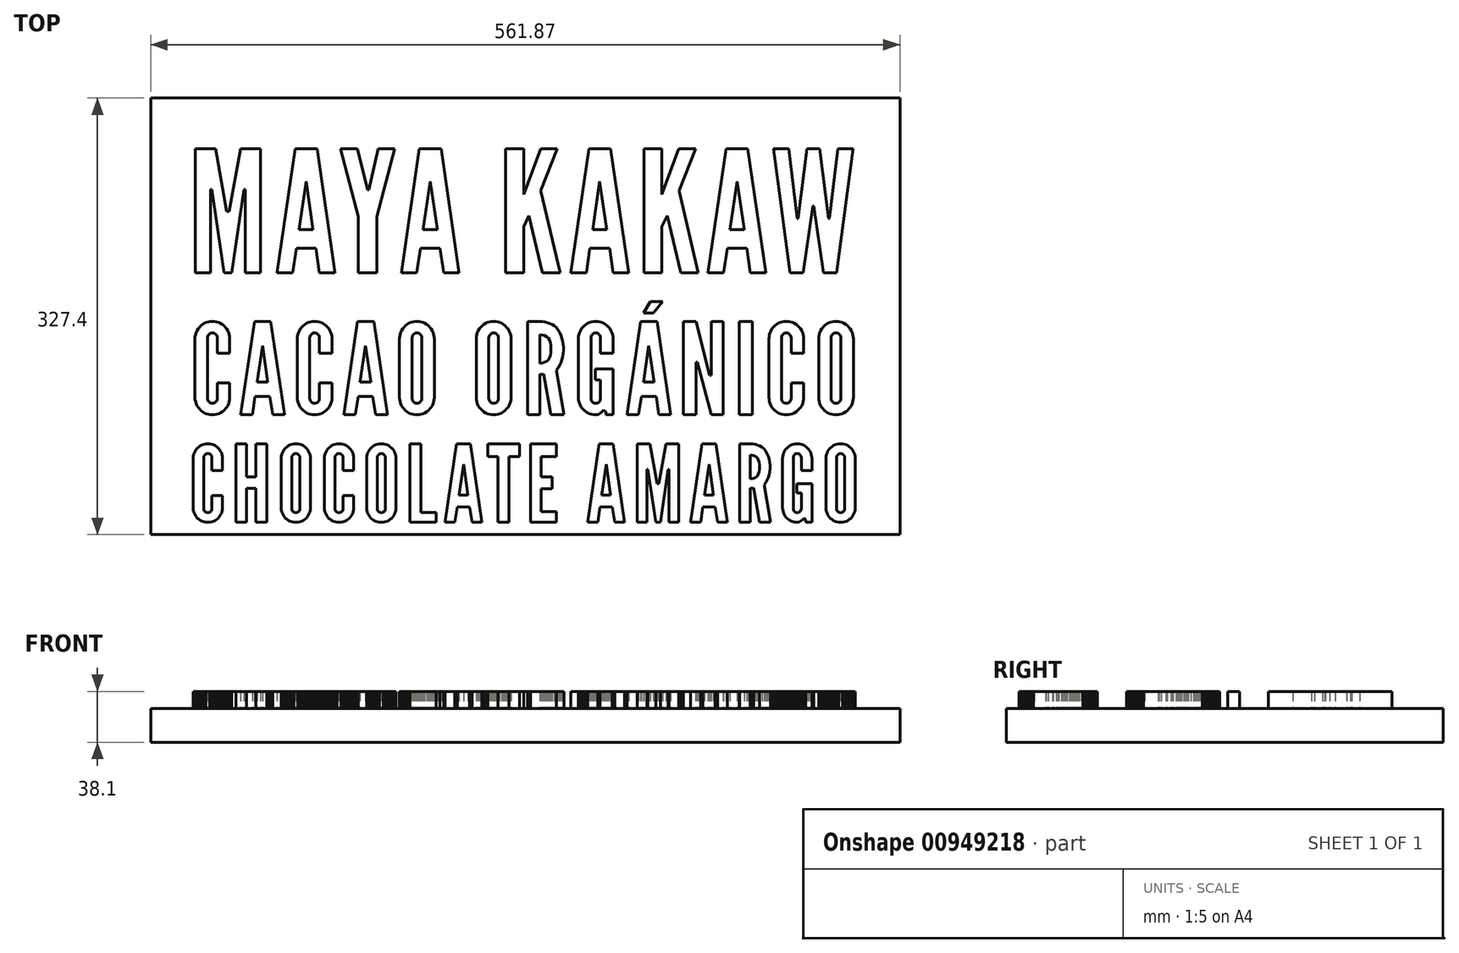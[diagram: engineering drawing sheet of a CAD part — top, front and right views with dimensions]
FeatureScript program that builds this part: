
annotation { "Feature Type Name" : "Feature", "Feature Type Description" : "" }
export const myFeature = defineFeature(function(context is Context, id is Id, definition is map)
    precondition{}
    {
        {
            var Q0;
            Q0=qCreatedBy(makeId("Top.planeOp"),FACE);
            var sketch = newSketch(context, id + "F0", { "sketchPlane" : qUnion([Q0])});
            skLineSegment(sketch, "E0", {"start": v(-116.2, -328.45) * mm, "end": v(-116.2, -376.5) * mm});
            skLineSegment(sketch, "E1", {"start": v(-116.2, -376.5) * mm, "end": v(-116.2, -377.7) * mm});
            skLineSegment(sketch, "E2", {"start": v(-116.2, -377.7) * mm, "end": v(-115.97, -378.89) * mm});
            skLineSegment(sketch, "E3", {"start": v(-115.97, -378.89) * mm, "end": v(-115.65, -379.97) * mm});
            skLineSegment(sketch, "E4", {"start": v(-115.65, -379.97) * mm, "end": v(-115.22, -381.05) * mm});
            skLineSegment(sketch, "E5", {"start": v(-115.22, -381.05) * mm, "end": v(-114.78, -382.02) * mm});
            skLineSegment(sketch, "E6", {"start": v(-114.78, -382.02) * mm, "end": v(-114.14, -383) * mm});
            skLineSegment(sketch, "E7", {"start": v(-114.14, -383) * mm, "end": v(-113.38, -383.86) * mm});
            skLineSegment(sketch, "E8", {"start": v(-113.38, -383.86) * mm, "end": v(-112.62, -384.73) * mm});
            skLineSegment(sketch, "E9", {"start": v(-112.62, -384.73) * mm, "end": v(-111.65, -385.49) * mm});
            skLineSegment(sketch, "E10", {"start": v(-111.65, -385.49) * mm, "end": v(-110.78, -386.03) * mm});
            skLineSegment(sketch, "E11", {"start": v(-110.78, -386.03) * mm, "end": v(-109.7, -386.57) * mm});
            skLineSegment(sketch, "E12", {"start": v(-109.7, -386.57) * mm, "end": v(-108.61, -387) * mm});
            skLineSegment(sketch, "E13", {"start": v(-108.61, -387) * mm, "end": v(-107.53, -387.33) * mm});
            skLineSegment(sketch, "E14", {"start": v(-107.53, -387.33) * mm, "end": v(-106.34, -387.44) * mm});
            skLineSegment(sketch, "E15", {"start": v(-106.34, -387.44) * mm, "end": v(-105.26, -387.54) * mm});
            skLineSegment(sketch, "E16", {"start": v(-105.26, -387.54) * mm, "end": v(-104.07, -387.44) * mm});
            skLineSegment(sketch, "E17", {"start": v(-104.07, -387.44) * mm, "end": v(-102.99, -387.33) * mm});
            skLineSegment(sketch, "E18", {"start": v(-102.99, -387.33) * mm, "end": v(-101.8, -387) * mm});
            skLineSegment(sketch, "E19", {"start": v(-101.8, -387) * mm, "end": v(-100.82, -386.57) * mm});
            skLineSegment(sketch, "E20", {"start": v(-100.82, -386.57) * mm, "end": v(-99.74, -386.03) * mm});
            skLineSegment(sketch, "E21", {"start": v(-99.74, -386.03) * mm, "end": v(-98.76, -385.49) * mm});
            skLineSegment(sketch, "E22", {"start": v(-98.76, -385.49) * mm, "end": v(-97.9, -384.73) * mm});
            skLineSegment(sketch, "E23", {"start": v(-97.9, -384.73) * mm, "end": v(-97.03, -383.86) * mm});
            skLineSegment(sketch, "E24", {"start": v(-97.03, -383.86) * mm, "end": v(-96.38, -383) * mm});
            skLineSegment(sketch, "E25", {"start": v(-96.38, -383) * mm, "end": v(-95.73, -382.02) * mm});
            skLineSegment(sketch, "E26", {"start": v(-95.73, -382.02) * mm, "end": v(-95.2, -381.05) * mm});
            skLineSegment(sketch, "E27", {"start": v(-95.2, -381.05) * mm, "end": v(-94.76, -379.97) * mm});
            skLineSegment(sketch, "E28", {"start": v(-94.76, -379.97) * mm, "end": v(-94.54, -378.89) * mm});
            skLineSegment(sketch, "E29", {"start": v(-94.54, -378.89) * mm, "end": v(-94.33, -377.7) * mm});
            skLineSegment(sketch, "E30", {"start": v(-94.33, -377.7) * mm, "end": v(-94.22, -376.5) * mm});
            skLineSegment(sketch, "E31", {"start": v(-94.22, -376.5) * mm, "end": v(-94.22, -328.45) * mm});
            skLineSegment(sketch, "E32", {"start": v(-94.22, -328.45) * mm, "end": v(-102.23, -328.45) * mm});
            skLineSegment(sketch, "E33", {"start": v(-102.23, -328.45) * mm, "end": v(-102.23, -377.15) * mm});
            skLineSegment(sketch, "E34", {"start": v(-108.3, -377.15) * mm, "end": v(-108.18, -377.8) * mm});
            skLineSegment(sketch, "E35", {"start": v(-108.18, -377.8) * mm, "end": v(-108.08, -378.34) * mm});
            skLineSegment(sketch, "E36", {"start": v(-108.08, -378.34) * mm, "end": v(-107.75, -378.89) * mm});
            skLineSegment(sketch, "E37", {"start": v(-107.75, -378.89) * mm, "end": v(-107.43, -379.32) * mm});
            skLineSegment(sketch, "E38", {"start": v(-107.43, -379.32) * mm, "end": v(-106.88, -379.75) * mm});
            skLineSegment(sketch, "E39", {"start": v(-106.88, -379.75) * mm, "end": v(-106.45, -379.97) * mm});
            skLineSegment(sketch, "E40", {"start": v(-106.45, -379.97) * mm, "end": v(-105.8, -380.18) * mm});
            skLineSegment(sketch, "E41", {"start": v(-105.8, -380.18) * mm, "end": v(-104.61, -380.18) * mm});
            skLineSegment(sketch, "E42", {"start": v(-104.61, -380.18) * mm, "end": v(-104.07, -379.97) * mm});
            skLineSegment(sketch, "E43", {"start": v(-104.07, -379.97) * mm, "end": v(-103.53, -379.75) * mm});
            skLineSegment(sketch, "E44", {"start": v(-103.53, -379.75) * mm, "end": v(-103.1, -379.32) * mm});
            skLineSegment(sketch, "E45", {"start": v(-103.1, -379.32) * mm, "end": v(-102.66, -378.89) * mm});
            skLineSegment(sketch, "E46", {"start": v(-102.66, -378.89) * mm, "end": v(-102.23, -377.8) * mm});
            skLineSegment(sketch, "E47", {"start": v(-102.23, -377.8) * mm, "end": v(-102.23, -377.15) * mm});
            skLineSegment(sketch, "E48", {"start": v(-108.3, -377.15) * mm, "end": v(-108.3, -328.45) * mm});
            skLineSegment(sketch, "E49", {"start": v(-108.3, -328.45) * mm, "end": v(-116.2, -328.45) * mm});
            skLineSegment(sketch, "E50", {"start": v(9.9, -341.44) * mm, "end": v(9.9, -375.1) * mm});
            skLineSegment(sketch, "E51", {"start": v(3.95, -380.3) * mm, "end": v(4.82, -380.18) * mm});
            skLineSegment(sketch, "E52", {"start": v(4.82, -380.18) * mm, "end": v(5.8, -379.97) * mm});
            skLineSegment(sketch, "E53", {"start": v(5.8, -379.97) * mm, "end": v(6.66, -379.54) * mm});
            skLineSegment(sketch, "E54", {"start": v(6.66, -379.54) * mm, "end": v(7.42, -379) * mm});
            skLineSegment(sketch, "E55", {"start": v(7.42, -379) * mm, "end": v(8.17, -378.45) * mm});
            skLineSegment(sketch, "E56", {"start": v(8.17, -378.45) * mm, "end": v(8.82, -377.7) * mm});
            skLineSegment(sketch, "E57", {"start": v(8.82, -377.7) * mm, "end": v(9.25, -376.94) * mm});
            skLineSegment(sketch, "E58", {"start": v(9.25, -376.94) * mm, "end": v(9.69, -376.07) * mm});
            skLineSegment(sketch, "E59", {"start": v(9.69, -376.07) * mm, "end": v(9.9, -375.1) * mm});
            skLineSegment(sketch, "E60", {"start": v(3.95, -380.3) * mm, "end": v(3.2, -380.3) * mm});
            skLineSegment(sketch, "E61", {"start": v(3.2, -380.3) * mm, "end": v(3.2, -336.24) * mm});
            skLineSegment(sketch, "E62", {"start": v(3.2, -336.24) * mm, "end": v(3.95, -336.24) * mm});
            skLineSegment(sketch, "E63", {"start": v(9.9, -341.44) * mm, "end": v(9.69, -340.46) * mm});
            skLineSegment(sketch, "E64", {"start": v(9.69, -340.46) * mm, "end": v(9.25, -339.6) * mm});
            skLineSegment(sketch, "E65", {"start": v(9.25, -339.6) * mm, "end": v(8.82, -338.84) * mm});
            skLineSegment(sketch, "E66", {"start": v(8.82, -338.84) * mm, "end": v(8.17, -338.08) * mm});
            skLineSegment(sketch, "E67", {"start": v(8.17, -338.08) * mm, "end": v(7.42, -337.43) * mm});
            skLineSegment(sketch, "E68", {"start": v(7.42, -337.43) * mm, "end": v(6.66, -337) * mm});
            skLineSegment(sketch, "E69", {"start": v(6.66, -337) * mm, "end": v(5.8, -336.56) * mm});
            skLineSegment(sketch, "E70", {"start": v(5.8, -336.56) * mm, "end": v(4.82, -336.35) * mm});
            skLineSegment(sketch, "E71", {"start": v(4.82, -336.35) * mm, "end": v(3.95, -336.24) * mm});
            skLineSegment(sketch, "E72", {"start": v(-5.36, -328.45) * mm, "end": v(-5.36, -387.98) * mm});
            skLineSegment(sketch, "E73", {"start": v(-5.36, -387.98) * mm, "end": v(8.6, -387.98) * mm});
            skLineSegment(sketch, "E74", {"start": v(8.6, -387.98) * mm, "end": v(9.9, -387.44) * mm});
            skLineSegment(sketch, "E75", {"start": v(9.9, -387.44) * mm, "end": v(11.2, -386.79) * mm});
            skLineSegment(sketch, "E76", {"start": v(11.2, -386.79) * mm, "end": v(12.4, -386.03) * mm});
            skLineSegment(sketch, "E77", {"start": v(12.4, -386.03) * mm, "end": v(13.48, -385.16) * mm});
            skLineSegment(sketch, "E78", {"start": v(13.48, -385.16) * mm, "end": v(14.45, -384.19) * mm});
            skLineSegment(sketch, "E79", {"start": v(14.45, -384.19) * mm, "end": v(15.42, -383.1) * mm});
            skLineSegment(sketch, "E80", {"start": v(15.42, -383.1) * mm, "end": v(16.3, -382.02) * mm});
            skLineSegment(sketch, "E81", {"start": v(16.3, -382.02) * mm, "end": v(16.94, -380.73) * mm});
            skLineSegment(sketch, "E82", {"start": v(16.94, -380.73) * mm, "end": v(17.59, -379.54) * mm});
            skLineSegment(sketch, "E83", {"start": v(17.59, -379.54) * mm, "end": v(18.13, -378.13) * mm});
            skLineSegment(sketch, "E84", {"start": v(18.13, -378.13) * mm, "end": v(18.46, -376.83) * mm});
            skLineSegment(sketch, "E85", {"start": v(18.46, -376.83) * mm, "end": v(18.46, -339.7) * mm});
            skLineSegment(sketch, "E86", {"start": v(18.46, -339.7) * mm, "end": v(18.13, -338.3) * mm});
            skLineSegment(sketch, "E87", {"start": v(18.13, -338.3) * mm, "end": v(17.59, -337) * mm});
            skLineSegment(sketch, "E88", {"start": v(17.59, -337) * mm, "end": v(16.94, -335.7) * mm});
            skLineSegment(sketch, "E89", {"start": v(16.94, -335.7) * mm, "end": v(16.3, -334.5) * mm});
            skLineSegment(sketch, "E90", {"start": v(16.3, -334.5) * mm, "end": v(15.42, -333.43) * mm});
            skLineSegment(sketch, "E91", {"start": v(15.42, -333.43) * mm, "end": v(14.45, -332.34) * mm});
            skLineSegment(sketch, "E92", {"start": v(14.45, -332.34) * mm, "end": v(13.48, -331.37) * mm});
            skLineSegment(sketch, "E93", {"start": v(13.48, -331.37) * mm, "end": v(12.4, -330.5) * mm});
            skLineSegment(sketch, "E94", {"start": v(12.4, -330.5) * mm, "end": v(11.2, -329.75) * mm});
            skLineSegment(sketch, "E95", {"start": v(11.2, -329.75) * mm, "end": v(9.9, -329.1) * mm});
            skLineSegment(sketch, "E96", {"start": v(9.9, -329.1) * mm, "end": v(8.6, -328.45) * mm});
            skLineSegment(sketch, "E97", {"start": v(8.6, -328.45) * mm, "end": v(-5.36, -328.45) * mm});
            skLineSegment(sketch, "E98", {"start": v(-135.57, -338.84) * mm, "end": v(-135.57, -377.15) * mm});
            skLineSegment(sketch, "E99", {"start": v(-141.63, -377.15) * mm, "end": v(-141.63, -377.8) * mm});
            skLineSegment(sketch, "E100", {"start": v(-141.63, -377.8) * mm, "end": v(-141.41, -378.34) * mm});
            skLineSegment(sketch, "E101", {"start": v(-141.41, -378.34) * mm, "end": v(-141.09, -378.89) * mm});
            skLineSegment(sketch, "E102", {"start": v(-141.09, -378.89) * mm, "end": v(-140.76, -379.32) * mm});
            skLineSegment(sketch, "E103", {"start": v(-140.76, -379.32) * mm, "end": v(-140.33, -379.75) * mm});
            skLineSegment(sketch, "E104", {"start": v(-140.33, -379.75) * mm, "end": v(-139.79, -379.97) * mm});
            skLineSegment(sketch, "E105", {"start": v(-139.79, -379.97) * mm, "end": v(-139.14, -380.18) * mm});
            skLineSegment(sketch, "E106", {"start": v(-139.14, -380.18) * mm, "end": v(-137.95, -380.18) * mm});
            skLineSegment(sketch, "E107", {"start": v(-137.95, -380.18) * mm, "end": v(-136.86, -379.75) * mm});
            skLineSegment(sketch, "E108", {"start": v(-136.86, -379.75) * mm, "end": v(-136, -378.89) * mm});
            skLineSegment(sketch, "E109", {"start": v(-136, -378.89) * mm, "end": v(-135.57, -377.8) * mm});
            skLineSegment(sketch, "E110", {"start": v(-135.57, -377.8) * mm, "end": v(-135.57, -377.15) * mm});
            skLineSegment(sketch, "E111", {"start": v(-141.63, -377.15) * mm, "end": v(-141.63, -338.84) * mm});
            skLineSegment(sketch, "E112", {"start": v(-135.57, -338.84) * mm, "end": v(-135.57, -338.3) * mm});
            skLineSegment(sketch, "E113", {"start": v(-135.57, -338.3) * mm, "end": v(-135.78, -337.65) * mm});
            skLineSegment(sketch, "E114", {"start": v(-135.78, -337.65) * mm, "end": v(-136, -337.21) * mm});
            skLineSegment(sketch, "E115", {"start": v(-136, -337.21) * mm, "end": v(-136.43, -336.67) * mm});
            skLineSegment(sketch, "E116", {"start": v(-136.43, -336.67) * mm, "end": v(-136.86, -336.35) * mm});
            skLineSegment(sketch, "E117", {"start": v(-136.86, -336.35) * mm, "end": v(-137.4, -336.02) * mm});
            skLineSegment(sketch, "E118", {"start": v(-137.4, -336.02) * mm, "end": v(-137.95, -335.91) * mm});
            skLineSegment(sketch, "E119", {"start": v(-137.95, -335.91) * mm, "end": v(-138.6, -335.8) * mm});
            skLineSegment(sketch, "E120", {"start": v(-138.6, -335.8) * mm, "end": v(-139.14, -335.91) * mm});
            skLineSegment(sketch, "E121", {"start": v(-139.14, -335.91) * mm, "end": v(-139.79, -336.02) * mm});
            skLineSegment(sketch, "E122", {"start": v(-139.79, -336.02) * mm, "end": v(-140.33, -336.35) * mm});
            skLineSegment(sketch, "E123", {"start": v(-140.33, -336.35) * mm, "end": v(-140.76, -336.67) * mm});
            skLineSegment(sketch, "E124", {"start": v(-140.76, -336.67) * mm, "end": v(-141.09, -337.21) * mm});
            skLineSegment(sketch, "E125", {"start": v(-141.09, -337.21) * mm, "end": v(-141.41, -337.65) * mm});
            skLineSegment(sketch, "E126", {"start": v(-141.41, -337.65) * mm, "end": v(-141.63, -338.3) * mm});
            skLineSegment(sketch, "E127", {"start": v(-141.63, -338.3) * mm, "end": v(-141.63, -338.84) * mm});
            skLineSegment(sketch, "E128", {"start": v(-149.53, -376.5) * mm, "end": v(-149.53, -339.49) * mm});
            skLineSegment(sketch, "E129", {"start": v(-127.55, -339.49) * mm, "end": v(-127.66, -338.3) * mm});
            skLineSegment(sketch, "E130", {"start": v(-127.66, -338.3) * mm, "end": v(-128.1, -336.13) * mm});
            skLineSegment(sketch, "E131", {"start": v(-128.1, -336.13) * mm, "end": v(-128.53, -335.05) * mm});
            skLineSegment(sketch, "E132", {"start": v(-128.53, -335.05) * mm, "end": v(-129.07, -333.97) * mm});
            skLineSegment(sketch, "E133", {"start": v(-129.07, -333.97) * mm, "end": v(-129.72, -333) * mm});
            skLineSegment(sketch, "E134", {"start": v(-129.72, -333) * mm, "end": v(-130.48, -332.13) * mm});
            skLineSegment(sketch, "E135", {"start": v(-130.48, -332.13) * mm, "end": v(-131.24, -331.37) * mm});
            skLineSegment(sketch, "E136", {"start": v(-131.24, -331.37) * mm, "end": v(-132.1, -330.61) * mm});
            skLineSegment(sketch, "E137", {"start": v(-132.1, -330.61) * mm, "end": v(-133.08, -329.96) * mm});
            skLineSegment(sketch, "E138", {"start": v(-133.08, -329.96) * mm, "end": v(-134.16, -329.42) * mm});
            skLineSegment(sketch, "E139", {"start": v(-134.16, -329.42) * mm, "end": v(-135.24, -328.99) * mm});
            skLineSegment(sketch, "E140", {"start": v(-135.24, -328.99) * mm, "end": v(-136.33, -328.77) * mm});
            skLineSegment(sketch, "E141", {"start": v(-136.33, -328.77) * mm, "end": v(-137.4, -328.56) * mm});
            skLineSegment(sketch, "E142", {"start": v(-137.4, -328.56) * mm, "end": v(-138.6, -328.45) * mm});
            skLineSegment(sketch, "E143", {"start": v(-138.6, -328.45) * mm, "end": v(-139.79, -328.56) * mm});
            skLineSegment(sketch, "E144", {"start": v(-139.79, -328.56) * mm, "end": v(-140.87, -328.77) * mm});
            skLineSegment(sketch, "E145", {"start": v(-140.87, -328.77) * mm, "end": v(-141.95, -328.99) * mm});
            skLineSegment(sketch, "E146", {"start": v(-141.95, -328.99) * mm, "end": v(-143.03, -329.42) * mm});
            skLineSegment(sketch, "E147", {"start": v(-143.03, -329.42) * mm, "end": v(-144.12, -329.96) * mm});
            skLineSegment(sketch, "E148", {"start": v(-144.12, -329.96) * mm, "end": v(-145.1, -330.61) * mm});
            skLineSegment(sketch, "E149", {"start": v(-145.1, -330.61) * mm, "end": v(-145.96, -331.37) * mm});
            skLineSegment(sketch, "E150", {"start": v(-145.96, -331.37) * mm, "end": v(-146.71, -332.13) * mm});
            skLineSegment(sketch, "E151", {"start": v(-146.71, -332.13) * mm, "end": v(-147.47, -333) * mm});
            skLineSegment(sketch, "E152", {"start": v(-147.47, -333) * mm, "end": v(-148.12, -333.97) * mm});
            skLineSegment(sketch, "E153", {"start": v(-148.12, -333.97) * mm, "end": v(-148.66, -335.05) * mm});
            skLineSegment(sketch, "E154", {"start": v(-148.66, -335.05) * mm, "end": v(-148.99, -336.13) * mm});
            skLineSegment(sketch, "E155", {"start": v(-148.99, -336.13) * mm, "end": v(-149.31, -337.21) * mm});
            skLineSegment(sketch, "E156", {"start": v(-149.31, -337.21) * mm, "end": v(-149.53, -338.3) * mm});
            skLineSegment(sketch, "E157", {"start": v(-149.53, -338.3) * mm, "end": v(-149.53, -339.49) * mm});
            skLineSegment(sketch, "E158", {"start": v(-127.55, -339.49) * mm, "end": v(-127.55, -376.5) * mm});
            skLineSegment(sketch, "E159", {"start": v(-129.29, -382.35) * mm, "end": v(-128.64, -381.27) * mm});
            skLineSegment(sketch, "E160", {"start": v(-128.64, -381.27) * mm, "end": v(-128.2, -380.08) * mm});
            skLineSegment(sketch, "E161", {"start": v(-128.2, -380.08) * mm, "end": v(-127.88, -379) * mm});
            skLineSegment(sketch, "E162", {"start": v(-127.88, -379) * mm, "end": v(-127.66, -377.8) * mm});
            skLineSegment(sketch, "E163", {"start": v(-127.66, -377.8) * mm, "end": v(-127.55, -376.5) * mm});
            skLineSegment(sketch, "E164", {"start": v(-129.29, -382.35) * mm, "end": v(-128.2, -383.43) * mm});
            skLineSegment(sketch, "E165", {"start": v(-128.2, -383.43) * mm, "end": v(-127.55, -383.97) * mm});
            skLineSegment(sketch, "E166", {"start": v(-127.55, -383.97) * mm, "end": v(-126.8, -384.3) * mm});
            skLineSegment(sketch, "E167", {"start": v(-126.8, -384.3) * mm, "end": v(-126.04, -384.51) * mm});
            skLineSegment(sketch, "E168", {"start": v(-126.04, -384.51) * mm, "end": v(-126.04, -391.55) * mm});
            skLineSegment(sketch, "E169", {"start": v(-134.05, -386.57) * mm, "end": v(-133.4, -387.44) * mm});
            skLineSegment(sketch, "E170", {"start": v(-133.4, -387.44) * mm, "end": v(-132.75, -388.3) * mm});
            skLineSegment(sketch, "E171", {"start": v(-132.75, -388.3) * mm, "end": v(-131.89, -389.06) * mm});
            skLineSegment(sketch, "E172", {"start": v(-131.89, -389.06) * mm, "end": v(-131.13, -389.7) * mm});
            skLineSegment(sketch, "E173", {"start": v(-131.13, -389.7) * mm, "end": v(-130.16, -390.25) * mm});
            skLineSegment(sketch, "E174", {"start": v(-130.16, -390.25) * mm, "end": v(-129.18, -390.8) * mm});
            skLineSegment(sketch, "E175", {"start": v(-129.18, -390.8) * mm, "end": v(-128.2, -391.12) * mm});
            skLineSegment(sketch, "E176", {"start": v(-128.2, -391.12) * mm, "end": v(-127.12, -391.33) * mm});
            skLineSegment(sketch, "E177", {"start": v(-127.12, -391.33) * mm, "end": v(-126.04, -391.55) * mm});
            skLineSegment(sketch, "E178", {"start": v(-149.53, -376.5) * mm, "end": v(-149.53, -377.7) * mm});
            skLineSegment(sketch, "E179", {"start": v(-149.53, -377.7) * mm, "end": v(-149.31, -378.89) * mm});
            skLineSegment(sketch, "E180", {"start": v(-149.31, -378.89) * mm, "end": v(-148.99, -379.97) * mm});
            skLineSegment(sketch, "E181", {"start": v(-148.99, -379.97) * mm, "end": v(-148.66, -381.05) * mm});
            skLineSegment(sketch, "E182", {"start": v(-148.66, -381.05) * mm, "end": v(-148.12, -382.02) * mm});
            skLineSegment(sketch, "E183", {"start": v(-148.12, -382.02) * mm, "end": v(-147.47, -383) * mm});
            skLineSegment(sketch, "E184", {"start": v(-147.47, -383) * mm, "end": v(-146.71, -383.97) * mm});
            skLineSegment(sketch, "E185", {"start": v(-146.71, -383.97) * mm, "end": v(-145.85, -384.73) * mm});
            skLineSegment(sketch, "E186", {"start": v(-145.85, -384.73) * mm, "end": v(-144.98, -385.49) * mm});
            skLineSegment(sketch, "E187", {"start": v(-144.98, -385.49) * mm, "end": v(-144, -386.14) * mm});
            skLineSegment(sketch, "E188", {"start": v(-144, -386.14) * mm, "end": v(-143.03, -386.57) * mm});
            skLineSegment(sketch, "E189", {"start": v(-143.03, -386.57) * mm, "end": v(-141.95, -387) * mm});
            skLineSegment(sketch, "E190", {"start": v(-141.95, -387) * mm, "end": v(-140.76, -387.33) * mm});
            skLineSegment(sketch, "E191", {"start": v(-140.76, -387.33) * mm, "end": v(-139.68, -387.44) * mm});
            skLineSegment(sketch, "E192", {"start": v(-139.68, -387.44) * mm, "end": v(-138.49, -387.54) * mm});
            skLineSegment(sketch, "E193", {"start": v(-138.49, -387.54) * mm, "end": v(-137.3, -387.44) * mm});
            skLineSegment(sketch, "E194", {"start": v(-137.3, -387.44) * mm, "end": v(-136.22, -387.33) * mm});
            skLineSegment(sketch, "E195", {"start": v(-136.22, -387.33) * mm, "end": v(-135.13, -387) * mm});
            skLineSegment(sketch, "E196", {"start": v(-135.13, -387) * mm, "end": v(-134.05, -386.57) * mm});
            skLineSegment(sketch, "E197", {"start": v(-167.06, -338.84) * mm, "end": v(-167.06, -343.7) * mm});
            skLineSegment(sketch, "E198", {"start": v(-167.06, -343.7) * mm, "end": v(-159.16, -343.7) * mm});
            skLineSegment(sketch, "E199", {"start": v(-159.16, -343.7) * mm, "end": v(-159.16, -339.49) * mm});
            skLineSegment(sketch, "E200", {"start": v(-159.16, -339.49) * mm, "end": v(-159.16, -338.3) * mm});
            skLineSegment(sketch, "E201", {"start": v(-159.16, -338.3) * mm, "end": v(-159.38, -337.21) * mm});
            skLineSegment(sketch, "E202", {"start": v(-159.38, -337.21) * mm, "end": v(-159.7, -336.13) * mm});
            skLineSegment(sketch, "E203", {"start": v(-159.7, -336.13) * mm, "end": v(-160.03, -335.05) * mm});
            skLineSegment(sketch, "E204", {"start": v(-160.03, -335.05) * mm, "end": v(-160.57, -333.97) * mm});
            skLineSegment(sketch, "E205", {"start": v(-160.57, -333.97) * mm, "end": v(-161.22, -333) * mm});
            skLineSegment(sketch, "E206", {"start": v(-161.22, -333) * mm, "end": v(-161.97, -332.13) * mm});
            skLineSegment(sketch, "E207", {"start": v(-161.97, -332.13) * mm, "end": v(-162.73, -331.37) * mm});
            skLineSegment(sketch, "E208", {"start": v(-162.73, -331.37) * mm, "end": v(-163.7, -330.61) * mm});
            skLineSegment(sketch, "E209", {"start": v(-163.7, -330.61) * mm, "end": v(-164.58, -329.96) * mm});
            skLineSegment(sketch, "E210", {"start": v(-164.58, -329.96) * mm, "end": v(-165.65, -329.42) * mm});
            skLineSegment(sketch, "E211", {"start": v(-165.65, -329.42) * mm, "end": v(-166.74, -328.99) * mm});
            skLineSegment(sketch, "E212", {"start": v(-166.74, -328.99) * mm, "end": v(-167.82, -328.77) * mm});
            skLineSegment(sketch, "E213", {"start": v(-167.82, -328.77) * mm, "end": v(-169.01, -328.56) * mm});
            skLineSegment(sketch, "E214", {"start": v(-169.01, -328.56) * mm, "end": v(-170.1, -328.45) * mm});
            skLineSegment(sketch, "E215", {"start": v(-170.1, -328.45) * mm, "end": v(-171.28, -328.56) * mm});
            skLineSegment(sketch, "E216", {"start": v(-171.28, -328.56) * mm, "end": v(-172.37, -328.77) * mm});
            skLineSegment(sketch, "E217", {"start": v(-172.37, -328.77) * mm, "end": v(-173.45, -328.99) * mm});
            skLineSegment(sketch, "E218", {"start": v(-173.45, -328.99) * mm, "end": v(-174.53, -329.42) * mm});
            skLineSegment(sketch, "E219", {"start": v(-174.53, -329.42) * mm, "end": v(-175.61, -329.96) * mm});
            skLineSegment(sketch, "E220", {"start": v(-175.61, -329.96) * mm, "end": v(-176.59, -330.61) * mm});
            skLineSegment(sketch, "E221", {"start": v(-176.59, -330.61) * mm, "end": v(-177.46, -331.37) * mm});
            skLineSegment(sketch, "E222", {"start": v(-177.46, -331.37) * mm, "end": v(-178.32, -332.13) * mm});
            skLineSegment(sketch, "E223", {"start": v(-178.32, -332.13) * mm, "end": v(-178.97, -333) * mm});
            skLineSegment(sketch, "E224", {"start": v(-178.97, -333) * mm, "end": v(-179.62, -333.97) * mm});
            skLineSegment(sketch, "E225", {"start": v(-179.62, -333.97) * mm, "end": v(-180.16, -335.05) * mm});
            skLineSegment(sketch, "E226", {"start": v(-180.16, -335.05) * mm, "end": v(-180.6, -336.13) * mm});
            skLineSegment(sketch, "E227", {"start": v(-180.6, -336.13) * mm, "end": v(-180.8, -337.21) * mm});
            skLineSegment(sketch, "E228", {"start": v(-180.8, -337.21) * mm, "end": v(-181.03, -338.3) * mm});
            skLineSegment(sketch, "E229", {"start": v(-181.03, -338.3) * mm, "end": v(-181.13, -339.49) * mm});
            skLineSegment(sketch, "E230", {"start": v(-181.13, -339.49) * mm, "end": v(-181.13, -343.7) * mm});
            skLineSegment(sketch, "E231", {"start": v(-181.13, -343.7) * mm, "end": v(-180.38, -346.09) * mm});
            skLineSegment(sketch, "E232", {"start": v(-180.38, -346.09) * mm, "end": v(-179.51, -348.36) * mm});
            skLineSegment(sketch, "E233", {"start": v(-179.51, -348.36) * mm, "end": v(-178.54, -350.63) * mm});
            skLineSegment(sketch, "E234", {"start": v(-178.54, -350.63) * mm, "end": v(-177.46, -352.8) * mm});
            skLineSegment(sketch, "E235", {"start": v(-177.46, -352.8) * mm, "end": v(-176.26, -354.96) * mm});
            skLineSegment(sketch, "E236", {"start": v(-176.26, -354.96) * mm, "end": v(-174.86, -357.02) * mm});
            skLineSegment(sketch, "E237", {"start": v(-174.86, -357.02) * mm, "end": v(-173.34, -358.97) * mm});
            skLineSegment(sketch, "E238", {"start": v(-166.52, -370.66) * mm, "end": v(-168.69, -366.65) * mm});
            skLineSegment(sketch, "E239", {"start": v(-168.69, -366.65) * mm, "end": v(-170.96, -362.87) * mm});
            skLineSegment(sketch, "E240", {"start": v(-170.96, -362.87) * mm, "end": v(-173.34, -358.97) * mm});
            skLineSegment(sketch, "E241", {"start": v(-166.52, -370.66) * mm, "end": v(-166.52, -376.18) * mm});
            skLineSegment(sketch, "E242", {"start": v(-174.53, -377.15) * mm, "end": v(-174.31, -377.8) * mm});
            skLineSegment(sketch, "E243", {"start": v(-174.31, -377.8) * mm, "end": v(-174, -378.45) * mm});
            skLineSegment(sketch, "E244", {"start": v(-174, -378.45) * mm, "end": v(-173.56, -379) * mm});
            skLineSegment(sketch, "E245", {"start": v(-173.56, -379) * mm, "end": v(-173.02, -379.43) * mm});
            skLineSegment(sketch, "E246", {"start": v(-173.02, -379.43) * mm, "end": v(-172.47, -379.86) * mm});
            skLineSegment(sketch, "E247", {"start": v(-172.47, -379.86) * mm, "end": v(-171.82, -380.08) * mm});
            skLineSegment(sketch, "E248", {"start": v(-171.82, -380.08) * mm, "end": v(-171.07, -380.3) * mm});
            skLineSegment(sketch, "E249", {"start": v(-171.07, -380.3) * mm, "end": v(-170.42, -380.3) * mm});
            skLineSegment(sketch, "E250", {"start": v(-170.42, -380.3) * mm, "end": v(-169.77, -380.18) * mm});
            skLineSegment(sketch, "E251", {"start": v(-169.77, -380.18) * mm, "end": v(-169.01, -379.97) * mm});
            skLineSegment(sketch, "E252", {"start": v(-169.01, -379.97) * mm, "end": v(-168.47, -379.75) * mm});
            skLineSegment(sketch, "E253", {"start": v(-168.47, -379.75) * mm, "end": v(-167.82, -379.32) * mm});
            skLineSegment(sketch, "E254", {"start": v(-167.82, -379.32) * mm, "end": v(-167.39, -378.78) * mm});
            skLineSegment(sketch, "E255", {"start": v(-167.39, -378.78) * mm, "end": v(-166.96, -378.23) * mm});
            skLineSegment(sketch, "E256", {"start": v(-166.96, -378.23) * mm, "end": v(-166.74, -377.59) * mm});
            skLineSegment(sketch, "E257", {"start": v(-166.74, -377.59) * mm, "end": v(-166.52, -376.94) * mm});
            skLineSegment(sketch, "E258", {"start": v(-166.52, -376.94) * mm, "end": v(-166.52, -376.18) * mm});
            skLineSegment(sketch, "E259", {"start": v(-174.53, -377.15) * mm, "end": v(-174.53, -370.66) * mm});
            skLineSegment(sketch, "E260", {"start": v(-174.53, -370.66) * mm, "end": v(-182.32, -370.66) * mm});
            skLineSegment(sketch, "E261", {"start": v(-182.32, -370.66) * mm, "end": v(-182.32, -376.5) * mm});
            skLineSegment(sketch, "E262", {"start": v(-182.32, -376.5) * mm, "end": v(-182.22, -377.8) * mm});
            skLineSegment(sketch, "E263", {"start": v(-182.22, -377.8) * mm, "end": v(-182, -379) * mm});
            skLineSegment(sketch, "E264", {"start": v(-182, -379) * mm, "end": v(-181.57, -380.08) * mm});
            skLineSegment(sketch, "E265", {"start": v(-181.57, -380.08) * mm, "end": v(-181.13, -381.27) * mm});
            skLineSegment(sketch, "E266", {"start": v(-181.13, -381.27) * mm, "end": v(-180.49, -382.24) * mm});
            skLineSegment(sketch, "E267", {"start": v(-180.49, -382.24) * mm, "end": v(-179.73, -383.21) * mm});
            skLineSegment(sketch, "E268", {"start": v(-179.73, -383.21) * mm, "end": v(-178.97, -384.19) * mm});
            skLineSegment(sketch, "E269", {"start": v(-178.97, -384.19) * mm, "end": v(-178.1, -384.95) * mm});
            skLineSegment(sketch, "E270", {"start": v(-178.1, -384.95) * mm, "end": v(-177.02, -385.7) * mm});
            skLineSegment(sketch, "E271", {"start": v(-177.02, -385.7) * mm, "end": v(-176.05, -386.25) * mm});
            skLineSegment(sketch, "E272", {"start": v(-176.05, -386.25) * mm, "end": v(-174.86, -386.79) * mm});
            skLineSegment(sketch, "E273", {"start": v(-174.86, -386.79) * mm, "end": v(-173.78, -387.11) * mm});
            skLineSegment(sketch, "E274", {"start": v(-173.78, -387.11) * mm, "end": v(-172.58, -387.44) * mm});
            skLineSegment(sketch, "E275", {"start": v(-172.58, -387.44) * mm, "end": v(-171.4, -387.54) * mm});
            skLineSegment(sketch, "E276", {"start": v(-171.4, -387.54) * mm, "end": v(-170.1, -387.54) * mm});
            skLineSegment(sketch, "E277", {"start": v(-170.1, -387.54) * mm, "end": v(-168.9, -387.44) * mm});
            skLineSegment(sketch, "E278", {"start": v(-168.9, -387.44) * mm, "end": v(-167.71, -387.11) * mm});
            skLineSegment(sketch, "E279", {"start": v(-167.71, -387.11) * mm, "end": v(-166.63, -386.79) * mm});
            skLineSegment(sketch, "E280", {"start": v(-166.63, -386.79) * mm, "end": v(-165.44, -386.25) * mm});
            skLineSegment(sketch, "E281", {"start": v(-165.44, -386.25) * mm, "end": v(-164.47, -385.7) * mm});
            skLineSegment(sketch, "E282", {"start": v(-164.47, -385.7) * mm, "end": v(-163.38, -384.95) * mm});
            skLineSegment(sketch, "E283", {"start": v(-163.38, -384.95) * mm, "end": v(-162.52, -384.19) * mm});
            skLineSegment(sketch, "E284", {"start": v(-162.52, -384.19) * mm, "end": v(-161.76, -383.21) * mm});
            skLineSegment(sketch, "E285", {"start": v(-161.76, -383.21) * mm, "end": v(-161, -382.24) * mm});
            skLineSegment(sketch, "E286", {"start": v(-161, -382.24) * mm, "end": v(-160.35, -381.27) * mm});
            skLineSegment(sketch, "E287", {"start": v(-160.35, -381.27) * mm, "end": v(-159.92, -380.08) * mm});
            skLineSegment(sketch, "E288", {"start": v(-159.92, -380.08) * mm, "end": v(-159.49, -379) * mm});
            skLineSegment(sketch, "E289", {"start": v(-159.49, -379) * mm, "end": v(-159.27, -377.8) * mm});
            skLineSegment(sketch, "E290", {"start": v(-159.27, -377.8) * mm, "end": v(-159.16, -376.5) * mm});
            skLineSegment(sketch, "E291", {"start": v(-159.16, -376.5) * mm, "end": v(-159.16, -370.66) * mm});
            skLineSegment(sketch, "E292", {"start": v(-159.16, -370.66) * mm, "end": v(-159.81, -368.06) * mm});
            skLineSegment(sketch, "E293", {"start": v(-159.81, -368.06) * mm, "end": v(-160.79, -365.57) * mm});
            skLineSegment(sketch, "E294", {"start": v(-160.79, -365.57) * mm, "end": v(-161.76, -363.2) * mm});
            skLineSegment(sketch, "E295", {"start": v(-161.76, -363.2) * mm, "end": v(-162.84, -360.8) * mm});
            skLineSegment(sketch, "E296", {"start": v(-162.84, -360.8) * mm, "end": v(-164.14, -358.54) * mm});
            skLineSegment(sketch, "E297", {"start": v(-164.14, -358.54) * mm, "end": v(-165.55, -356.37) * mm});
            skLineSegment(sketch, "E298", {"start": v(-165.55, -356.37) * mm, "end": v(-167.06, -354.2) * mm});
            skLineSegment(sketch, "E299", {"start": v(-173.12, -343.7) * mm, "end": v(-172.15, -345.87) * mm});
            skLineSegment(sketch, "E300", {"start": v(-172.15, -345.87) * mm, "end": v(-171.07, -348.04) * mm});
            skLineSegment(sketch, "E301", {"start": v(-171.07, -348.04) * mm, "end": v(-169.77, -350.2) * mm});
            skLineSegment(sketch, "E302", {"start": v(-169.77, -350.2) * mm, "end": v(-168.47, -352.26) * mm});
            skLineSegment(sketch, "E303", {"start": v(-168.47, -352.26) * mm, "end": v(-167.06, -354.2) * mm});
            skLineSegment(sketch, "E304", {"start": v(-173.12, -343.7) * mm, "end": v(-173.12, -338.84) * mm});
            skLineSegment(sketch, "E305", {"start": v(-167.06, -338.84) * mm, "end": v(-167.06, -338.3) * mm});
            skLineSegment(sketch, "E306", {"start": v(-167.06, -338.3) * mm, "end": v(-167.28, -337.65) * mm});
            skLineSegment(sketch, "E307", {"start": v(-167.28, -337.65) * mm, "end": v(-167.6, -337.21) * mm});
            skLineSegment(sketch, "E308", {"start": v(-167.6, -337.21) * mm, "end": v(-167.93, -336.67) * mm});
            skLineSegment(sketch, "E309", {"start": v(-167.93, -336.67) * mm, "end": v(-168.36, -336.35) * mm});
            skLineSegment(sketch, "E310", {"start": v(-168.36, -336.35) * mm, "end": v(-168.9, -336.02) * mm});
            skLineSegment(sketch, "E311", {"start": v(-168.9, -336.02) * mm, "end": v(-169.55, -335.91) * mm});
            skLineSegment(sketch, "E312", {"start": v(-169.55, -335.91) * mm, "end": v(-170.1, -335.8) * mm});
            skLineSegment(sketch, "E313", {"start": v(-170.1, -335.8) * mm, "end": v(-170.74, -335.91) * mm});
            skLineSegment(sketch, "E314", {"start": v(-170.74, -335.91) * mm, "end": v(-171.28, -336.02) * mm});
            skLineSegment(sketch, "E315", {"start": v(-171.28, -336.02) * mm, "end": v(-171.82, -336.35) * mm});
            skLineSegment(sketch, "E316", {"start": v(-171.82, -336.35) * mm, "end": v(-172.26, -336.67) * mm});
            skLineSegment(sketch, "E317", {"start": v(-172.26, -336.67) * mm, "end": v(-172.7, -337.21) * mm});
            skLineSegment(sketch, "E318", {"start": v(-172.7, -337.21) * mm, "end": v(-172.9, -337.65) * mm});
            skLineSegment(sketch, "E319", {"start": v(-172.9, -337.65) * mm, "end": v(-173.12, -338.3) * mm});
            skLineSegment(sketch, "E320", {"start": v(-173.12, -338.3) * mm, "end": v(-173.12, -338.84) * mm});
            skLineSegment(sketch, "E321", {"start": v(-39.34, -338.84) * mm, "end": v(-39.34, -343.7) * mm});
            skLineSegment(sketch, "E322", {"start": v(-39.34, -343.7) * mm, "end": v(-31.44, -343.7) * mm});
            skLineSegment(sketch, "E323", {"start": v(-31.44, -343.7) * mm, "end": v(-31.44, -339.49) * mm});
            skLineSegment(sketch, "E324", {"start": v(-31.44, -339.49) * mm, "end": v(-31.55, -338.3) * mm});
            skLineSegment(sketch, "E325", {"start": v(-31.55, -338.3) * mm, "end": v(-31.66, -337.21) * mm});
            skLineSegment(sketch, "E326", {"start": v(-31.66, -337.21) * mm, "end": v(-31.98, -336.13) * mm});
            skLineSegment(sketch, "E327", {"start": v(-31.98, -336.13) * mm, "end": v(-32.42, -335.05) * mm});
            skLineSegment(sketch, "E328", {"start": v(-32.42, -335.05) * mm, "end": v(-32.96, -333.97) * mm});
            skLineSegment(sketch, "E329", {"start": v(-32.96, -333.97) * mm, "end": v(-33.6, -333) * mm});
            skLineSegment(sketch, "E330", {"start": v(-33.6, -333) * mm, "end": v(-34.26, -332.13) * mm});
            skLineSegment(sketch, "E331", {"start": v(-34.26, -332.13) * mm, "end": v(-35.12, -331.37) * mm});
            skLineSegment(sketch, "E332", {"start": v(-35.12, -331.37) * mm, "end": v(-35.99, -330.61) * mm});
            skLineSegment(sketch, "E333", {"start": v(-35.99, -330.61) * mm, "end": v(-36.96, -329.96) * mm});
            skLineSegment(sketch, "E334", {"start": v(-36.96, -329.96) * mm, "end": v(-37.94, -329.42) * mm});
            skLineSegment(sketch, "E335", {"start": v(-37.94, -329.42) * mm, "end": v(-39.02, -328.99) * mm});
            skLineSegment(sketch, "E336", {"start": v(-39.02, -328.99) * mm, "end": v(-40.2, -328.77) * mm});
            skLineSegment(sketch, "E337", {"start": v(-40.2, -328.77) * mm, "end": v(-41.3, -328.56) * mm});
            skLineSegment(sketch, "E338", {"start": v(-41.3, -328.56) * mm, "end": v(-42.48, -328.45) * mm});
            skLineSegment(sketch, "E339", {"start": v(-42.48, -328.45) * mm, "end": v(-43.56, -328.56) * mm});
            skLineSegment(sketch, "E340", {"start": v(-43.56, -328.56) * mm, "end": v(-44.75, -328.77) * mm});
            skLineSegment(sketch, "E341", {"start": v(-44.75, -328.77) * mm, "end": v(-45.84, -328.99) * mm});
            skLineSegment(sketch, "E342", {"start": v(-45.84, -328.99) * mm, "end": v(-46.92, -329.42) * mm});
            skLineSegment(sketch, "E343", {"start": v(-46.92, -329.42) * mm, "end": v(-47.9, -329.96) * mm});
            skLineSegment(sketch, "E344", {"start": v(-47.9, -329.96) * mm, "end": v(-48.87, -330.61) * mm});
            skLineSegment(sketch, "E345", {"start": v(-48.87, -330.61) * mm, "end": v(-49.84, -331.37) * mm});
            skLineSegment(sketch, "E346", {"start": v(-49.84, -331.37) * mm, "end": v(-50.6, -332.13) * mm});
            skLineSegment(sketch, "E347", {"start": v(-50.6, -332.13) * mm, "end": v(-51.36, -333) * mm});
            skLineSegment(sketch, "E348", {"start": v(-51.36, -333) * mm, "end": v(-52, -333.97) * mm});
            skLineSegment(sketch, "E349", {"start": v(-52, -333.97) * mm, "end": v(-52.44, -335.05) * mm});
            skLineSegment(sketch, "E350", {"start": v(-52.44, -335.05) * mm, "end": v(-52.87, -336.13) * mm});
            skLineSegment(sketch, "E351", {"start": v(-52.87, -336.13) * mm, "end": v(-53.2, -337.21) * mm});
            skLineSegment(sketch, "E352", {"start": v(-53.2, -337.21) * mm, "end": v(-53.41, -338.3) * mm});
            skLineSegment(sketch, "E353", {"start": v(-53.41, -338.3) * mm, "end": v(-53.41, -339.49) * mm});
            skLineSegment(sketch, "E354", {"start": v(-53.41, -339.49) * mm, "end": v(-53.41, -343.7) * mm});
            skLineSegment(sketch, "E355", {"start": v(-53.41, -343.7) * mm, "end": v(-52.77, -346.09) * mm});
            skLineSegment(sketch, "E356", {"start": v(-52.77, -346.09) * mm, "end": v(-51.9, -348.36) * mm});
            skLineSegment(sketch, "E357", {"start": v(-51.9, -348.36) * mm, "end": v(-50.92, -350.63) * mm});
            skLineSegment(sketch, "E358", {"start": v(-50.92, -350.63) * mm, "end": v(-49.84, -352.8) * mm});
            skLineSegment(sketch, "E359", {"start": v(-49.84, -352.8) * mm, "end": v(-48.54, -354.96) * mm});
            skLineSegment(sketch, "E360", {"start": v(-48.54, -354.96) * mm, "end": v(-47.25, -357.02) * mm});
            skLineSegment(sketch, "E361", {"start": v(-47.25, -357.02) * mm, "end": v(-45.73, -358.97) * mm});
            skLineSegment(sketch, "E362", {"start": v(-38.8, -370.66) * mm, "end": v(-40.97, -366.65) * mm});
            skLineSegment(sketch, "E363", {"start": v(-40.97, -366.65) * mm, "end": v(-43.35, -362.87) * mm});
            skLineSegment(sketch, "E364", {"start": v(-43.35, -362.87) * mm, "end": v(-45.73, -358.97) * mm});
            skLineSegment(sketch, "E365", {"start": v(-38.8, -370.66) * mm, "end": v(-38.8, -376.18) * mm});
            skLineSegment(sketch, "E366", {"start": v(-46.81, -377.15) * mm, "end": v(-46.6, -377.8) * mm});
            skLineSegment(sketch, "E367", {"start": v(-46.6, -377.8) * mm, "end": v(-46.27, -378.45) * mm});
            skLineSegment(sketch, "E368", {"start": v(-46.27, -378.45) * mm, "end": v(-45.84, -379) * mm});
            skLineSegment(sketch, "E369", {"start": v(-45.84, -379) * mm, "end": v(-45.4, -379.43) * mm});
            skLineSegment(sketch, "E370", {"start": v(-45.4, -379.43) * mm, "end": v(-44.75, -379.86) * mm});
            skLineSegment(sketch, "E371", {"start": v(-44.75, -379.86) * mm, "end": v(-44.1, -380.08) * mm});
            skLineSegment(sketch, "E372", {"start": v(-44.1, -380.08) * mm, "end": v(-43.46, -380.3) * mm});
            skLineSegment(sketch, "E373", {"start": v(-43.46, -380.3) * mm, "end": v(-42.7, -380.3) * mm});
            skLineSegment(sketch, "E374", {"start": v(-42.7, -380.3) * mm, "end": v(-42.05, -380.18) * mm});
            skLineSegment(sketch, "E375", {"start": v(-42.05, -380.18) * mm, "end": v(-40.75, -379.75) * mm});
            skLineSegment(sketch, "E376", {"start": v(-40.75, -379.75) * mm, "end": v(-40.2, -379.32) * mm});
            skLineSegment(sketch, "E377", {"start": v(-40.2, -379.32) * mm, "end": v(-39.67, -378.78) * mm});
            skLineSegment(sketch, "E378", {"start": v(-39.67, -378.78) * mm, "end": v(-39.34, -378.23) * mm});
            skLineSegment(sketch, "E379", {"start": v(-39.34, -378.23) * mm, "end": v(-39.02, -377.59) * mm});
            skLineSegment(sketch, "E380", {"start": v(-39.02, -377.59) * mm, "end": v(-38.91, -376.94) * mm});
            skLineSegment(sketch, "E381", {"start": v(-38.91, -376.94) * mm, "end": v(-38.8, -376.18) * mm});
            skLineSegment(sketch, "E382", {"start": v(-46.81, -377.15) * mm, "end": v(-46.81, -370.66) * mm});
            skLineSegment(sketch, "E383", {"start": v(-46.81, -370.66) * mm, "end": v(-54.71, -370.66) * mm});
            skLineSegment(sketch, "E384", {"start": v(-54.71, -370.66) * mm, "end": v(-54.71, -376.5) * mm});
            skLineSegment(sketch, "E385", {"start": v(-54.71, -376.5) * mm, "end": v(-54.6, -377.8) * mm});
            skLineSegment(sketch, "E386", {"start": v(-54.6, -377.8) * mm, "end": v(-54.28, -379) * mm});
            skLineSegment(sketch, "E387", {"start": v(-54.28, -379) * mm, "end": v(-53.96, -380.08) * mm});
            skLineSegment(sketch, "E388", {"start": v(-53.96, -380.08) * mm, "end": v(-53.41, -381.27) * mm});
            skLineSegment(sketch, "E389", {"start": v(-53.41, -381.27) * mm, "end": v(-52.87, -382.24) * mm});
            skLineSegment(sketch, "E390", {"start": v(-52.87, -382.24) * mm, "end": v(-52.12, -383.21) * mm});
            skLineSegment(sketch, "E391", {"start": v(-52.12, -383.21) * mm, "end": v(-51.25, -384.19) * mm});
            skLineSegment(sketch, "E392", {"start": v(-51.25, -384.19) * mm, "end": v(-50.38, -384.95) * mm});
            skLineSegment(sketch, "E393", {"start": v(-50.38, -384.95) * mm, "end": v(-49.4, -385.7) * mm});
            skLineSegment(sketch, "E394", {"start": v(-49.4, -385.7) * mm, "end": v(-48.33, -386.25) * mm});
            skLineSegment(sketch, "E395", {"start": v(-48.33, -386.25) * mm, "end": v(-47.25, -386.79) * mm});
            skLineSegment(sketch, "E396", {"start": v(-47.25, -386.79) * mm, "end": v(-44.86, -387.44) * mm});
            skLineSegment(sketch, "E397", {"start": v(-44.86, -387.44) * mm, "end": v(-43.67, -387.54) * mm});
            skLineSegment(sketch, "E398", {"start": v(-43.67, -387.54) * mm, "end": v(-42.48, -387.54) * mm});
            skLineSegment(sketch, "E399", {"start": v(-42.48, -387.54) * mm, "end": v(-41.3, -387.44) * mm});
            skLineSegment(sketch, "E400", {"start": v(-41.3, -387.44) * mm, "end": v(-38.91, -386.79) * mm});
            skLineSegment(sketch, "E401", {"start": v(-38.91, -386.79) * mm, "end": v(-37.83, -386.25) * mm});
            skLineSegment(sketch, "E402", {"start": v(-37.83, -386.25) * mm, "end": v(-36.75, -385.7) * mm});
            skLineSegment(sketch, "E403", {"start": v(-36.75, -385.7) * mm, "end": v(-35.77, -384.95) * mm});
            skLineSegment(sketch, "E404", {"start": v(-35.77, -384.95) * mm, "end": v(-34.9, -384.19) * mm});
            skLineSegment(sketch, "E405", {"start": v(-34.9, -384.19) * mm, "end": v(-34.04, -383.21) * mm});
            skLineSegment(sketch, "E406", {"start": v(-34.04, -383.21) * mm, "end": v(-33.28, -382.24) * mm});
            skLineSegment(sketch, "E407", {"start": v(-33.28, -382.24) * mm, "end": v(-32.74, -381.27) * mm});
            skLineSegment(sketch, "E408", {"start": v(-32.74, -381.27) * mm, "end": v(-32.2, -380.08) * mm});
            skLineSegment(sketch, "E409", {"start": v(-32.2, -380.08) * mm, "end": v(-31.88, -379) * mm});
            skLineSegment(sketch, "E410", {"start": v(-31.88, -379) * mm, "end": v(-31.55, -377.8) * mm});
            skLineSegment(sketch, "E411", {"start": v(-31.55, -377.8) * mm, "end": v(-31.44, -376.5) * mm});
            skLineSegment(sketch, "E412", {"start": v(-31.44, -376.5) * mm, "end": v(-31.44, -370.66) * mm});
            skLineSegment(sketch, "E413", {"start": v(-31.44, -370.66) * mm, "end": v(-32.2, -368.06) * mm});
            skLineSegment(sketch, "E414", {"start": v(-32.2, -368.06) * mm, "end": v(-33.07, -365.57) * mm});
            skLineSegment(sketch, "E415", {"start": v(-33.07, -365.57) * mm, "end": v(-34.04, -363.2) * mm});
            skLineSegment(sketch, "E416", {"start": v(-34.04, -363.2) * mm, "end": v(-35.23, -360.8) * mm});
            skLineSegment(sketch, "E417", {"start": v(-35.23, -360.8) * mm, "end": v(-36.53, -358.54) * mm});
            skLineSegment(sketch, "E418", {"start": v(-36.53, -358.54) * mm, "end": v(-37.83, -356.37) * mm});
            skLineSegment(sketch, "E419", {"start": v(-37.83, -356.37) * mm, "end": v(-39.34, -354.2) * mm});
            skLineSegment(sketch, "E420", {"start": v(-45.51, -343.7) * mm, "end": v(-44.54, -345.87) * mm});
            skLineSegment(sketch, "E421", {"start": v(-44.54, -345.87) * mm, "end": v(-43.35, -348.04) * mm});
            skLineSegment(sketch, "E422", {"start": v(-43.35, -348.04) * mm, "end": v(-42.16, -350.2) * mm});
            skLineSegment(sketch, "E423", {"start": v(-42.16, -350.2) * mm, "end": v(-40.86, -352.26) * mm});
            skLineSegment(sketch, "E424", {"start": v(-40.86, -352.26) * mm, "end": v(-39.34, -354.2) * mm});
            skLineSegment(sketch, "E425", {"start": v(-45.51, -343.7) * mm, "end": v(-45.51, -338.84) * mm});
            skLineSegment(sketch, "E426", {"start": v(-39.34, -338.84) * mm, "end": v(-39.45, -338.3) * mm});
            skLineSegment(sketch, "E427", {"start": v(-39.45, -338.3) * mm, "end": v(-39.67, -337.65) * mm});
            skLineSegment(sketch, "E428", {"start": v(-39.67, -337.65) * mm, "end": v(-39.89, -337.21) * mm});
            skLineSegment(sketch, "E429", {"start": v(-39.89, -337.21) * mm, "end": v(-40.32, -336.67) * mm});
            skLineSegment(sketch, "E430", {"start": v(-40.32, -336.67) * mm, "end": v(-40.75, -336.35) * mm});
            skLineSegment(sketch, "E431", {"start": v(-40.75, -336.35) * mm, "end": v(-41.3, -336.02) * mm});
            skLineSegment(sketch, "E432", {"start": v(-41.3, -336.02) * mm, "end": v(-41.83, -335.91) * mm});
            skLineSegment(sketch, "E433", {"start": v(-41.83, -335.91) * mm, "end": v(-42.48, -335.8) * mm});
            skLineSegment(sketch, "E434", {"start": v(-42.48, -335.8) * mm, "end": v(-43.03, -335.91) * mm});
            skLineSegment(sketch, "E435", {"start": v(-43.03, -335.91) * mm, "end": v(-43.56, -336.02) * mm});
            skLineSegment(sketch, "E436", {"start": v(-43.56, -336.02) * mm, "end": v(-44.1, -336.35) * mm});
            skLineSegment(sketch, "E437", {"start": v(-44.1, -336.35) * mm, "end": v(-44.65, -336.67) * mm});
            skLineSegment(sketch, "E438", {"start": v(-44.65, -336.67) * mm, "end": v(-44.97, -337.21) * mm});
            skLineSegment(sketch, "E439", {"start": v(-44.97, -337.21) * mm, "end": v(-45.3, -337.65) * mm});
            skLineSegment(sketch, "E440", {"start": v(-45.3, -337.65) * mm, "end": v(-45.4, -338.3) * mm});
            skLineSegment(sketch, "E441", {"start": v(-45.4, -338.3) * mm, "end": v(-45.51, -338.84) * mm});
            skLineSegment(sketch, "E442", {"start": v(-234.06, -376.18) * mm, "end": v(-233.52, -374.88) * mm});
            skLineSegment(sketch, "E443", {"start": v(-233.52, -374.88) * mm, "end": v(-233.09, -373.47) * mm});
            skLineSegment(sketch, "E444", {"start": v(-233.09, -373.47) * mm, "end": v(-232.65, -372.07) * mm});
            skLineSegment(sketch, "E445", {"start": v(-232.65, -372.07) * mm, "end": v(-232.55, -370.66) * mm});
            skLineSegment(sketch, "E446", {"start": v(-232.55, -370.66) * mm, "end": v(-232.44, -369.25) * mm});
            skLineSegment(sketch, "E447", {"start": v(-232.44, -369.25) * mm, "end": v(-232.55, -367.84) * mm});
            skLineSegment(sketch, "E448", {"start": v(-232.55, -367.84) * mm, "end": v(-232.65, -366.44) * mm});
            skLineSegment(sketch, "E449", {"start": v(-232.65, -366.44) * mm, "end": v(-233.09, -365.03) * mm});
            skLineSegment(sketch, "E450", {"start": v(-233.09, -365.03) * mm, "end": v(-233.52, -363.73) * mm});
            skLineSegment(sketch, "E451", {"start": v(-233.52, -363.73) * mm, "end": v(-234.06, -362.43) * mm});
            skLineSegment(sketch, "E452", {"start": v(-239.37, -378.34) * mm, "end": v(-238.28, -378.13) * mm});
            skLineSegment(sketch, "E453", {"start": v(-238.28, -378.13) * mm, "end": v(-237.1, -377.91) * mm});
            skLineSegment(sketch, "E454", {"start": v(-237.1, -377.91) * mm, "end": v(-236.01, -377.48) * mm});
            skLineSegment(sketch, "E455", {"start": v(-236.01, -377.48) * mm, "end": v(-235.04, -376.83) * mm});
            skLineSegment(sketch, "E456", {"start": v(-235.04, -376.83) * mm, "end": v(-234.06, -376.18) * mm});
            skLineSegment(sketch, "E457", {"start": v(-239.37, -378.34) * mm, "end": v(-239.37, -360.27) * mm});
            skLineSegment(sketch, "E458", {"start": v(-234.06, -362.43) * mm, "end": v(-235.04, -361.68) * mm});
            skLineSegment(sketch, "E459", {"start": v(-235.04, -361.68) * mm, "end": v(-236.01, -361.13) * mm});
            skLineSegment(sketch, "E460", {"start": v(-236.01, -361.13) * mm, "end": v(-237.1, -360.7) * mm});
            skLineSegment(sketch, "E461", {"start": v(-237.1, -360.7) * mm, "end": v(-238.28, -360.38) * mm});
            skLineSegment(sketch, "E462", {"start": v(-238.28, -360.38) * mm, "end": v(-239.37, -360.27) * mm});
            skLineSegment(sketch, "E463", {"start": v(-234.06, -350.2) * mm, "end": v(-233.52, -349.12) * mm});
            skLineSegment(sketch, "E464", {"start": v(-233.52, -349.12) * mm, "end": v(-232.98, -348.04) * mm});
            skLineSegment(sketch, "E465", {"start": v(-232.98, -348.04) * mm, "end": v(-232.65, -346.85) * mm});
            skLineSegment(sketch, "E466", {"start": v(-232.65, -346.85) * mm, "end": v(-232.44, -345.66) * mm});
            skLineSegment(sketch, "E467", {"start": v(-232.44, -345.66) * mm, "end": v(-232.44, -343.17) * mm});
            skLineSegment(sketch, "E468", {"start": v(-232.44, -343.17) * mm, "end": v(-232.65, -341.98) * mm});
            skLineSegment(sketch, "E469", {"start": v(-232.65, -341.98) * mm, "end": v(-232.98, -340.79) * mm});
            skLineSegment(sketch, "E470", {"start": v(-232.98, -340.79) * mm, "end": v(-233.52, -339.6) * mm});
            skLineSegment(sketch, "E471", {"start": v(-233.52, -339.6) * mm, "end": v(-234.06, -338.62) * mm});
            skLineSegment(sketch, "E472", {"start": v(-239.37, -352.48) * mm, "end": v(-238.6, -352.58) * mm});
            skLineSegment(sketch, "E473", {"start": v(-238.6, -352.58) * mm, "end": v(-237.1, -352.37) * mm});
            skLineSegment(sketch, "E474", {"start": v(-237.1, -352.37) * mm, "end": v(-236.44, -352.15) * mm});
            skLineSegment(sketch, "E475", {"start": v(-236.44, -352.15) * mm, "end": v(-235.69, -351.82) * mm});
            skLineSegment(sketch, "E476", {"start": v(-235.69, -351.82) * mm, "end": v(-235.14, -351.4) * mm});
            skLineSegment(sketch, "E477", {"start": v(-235.14, -351.4) * mm, "end": v(-234.6, -350.85) * mm});
            skLineSegment(sketch, "E478", {"start": v(-234.6, -350.85) * mm, "end": v(-234.06, -350.2) * mm});
            skLineSegment(sketch, "E479", {"start": v(-239.37, -352.48) * mm, "end": v(-239.37, -336.35) * mm});
            skLineSegment(sketch, "E480", {"start": v(-234.06, -338.62) * mm, "end": v(-235.04, -337.86) * mm});
            skLineSegment(sketch, "E481", {"start": v(-235.04, -337.86) * mm, "end": v(-236.01, -337.32) * mm});
            skLineSegment(sketch, "E482", {"start": v(-236.01, -337.32) * mm, "end": v(-237.1, -336.78) * mm});
            skLineSegment(sketch, "E483", {"start": v(-237.1, -336.78) * mm, "end": v(-238.28, -336.56) * mm});
            skLineSegment(sketch, "E484", {"start": v(-238.28, -336.56) * mm, "end": v(-239.37, -336.35) * mm});
            skLineSegment(sketch, "E485", {"start": v(-247.7, -328.45) * mm, "end": v(-247.7, -387.98) * mm});
            skLineSegment(sketch, "E486", {"start": v(-247.7, -387.98) * mm, "end": v(-238.82, -387.98) * mm});
            skLineSegment(sketch, "E487", {"start": v(-238.82, -387.98) * mm, "end": v(-237.53, -387.87) * mm});
            skLineSegment(sketch, "E488", {"start": v(-237.53, -387.87) * mm, "end": v(-236.12, -387.54) * mm});
            skLineSegment(sketch, "E489", {"start": v(-236.12, -387.54) * mm, "end": v(-234.82, -387.11) * mm});
            skLineSegment(sketch, "E490", {"start": v(-234.82, -387.11) * mm, "end": v(-233.52, -386.57) * mm});
            skLineSegment(sketch, "E491", {"start": v(-233.52, -386.57) * mm, "end": v(-232.33, -385.92) * mm});
            skLineSegment(sketch, "E492", {"start": v(-232.33, -385.92) * mm, "end": v(-231.14, -385.16) * mm});
            skLineSegment(sketch, "E493", {"start": v(-231.14, -385.16) * mm, "end": v(-230.06, -384.3) * mm});
            skLineSegment(sketch, "E494", {"start": v(-230.06, -384.3) * mm, "end": v(-229.08, -383.32) * mm});
            skLineSegment(sketch, "E495", {"start": v(-229.08, -383.32) * mm, "end": v(-228.22, -382.24) * mm});
            skLineSegment(sketch, "E496", {"start": v(-228.22, -382.24) * mm, "end": v(-227.46, -381.16) * mm});
            skLineSegment(sketch, "E497", {"start": v(-227.46, -381.16) * mm, "end": v(-226.81, -379.97) * mm});
            skLineSegment(sketch, "E498", {"start": v(-226.81, -379.97) * mm, "end": v(-226.05, -378.34) * mm});
            skLineSegment(sketch, "E499", {"start": v(-226.05, -378.34) * mm, "end": v(-225.4, -376.83) * mm});
            skLineSegment(sketch, "E500", {"start": v(-225.4, -376.83) * mm, "end": v(-224.97, -375.2) * mm});
            skLineSegment(sketch, "E501", {"start": v(-224.97, -375.2) * mm, "end": v(-224.54, -373.47) * mm});
            skLineSegment(sketch, "E502", {"start": v(-224.54, -373.47) * mm, "end": v(-224.32, -371.85) * mm});
            skLineSegment(sketch, "E503", {"start": v(-224.32, -371.85) * mm, "end": v(-224.21, -370.12) * mm});
            skLineSegment(sketch, "E504", {"start": v(-224.21, -370.12) * mm, "end": v(-224.21, -368.39) * mm});
            skLineSegment(sketch, "E505", {"start": v(-224.21, -368.39) * mm, "end": v(-224.32, -366.76) * mm});
            skLineSegment(sketch, "E506", {"start": v(-224.32, -366.76) * mm, "end": v(-224.54, -365.03) * mm});
            skLineSegment(sketch, "E507", {"start": v(-224.54, -365.03) * mm, "end": v(-224.97, -363.4) * mm});
            skLineSegment(sketch, "E508", {"start": v(-224.97, -363.4) * mm, "end": v(-225.4, -361.78) * mm});
            skLineSegment(sketch, "E509", {"start": v(-225.4, -361.78) * mm, "end": v(-226.05, -360.16) * mm});
            skLineSegment(sketch, "E510", {"start": v(-226.05, -360.16) * mm, "end": v(-226.81, -358.64) * mm});
            skLineSegment(sketch, "E511", {"start": v(-226.81, -358.64) * mm, "end": v(-227.68, -357.45) * mm});
            skLineSegment(sketch, "E512", {"start": v(-227.68, -357.45) * mm, "end": v(-228.65, -356.48) * mm});
            skLineSegment(sketch, "E513", {"start": v(-228.65, -356.48) * mm, "end": v(-229.73, -355.5) * mm});
            skLineSegment(sketch, "E514", {"start": v(-229.73, -355.5) * mm, "end": v(-228.65, -354.53) * mm});
            skLineSegment(sketch, "E515", {"start": v(-228.65, -354.53) * mm, "end": v(-227.68, -353.56) * mm});
            skLineSegment(sketch, "E516", {"start": v(-227.68, -353.56) * mm, "end": v(-226.81, -352.37) * mm});
            skLineSegment(sketch, "E517", {"start": v(-226.81, -352.37) * mm, "end": v(-226.05, -351.18) * mm});
            skLineSegment(sketch, "E518", {"start": v(-226.05, -351.18) * mm, "end": v(-225.4, -349.88) * mm});
            skLineSegment(sketch, "E519", {"start": v(-225.4, -349.88) * mm, "end": v(-224.86, -348.47) * mm});
            skLineSegment(sketch, "E520", {"start": v(-224.86, -348.47) * mm, "end": v(-224.54, -347.06) * mm});
            skLineSegment(sketch, "E521", {"start": v(-224.54, -347.06) * mm, "end": v(-224.21, -345.66) * mm});
            skLineSegment(sketch, "E522", {"start": v(-224.21, -345.66) * mm, "end": v(-224.1, -344.25) * mm});
            skLineSegment(sketch, "E523", {"start": v(-224.1, -344.25) * mm, "end": v(-224.1, -342.84) * mm});
            skLineSegment(sketch, "E524", {"start": v(-224.1, -342.84) * mm, "end": v(-224.21, -341.33) * mm});
            skLineSegment(sketch, "E525", {"start": v(-224.21, -341.33) * mm, "end": v(-224.54, -339.92) * mm});
            skLineSegment(sketch, "E526", {"start": v(-224.54, -339.92) * mm, "end": v(-224.86, -338.51) * mm});
            skLineSegment(sketch, "E527", {"start": v(-224.86, -338.51) * mm, "end": v(-225.4, -337.21) * mm});
            skLineSegment(sketch, "E528", {"start": v(-225.4, -337.21) * mm, "end": v(-226.05, -335.91) * mm});
            skLineSegment(sketch, "E529", {"start": v(-226.05, -335.91) * mm, "end": v(-226.81, -334.62) * mm});
            skLineSegment(sketch, "E530", {"start": v(-226.81, -334.62) * mm, "end": v(-227.57, -333.53) * mm});
            skLineSegment(sketch, "E531", {"start": v(-227.57, -333.53) * mm, "end": v(-228.54, -332.45) * mm});
            skLineSegment(sketch, "E532", {"start": v(-228.54, -332.45) * mm, "end": v(-229.62, -331.37) * mm});
            skLineSegment(sketch, "E533", {"start": v(-229.62, -331.37) * mm, "end": v(-230.82, -330.5) * mm});
            skLineSegment(sketch, "E534", {"start": v(-230.82, -330.5) * mm, "end": v(-232, -329.75) * mm});
            skLineSegment(sketch, "E535", {"start": v(-232, -329.75) * mm, "end": v(-233.3, -329.1) * mm});
            skLineSegment(sketch, "E536", {"start": v(-233.3, -329.1) * mm, "end": v(-234.6, -328.45) * mm});
            skLineSegment(sketch, "E537", {"start": v(-234.6, -328.45) * mm, "end": v(-247.7, -328.45) * mm});
            skLineSegment(sketch, "E538", {"start": v(239.48, -378.67) * mm, "end": v(247.7, -378.67) * mm});
            skLineSegment(sketch, "E539", {"start": v(247.7, -378.67) * mm, "end": v(247.7, -387.98) * mm});
            skLineSegment(sketch, "E540", {"start": v(247.7, -387.98) * mm, "end": v(239.48, -387.98) * mm});
            skLineSegment(sketch, "E541", {"start": v(239.48, -387.98) * mm, "end": v(239.48, -378.67) * mm});
            skLineSegment(sketch, "E542", {"start": v(-237.74, -272.7) * mm, "end": v(-237.74, -296.4) * mm});
            skLineSegment(sketch, "E543", {"start": v(-241.96, -300.09) * mm, "end": v(-241.31, -299.98) * mm});
            skLineSegment(sketch, "E544", {"start": v(-241.31, -299.98) * mm, "end": v(-240.56, -299.76) * mm});
            skLineSegment(sketch, "E545", {"start": v(-240.56, -299.76) * mm, "end": v(-239.9, -299.44) * mm});
            skLineSegment(sketch, "E546", {"start": v(-239.9, -299.44) * mm, "end": v(-239.26, -299) * mm});
            skLineSegment(sketch, "E547", {"start": v(-239.26, -299) * mm, "end": v(-238.72, -298.46) * mm});
            skLineSegment(sketch, "E548", {"start": v(-238.72, -298.46) * mm, "end": v(-238.28, -297.81) * mm});
            skLineSegment(sketch, "E549", {"start": v(-238.28, -297.81) * mm, "end": v(-237.96, -297.17) * mm});
            skLineSegment(sketch, "E550", {"start": v(-237.96, -297.17) * mm, "end": v(-237.74, -296.4) * mm});
            skLineSegment(sketch, "E551", {"start": v(-241.96, -300.09) * mm, "end": v(-242.5, -300.09) * mm});
            skLineSegment(sketch, "E552", {"start": v(-242.5, -300.09) * mm, "end": v(-242.5, -269.02) * mm});
            skLineSegment(sketch, "E553", {"start": v(-242.5, -269.02) * mm, "end": v(-241.96, -269.02) * mm});
            skLineSegment(sketch, "E554", {"start": v(-237.74, -272.7) * mm, "end": v(-237.96, -271.95) * mm});
            skLineSegment(sketch, "E555", {"start": v(-237.96, -271.95) * mm, "end": v(-238.28, -271.3) * mm});
            skLineSegment(sketch, "E556", {"start": v(-238.28, -271.3) * mm, "end": v(-238.72, -270.65) * mm});
            skLineSegment(sketch, "E557", {"start": v(-238.72, -270.65) * mm, "end": v(-239.26, -270.1) * mm});
            skLineSegment(sketch, "E558", {"start": v(-239.26, -270.1) * mm, "end": v(-239.9, -269.67) * mm});
            skLineSegment(sketch, "E559", {"start": v(-239.9, -269.67) * mm, "end": v(-240.56, -269.35) * mm});
            skLineSegment(sketch, "E560", {"start": v(-240.56, -269.35) * mm, "end": v(-241.31, -269.13) * mm});
            skLineSegment(sketch, "E561", {"start": v(-241.31, -269.13) * mm, "end": v(-241.96, -269.02) * mm});
            skLineSegment(sketch, "E562", {"start": v(-248.57, -263.61) * mm, "end": v(-248.57, -305.5) * mm});
            skLineSegment(sketch, "E563", {"start": v(-248.57, -305.5) * mm, "end": v(-238.72, -305.5) * mm});
            skLineSegment(sketch, "E564", {"start": v(-238.72, -305.5) * mm, "end": v(-237.53, -305.07) * mm});
            skLineSegment(sketch, "E565", {"start": v(-237.53, -305.07) * mm, "end": v(-236.55, -304.42) * mm});
            skLineSegment(sketch, "E566", {"start": v(-236.55, -304.42) * mm, "end": v(-235.47, -303.77) * mm});
            skLineSegment(sketch, "E567", {"start": v(-235.47, -303.77) * mm, "end": v(-234.6, -302.9) * mm});
            skLineSegment(sketch, "E568", {"start": v(-234.6, -302.9) * mm, "end": v(-233.85, -302.04) * mm});
            skLineSegment(sketch, "E569", {"start": v(-233.85, -302.04) * mm, "end": v(-233.09, -301.06) * mm});
            skLineSegment(sketch, "E570", {"start": v(-233.09, -301.06) * mm, "end": v(-232.55, -299.98) * mm});
            skLineSegment(sketch, "E571", {"start": v(-232.55, -299.98) * mm, "end": v(-232, -298.79) * mm});
            skLineSegment(sketch, "E572", {"start": v(-232, -298.79) * mm, "end": v(-231.68, -297.7) * mm});
            skLineSegment(sketch, "E573", {"start": v(-231.68, -297.7) * mm, "end": v(-231.68, -271.4) * mm});
            skLineSegment(sketch, "E574", {"start": v(-231.68, -271.4) * mm, "end": v(-232, -270.32) * mm});
            skLineSegment(sketch, "E575", {"start": v(-232, -270.32) * mm, "end": v(-232.55, -269.13) * mm});
            skLineSegment(sketch, "E576", {"start": v(-232.55, -269.13) * mm, "end": v(-233.09, -268.05) * mm});
            skLineSegment(sketch, "E577", {"start": v(-233.09, -268.05) * mm, "end": v(-233.85, -267.08) * mm});
            skLineSegment(sketch, "E578", {"start": v(-233.85, -267.08) * mm, "end": v(-234.6, -266.2) * mm});
            skLineSegment(sketch, "E579", {"start": v(-234.6, -266.2) * mm, "end": v(-235.47, -265.34) * mm});
            skLineSegment(sketch, "E580", {"start": v(-235.47, -265.34) * mm, "end": v(-236.55, -264.7) * mm});
            skLineSegment(sketch, "E581", {"start": v(-236.55, -264.7) * mm, "end": v(-237.53, -264.04) * mm});
            skLineSegment(sketch, "E582", {"start": v(-237.53, -264.04) * mm, "end": v(-238.72, -263.61) * mm});
            skLineSegment(sketch, "E583", {"start": v(-238.72, -263.61) * mm, "end": v(-248.57, -263.61) * mm});
            skLineSegment(sketch, "E584", {"start": v(63.16, -272.7) * mm, "end": v(63.16, -296.4) * mm});
            skLineSegment(sketch, "E585", {"start": v(58.93, -300.09) * mm, "end": v(59.7, -299.98) * mm});
            skLineSegment(sketch, "E586", {"start": v(59.7, -299.98) * mm, "end": v(60.45, -299.76) * mm});
            skLineSegment(sketch, "E587", {"start": v(60.45, -299.76) * mm, "end": v(61.1, -299.44) * mm});
            skLineSegment(sketch, "E588", {"start": v(61.1, -299.44) * mm, "end": v(61.64, -299) * mm});
            skLineSegment(sketch, "E589", {"start": v(61.64, -299) * mm, "end": v(62.18, -298.46) * mm});
            skLineSegment(sketch, "E590", {"start": v(62.18, -298.46) * mm, "end": v(62.62, -297.81) * mm});
            skLineSegment(sketch, "E591", {"start": v(62.62, -297.81) * mm, "end": v(62.94, -297.17) * mm});
            skLineSegment(sketch, "E592", {"start": v(62.94, -297.17) * mm, "end": v(63.16, -296.4) * mm});
            skLineSegment(sketch, "E593", {"start": v(58.93, -300.09) * mm, "end": v(58.5, -300.09) * mm});
            skLineSegment(sketch, "E594", {"start": v(58.5, -300.09) * mm, "end": v(58.5, -269.02) * mm});
            skLineSegment(sketch, "E595", {"start": v(58.5, -269.02) * mm, "end": v(58.93, -269.02) * mm});
            skLineSegment(sketch, "E596", {"start": v(63.16, -272.7) * mm, "end": v(62.94, -271.95) * mm});
            skLineSegment(sketch, "E597", {"start": v(62.94, -271.95) * mm, "end": v(62.62, -271.3) * mm});
            skLineSegment(sketch, "E598", {"start": v(62.62, -271.3) * mm, "end": v(62.18, -270.65) * mm});
            skLineSegment(sketch, "E599", {"start": v(62.18, -270.65) * mm, "end": v(61.64, -270.1) * mm});
            skLineSegment(sketch, "E600", {"start": v(61.64, -270.1) * mm, "end": v(61.1, -269.67) * mm});
            skLineSegment(sketch, "E601", {"start": v(61.1, -269.67) * mm, "end": v(60.45, -269.35) * mm});
            skLineSegment(sketch, "E602", {"start": v(60.45, -269.35) * mm, "end": v(59.7, -269.13) * mm});
            skLineSegment(sketch, "E603", {"start": v(59.7, -269.13) * mm, "end": v(58.93, -269.02) * mm});
            skLineSegment(sketch, "E604", {"start": v(52.44, -263.61) * mm, "end": v(52.44, -305.5) * mm});
            skLineSegment(sketch, "E605", {"start": v(52.44, -305.5) * mm, "end": v(62.29, -305.5) * mm});
            skLineSegment(sketch, "E606", {"start": v(62.29, -305.5) * mm, "end": v(63.37, -305.07) * mm});
            skLineSegment(sketch, "E607", {"start": v(63.37, -305.07) * mm, "end": v(64.46, -304.42) * mm});
            skLineSegment(sketch, "E608", {"start": v(64.46, -304.42) * mm, "end": v(65.43, -303.77) * mm});
            skLineSegment(sketch, "E609", {"start": v(65.43, -303.77) * mm, "end": v(66.3, -302.9) * mm});
            skLineSegment(sketch, "E610", {"start": v(66.3, -302.9) * mm, "end": v(67.16, -302.04) * mm});
            skLineSegment(sketch, "E611", {"start": v(67.16, -302.04) * mm, "end": v(67.8, -301.06) * mm});
            skLineSegment(sketch, "E612", {"start": v(67.8, -301.06) * mm, "end": v(68.46, -299.98) * mm});
            skLineSegment(sketch, "E613", {"start": v(68.46, -299.98) * mm, "end": v(68.9, -298.79) * mm});
            skLineSegment(sketch, "E614", {"start": v(68.9, -298.79) * mm, "end": v(69.22, -297.7) * mm});
            skLineSegment(sketch, "E615", {"start": v(69.22, -297.7) * mm, "end": v(69.22, -271.4) * mm});
            skLineSegment(sketch, "E616", {"start": v(69.22, -271.4) * mm, "end": v(68.9, -270.32) * mm});
            skLineSegment(sketch, "E617", {"start": v(68.9, -270.32) * mm, "end": v(68.46, -269.13) * mm});
            skLineSegment(sketch, "E618", {"start": v(68.46, -269.13) * mm, "end": v(67.8, -268.05) * mm});
            skLineSegment(sketch, "E619", {"start": v(67.8, -268.05) * mm, "end": v(67.16, -267.08) * mm});
            skLineSegment(sketch, "E620", {"start": v(67.16, -267.08) * mm, "end": v(65.43, -265.34) * mm});
            skLineSegment(sketch, "E621", {"start": v(65.43, -265.34) * mm, "end": v(64.46, -264.7) * mm});
            skLineSegment(sketch, "E622", {"start": v(64.46, -264.7) * mm, "end": v(63.37, -264.04) * mm});
            skLineSegment(sketch, "E623", {"start": v(63.37, -264.04) * mm, "end": v(62.29, -263.61) * mm});
            skLineSegment(sketch, "E624", {"start": v(62.29, -263.61) * mm, "end": v(52.44, -263.61) * mm});
            skLineSegment(sketch, "E625", {"start": v(135.13, -272.7) * mm, "end": v(135.13, -296.4) * mm});
            skLineSegment(sketch, "E626", {"start": v(130.91, -300.09) * mm, "end": v(131.67, -299.98) * mm});
            skLineSegment(sketch, "E627", {"start": v(131.67, -299.98) * mm, "end": v(132.43, -299.76) * mm});
            skLineSegment(sketch, "E628", {"start": v(132.43, -299.76) * mm, "end": v(133.08, -299.44) * mm});
            skLineSegment(sketch, "E629", {"start": v(133.08, -299.44) * mm, "end": v(133.62, -299) * mm});
            skLineSegment(sketch, "E630", {"start": v(133.62, -299) * mm, "end": v(134.16, -298.46) * mm});
            skLineSegment(sketch, "E631", {"start": v(134.16, -298.46) * mm, "end": v(134.6, -297.81) * mm});
            skLineSegment(sketch, "E632", {"start": v(134.6, -297.81) * mm, "end": v(134.92, -297.17) * mm});
            skLineSegment(sketch, "E633", {"start": v(134.92, -297.17) * mm, "end": v(135.13, -296.4) * mm});
            skLineSegment(sketch, "E634", {"start": v(130.91, -300.09) * mm, "end": v(130.37, -300.09) * mm});
            skLineSegment(sketch, "E635", {"start": v(130.37, -300.09) * mm, "end": v(130.37, -269.02) * mm});
            skLineSegment(sketch, "E636", {"start": v(130.37, -269.02) * mm, "end": v(130.91, -269.02) * mm});
            skLineSegment(sketch, "E637", {"start": v(135.13, -272.7) * mm, "end": v(134.92, -271.95) * mm});
            skLineSegment(sketch, "E638", {"start": v(134.92, -271.95) * mm, "end": v(134.6, -271.3) * mm});
            skLineSegment(sketch, "E639", {"start": v(134.6, -271.3) * mm, "end": v(134.16, -270.65) * mm});
            skLineSegment(sketch, "E640", {"start": v(134.16, -270.65) * mm, "end": v(133.62, -270.1) * mm});
            skLineSegment(sketch, "E641", {"start": v(133.62, -270.1) * mm, "end": v(133.08, -269.67) * mm});
            skLineSegment(sketch, "E642", {"start": v(133.08, -269.67) * mm, "end": v(132.43, -269.35) * mm});
            skLineSegment(sketch, "E643", {"start": v(132.43, -269.35) * mm, "end": v(131.67, -269.13) * mm});
            skLineSegment(sketch, "E644", {"start": v(131.67, -269.13) * mm, "end": v(130.91, -269.02) * mm});
            skLineSegment(sketch, "E645", {"start": v(124.42, -263.61) * mm, "end": v(124.42, -305.5) * mm});
            skLineSegment(sketch, "E646", {"start": v(124.42, -305.5) * mm, "end": v(134.27, -305.5) * mm});
            skLineSegment(sketch, "E647", {"start": v(134.27, -305.5) * mm, "end": v(135.35, -305.07) * mm});
            skLineSegment(sketch, "E648", {"start": v(135.35, -305.07) * mm, "end": v(136.43, -304.42) * mm});
            skLineSegment(sketch, "E649", {"start": v(136.43, -304.42) * mm, "end": v(137.4, -303.77) * mm});
            skLineSegment(sketch, "E650", {"start": v(137.4, -303.77) * mm, "end": v(138.27, -302.9) * mm});
            skLineSegment(sketch, "E651", {"start": v(138.27, -302.9) * mm, "end": v(139.14, -302.04) * mm});
            skLineSegment(sketch, "E652", {"start": v(139.14, -302.04) * mm, "end": v(139.79, -301.06) * mm});
            skLineSegment(sketch, "E653", {"start": v(139.79, -301.06) * mm, "end": v(140.44, -299.98) * mm});
            skLineSegment(sketch, "E654", {"start": v(140.44, -299.98) * mm, "end": v(140.87, -298.79) * mm});
            skLineSegment(sketch, "E655", {"start": v(140.87, -298.79) * mm, "end": v(141.2, -297.7) * mm});
            skLineSegment(sketch, "E656", {"start": v(141.2, -297.7) * mm, "end": v(141.2, -271.4) * mm});
            skLineSegment(sketch, "E657", {"start": v(141.2, -271.4) * mm, "end": v(140.87, -270.32) * mm});
            skLineSegment(sketch, "E658", {"start": v(140.87, -270.32) * mm, "end": v(140.44, -269.13) * mm});
            skLineSegment(sketch, "E659", {"start": v(140.44, -269.13) * mm, "end": v(139.79, -268.05) * mm});
            skLineSegment(sketch, "E660", {"start": v(139.79, -268.05) * mm, "end": v(139.14, -267.08) * mm});
            skLineSegment(sketch, "E661", {"start": v(139.14, -267.08) * mm, "end": v(137.4, -265.34) * mm});
            skLineSegment(sketch, "E662", {"start": v(137.4, -265.34) * mm, "end": v(136.43, -264.7) * mm});
            skLineSegment(sketch, "E663", {"start": v(136.43, -264.7) * mm, "end": v(135.35, -264.04) * mm});
            skLineSegment(sketch, "E664", {"start": v(135.35, -264.04) * mm, "end": v(134.27, -263.61) * mm});
            skLineSegment(sketch, "E665", {"start": v(134.27, -263.61) * mm, "end": v(124.42, -263.61) * mm});
            skLineSegment(sketch, "E666", {"start": v(-223.02, -263.61) * mm, "end": v(-217.07, -263.61) * mm});
            skLineSegment(sketch, "E667", {"start": v(-217.07, -263.61) * mm, "end": v(-217.07, -305.5) * mm});
            skLineSegment(sketch, "E668", {"start": v(-217.07, -305.5) * mm, "end": v(-223.02, -305.5) * mm});
            skLineSegment(sketch, "E669", {"start": v(-223.02, -305.5) * mm, "end": v(-223.02, -263.61) * mm});
            skLineSegment(sketch, "E670", {"start": v(-197.15, -280.82) * mm, "end": v(-196.61, -279.85) * mm});
            skLineSegment(sketch, "E671", {"start": v(-196.61, -279.85) * mm, "end": v(-196.29, -278.76) * mm});
            skLineSegment(sketch, "E672", {"start": v(-196.29, -278.76) * mm, "end": v(-195.96, -277.68) * mm});
            skLineSegment(sketch, "E673", {"start": v(-195.96, -277.68) * mm, "end": v(-195.86, -276.5) * mm});
            skLineSegment(sketch, "E674", {"start": v(-195.86, -276.5) * mm, "end": v(-195.86, -275.4) * mm});
            skLineSegment(sketch, "E675", {"start": v(-195.86, -275.4) * mm, "end": v(-195.96, -274.22) * mm});
            skLineSegment(sketch, "E676", {"start": v(-195.96, -274.22) * mm, "end": v(-196.29, -273.14) * mm});
            skLineSegment(sketch, "E677", {"start": v(-196.29, -273.14) * mm, "end": v(-196.61, -272.05) * mm});
            skLineSegment(sketch, "E678", {"start": v(-196.61, -272.05) * mm, "end": v(-197.15, -271.08) * mm});
            skLineSegment(sketch, "E679", {"start": v(-200.83, -282.34) * mm, "end": v(-199.86, -282.23) * mm});
            skLineSegment(sketch, "E680", {"start": v(-199.86, -282.23) * mm, "end": v(-198.88, -281.9) * mm});
            skLineSegment(sketch, "E681", {"start": v(-198.88, -281.9) * mm, "end": v(-197.91, -281.47) * mm});
            skLineSegment(sketch, "E682", {"start": v(-197.91, -281.47) * mm, "end": v(-197.15, -280.82) * mm});
            skLineSegment(sketch, "E683", {"start": v(-200.83, -282.34) * mm, "end": v(-200.83, -269.57) * mm});
            skLineSegment(sketch, "E684", {"start": v(-197.15, -271.08) * mm, "end": v(-197.91, -270.43) * mm});
            skLineSegment(sketch, "E685", {"start": v(-197.91, -270.43) * mm, "end": v(-198.88, -270) * mm});
            skLineSegment(sketch, "E686", {"start": v(-198.88, -270) * mm, "end": v(-199.86, -269.67) * mm});
            skLineSegment(sketch, "E687", {"start": v(-199.86, -269.67) * mm, "end": v(-200.83, -269.57) * mm});
            skLineSegment(sketch, "E688", {"start": v(-200.83, -263.61) * mm, "end": v(-206.46, -263.61) * mm});
            skLineSegment(sketch, "E689", {"start": v(-206.46, -263.61) * mm, "end": v(-206.46, -305.5) * mm});
            skLineSegment(sketch, "E690", {"start": v(-206.46, -305.5) * mm, "end": v(-200.83, -305.5) * mm});
            skLineSegment(sketch, "E691", {"start": v(-200.83, -305.5) * mm, "end": v(-200.83, -287.2) * mm});
            skLineSegment(sketch, "E692", {"start": v(-200.83, -287.2) * mm, "end": v(-200.4, -287.42) * mm});
            skLineSegment(sketch, "E693", {"start": v(-200.4, -287.42) * mm, "end": v(-199.54, -287.42) * mm});
            skLineSegment(sketch, "E694", {"start": v(-199.54, -287.42) * mm, "end": v(-199.1, -287.2) * mm});
            skLineSegment(sketch, "E695", {"start": v(-199.1, -287.2) * mm, "end": v(-195.86, -305.5) * mm});
            skLineSegment(sketch, "E696", {"start": v(-195.86, -305.5) * mm, "end": v(-190, -305.5) * mm});
            skLineSegment(sketch, "E697", {"start": v(-190, -305.5) * mm, "end": v(-193.47, -285.58) * mm});
            skLineSegment(sketch, "E698", {"start": v(-193.47, -285.58) * mm, "end": v(-192.6, -284.4) * mm});
            skLineSegment(sketch, "E699", {"start": v(-192.6, -284.4) * mm, "end": v(-191.96, -283.1) * mm});
            skLineSegment(sketch, "E700", {"start": v(-191.96, -283.1) * mm, "end": v(-191.3, -281.8) * mm});
            skLineSegment(sketch, "E701", {"start": v(-191.3, -281.8) * mm, "end": v(-190.87, -280.39) * mm});
            skLineSegment(sketch, "E702", {"start": v(-190.87, -280.39) * mm, "end": v(-190.44, -278.87) * mm});
            skLineSegment(sketch, "E703", {"start": v(-190.44, -278.87) * mm, "end": v(-190.23, -277.47) * mm});
            skLineSegment(sketch, "E704", {"start": v(-190.23, -277.47) * mm, "end": v(-190.23, -274.44) * mm});
            skLineSegment(sketch, "E705", {"start": v(-190.23, -274.44) * mm, "end": v(-190.44, -273.03) * mm});
            skLineSegment(sketch, "E706", {"start": v(-190.44, -273.03) * mm, "end": v(-190.87, -271.51) * mm});
            skLineSegment(sketch, "E707", {"start": v(-190.87, -271.51) * mm, "end": v(-191.3, -270.1) * mm});
            skLineSegment(sketch, "E708", {"start": v(-191.3, -270.1) * mm, "end": v(-191.96, -268.8) * mm});
            skLineSegment(sketch, "E709", {"start": v(-191.96, -268.8) * mm, "end": v(-192.6, -267.5) * mm});
            skLineSegment(sketch, "E710", {"start": v(-192.6, -267.5) * mm, "end": v(-193.47, -266.32) * mm});
            skLineSegment(sketch, "E711", {"start": v(-193.47, -266.32) * mm, "end": v(-194.56, -265.56) * mm});
            skLineSegment(sketch, "E712", {"start": v(-194.56, -265.56) * mm, "end": v(-195.75, -264.91) * mm});
            skLineSegment(sketch, "E713", {"start": v(-195.75, -264.91) * mm, "end": v(-196.93, -264.37) * mm});
            skLineSegment(sketch, "E714", {"start": v(-196.93, -264.37) * mm, "end": v(-198.24, -263.94) * mm});
            skLineSegment(sketch, "E715", {"start": v(-198.24, -263.94) * mm, "end": v(-199.54, -263.72) * mm});
            skLineSegment(sketch, "E716", {"start": v(-199.54, -263.72) * mm, "end": v(-200.83, -263.61) * mm});
            skLineSegment(sketch, "E717", {"start": v(-167.82, -263.61) * mm, "end": v(-181.57, -263.61) * mm});
            skLineSegment(sketch, "E718", {"start": v(-181.57, -263.61) * mm, "end": v(-181.57, -305.5) * mm});
            skLineSegment(sketch, "E719", {"start": v(-181.57, -305.5) * mm, "end": v(-167.82, -305.5) * mm});
            skLineSegment(sketch, "E720", {"start": v(-167.82, -305.5) * mm, "end": v(-167.82, -299.65) * mm});
            skLineSegment(sketch, "E721", {"start": v(-167.82, -299.65) * mm, "end": v(-175.83, -299.65) * mm});
            skLineSegment(sketch, "E722", {"start": v(-175.83, -299.65) * mm, "end": v(-175.83, -287.64) * mm});
            skLineSegment(sketch, "E723", {"start": v(-175.83, -287.64) * mm, "end": v(-170.1, -287.64) * mm});
            skLineSegment(sketch, "E724", {"start": v(-170.1, -287.64) * mm, "end": v(-170.1, -281.36) * mm});
            skLineSegment(sketch, "E725", {"start": v(-170.1, -281.36) * mm, "end": v(-175.83, -281.36) * mm});
            skLineSegment(sketch, "E726", {"start": v(-175.83, -281.36) * mm, "end": v(-175.83, -270.32) * mm});
            skLineSegment(sketch, "E727", {"start": v(-175.83, -270.32) * mm, "end": v(-167.82, -270.32) * mm});
            skLineSegment(sketch, "E728", {"start": v(-167.82, -270.32) * mm, "end": v(-167.82, -263.61) * mm});
            skLineSegment(sketch, "E729", {"start": v(-41.72, -263.61) * mm, "end": v(-55.47, -263.61) * mm});
            skLineSegment(sketch, "E730", {"start": v(-55.47, -263.61) * mm, "end": v(-55.47, -305.5) * mm});
            skLineSegment(sketch, "E731", {"start": v(-55.47, -305.5) * mm, "end": v(-41.72, -305.5) * mm});
            skLineSegment(sketch, "E732", {"start": v(-41.72, -305.5) * mm, "end": v(-41.72, -299.65) * mm});
            skLineSegment(sketch, "E733", {"start": v(-41.72, -299.65) * mm, "end": v(-49.73, -299.65) * mm});
            skLineSegment(sketch, "E734", {"start": v(-49.73, -299.65) * mm, "end": v(-49.73, -287.64) * mm});
            skLineSegment(sketch, "E735", {"start": v(-49.73, -287.64) * mm, "end": v(-44, -287.64) * mm});
            skLineSegment(sketch, "E736", {"start": v(-44, -287.64) * mm, "end": v(-44, -281.36) * mm});
            skLineSegment(sketch, "E737", {"start": v(-44, -281.36) * mm, "end": v(-49.73, -281.36) * mm});
            skLineSegment(sketch, "E738", {"start": v(-49.73, -281.36) * mm, "end": v(-49.73, -270.32) * mm});
            skLineSegment(sketch, "E739", {"start": v(-49.73, -270.32) * mm, "end": v(-41.72, -270.32) * mm});
            skLineSegment(sketch, "E740", {"start": v(-41.72, -270.32) * mm, "end": v(-41.72, -263.61) * mm});
            skLineSegment(sketch, "E741", {"start": v(31.01, -263.61) * mm, "end": v(17.26, -263.61) * mm});
            skLineSegment(sketch, "E742", {"start": v(17.26, -263.61) * mm, "end": v(17.26, -305.5) * mm});
            skLineSegment(sketch, "E743", {"start": v(17.26, -305.5) * mm, "end": v(31.01, -305.5) * mm});
            skLineSegment(sketch, "E744", {"start": v(31.01, -305.5) * mm, "end": v(31.01, -299.65) * mm});
            skLineSegment(sketch, "E745", {"start": v(31.01, -299.65) * mm, "end": v(23, -299.65) * mm});
            skLineSegment(sketch, "E746", {"start": v(23, -299.65) * mm, "end": v(23, -287.64) * mm});
            skLineSegment(sketch, "E747", {"start": v(23, -287.64) * mm, "end": v(28.74, -287.64) * mm});
            skLineSegment(sketch, "E748", {"start": v(28.74, -287.64) * mm, "end": v(28.74, -281.36) * mm});
            skLineSegment(sketch, "E749", {"start": v(28.74, -281.36) * mm, "end": v(23, -281.36) * mm});
            skLineSegment(sketch, "E750", {"start": v(23, -281.36) * mm, "end": v(23, -270.32) * mm});
            skLineSegment(sketch, "E751", {"start": v(23, -270.32) * mm, "end": v(31.01, -270.32) * mm});
            skLineSegment(sketch, "E752", {"start": v(31.01, -270.32) * mm, "end": v(31.01, -263.61) * mm});
            skLineSegment(sketch, "E753", {"start": v(92.38, -263.61) * mm, "end": v(78.63, -263.61) * mm});
            skLineSegment(sketch, "E754", {"start": v(78.63, -263.61) * mm, "end": v(78.63, -305.5) * mm});
            skLineSegment(sketch, "E755", {"start": v(78.63, -305.5) * mm, "end": v(92.38, -305.5) * mm});
            skLineSegment(sketch, "E756", {"start": v(92.38, -305.5) * mm, "end": v(92.38, -299.65) * mm});
            skLineSegment(sketch, "E757", {"start": v(92.38, -299.65) * mm, "end": v(84.37, -299.65) * mm});
            skLineSegment(sketch, "E758", {"start": v(84.37, -299.65) * mm, "end": v(84.37, -287.64) * mm});
            skLineSegment(sketch, "E759", {"start": v(84.37, -287.64) * mm, "end": v(90.1, -287.64) * mm});
            skLineSegment(sketch, "E760", {"start": v(90.1, -287.64) * mm, "end": v(90.1, -281.36) * mm});
            skLineSegment(sketch, "E761", {"start": v(90.1, -281.36) * mm, "end": v(84.37, -281.36) * mm});
            skLineSegment(sketch, "E762", {"start": v(84.37, -281.36) * mm, "end": v(84.37, -270.32) * mm});
            skLineSegment(sketch, "E763", {"start": v(84.37, -270.32) * mm, "end": v(92.38, -270.32) * mm});
            skLineSegment(sketch, "E764", {"start": v(92.38, -270.32) * mm, "end": v(92.38, -263.61) * mm});
            skLineSegment(sketch, "E765", {"start": v(164.47, -263.61) * mm, "end": v(150.72, -263.61) * mm});
            skLineSegment(sketch, "E766", {"start": v(150.72, -263.61) * mm, "end": v(150.72, -305.5) * mm});
            skLineSegment(sketch, "E767", {"start": v(150.72, -305.5) * mm, "end": v(164.47, -305.5) * mm});
            skLineSegment(sketch, "E768", {"start": v(164.47, -305.5) * mm, "end": v(164.47, -299.65) * mm});
            skLineSegment(sketch, "E769", {"start": v(164.47, -299.65) * mm, "end": v(156.46, -299.65) * mm});
            skLineSegment(sketch, "E770", {"start": v(156.46, -299.65) * mm, "end": v(156.46, -287.64) * mm});
            skLineSegment(sketch, "E771", {"start": v(156.46, -287.64) * mm, "end": v(162.2, -287.64) * mm});
            skLineSegment(sketch, "E772", {"start": v(162.2, -287.64) * mm, "end": v(162.2, -281.36) * mm});
            skLineSegment(sketch, "E773", {"start": v(162.2, -281.36) * mm, "end": v(156.46, -281.36) * mm});
            skLineSegment(sketch, "E774", {"start": v(156.46, -281.36) * mm, "end": v(156.46, -270.32) * mm});
            skLineSegment(sketch, "E775", {"start": v(156.46, -270.32) * mm, "end": v(164.47, -270.32) * mm});
            skLineSegment(sketch, "E776", {"start": v(164.47, -270.32) * mm, "end": v(164.47, -263.61) * mm});
            skLineSegment(sketch, "E777", {"start": v(-159.7, -297.7) * mm, "end": v(-159.7, -298.79) * mm});
            skLineSegment(sketch, "E778", {"start": v(-159.7, -298.79) * mm, "end": v(-159.49, -299.76) * mm});
            skLineSegment(sketch, "E779", {"start": v(-159.49, -299.76) * mm, "end": v(-159.16, -300.74) * mm});
            skLineSegment(sketch, "E780", {"start": v(-159.16, -300.74) * mm, "end": v(-158.73, -301.6) * mm});
            skLineSegment(sketch, "E781", {"start": v(-158.73, -301.6) * mm, "end": v(-158.08, -302.47) * mm});
            skLineSegment(sketch, "E782", {"start": v(-158.08, -302.47) * mm, "end": v(-157.43, -303.23) * mm});
            skLineSegment(sketch, "E783", {"start": v(-157.43, -303.23) * mm, "end": v(-156.67, -303.98) * mm});
            skLineSegment(sketch, "E784", {"start": v(-156.67, -303.98) * mm, "end": v(-155.8, -304.53) * mm});
            skLineSegment(sketch, "E785", {"start": v(-155.8, -304.53) * mm, "end": v(-154.94, -304.96) * mm});
            skLineSegment(sketch, "E786", {"start": v(-154.94, -304.96) * mm, "end": v(-153.97, -305.28) * mm});
            skLineSegment(sketch, "E787", {"start": v(-153.97, -305.28) * mm, "end": v(-152.88, -305.5) * mm});
            skLineSegment(sketch, "E788", {"start": v(-152.88, -305.5) * mm, "end": v(-150.94, -305.5) * mm});
            skLineSegment(sketch, "E789", {"start": v(-150.94, -305.5) * mm, "end": v(-149.85, -305.28) * mm});
            skLineSegment(sketch, "E790", {"start": v(-149.85, -305.28) * mm, "end": v(-148.88, -304.96) * mm});
            skLineSegment(sketch, "E791", {"start": v(-148.88, -304.96) * mm, "end": v(-148.01, -304.53) * mm});
            skLineSegment(sketch, "E792", {"start": v(-148.01, -304.53) * mm, "end": v(-147.15, -303.98) * mm});
            skLineSegment(sketch, "E793", {"start": v(-147.15, -303.98) * mm, "end": v(-146.39, -303.23) * mm});
            skLineSegment(sketch, "E794", {"start": v(-146.39, -303.23) * mm, "end": v(-145.74, -302.47) * mm});
            skLineSegment(sketch, "E795", {"start": v(-145.74, -302.47) * mm, "end": v(-144.66, -300.74) * mm});
            skLineSegment(sketch, "E796", {"start": v(-144.66, -300.74) * mm, "end": v(-144.33, -299.76) * mm});
            skLineSegment(sketch, "E797", {"start": v(-144.33, -299.76) * mm, "end": v(-144.22, -298.79) * mm});
            skLineSegment(sketch, "E798", {"start": v(-144.22, -298.79) * mm, "end": v(-144.12, -297.7) * mm});
            skLineSegment(sketch, "E799", {"start": v(-144.12, -297.7) * mm, "end": v(-144.12, -291.21) * mm});
            skLineSegment(sketch, "E800", {"start": v(-144.12, -291.21) * mm, "end": v(-149.74, -291.21) * mm});
            skLineSegment(sketch, "E801", {"start": v(-149.74, -291.21) * mm, "end": v(-149.74, -298.14) * mm});
            skLineSegment(sketch, "E802", {"start": v(-154.07, -298.14) * mm, "end": v(-154.07, -298.68) * mm});
            skLineSegment(sketch, "E803", {"start": v(-154.07, -298.68) * mm, "end": v(-153.86, -299.11) * mm});
            skLineSegment(sketch, "E804", {"start": v(-153.86, -299.11) * mm, "end": v(-153.64, -299.55) * mm});
            skLineSegment(sketch, "E805", {"start": v(-153.64, -299.55) * mm, "end": v(-153.32, -299.87) * mm});
            skLineSegment(sketch, "E806", {"start": v(-153.32, -299.87) * mm, "end": v(-152.88, -300.09) * mm});
            skLineSegment(sketch, "E807", {"start": v(-152.88, -300.09) * mm, "end": v(-152.45, -300.3) * mm});
            skLineSegment(sketch, "E808", {"start": v(-152.45, -300.3) * mm, "end": v(-151.48, -300.3) * mm});
            skLineSegment(sketch, "E809", {"start": v(-151.48, -300.3) * mm, "end": v(-150.94, -300.09) * mm});
            skLineSegment(sketch, "E810", {"start": v(-150.94, -300.09) * mm, "end": v(-150.61, -299.87) * mm});
            skLineSegment(sketch, "E811", {"start": v(-150.61, -299.87) * mm, "end": v(-150.18, -299.55) * mm});
            skLineSegment(sketch, "E812", {"start": v(-150.18, -299.55) * mm, "end": v(-149.96, -299.11) * mm});
            skLineSegment(sketch, "E813", {"start": v(-149.96, -299.11) * mm, "end": v(-149.74, -298.68) * mm});
            skLineSegment(sketch, "E814", {"start": v(-149.74, -298.68) * mm, "end": v(-149.74, -298.14) * mm});
            skLineSegment(sketch, "E815", {"start": v(-154.07, -298.14) * mm, "end": v(-154.07, -270.97) * mm});
            skLineSegment(sketch, "E816", {"start": v(-149.74, -270.97) * mm, "end": v(-149.74, -270.43) * mm});
            skLineSegment(sketch, "E817", {"start": v(-149.74, -270.43) * mm, "end": v(-149.96, -270) * mm});
            skLineSegment(sketch, "E818", {"start": v(-149.96, -270) * mm, "end": v(-150.18, -269.57) * mm});
            skLineSegment(sketch, "E819", {"start": v(-150.18, -269.57) * mm, "end": v(-150.61, -269.24) * mm});
            skLineSegment(sketch, "E820", {"start": v(-150.61, -269.24) * mm, "end": v(-150.94, -269.02) * mm});
            skLineSegment(sketch, "E821", {"start": v(-150.94, -269.02) * mm, "end": v(-151.48, -268.8) * mm});
            skLineSegment(sketch, "E822", {"start": v(-151.48, -268.8) * mm, "end": v(-152.45, -268.8) * mm});
            skLineSegment(sketch, "E823", {"start": v(-152.45, -268.8) * mm, "end": v(-153.32, -269.24) * mm});
            skLineSegment(sketch, "E824", {"start": v(-153.32, -269.24) * mm, "end": v(-153.64, -269.57) * mm});
            skLineSegment(sketch, "E825", {"start": v(-153.64, -269.57) * mm, "end": v(-153.86, -270) * mm});
            skLineSegment(sketch, "E826", {"start": v(-153.86, -270) * mm, "end": v(-154.07, -270.43) * mm});
            skLineSegment(sketch, "E827", {"start": v(-154.07, -270.43) * mm, "end": v(-154.07, -270.97) * mm});
            skLineSegment(sketch, "E828", {"start": v(-149.74, -270.97) * mm, "end": v(-149.74, -277.9) * mm});
            skLineSegment(sketch, "E829", {"start": v(-149.74, -277.9) * mm, "end": v(-144.12, -277.9) * mm});
            skLineSegment(sketch, "E830", {"start": v(-144.12, -277.9) * mm, "end": v(-144.12, -271.4) * mm});
            skLineSegment(sketch, "E831", {"start": v(-144.12, -271.4) * mm, "end": v(-144.22, -270.32) * mm});
            skLineSegment(sketch, "E832", {"start": v(-144.22, -270.32) * mm, "end": v(-144.33, -269.35) * mm});
            skLineSegment(sketch, "E833", {"start": v(-144.33, -269.35) * mm, "end": v(-144.66, -268.37) * mm});
            skLineSegment(sketch, "E834", {"start": v(-144.66, -268.37) * mm, "end": v(-145.2, -267.5) * mm});
            skLineSegment(sketch, "E835", {"start": v(-145.2, -267.5) * mm, "end": v(-145.74, -266.64) * mm});
            skLineSegment(sketch, "E836", {"start": v(-145.74, -266.64) * mm, "end": v(-146.39, -265.88) * mm});
            skLineSegment(sketch, "E837", {"start": v(-146.39, -265.88) * mm, "end": v(-147.15, -265.13) * mm});
            skLineSegment(sketch, "E838", {"start": v(-147.15, -265.13) * mm, "end": v(-148.01, -264.59) * mm});
            skLineSegment(sketch, "E839", {"start": v(-148.01, -264.59) * mm, "end": v(-148.88, -264.15) * mm});
            skLineSegment(sketch, "E840", {"start": v(-148.88, -264.15) * mm, "end": v(-149.85, -263.83) * mm});
            skLineSegment(sketch, "E841", {"start": v(-149.85, -263.83) * mm, "end": v(-150.94, -263.61) * mm});
            skLineSegment(sketch, "E842", {"start": v(-150.94, -263.61) * mm, "end": v(-152.88, -263.61) * mm});
            skLineSegment(sketch, "E843", {"start": v(-152.88, -263.61) * mm, "end": v(-153.97, -263.83) * mm});
            skLineSegment(sketch, "E844", {"start": v(-153.97, -263.83) * mm, "end": v(-154.94, -264.15) * mm});
            skLineSegment(sketch, "E845", {"start": v(-154.94, -264.15) * mm, "end": v(-155.8, -264.59) * mm});
            skLineSegment(sketch, "E846", {"start": v(-155.8, -264.59) * mm, "end": v(-156.67, -265.13) * mm});
            skLineSegment(sketch, "E847", {"start": v(-156.67, -265.13) * mm, "end": v(-157.43, -265.88) * mm});
            skLineSegment(sketch, "E848", {"start": v(-157.43, -265.88) * mm, "end": v(-158.08, -266.64) * mm});
            skLineSegment(sketch, "E849", {"start": v(-158.08, -266.64) * mm, "end": v(-158.73, -267.5) * mm});
            skLineSegment(sketch, "E850", {"start": v(-158.73, -267.5) * mm, "end": v(-159.16, -268.37) * mm});
            skLineSegment(sketch, "E851", {"start": v(-159.16, -268.37) * mm, "end": v(-159.49, -269.35) * mm});
            skLineSegment(sketch, "E852", {"start": v(-159.49, -269.35) * mm, "end": v(-159.7, -270.32) * mm});
            skLineSegment(sketch, "E853", {"start": v(-159.7, -270.32) * mm, "end": v(-159.7, -271.4) * mm});
            skLineSegment(sketch, "E854", {"start": v(-159.7, -271.4) * mm, "end": v(-159.7, -297.7) * mm});
            skLineSegment(sketch, "E855", {"start": v(-119.87, -263.61) * mm, "end": v(-136.97, -263.61) * mm});
            skLineSegment(sketch, "E856", {"start": v(-136.97, -263.61) * mm, "end": v(-136.97, -270.32) * mm});
            skLineSegment(sketch, "E857", {"start": v(-136.97, -270.32) * mm, "end": v(-131.56, -270.32) * mm});
            skLineSegment(sketch, "E858", {"start": v(-131.56, -270.32) * mm, "end": v(-131.56, -305.5) * mm});
            skLineSegment(sketch, "E859", {"start": v(-131.56, -305.5) * mm, "end": v(-125.6, -305.5) * mm});
            skLineSegment(sketch, "E860", {"start": v(-125.6, -305.5) * mm, "end": v(-125.6, -270.32) * mm});
            skLineSegment(sketch, "E861", {"start": v(-125.6, -270.32) * mm, "end": v(-119.87, -270.32) * mm});
            skLineSegment(sketch, "E862", {"start": v(-119.87, -270.32) * mm, "end": v(-119.87, -263.61) * mm});
            skLineSegment(sketch, "E863", {"start": v(9.58, -263.61) * mm, "end": v(-7.52, -263.61) * mm});
            skLineSegment(sketch, "E864", {"start": v(-7.52, -263.61) * mm, "end": v(-7.52, -270.32) * mm});
            skLineSegment(sketch, "E865", {"start": v(-7.52, -270.32) * mm, "end": v(-2.1, -270.32) * mm});
            skLineSegment(sketch, "E866", {"start": v(-2.1, -270.32) * mm, "end": v(-2.1, -305.5) * mm});
            skLineSegment(sketch, "E867", {"start": v(-2.1, -305.5) * mm, "end": v(3.74, -305.5) * mm});
            skLineSegment(sketch, "E868", {"start": v(3.74, -305.5) * mm, "end": v(3.74, -270.32) * mm});
            skLineSegment(sketch, "E869", {"start": v(3.74, -270.32) * mm, "end": v(9.58, -270.32) * mm});
            skLineSegment(sketch, "E870", {"start": v(9.58, -270.32) * mm, "end": v(9.58, -263.61) * mm});
            skLineSegment(sketch, "E871", {"start": v(110.35, -270.97) * mm, "end": v(110.35, -274.33) * mm});
            skLineSegment(sketch, "E872", {"start": v(110.35, -274.33) * mm, "end": v(116.08, -274.33) * mm});
            skLineSegment(sketch, "E873", {"start": v(116.08, -274.33) * mm, "end": v(116.08, -271.4) * mm});
            skLineSegment(sketch, "E874", {"start": v(116.08, -271.4) * mm, "end": v(115.98, -270.32) * mm});
            skLineSegment(sketch, "E875", {"start": v(115.98, -270.32) * mm, "end": v(115.76, -269.35) * mm});
            skLineSegment(sketch, "E876", {"start": v(115.76, -269.35) * mm, "end": v(115.43, -268.37) * mm});
            skLineSegment(sketch, "E877", {"start": v(115.43, -268.37) * mm, "end": v(115, -267.5) * mm});
            skLineSegment(sketch, "E878", {"start": v(115, -267.5) * mm, "end": v(114.46, -266.64) * mm});
            skLineSegment(sketch, "E879", {"start": v(114.46, -266.64) * mm, "end": v(113.7, -265.88) * mm});
            skLineSegment(sketch, "E880", {"start": v(113.7, -265.88) * mm, "end": v(112.95, -265.24) * mm});
            skLineSegment(sketch, "E881", {"start": v(112.95, -265.24) * mm, "end": v(112.08, -264.59) * mm});
            skLineSegment(sketch, "E882", {"start": v(112.08, -264.59) * mm, "end": v(111.21, -264.15) * mm});
            skLineSegment(sketch, "E883", {"start": v(111.21, -264.15) * mm, "end": v(110.24, -263.83) * mm});
            skLineSegment(sketch, "E884", {"start": v(110.24, -263.83) * mm, "end": v(109.26, -263.61) * mm});
            skLineSegment(sketch, "E885", {"start": v(109.26, -263.61) * mm, "end": v(107.2, -263.61) * mm});
            skLineSegment(sketch, "E886", {"start": v(107.2, -263.61) * mm, "end": v(106.23, -263.83) * mm});
            skLineSegment(sketch, "E887", {"start": v(106.23, -263.83) * mm, "end": v(105.26, -264.15) * mm});
            skLineSegment(sketch, "E888", {"start": v(105.26, -264.15) * mm, "end": v(104.29, -264.59) * mm});
            skLineSegment(sketch, "E889", {"start": v(104.29, -264.59) * mm, "end": v(103.53, -265.24) * mm});
            skLineSegment(sketch, "E890", {"start": v(103.53, -265.24) * mm, "end": v(102.67, -265.88) * mm});
            skLineSegment(sketch, "E891", {"start": v(102.67, -265.88) * mm, "end": v(102.02, -266.64) * mm});
            skLineSegment(sketch, "E892", {"start": v(102.02, -266.64) * mm, "end": v(101.47, -267.5) * mm});
            skLineSegment(sketch, "E893", {"start": v(101.47, -267.5) * mm, "end": v(101.04, -268.37) * mm});
            skLineSegment(sketch, "E894", {"start": v(101.04, -268.37) * mm, "end": v(100.72, -269.35) * mm});
            skLineSegment(sketch, "E895", {"start": v(100.72, -269.35) * mm, "end": v(100.5, -270.32) * mm});
            skLineSegment(sketch, "E896", {"start": v(100.5, -270.32) * mm, "end": v(100.39, -271.4) * mm});
            skLineSegment(sketch, "E897", {"start": v(100.39, -271.4) * mm, "end": v(100.39, -274.33) * mm});
            skLineSegment(sketch, "E898", {"start": v(100.39, -274.33) * mm, "end": v(101.04, -276.28) * mm});
            skLineSegment(sketch, "E899", {"start": v(101.04, -276.28) * mm, "end": v(101.69, -278.22) * mm});
            skLineSegment(sketch, "E900", {"start": v(101.69, -278.22) * mm, "end": v(102.56, -280.06) * mm});
            skLineSegment(sketch, "E901", {"start": v(102.56, -280.06) * mm, "end": v(103.53, -281.9) * mm});
            skLineSegment(sketch, "E902", {"start": v(103.53, -281.9) * mm, "end": v(104.72, -283.64) * mm});
            skLineSegment(sketch, "E903", {"start": v(104.72, -283.64) * mm, "end": v(105.9, -285.26) * mm});
            skLineSegment(sketch, "E904", {"start": v(110.78, -293.49) * mm, "end": v(108.4, -289.37) * mm});
            skLineSegment(sketch, "E905", {"start": v(108.4, -289.37) * mm, "end": v(105.9, -285.26) * mm});
            skLineSegment(sketch, "E906", {"start": v(110.78, -293.49) * mm, "end": v(110.78, -297.49) * mm});
            skLineSegment(sketch, "E907", {"start": v(105.05, -298.14) * mm, "end": v(105.26, -298.68) * mm});
            skLineSegment(sketch, "E908", {"start": v(105.26, -298.68) * mm, "end": v(105.59, -299.22) * mm});
            skLineSegment(sketch, "E909", {"start": v(105.59, -299.22) * mm, "end": v(105.9, -299.65) * mm});
            skLineSegment(sketch, "E910", {"start": v(105.9, -299.65) * mm, "end": v(106.34, -299.98) * mm});
            skLineSegment(sketch, "E911", {"start": v(106.34, -299.98) * mm, "end": v(106.88, -300.2) * mm});
            skLineSegment(sketch, "E912", {"start": v(106.88, -300.2) * mm, "end": v(107.43, -300.3) * mm});
            skLineSegment(sketch, "E913", {"start": v(107.43, -300.3) * mm, "end": v(107.97, -300.41) * mm});
            skLineSegment(sketch, "E914", {"start": v(107.97, -300.41) * mm, "end": v(108.51, -300.3) * mm});
            skLineSegment(sketch, "E915", {"start": v(108.51, -300.3) * mm, "end": v(109.05, -300.2) * mm});
            skLineSegment(sketch, "E916", {"start": v(109.05, -300.2) * mm, "end": v(109.59, -299.87) * mm});
            skLineSegment(sketch, "E917", {"start": v(109.59, -299.87) * mm, "end": v(110.02, -299.55) * mm});
            skLineSegment(sketch, "E918", {"start": v(110.02, -299.55) * mm, "end": v(110.35, -299.11) * mm});
            skLineSegment(sketch, "E919", {"start": v(110.35, -299.11) * mm, "end": v(110.78, -298.03) * mm});
            skLineSegment(sketch, "E920", {"start": v(110.78, -298.03) * mm, "end": v(110.78, -297.49) * mm});
            skLineSegment(sketch, "E921", {"start": v(105.05, -298.14) * mm, "end": v(105.05, -293.49) * mm});
            skLineSegment(sketch, "E922", {"start": v(105.05, -293.49) * mm, "end": v(99.52, -293.49) * mm});
            skLineSegment(sketch, "E923", {"start": v(99.52, -293.49) * mm, "end": v(99.52, -297.7) * mm});
            skLineSegment(sketch, "E924", {"start": v(99.52, -297.7) * mm, "end": v(99.63, -298.68) * mm});
            skLineSegment(sketch, "E925", {"start": v(99.63, -298.68) * mm, "end": v(99.85, -299.65) * mm});
            skLineSegment(sketch, "E926", {"start": v(99.85, -299.65) * mm, "end": v(100.17, -300.63) * mm});
            skLineSegment(sketch, "E927", {"start": v(100.17, -300.63) * mm, "end": v(100.72, -301.5) * mm});
            skLineSegment(sketch, "E928", {"start": v(100.72, -301.5) * mm, "end": v(101.26, -302.36) * mm});
            skLineSegment(sketch, "E929", {"start": v(101.26, -302.36) * mm, "end": v(101.9, -303.12) * mm});
            skLineSegment(sketch, "E930", {"start": v(101.9, -303.12) * mm, "end": v(102.67, -303.77) * mm});
            skLineSegment(sketch, "E931", {"start": v(102.67, -303.77) * mm, "end": v(103.53, -304.3) * mm});
            skLineSegment(sketch, "E932", {"start": v(103.53, -304.3) * mm, "end": v(104.4, -304.85) * mm});
            skLineSegment(sketch, "E933", {"start": v(104.4, -304.85) * mm, "end": v(105.26, -305.18) * mm});
            skLineSegment(sketch, "E934", {"start": v(105.26, -305.18) * mm, "end": v(106.23, -305.4) * mm});
            skLineSegment(sketch, "E935", {"start": v(106.23, -305.4) * mm, "end": v(107.32, -305.5) * mm});
            skLineSegment(sketch, "E936", {"start": v(107.32, -305.5) * mm, "end": v(108.3, -305.5) * mm});
            skLineSegment(sketch, "E937", {"start": v(108.3, -305.5) * mm, "end": v(109.26, -305.4) * mm});
            skLineSegment(sketch, "E938", {"start": v(109.26, -305.4) * mm, "end": v(110.24, -305.18) * mm});
            skLineSegment(sketch, "E939", {"start": v(110.24, -305.18) * mm, "end": v(111.21, -304.85) * mm});
            skLineSegment(sketch, "E940", {"start": v(111.21, -304.85) * mm, "end": v(112.08, -304.3) * mm});
            skLineSegment(sketch, "E941", {"start": v(112.08, -304.3) * mm, "end": v(112.95, -303.77) * mm});
            skLineSegment(sketch, "E942", {"start": v(112.95, -303.77) * mm, "end": v(114.35, -302.36) * mm});
            skLineSegment(sketch, "E943", {"start": v(114.35, -302.36) * mm, "end": v(114.9, -301.5) * mm});
            skLineSegment(sketch, "E944", {"start": v(114.9, -301.5) * mm, "end": v(115.33, -300.63) * mm});
            skLineSegment(sketch, "E945", {"start": v(115.33, -300.63) * mm, "end": v(115.65, -299.65) * mm});
            skLineSegment(sketch, "E946", {"start": v(115.65, -299.65) * mm, "end": v(115.87, -298.68) * mm});
            skLineSegment(sketch, "E947", {"start": v(115.87, -298.68) * mm, "end": v(116.08, -297.7) * mm});
            skLineSegment(sketch, "E948", {"start": v(116.08, -297.7) * mm, "end": v(116.08, -293.49) * mm});
            skLineSegment(sketch, "E949", {"start": v(116.08, -293.49) * mm, "end": v(115.43, -291.43) * mm});
            skLineSegment(sketch, "E950", {"start": v(115.43, -291.43) * mm, "end": v(114.68, -289.37) * mm});
            skLineSegment(sketch, "E951", {"start": v(114.68, -289.37) * mm, "end": v(113.81, -287.42) * mm});
            skLineSegment(sketch, "E952", {"start": v(113.81, -287.42) * mm, "end": v(112.73, -285.48) * mm});
            skLineSegment(sketch, "E953", {"start": v(112.73, -285.48) * mm, "end": v(111.65, -283.64) * mm});
            skLineSegment(sketch, "E954", {"start": v(111.65, -283.64) * mm, "end": v(110.35, -281.9) * mm});
            skLineSegment(sketch, "E955", {"start": v(106.02, -274.33) * mm, "end": v(107, -276.38) * mm});
            skLineSegment(sketch, "E956", {"start": v(107, -276.38) * mm, "end": v(107.97, -278.22) * mm});
            skLineSegment(sketch, "E957", {"start": v(107.97, -278.22) * mm, "end": v(109.16, -280.06) * mm});
            skLineSegment(sketch, "E958", {"start": v(109.16, -280.06) * mm, "end": v(110.35, -281.9) * mm});
            skLineSegment(sketch, "E959", {"start": v(106.02, -274.33) * mm, "end": v(106.02, -270.97) * mm});
            skLineSegment(sketch, "E960", {"start": v(110.35, -270.97) * mm, "end": v(110.35, -270.43) * mm});
            skLineSegment(sketch, "E961", {"start": v(110.35, -270.43) * mm, "end": v(110.13, -270) * mm});
            skLineSegment(sketch, "E962", {"start": v(110.13, -270) * mm, "end": v(109.91, -269.57) * mm});
            skLineSegment(sketch, "E963", {"start": v(109.91, -269.57) * mm, "end": v(109.59, -269.24) * mm});
            skLineSegment(sketch, "E964", {"start": v(109.59, -269.24) * mm, "end": v(109.16, -269.02) * mm});
            skLineSegment(sketch, "E965", {"start": v(109.16, -269.02) * mm, "end": v(108.73, -268.8) * mm});
            skLineSegment(sketch, "E966", {"start": v(108.73, -268.8) * mm, "end": v(107.75, -268.8) * mm});
            skLineSegment(sketch, "E967", {"start": v(107.75, -268.8) * mm, "end": v(107.32, -269.02) * mm});
            skLineSegment(sketch, "E968", {"start": v(107.32, -269.02) * mm, "end": v(106.88, -269.24) * mm});
            skLineSegment(sketch, "E969", {"start": v(106.88, -269.24) * mm, "end": v(106.56, -269.57) * mm});
            skLineSegment(sketch, "E970", {"start": v(106.56, -269.57) * mm, "end": v(106.23, -270) * mm});
            skLineSegment(sketch, "E971", {"start": v(106.23, -270) * mm, "end": v(106.13, -270.43) * mm});
            skLineSegment(sketch, "E972", {"start": v(106.13, -270.43) * mm, "end": v(106.02, -270.97) * mm});
            skLineSegment(sketch, "E973", {"start": v(242.94, -270.97) * mm, "end": v(242.94, -274.33) * mm});
            skLineSegment(sketch, "E974", {"start": v(242.94, -274.33) * mm, "end": v(248.57, -274.33) * mm});
            skLineSegment(sketch, "E975", {"start": v(248.57, -274.33) * mm, "end": v(248.57, -271.4) * mm});
            skLineSegment(sketch, "E976", {"start": v(248.57, -271.4) * mm, "end": v(248.57, -270.32) * mm});
            skLineSegment(sketch, "E977", {"start": v(248.57, -270.32) * mm, "end": v(248.35, -269.35) * mm});
            skLineSegment(sketch, "E978", {"start": v(248.35, -269.35) * mm, "end": v(248.03, -268.37) * mm});
            skLineSegment(sketch, "E979", {"start": v(248.03, -268.37) * mm, "end": v(247.48, -267.5) * mm});
            skLineSegment(sketch, "E980", {"start": v(247.48, -267.5) * mm, "end": v(246.94, -266.64) * mm});
            skLineSegment(sketch, "E981", {"start": v(246.94, -266.64) * mm, "end": v(246.3, -265.88) * mm});
            skLineSegment(sketch, "E982", {"start": v(246.3, -265.88) * mm, "end": v(245.54, -265.24) * mm});
            skLineSegment(sketch, "E983", {"start": v(245.54, -265.24) * mm, "end": v(244.67, -264.59) * mm});
            skLineSegment(sketch, "E984", {"start": v(244.67, -264.59) * mm, "end": v(243.8, -264.15) * mm});
            skLineSegment(sketch, "E985", {"start": v(243.8, -264.15) * mm, "end": v(242.83, -263.83) * mm});
            skLineSegment(sketch, "E986", {"start": v(242.83, -263.83) * mm, "end": v(241.75, -263.61) * mm});
            skLineSegment(sketch, "E987", {"start": v(241.75, -263.61) * mm, "end": v(239.8, -263.61) * mm});
            skLineSegment(sketch, "E988", {"start": v(239.8, -263.61) * mm, "end": v(238.72, -263.83) * mm});
            skLineSegment(sketch, "E989", {"start": v(238.72, -263.83) * mm, "end": v(237.74, -264.15) * mm});
            skLineSegment(sketch, "E990", {"start": v(237.74, -264.15) * mm, "end": v(236.88, -264.59) * mm});
            skLineSegment(sketch, "E991", {"start": v(236.88, -264.59) * mm, "end": v(236.01, -265.24) * mm});
            skLineSegment(sketch, "E992", {"start": v(236.01, -265.24) * mm, "end": v(235.25, -265.88) * mm});
            skLineSegment(sketch, "E993", {"start": v(235.25, -265.88) * mm, "end": v(234.6, -266.64) * mm});
            skLineSegment(sketch, "E994", {"start": v(234.6, -266.64) * mm, "end": v(234.07, -267.5) * mm});
            skLineSegment(sketch, "E995", {"start": v(234.07, -267.5) * mm, "end": v(233.52, -268.37) * mm});
            skLineSegment(sketch, "E996", {"start": v(233.52, -268.37) * mm, "end": v(233.2, -269.35) * mm});
            skLineSegment(sketch, "E997", {"start": v(233.2, -269.35) * mm, "end": v(233.09, -270.32) * mm});
            skLineSegment(sketch, "E998", {"start": v(233.09, -270.32) * mm, "end": v(232.98, -271.4) * mm});
            skLineSegment(sketch, "E999", {"start": v(232.98, -271.4) * mm, "end": v(232.98, -274.33) * mm});
            skLineSegment(sketch, "E1000", {"start": v(232.98, -274.33) * mm, "end": v(233.52, -276.28) * mm});
            skLineSegment(sketch, "E1001", {"start": v(233.52, -276.28) * mm, "end": v(234.28, -278.22) * mm});
            skLineSegment(sketch, "E1002", {"start": v(234.28, -278.22) * mm, "end": v(235.14, -280.06) * mm});
            skLineSegment(sketch, "E1003", {"start": v(235.14, -280.06) * mm, "end": v(236.12, -281.9) * mm});
            skLineSegment(sketch, "E1004", {"start": v(236.12, -281.9) * mm, "end": v(237.2, -283.64) * mm});
            skLineSegment(sketch, "E1005", {"start": v(237.2, -283.64) * mm, "end": v(238.5, -285.26) * mm});
            skLineSegment(sketch, "E1006", {"start": v(243.37, -293.49) * mm, "end": v(241, -289.37) * mm});
            skLineSegment(sketch, "E1007", {"start": v(241, -289.37) * mm, "end": v(238.5, -285.26) * mm});
            skLineSegment(sketch, "E1008", {"start": v(243.37, -293.49) * mm, "end": v(243.37, -297.49) * mm});
            skLineSegment(sketch, "E1009", {"start": v(237.63, -298.14) * mm, "end": v(237.85, -298.68) * mm});
            skLineSegment(sketch, "E1010", {"start": v(237.85, -298.68) * mm, "end": v(238.07, -299.22) * mm});
            skLineSegment(sketch, "E1011", {"start": v(238.07, -299.22) * mm, "end": v(238.5, -299.65) * mm});
            skLineSegment(sketch, "E1012", {"start": v(238.5, -299.65) * mm, "end": v(238.93, -299.98) * mm});
            skLineSegment(sketch, "E1013", {"start": v(238.93, -299.98) * mm, "end": v(239.48, -300.2) * mm});
            skLineSegment(sketch, "E1014", {"start": v(239.48, -300.2) * mm, "end": v(240.02, -300.3) * mm});
            skLineSegment(sketch, "E1015", {"start": v(240.02, -300.3) * mm, "end": v(240.55, -300.41) * mm});
            skLineSegment(sketch, "E1016", {"start": v(240.55, -300.41) * mm, "end": v(241.1, -300.3) * mm});
            skLineSegment(sketch, "E1017", {"start": v(241.1, -300.3) * mm, "end": v(241.64, -300.2) * mm});
            skLineSegment(sketch, "E1018", {"start": v(241.64, -300.2) * mm, "end": v(242.07, -299.87) * mm});
            skLineSegment(sketch, "E1019", {"start": v(242.07, -299.87) * mm, "end": v(242.5, -299.55) * mm});
            skLineSegment(sketch, "E1020", {"start": v(242.5, -299.55) * mm, "end": v(242.94, -299.11) * mm});
            skLineSegment(sketch, "E1021", {"start": v(242.94, -299.11) * mm, "end": v(243.16, -298.57) * mm});
            skLineSegment(sketch, "E1022", {"start": v(243.16, -298.57) * mm, "end": v(243.37, -297.49) * mm});
            skLineSegment(sketch, "E1023", {"start": v(237.63, -298.14) * mm, "end": v(237.63, -293.49) * mm});
            skLineSegment(sketch, "E1024", {"start": v(237.63, -293.49) * mm, "end": v(232.12, -293.49) * mm});
            skLineSegment(sketch, "E1025", {"start": v(232.12, -293.49) * mm, "end": v(232.12, -297.7) * mm});
            skLineSegment(sketch, "E1026", {"start": v(232.12, -297.7) * mm, "end": v(232.22, -298.68) * mm});
            skLineSegment(sketch, "E1027", {"start": v(232.22, -298.68) * mm, "end": v(232.44, -299.65) * mm});
            skLineSegment(sketch, "E1028", {"start": v(232.44, -299.65) * mm, "end": v(232.76, -300.63) * mm});
            skLineSegment(sketch, "E1029", {"start": v(232.76, -300.63) * mm, "end": v(233.2, -301.5) * mm});
            skLineSegment(sketch, "E1030", {"start": v(233.2, -301.5) * mm, "end": v(233.85, -302.36) * mm});
            skLineSegment(sketch, "E1031", {"start": v(233.85, -302.36) * mm, "end": v(234.5, -303.12) * mm});
            skLineSegment(sketch, "E1032", {"start": v(234.5, -303.12) * mm, "end": v(235.25, -303.77) * mm});
            skLineSegment(sketch, "E1033", {"start": v(235.25, -303.77) * mm, "end": v(236.01, -304.3) * mm});
            skLineSegment(sketch, "E1034", {"start": v(236.01, -304.3) * mm, "end": v(236.88, -304.85) * mm});
            skLineSegment(sketch, "E1035", {"start": v(236.88, -304.85) * mm, "end": v(237.85, -305.18) * mm});
            skLineSegment(sketch, "E1036", {"start": v(237.85, -305.18) * mm, "end": v(238.83, -305.4) * mm});
            skLineSegment(sketch, "E1037", {"start": v(238.83, -305.4) * mm, "end": v(239.8, -305.5) * mm});
            skLineSegment(sketch, "E1038", {"start": v(239.8, -305.5) * mm, "end": v(240.77, -305.5) * mm});
            skLineSegment(sketch, "E1039", {"start": v(240.77, -305.5) * mm, "end": v(241.86, -305.4) * mm});
            skLineSegment(sketch, "E1040", {"start": v(241.86, -305.4) * mm, "end": v(242.83, -305.18) * mm});
            skLineSegment(sketch, "E1041", {"start": v(242.83, -305.18) * mm, "end": v(243.7, -304.85) * mm});
            skLineSegment(sketch, "E1042", {"start": v(243.7, -304.85) * mm, "end": v(244.67, -304.3) * mm});
            skLineSegment(sketch, "E1043", {"start": v(244.67, -304.3) * mm, "end": v(245.43, -303.77) * mm});
            skLineSegment(sketch, "E1044", {"start": v(245.43, -303.77) * mm, "end": v(246.19, -303.12) * mm});
            skLineSegment(sketch, "E1045", {"start": v(246.19, -303.12) * mm, "end": v(246.83, -302.36) * mm});
            skLineSegment(sketch, "E1046", {"start": v(246.83, -302.36) * mm, "end": v(247.38, -301.5) * mm});
            skLineSegment(sketch, "E1047", {"start": v(247.38, -301.5) * mm, "end": v(247.92, -300.63) * mm});
            skLineSegment(sketch, "E1048", {"start": v(247.92, -300.63) * mm, "end": v(248.24, -299.65) * mm});
            skLineSegment(sketch, "E1049", {"start": v(248.24, -299.65) * mm, "end": v(248.46, -298.68) * mm});
            skLineSegment(sketch, "E1050", {"start": v(248.46, -298.68) * mm, "end": v(248.57, -297.7) * mm});
            skLineSegment(sketch, "E1051", {"start": v(248.57, -297.7) * mm, "end": v(248.57, -293.49) * mm});
            skLineSegment(sketch, "E1052", {"start": v(248.57, -293.49) * mm, "end": v(247.92, -291.43) * mm});
            skLineSegment(sketch, "E1053", {"start": v(247.92, -291.43) * mm, "end": v(247.16, -289.37) * mm});
            skLineSegment(sketch, "E1054", {"start": v(247.16, -289.37) * mm, "end": v(246.3, -287.42) * mm});
            skLineSegment(sketch, "E1055", {"start": v(246.3, -287.42) * mm, "end": v(245.32, -285.48) * mm});
            skLineSegment(sketch, "E1056", {"start": v(245.32, -285.48) * mm, "end": v(244.24, -283.64) * mm});
            skLineSegment(sketch, "E1057", {"start": v(244.24, -283.64) * mm, "end": v(242.94, -281.9) * mm});
            skLineSegment(sketch, "E1058", {"start": v(238.6, -274.33) * mm, "end": v(239.48, -276.38) * mm});
            skLineSegment(sketch, "E1059", {"start": v(239.48, -276.38) * mm, "end": v(240.55, -278.22) * mm});
            skLineSegment(sketch, "E1060", {"start": v(240.55, -278.22) * mm, "end": v(241.64, -280.06) * mm});
            skLineSegment(sketch, "E1061", {"start": v(241.64, -280.06) * mm, "end": v(242.94, -281.9) * mm});
            skLineSegment(sketch, "E1062", {"start": v(238.6, -274.33) * mm, "end": v(238.6, -270.97) * mm});
            skLineSegment(sketch, "E1063", {"start": v(242.94, -270.97) * mm, "end": v(242.94, -270.43) * mm});
            skLineSegment(sketch, "E1064", {"start": v(242.94, -270.43) * mm, "end": v(242.72, -270) * mm});
            skLineSegment(sketch, "E1065", {"start": v(242.72, -270) * mm, "end": v(242.5, -269.57) * mm});
            skLineSegment(sketch, "E1066", {"start": v(242.5, -269.57) * mm, "end": v(242.18, -269.24) * mm});
            skLineSegment(sketch, "E1067", {"start": v(242.18, -269.24) * mm, "end": v(241.75, -269.02) * mm});
            skLineSegment(sketch, "E1068", {"start": v(241.75, -269.02) * mm, "end": v(241.2, -268.8) * mm});
            skLineSegment(sketch, "E1069", {"start": v(241.2, -268.8) * mm, "end": v(240.34, -268.8) * mm});
            skLineSegment(sketch, "E1070", {"start": v(240.34, -268.8) * mm, "end": v(239.8, -269.02) * mm});
            skLineSegment(sketch, "E1071", {"start": v(239.8, -269.02) * mm, "end": v(239.48, -269.24) * mm});
            skLineSegment(sketch, "E1072", {"start": v(239.48, -269.24) * mm, "end": v(239.04, -269.57) * mm});
            skLineSegment(sketch, "E1073", {"start": v(239.04, -269.57) * mm, "end": v(238.83, -270) * mm});
            skLineSegment(sketch, "E1074", {"start": v(238.83, -270) * mm, "end": v(238.6, -270.43) * mm});
            skLineSegment(sketch, "E1075", {"start": v(238.6, -270.43) * mm, "end": v(238.6, -270.97) * mm});
            skLineSegment(sketch, "E1076", {"start": v(-105.48, -274.44) * mm, "end": v(-103.1, -290.89) * mm});
            skLineSegment(sketch, "E1077", {"start": v(-103.1, -290.89) * mm, "end": v(-107.86, -290.89) * mm});
            skLineSegment(sketch, "E1078", {"start": v(-107.86, -290.89) * mm, "end": v(-105.48, -274.44) * mm});
            skLineSegment(sketch, "E1079", {"start": v(-101.8, -263.61) * mm, "end": v(-109.16, -263.61) * mm});
            skLineSegment(sketch, "E1080", {"start": v(-109.16, -263.61) * mm, "end": v(-115.22, -305.5) * mm});
            skLineSegment(sketch, "E1081", {"start": v(-115.22, -305.5) * mm, "end": v(-110.02, -305.5) * mm});
            skLineSegment(sketch, "E1082", {"start": v(-110.02, -305.5) * mm, "end": v(-108.72, -297.27) * mm});
            skLineSegment(sketch, "E1083", {"start": v(-108.72, -297.27) * mm, "end": v(-102.12, -297.27) * mm});
            skLineSegment(sketch, "E1084", {"start": v(-102.12, -297.27) * mm, "end": v(-100.93, -305.5) * mm});
            skLineSegment(sketch, "E1085", {"start": v(-100.93, -305.5) * mm, "end": v(-95.63, -305.5) * mm});
            skLineSegment(sketch, "E1086", {"start": v(-95.63, -305.5) * mm, "end": v(-101.8, -263.61) * mm});
            skLineSegment(sketch, "E1087", {"start": v(191.74, -263.61) * mm, "end": v(185.9, -263.61) * mm});
            skLineSegment(sketch, "E1088", {"start": v(185.9, -263.61) * mm, "end": v(185.9, -305.5) * mm});
            skLineSegment(sketch, "E1089", {"start": v(185.9, -305.5) * mm, "end": v(199.75, -305.5) * mm});
            skLineSegment(sketch, "E1090", {"start": v(199.75, -305.5) * mm, "end": v(199.75, -300.3) * mm});
            skLineSegment(sketch, "E1091", {"start": v(199.75, -300.3) * mm, "end": v(191.74, -300.3) * mm});
            skLineSegment(sketch, "E1092", {"start": v(191.74, -300.3) * mm, "end": v(191.74, -263.61) * mm});
            skLineSegment(sketch, "E1093", {"start": v(217.07, -270.97) * mm, "end": v(217.07, -298.14) * mm});
            skLineSegment(sketch, "E1094", {"start": v(212.74, -298.14) * mm, "end": v(212.74, -298.68) * mm});
            skLineSegment(sketch, "E1095", {"start": v(212.74, -298.68) * mm, "end": v(212.96, -299.11) * mm});
            skLineSegment(sketch, "E1096", {"start": v(212.96, -299.11) * mm, "end": v(213.17, -299.55) * mm});
            skLineSegment(sketch, "E1097", {"start": v(213.17, -299.55) * mm, "end": v(213.6, -299.87) * mm});
            skLineSegment(sketch, "E1098", {"start": v(213.6, -299.87) * mm, "end": v(213.93, -300.09) * mm});
            skLineSegment(sketch, "E1099", {"start": v(213.93, -300.09) * mm, "end": v(214.47, -300.3) * mm});
            skLineSegment(sketch, "E1100", {"start": v(214.47, -300.3) * mm, "end": v(215.45, -300.3) * mm});
            skLineSegment(sketch, "E1101", {"start": v(215.45, -300.3) * mm, "end": v(215.88, -300.09) * mm});
            skLineSegment(sketch, "E1102", {"start": v(215.88, -300.09) * mm, "end": v(216.31, -299.87) * mm});
            skLineSegment(sketch, "E1103", {"start": v(216.31, -299.87) * mm, "end": v(216.64, -299.55) * mm});
            skLineSegment(sketch, "E1104", {"start": v(216.64, -299.55) * mm, "end": v(216.85, -299.11) * mm});
            skLineSegment(sketch, "E1105", {"start": v(216.85, -299.11) * mm, "end": v(217.07, -298.68) * mm});
            skLineSegment(sketch, "E1106", {"start": v(217.07, -298.68) * mm, "end": v(217.07, -298.14) * mm});
            skLineSegment(sketch, "E1107", {"start": v(212.74, -298.14) * mm, "end": v(212.74, -270.97) * mm});
            skLineSegment(sketch, "E1108", {"start": v(217.07, -270.97) * mm, "end": v(217.07, -270.43) * mm});
            skLineSegment(sketch, "E1109", {"start": v(217.07, -270.43) * mm, "end": v(216.64, -269.57) * mm});
            skLineSegment(sketch, "E1110", {"start": v(216.64, -269.57) * mm, "end": v(216.31, -269.24) * mm});
            skLineSegment(sketch, "E1111", {"start": v(216.31, -269.24) * mm, "end": v(215.88, -269.02) * mm});
            skLineSegment(sketch, "E1112", {"start": v(215.88, -269.02) * mm, "end": v(215.45, -268.8) * mm});
            skLineSegment(sketch, "E1113", {"start": v(215.45, -268.8) * mm, "end": v(214.47, -268.8) * mm});
            skLineSegment(sketch, "E1114", {"start": v(214.47, -268.8) * mm, "end": v(213.93, -269.02) * mm});
            skLineSegment(sketch, "E1115", {"start": v(213.93, -269.02) * mm, "end": v(213.6, -269.24) * mm});
            skLineSegment(sketch, "E1116", {"start": v(213.6, -269.24) * mm, "end": v(213.17, -269.57) * mm});
            skLineSegment(sketch, "E1117", {"start": v(213.17, -269.57) * mm, "end": v(212.96, -270) * mm});
            skLineSegment(sketch, "E1118", {"start": v(212.96, -270) * mm, "end": v(212.74, -270.43) * mm});
            skLineSegment(sketch, "E1119", {"start": v(212.74, -270.43) * mm, "end": v(212.74, -270.97) * mm});
            skLineSegment(sketch, "E1120", {"start": v(207.11, -271.4) * mm, "end": v(207.11, -297.7) * mm});
            skLineSegment(sketch, "E1121", {"start": v(207.11, -297.7) * mm, "end": v(207.22, -298.79) * mm});
            skLineSegment(sketch, "E1122", {"start": v(207.22, -298.79) * mm, "end": v(207.33, -299.76) * mm});
            skLineSegment(sketch, "E1123", {"start": v(207.33, -299.76) * mm, "end": v(207.65, -300.74) * mm});
            skLineSegment(sketch, "E1124", {"start": v(207.65, -300.74) * mm, "end": v(208.74, -302.47) * mm});
            skLineSegment(sketch, "E1125", {"start": v(208.74, -302.47) * mm, "end": v(209.39, -303.23) * mm});
            skLineSegment(sketch, "E1126", {"start": v(209.39, -303.23) * mm, "end": v(210.14, -303.98) * mm});
            skLineSegment(sketch, "E1127", {"start": v(210.14, -303.98) * mm, "end": v(211, -304.53) * mm});
            skLineSegment(sketch, "E1128", {"start": v(211, -304.53) * mm, "end": v(211.87, -304.96) * mm});
            skLineSegment(sketch, "E1129", {"start": v(211.87, -304.96) * mm, "end": v(212.85, -305.28) * mm});
            skLineSegment(sketch, "E1130", {"start": v(212.85, -305.28) * mm, "end": v(213.93, -305.5) * mm});
            skLineSegment(sketch, "E1131", {"start": v(213.93, -305.5) * mm, "end": v(215.88, -305.5) * mm});
            skLineSegment(sketch, "E1132", {"start": v(215.88, -305.5) * mm, "end": v(216.96, -305.28) * mm});
            skLineSegment(sketch, "E1133", {"start": v(216.96, -305.28) * mm, "end": v(217.94, -304.96) * mm});
            skLineSegment(sketch, "E1134", {"start": v(217.94, -304.96) * mm, "end": v(218.8, -304.53) * mm});
            skLineSegment(sketch, "E1135", {"start": v(218.8, -304.53) * mm, "end": v(219.67, -303.98) * mm});
            skLineSegment(sketch, "E1136", {"start": v(219.67, -303.98) * mm, "end": v(220.43, -303.23) * mm});
            skLineSegment(sketch, "E1137", {"start": v(220.43, -303.23) * mm, "end": v(221.08, -302.47) * mm});
            skLineSegment(sketch, "E1138", {"start": v(221.08, -302.47) * mm, "end": v(221.72, -301.6) * mm});
            skLineSegment(sketch, "E1139", {"start": v(221.72, -301.6) * mm, "end": v(222.16, -300.74) * mm});
            skLineSegment(sketch, "E1140", {"start": v(222.16, -300.74) * mm, "end": v(222.48, -299.76) * mm});
            skLineSegment(sketch, "E1141", {"start": v(222.48, -299.76) * mm, "end": v(222.7, -298.79) * mm});
            skLineSegment(sketch, "E1142", {"start": v(222.7, -298.79) * mm, "end": v(222.7, -297.7) * mm});
            skLineSegment(sketch, "E1143", {"start": v(222.7, -297.7) * mm, "end": v(222.7, -271.4) * mm});
            skLineSegment(sketch, "E1144", {"start": v(222.7, -271.4) * mm, "end": v(222.7, -270.32) * mm});
            skLineSegment(sketch, "E1145", {"start": v(222.7, -270.32) * mm, "end": v(222.48, -269.35) * mm});
            skLineSegment(sketch, "E1146", {"start": v(222.48, -269.35) * mm, "end": v(222.16, -268.37) * mm});
            skLineSegment(sketch, "E1147", {"start": v(222.16, -268.37) * mm, "end": v(221.72, -267.5) * mm});
            skLineSegment(sketch, "E1148", {"start": v(221.72, -267.5) * mm, "end": v(221.08, -266.64) * mm});
            skLineSegment(sketch, "E1149", {"start": v(221.08, -266.64) * mm, "end": v(220.43, -265.88) * mm});
            skLineSegment(sketch, "E1150", {"start": v(220.43, -265.88) * mm, "end": v(219.67, -265.13) * mm});
            skLineSegment(sketch, "E1151", {"start": v(219.67, -265.13) * mm, "end": v(218.8, -264.59) * mm});
            skLineSegment(sketch, "E1152", {"start": v(218.8, -264.59) * mm, "end": v(217.94, -264.15) * mm});
            skLineSegment(sketch, "E1153", {"start": v(217.94, -264.15) * mm, "end": v(216.96, -263.83) * mm});
            skLineSegment(sketch, "E1154", {"start": v(216.96, -263.83) * mm, "end": v(215.88, -263.61) * mm});
            skLineSegment(sketch, "E1155", {"start": v(215.88, -263.61) * mm, "end": v(213.93, -263.61) * mm});
            skLineSegment(sketch, "E1156", {"start": v(213.93, -263.61) * mm, "end": v(212.85, -263.83) * mm});
            skLineSegment(sketch, "E1157", {"start": v(212.85, -263.83) * mm, "end": v(211.87, -264.15) * mm});
            skLineSegment(sketch, "E1158", {"start": v(211.87, -264.15) * mm, "end": v(211, -264.59) * mm});
            skLineSegment(sketch, "E1159", {"start": v(211, -264.59) * mm, "end": v(210.14, -265.13) * mm});
            skLineSegment(sketch, "E1160", {"start": v(210.14, -265.13) * mm, "end": v(209.39, -265.88) * mm});
            skLineSegment(sketch, "E1161", {"start": v(209.39, -265.88) * mm, "end": v(208.74, -266.64) * mm});
            skLineSegment(sketch, "E1162", {"start": v(208.74, -266.64) * mm, "end": v(208.2, -267.5) * mm});
            skLineSegment(sketch, "E1163", {"start": v(208.2, -267.5) * mm, "end": v(207.65, -268.37) * mm});
            skLineSegment(sketch, "E1164", {"start": v(207.65, -268.37) * mm, "end": v(207.33, -269.35) * mm});
            skLineSegment(sketch, "E1165", {"start": v(207.33, -269.35) * mm, "end": v(207.22, -270.32) * mm});
            skLineSegment(sketch, "E1166", {"start": v(207.22, -270.32) * mm, "end": v(207.11, -271.4) * mm});
            skLineSegment(sketch, "E1167", {"start": v(-80.58, -263.61) * mm, "end": v(-87.4, -263.61) * mm});
            skLineSegment(sketch, "E1168", {"start": v(-87.4, -263.61) * mm, "end": v(-87.4, -305.5) * mm});
            skLineSegment(sketch, "E1169", {"start": v(-87.4, -305.5) * mm, "end": v(-82.31, -305.5) * mm});
            skLineSegment(sketch, "E1170", {"start": v(-82.31, -305.5) * mm, "end": v(-82.31, -277.25) * mm});
            skLineSegment(sketch, "E1171", {"start": v(-82.31, -277.25) * mm, "end": v(-81.77, -277.25) * mm});
            skLineSegment(sketch, "E1172", {"start": v(-81.77, -277.25) * mm, "end": v(-77.55, -305.5) * mm});
            skLineSegment(sketch, "E1173", {"start": v(-77.55, -305.5) * mm, "end": v(-75.17, -305.5) * mm});
            skLineSegment(sketch, "E1174", {"start": v(-75.17, -305.5) * mm, "end": v(-70.95, -277.25) * mm});
            skLineSegment(sketch, "E1175", {"start": v(-70.95, -277.25) * mm, "end": v(-70.52, -277.25) * mm});
            skLineSegment(sketch, "E1176", {"start": v(-70.52, -277.25) * mm, "end": v(-70.52, -305.5) * mm});
            skLineSegment(sketch, "E1177", {"start": v(-70.52, -305.5) * mm, "end": v(-65.32, -305.5) * mm});
            skLineSegment(sketch, "E1178", {"start": v(-65.32, -305.5) * mm, "end": v(-65.32, -263.61) * mm});
            skLineSegment(sketch, "E1179", {"start": v(-65.32, -263.61) * mm, "end": v(-72.14, -263.61) * mm});
            skLineSegment(sketch, "E1180", {"start": v(-72.14, -263.61) * mm, "end": v(-75.93, -284.83) * mm});
            skLineSegment(sketch, "E1181", {"start": v(-75.93, -284.83) * mm, "end": v(-76.8, -284.83) * mm});
            skLineSegment(sketch, "E1182", {"start": v(-76.8, -284.83) * mm, "end": v(-80.58, -263.61) * mm});
            skLineSegment(sketch, "E1183", {"start": v(-27.65, -263.61) * mm, "end": v(-33.17, -263.61) * mm});
            skLineSegment(sketch, "E1184", {"start": v(-33.17, -263.61) * mm, "end": v(-33.17, -305.5) * mm});
            skLineSegment(sketch, "E1185", {"start": v(-33.17, -305.5) * mm, "end": v(-27.65, -305.5) * mm});
            skLineSegment(sketch, "E1186", {"start": v(-27.65, -305.5) * mm, "end": v(-27.65, -281.9) * mm});
            skLineSegment(sketch, "E1187", {"start": v(-27.65, -281.9) * mm, "end": v(-27, -281.9) * mm});
            skLineSegment(sketch, "E1188", {"start": v(-27, -281.9) * mm, "end": v(-20.73, -305.5) * mm});
            skLineSegment(sketch, "E1189", {"start": v(-20.73, -305.5) * mm, "end": v(-15.53, -305.5) * mm});
            skLineSegment(sketch, "E1190", {"start": v(-15.53, -305.5) * mm, "end": v(-15.53, -263.61) * mm});
            skLineSegment(sketch, "E1191", {"start": v(-15.53, -263.61) * mm, "end": v(-20.73, -263.61) * mm});
            skLineSegment(sketch, "E1192", {"start": v(-20.73, -263.61) * mm, "end": v(-20.73, -287.75) * mm});
            skLineSegment(sketch, "E1193", {"start": v(-20.73, -287.75) * mm, "end": v(-21.38, -287.75) * mm});
            skLineSegment(sketch, "E1194", {"start": v(-21.38, -287.75) * mm, "end": v(-27.65, -263.61) * mm});
            skLineSegment(sketch, "E1195", {"start": v(-0.05, 391.55) * mm, "end": v(-13.58, 391.55) * mm});
            skLineSegment(sketch, "E1196", {"start": v(-13.58, 391.55) * mm, "end": v(-13.58, 298.68) * mm});
            skLineSegment(sketch, "E1197", {"start": v(-13.58, 298.68) * mm, "end": v(-0.05, 298.68) * mm});
            skLineSegment(sketch, "E1198", {"start": v(-0.05, 298.68) * mm, "end": v(-0.05, 333.2) * mm});
            skLineSegment(sketch, "E1199", {"start": v(-0.05, 333.2) * mm, "end": v(3.84, 341.54) * mm});
            skLineSegment(sketch, "E1200", {"start": v(3.84, 341.54) * mm, "end": v(14.01, 298.68) * mm});
            skLineSegment(sketch, "E1201", {"start": v(14.01, 298.68) * mm, "end": v(27.22, 298.68) * mm});
            skLineSegment(sketch, "E1202", {"start": v(27.22, 298.68) * mm, "end": v(12.61, 360.16) * mm});
            skLineSegment(sketch, "E1203", {"start": v(12.61, 360.16) * mm, "end": v(25.17, 391.55) * mm});
            skLineSegment(sketch, "E1204", {"start": v(25.17, 391.55) * mm, "end": v(12.5, 391.55) * mm});
            skLineSegment(sketch, "E1205", {"start": v(12.5, 391.55) * mm, "end": v(-0.05, 357.34) * mm});
            skLineSegment(sketch, "E1206", {"start": v(-0.05, 357.34) * mm, "end": v(-0.05, 391.55) * mm});
            skLineSegment(sketch, "E1207", {"start": v(103.53, 391.55) * mm, "end": v(90.1, 391.55) * mm});
            skLineSegment(sketch, "E1208", {"start": v(90.1, 391.55) * mm, "end": v(90.1, 298.68) * mm});
            skLineSegment(sketch, "E1209", {"start": v(90.1, 298.68) * mm, "end": v(103.53, 298.68) * mm});
            skLineSegment(sketch, "E1210", {"start": v(103.53, 298.68) * mm, "end": v(103.53, 333.2) * mm});
            skLineSegment(sketch, "E1211", {"start": v(103.53, 333.2) * mm, "end": v(107.53, 341.54) * mm});
            skLineSegment(sketch, "E1212", {"start": v(107.53, 341.54) * mm, "end": v(117.6, 298.68) * mm});
            skLineSegment(sketch, "E1213", {"start": v(117.6, 298.68) * mm, "end": v(130.8, 298.68) * mm});
            skLineSegment(sketch, "E1214", {"start": v(130.8, 298.68) * mm, "end": v(116.3, 360.16) * mm});
            skLineSegment(sketch, "E1215", {"start": v(116.3, 360.16) * mm, "end": v(128.75, 391.55) * mm});
            skLineSegment(sketch, "E1216", {"start": v(128.75, 391.55) * mm, "end": v(116.08, 391.55) * mm});
            skLineSegment(sketch, "E1217", {"start": v(116.08, 391.55) * mm, "end": v(103.53, 357.34) * mm});
            skLineSegment(sketch, "E1218", {"start": v(103.53, 357.34) * mm, "end": v(103.53, 391.55) * mm});
            skLineSegment(sketch, "E1219", {"start": v(56.88, 367.4) * mm, "end": v(62.18, 331.15) * mm});
            skLineSegment(sketch, "E1220", {"start": v(62.18, 331.15) * mm, "end": v(51.69, 331.15) * mm});
            skLineSegment(sketch, "E1221", {"start": v(51.69, 331.15) * mm, "end": v(56.88, 367.4) * mm});
            skLineSegment(sketch, "E1222", {"start": v(65.1, 391.55) * mm, "end": v(48.76, 391.55) * mm});
            skLineSegment(sketch, "E1223", {"start": v(48.76, 391.55) * mm, "end": v(35.23, 298.68) * mm});
            skLineSegment(sketch, "E1224", {"start": v(35.23, 298.68) * mm, "end": v(46.92, 298.68) * mm});
            skLineSegment(sketch, "E1225", {"start": v(46.92, 298.68) * mm, "end": v(49.63, 317.08) * mm});
            skLineSegment(sketch, "E1226", {"start": v(49.63, 317.08) * mm, "end": v(64.24, 317.08) * mm});
            skLineSegment(sketch, "E1227", {"start": v(64.24, 317.08) * mm, "end": v(66.95, 298.68) * mm});
            skLineSegment(sketch, "E1228", {"start": v(66.95, 298.68) * mm, "end": v(78.63, 298.68) * mm});
            skLineSegment(sketch, "E1229", {"start": v(78.63, 298.68) * mm, "end": v(65.1, 391.55) * mm});
            skLineSegment(sketch, "E1230", {"start": v(159.92, 367.4) * mm, "end": v(165.23, 331.15) * mm});
            skLineSegment(sketch, "E1231", {"start": v(165.23, 331.15) * mm, "end": v(154.62, 331.15) * mm});
            skLineSegment(sketch, "E1232", {"start": v(154.62, 331.15) * mm, "end": v(159.92, 367.4) * mm});
            skLineSegment(sketch, "E1233", {"start": v(168.04, 391.55) * mm, "end": v(151.8, 391.55) * mm});
            skLineSegment(sketch, "E1234", {"start": v(151.8, 391.55) * mm, "end": v(138.16, 298.68) * mm});
            skLineSegment(sketch, "E1235", {"start": v(138.16, 298.68) * mm, "end": v(149.86, 298.68) * mm});
            skLineSegment(sketch, "E1236", {"start": v(149.86, 298.68) * mm, "end": v(152.56, 317.08) * mm});
            skLineSegment(sketch, "E1237", {"start": v(152.56, 317.08) * mm, "end": v(167.28, 317.08) * mm});
            skLineSegment(sketch, "E1238", {"start": v(167.28, 317.08) * mm, "end": v(169.88, 298.68) * mm});
            skLineSegment(sketch, "E1239", {"start": v(169.88, 298.68) * mm, "end": v(181.57, 298.68) * mm});
            skLineSegment(sketch, "E1240", {"start": v(181.57, 298.68) * mm, "end": v(168.04, 391.55) * mm});
            skLineSegment(sketch, "E1241", {"start": v(-78.42, 391.55) * mm, "end": v(-62.07, 391.55) * mm});
            skLineSegment(sketch, "E1242", {"start": v(-70.19, 367.4) * mm, "end": v(-64.89, 331.15) * mm});
            skLineSegment(sketch, "E1243", {"start": v(-64.89, 331.15) * mm, "end": v(-75.5, 331.15) * mm});
            skLineSegment(sketch, "E1244", {"start": v(-75.5, 331.15) * mm, "end": v(-70.19, 367.4) * mm});
            skLineSegment(sketch, "E1245", {"start": v(-62.07, 391.55) * mm, "end": v(-78.42, 391.55) * mm});
            skLineSegment(sketch, "E1246", {"start": v(-78.42, 391.55) * mm, "end": v(-91.95, 298.68) * mm});
            skLineSegment(sketch, "E1247", {"start": v(-91.95, 298.68) * mm, "end": v(-80.26, 298.68) * mm});
            skLineSegment(sketch, "E1248", {"start": v(-80.26, 298.68) * mm, "end": v(-77.55, 317.08) * mm});
            skLineSegment(sketch, "E1249", {"start": v(-77.55, 317.08) * mm, "end": v(-62.83, 317.08) * mm});
            skLineSegment(sketch, "E1250", {"start": v(-62.83, 317.08) * mm, "end": v(-60.23, 298.68) * mm});
            skLineSegment(sketch, "E1251", {"start": v(-60.23, 298.68) * mm, "end": v(-48.54, 298.68) * mm});
            skLineSegment(sketch, "E1252", {"start": v(-48.54, 298.68) * mm, "end": v(-62.07, 391.55) * mm});
            skLineSegment(sketch, "E1253", {"start": v(-171.5, 391.55) * mm, "end": v(-155.16, 391.55) * mm});
            skLineSegment(sketch, "E1254", {"start": v(-163.27, 367.4) * mm, "end": v(-158.08, 331.15) * mm});
            skLineSegment(sketch, "E1255", {"start": v(-158.08, 331.15) * mm, "end": v(-168.58, 331.15) * mm});
            skLineSegment(sketch, "E1256", {"start": v(-168.58, 331.15) * mm, "end": v(-163.27, 367.4) * mm});
            skLineSegment(sketch, "E1257", {"start": v(-155.16, 391.55) * mm, "end": v(-171.5, 391.55) * mm});
            skLineSegment(sketch, "E1258", {"start": v(-171.5, 391.55) * mm, "end": v(-185.03, 298.68) * mm});
            skLineSegment(sketch, "E1259", {"start": v(-185.03, 298.68) * mm, "end": v(-173.34, 298.68) * mm});
            skLineSegment(sketch, "E1260", {"start": v(-173.34, 298.68) * mm, "end": v(-170.64, 317.08) * mm});
            skLineSegment(sketch, "E1261", {"start": v(-170.64, 317.08) * mm, "end": v(-156.02, 317.08) * mm});
            skLineSegment(sketch, "E1262", {"start": v(-156.02, 317.08) * mm, "end": v(-153.32, 298.68) * mm});
            skLineSegment(sketch, "E1263", {"start": v(-153.32, 298.68) * mm, "end": v(-141.63, 298.68) * mm});
            skLineSegment(sketch, "E1264", {"start": v(-141.63, 298.68) * mm, "end": v(-155.16, 391.55) * mm});
            skLineSegment(sketch, "E1265", {"start": v(198.78, 391.55) * mm, "end": v(187.2, 391.55) * mm});
            skLineSegment(sketch, "E1266", {"start": v(187.2, 391.55) * mm, "end": v(199.53, 298.68) * mm});
            skLineSegment(sketch, "E1267", {"start": v(199.53, 298.68) * mm, "end": v(209.39, 298.68) * mm});
            skLineSegment(sketch, "E1268", {"start": v(209.39, 298.68) * mm, "end": v(216.85, 348.8) * mm});
            skLineSegment(sketch, "E1269", {"start": v(216.85, 348.8) * mm, "end": v(217.4, 348.8) * mm});
            skLineSegment(sketch, "E1270", {"start": v(217.4, 348.8) * mm, "end": v(224.86, 298.68) * mm});
            skLineSegment(sketch, "E1271", {"start": v(224.86, 298.68) * mm, "end": v(234.71, 298.68) * mm});
            skLineSegment(sketch, "E1272", {"start": v(234.71, 298.68) * mm, "end": v(246.94, 391.55) * mm});
            skLineSegment(sketch, "E1273", {"start": v(246.94, 391.55) * mm, "end": v(235.47, 391.55) * mm});
            skLineSegment(sketch, "E1274", {"start": v(235.47, 391.55) * mm, "end": v(229.3, 339.27) * mm});
            skLineSegment(sketch, "E1275", {"start": v(229.3, 339.27) * mm, "end": v(228.44, 339.27) * mm});
            skLineSegment(sketch, "E1276", {"start": v(228.44, 339.27) * mm, "end": v(221.94, 391.55) * mm});
            skLineSegment(sketch, "E1277", {"start": v(221.94, 391.55) * mm, "end": v(212.3, 391.55) * mm});
            skLineSegment(sketch, "E1278", {"start": v(212.3, 391.55) * mm, "end": v(205.81, 339.27) * mm});
            skLineSegment(sketch, "E1279", {"start": v(205.81, 339.27) * mm, "end": v(204.95, 339.27) * mm});
            skLineSegment(sketch, "E1280", {"start": v(204.95, 339.27) * mm, "end": v(198.78, 391.55) * mm});
            skLineSegment(sketch, "E1281", {"start": v(-96.82, 391.55) * mm, "end": v(-109.26, 391.55) * mm});
            skLineSegment(sketch, "E1282", {"start": v(-109.26, 391.55) * mm, "end": v(-116.4, 361.02) * mm});
            skLineSegment(sketch, "E1283", {"start": v(-116.4, 361.02) * mm, "end": v(-117.38, 361.02) * mm});
            skLineSegment(sketch, "E1284", {"start": v(-117.38, 361.02) * mm, "end": v(-124.85, 391.55) * mm});
            skLineSegment(sketch, "E1285", {"start": v(-124.85, 391.55) * mm, "end": v(-137.62, 391.55) * mm});
            skLineSegment(sketch, "E1286", {"start": v(-137.62, 391.55) * mm, "end": v(-124.1, 341) * mm});
            skLineSegment(sketch, "E1287", {"start": v(-124.1, 341) * mm, "end": v(-124.1, 298.68) * mm});
            skLineSegment(sketch, "E1288", {"start": v(-124.1, 298.68) * mm, "end": v(-110.24, 298.68) * mm});
            skLineSegment(sketch, "E1289", {"start": v(-110.24, 298.68) * mm, "end": v(-110.24, 341) * mm});
            skLineSegment(sketch, "E1290", {"start": v(-110.24, 341) * mm, "end": v(-96.82, 391.55) * mm});
            skLineSegment(sketch, "E1291", {"start": v(-231.36, 391.55) * mm, "end": v(-246.4, 391.55) * mm});
            skLineSegment(sketch, "E1292", {"start": v(-246.4, 391.55) * mm, "end": v(-246.4, 298.68) * mm});
            skLineSegment(sketch, "E1293", {"start": v(-246.4, 298.68) * mm, "end": v(-235.04, 298.68) * mm});
            skLineSegment(sketch, "E1294", {"start": v(-235.04, 298.68) * mm, "end": v(-235.04, 361.35) * mm});
            skLineSegment(sketch, "E1295", {"start": v(-235.04, 361.35) * mm, "end": v(-234.06, 361.35) * mm});
            skLineSegment(sketch, "E1296", {"start": v(-234.06, 361.35) * mm, "end": v(-224.75, 298.68) * mm});
            skLineSegment(sketch, "E1297", {"start": v(-224.75, 298.68) * mm, "end": v(-219.23, 298.68) * mm});
            skLineSegment(sketch, "E1298", {"start": v(-219.23, 298.68) * mm, "end": v(-209.93, 361.35) * mm});
            skLineSegment(sketch, "E1299", {"start": v(-209.93, 361.35) * mm, "end": v(-208.95, 361.35) * mm});
            skLineSegment(sketch, "E1300", {"start": v(-208.95, 361.35) * mm, "end": v(-208.95, 298.68) * mm});
            skLineSegment(sketch, "E1301", {"start": v(-208.95, 298.68) * mm, "end": v(-197.59, 298.68) * mm});
            skLineSegment(sketch, "E1302", {"start": v(-197.59, 298.68) * mm, "end": v(-197.59, 391.55) * mm});
            skLineSegment(sketch, "E1303", {"start": v(-197.59, 391.55) * mm, "end": v(-212.63, 391.55) * mm});
            skLineSegment(sketch, "E1304", {"start": v(-212.63, 391.55) * mm, "end": v(-221.07, 344.68) * mm});
            skLineSegment(sketch, "E1305", {"start": v(-221.07, 344.68) * mm, "end": v(-222.91, 344.68) * mm});
            skLineSegment(sketch, "E1306", {"start": v(-222.91, 344.68) * mm, "end": v(-231.36, 391.55) * mm});
            skLineSegment(sketch, "E1307", {"start": v(-202.13, 262.3) * mm, "end": v(-189.8, 262.3) * mm});
            skLineSegment(sketch, "E1308", {"start": v(-195.96, 244.02) * mm, "end": v(-192.07, 216.74) * mm});
            skLineSegment(sketch, "E1309", {"start": v(-192.07, 216.74) * mm, "end": v(-199.97, 216.74) * mm});
            skLineSegment(sketch, "E1310", {"start": v(-199.97, 216.74) * mm, "end": v(-195.96, 244.02) * mm});
            skLineSegment(sketch, "E1311", {"start": v(-189.8, 262.3) * mm, "end": v(-202.13, 262.3) * mm});
            skLineSegment(sketch, "E1312", {"start": v(-202.13, 262.3) * mm, "end": v(-212.41, 192.18) * mm});
            skLineSegment(sketch, "E1313", {"start": v(-212.41, 192.18) * mm, "end": v(-203.54, 192.18) * mm});
            skLineSegment(sketch, "E1314", {"start": v(-203.54, 192.18) * mm, "end": v(-201.6, 206.03) * mm});
            skLineSegment(sketch, "E1315", {"start": v(-201.6, 206.03) * mm, "end": v(-190.44, 206.03) * mm});
            skLineSegment(sketch, "E1316", {"start": v(-190.44, 206.03) * mm, "end": v(-188.39, 192.18) * mm});
            skLineSegment(sketch, "E1317", {"start": v(-188.39, 192.18) * mm, "end": v(-179.62, 192.18) * mm});
            skLineSegment(sketch, "E1318", {"start": v(-179.62, 192.18) * mm, "end": v(-189.8, 262.3) * mm});
            skLineSegment(sketch, "E1319", {"start": v(-124.96, 262.3) * mm, "end": v(-112.62, 262.3) * mm});
            skLineSegment(sketch, "E1320", {"start": v(-118.79, 244.02) * mm, "end": v(-114.78, 216.74) * mm});
            skLineSegment(sketch, "E1321", {"start": v(-114.78, 216.74) * mm, "end": v(-122.8, 216.74) * mm});
            skLineSegment(sketch, "E1322", {"start": v(-122.8, 216.74) * mm, "end": v(-118.79, 244.02) * mm});
            skLineSegment(sketch, "E1323", {"start": v(-112.62, 262.3) * mm, "end": v(-124.96, 262.3) * mm});
            skLineSegment(sketch, "E1324", {"start": v(-124.96, 262.3) * mm, "end": v(-135.13, 192.18) * mm});
            skLineSegment(sketch, "E1325", {"start": v(-135.13, 192.18) * mm, "end": v(-126.37, 192.18) * mm});
            skLineSegment(sketch, "E1326", {"start": v(-126.37, 192.18) * mm, "end": v(-124.3, 206.03) * mm});
            skLineSegment(sketch, "E1327", {"start": v(-124.3, 206.03) * mm, "end": v(-113.27, 206.03) * mm});
            skLineSegment(sketch, "E1328", {"start": v(-113.27, 206.03) * mm, "end": v(-111.21, 192.18) * mm});
            skLineSegment(sketch, "E1329", {"start": v(-111.21, 192.18) * mm, "end": v(-102.34, 192.18) * mm});
            skLineSegment(sketch, "E1330", {"start": v(-102.34, 192.18) * mm, "end": v(-112.62, 262.3) * mm});
            skLineSegment(sketch, "E1331", {"start": v(87.5, 262.3) * mm, "end": v(99.85, 262.3) * mm});
            skLineSegment(sketch, "E1332", {"start": v(93.68, 244.02) * mm, "end": v(97.68, 216.74) * mm});
            skLineSegment(sketch, "E1333", {"start": v(97.68, 216.74) * mm, "end": v(89.68, 216.74) * mm});
            skLineSegment(sketch, "E1334", {"start": v(89.68, 216.74) * mm, "end": v(93.68, 244.02) * mm});
            skLineSegment(sketch, "E1335", {"start": v(99.85, 262.3) * mm, "end": v(87.5, 262.3) * mm});
            skLineSegment(sketch, "E1336", {"start": v(87.5, 262.3) * mm, "end": v(77.33, 192.18) * mm});
            skLineSegment(sketch, "E1337", {"start": v(77.33, 192.18) * mm, "end": v(86.1, 192.18) * mm});
            skLineSegment(sketch, "E1338", {"start": v(86.1, 192.18) * mm, "end": v(88.16, 206.03) * mm});
            skLineSegment(sketch, "E1339", {"start": v(88.16, 206.03) * mm, "end": v(99.2, 206.03) * mm});
            skLineSegment(sketch, "E1340", {"start": v(99.2, 206.03) * mm, "end": v(101.26, 192.18) * mm});
            skLineSegment(sketch, "E1341", {"start": v(101.26, 192.18) * mm, "end": v(110.02, 192.18) * mm});
            skLineSegment(sketch, "E1342", {"start": v(110.02, 192.18) * mm, "end": v(99.85, 262.3) * mm});
            skLineSegment(sketch, "E1343", {"start": v(161.54, 262.3) * mm, "end": v(171.4, 262.3) * mm});
            skLineSegment(sketch, "E1344", {"start": v(171.4, 262.3) * mm, "end": v(171.4, 192.18) * mm});
            skLineSegment(sketch, "E1345", {"start": v(171.4, 192.18) * mm, "end": v(161.54, 192.18) * mm});
            skLineSegment(sketch, "E1346", {"start": v(161.54, 192.18) * mm, "end": v(161.54, 262.3) * mm});
            skLineSegment(sketch, "E1347", {"start": v(237.74, 249.97) * mm, "end": v(237.74, 204.51) * mm});
            skLineSegment(sketch, "E1348", {"start": v(230.5, 204.51) * mm, "end": v(230.5, 203.65) * mm});
            skLineSegment(sketch, "E1349", {"start": v(230.5, 203.65) * mm, "end": v(230.81, 202.89) * mm});
            skLineSegment(sketch, "E1350", {"start": v(230.81, 202.89) * mm, "end": v(231.25, 202.24) * mm});
            skLineSegment(sketch, "E1351", {"start": v(231.25, 202.24) * mm, "end": v(231.8, 201.6) * mm});
            skLineSegment(sketch, "E1352", {"start": v(231.8, 201.6) * mm, "end": v(232.44, 201.16) * mm});
            skLineSegment(sketch, "E1353", {"start": v(232.44, 201.16) * mm, "end": v(233.3, 200.94) * mm});
            skLineSegment(sketch, "E1354", {"start": v(233.3, 200.94) * mm, "end": v(234.07, 200.83) * mm});
            skLineSegment(sketch, "E1355", {"start": v(234.07, 200.83) * mm, "end": v(234.82, 200.94) * mm});
            skLineSegment(sketch, "E1356", {"start": v(234.82, 200.94) * mm, "end": v(235.69, 201.16) * mm});
            skLineSegment(sketch, "E1357", {"start": v(235.69, 201.16) * mm, "end": v(236.34, 201.6) * mm});
            skLineSegment(sketch, "E1358", {"start": v(236.34, 201.6) * mm, "end": v(236.88, 202.24) * mm});
            skLineSegment(sketch, "E1359", {"start": v(236.88, 202.24) * mm, "end": v(237.3, 202.89) * mm});
            skLineSegment(sketch, "E1360", {"start": v(237.3, 202.89) * mm, "end": v(237.63, 203.65) * mm});
            skLineSegment(sketch, "E1361", {"start": v(237.63, 203.65) * mm, "end": v(237.74, 204.51) * mm});
            skLineSegment(sketch, "E1362", {"start": v(230.5, 204.51) * mm, "end": v(230.5, 249.97) * mm});
            skLineSegment(sketch, "E1363", {"start": v(237.74, 249.97) * mm, "end": v(237.63, 250.84) * mm});
            skLineSegment(sketch, "E1364", {"start": v(237.63, 250.84) * mm, "end": v(237.3, 251.6) * mm});
            skLineSegment(sketch, "E1365", {"start": v(237.3, 251.6) * mm, "end": v(236.88, 252.25) * mm});
            skLineSegment(sketch, "E1366", {"start": v(236.88, 252.25) * mm, "end": v(236.34, 252.78) * mm});
            skLineSegment(sketch, "E1367", {"start": v(236.34, 252.78) * mm, "end": v(235.69, 253.22) * mm});
            skLineSegment(sketch, "E1368", {"start": v(235.69, 253.22) * mm, "end": v(234.82, 253.54) * mm});
            skLineSegment(sketch, "E1369", {"start": v(234.82, 253.54) * mm, "end": v(234.07, 253.65) * mm});
            skLineSegment(sketch, "E1370", {"start": v(234.07, 253.65) * mm, "end": v(233.3, 253.54) * mm});
            skLineSegment(sketch, "E1371", {"start": v(233.3, 253.54) * mm, "end": v(232.44, 253.22) * mm});
            skLineSegment(sketch, "E1372", {"start": v(232.44, 253.22) * mm, "end": v(231.8, 252.78) * mm});
            skLineSegment(sketch, "E1373", {"start": v(231.8, 252.78) * mm, "end": v(231.25, 252.25) * mm});
            skLineSegment(sketch, "E1374", {"start": v(231.25, 252.25) * mm, "end": v(230.81, 251.6) * mm});
            skLineSegment(sketch, "E1375", {"start": v(230.81, 251.6) * mm, "end": v(230.5, 250.84) * mm});
            skLineSegment(sketch, "E1376", {"start": v(230.5, 250.84) * mm, "end": v(230.5, 249.97) * mm});
            skLineSegment(sketch, "E1377", {"start": v(221.08, 249.22) * mm, "end": v(221.08, 205.16) * mm});
            skLineSegment(sketch, "E1378", {"start": v(221.08, 205.16) * mm, "end": v(221.08, 203.65) * mm});
            skLineSegment(sketch, "E1379", {"start": v(221.08, 203.65) * mm, "end": v(221.4, 202.13) * mm});
            skLineSegment(sketch, "E1380", {"start": v(221.4, 202.13) * mm, "end": v(221.83, 200.62) * mm});
            skLineSegment(sketch, "E1381", {"start": v(221.83, 200.62) * mm, "end": v(222.48, 199.1) * mm});
            skLineSegment(sketch, "E1382", {"start": v(222.48, 199.1) * mm, "end": v(223.35, 197.8) * mm});
            skLineSegment(sketch, "E1383", {"start": v(223.35, 197.8) * mm, "end": v(224.32, 196.61) * mm});
            skLineSegment(sketch, "E1384", {"start": v(224.32, 196.61) * mm, "end": v(225.4, 195.42) * mm});
            skLineSegment(sketch, "E1385", {"start": v(225.4, 195.42) * mm, "end": v(226.7, 194.45) * mm});
            skLineSegment(sketch, "E1386", {"start": v(226.7, 194.45) * mm, "end": v(228, 193.69) * mm});
            skLineSegment(sketch, "E1387", {"start": v(228, 193.69) * mm, "end": v(229.4, 193.04) * mm});
            skLineSegment(sketch, "E1388", {"start": v(229.4, 193.04) * mm, "end": v(230.92, 192.5) * mm});
            skLineSegment(sketch, "E1389", {"start": v(230.92, 192.5) * mm, "end": v(232.55, 192.28) * mm});
            skLineSegment(sketch, "E1390", {"start": v(232.55, 192.28) * mm, "end": v(234.07, 192.18) * mm});
            skLineSegment(sketch, "E1391", {"start": v(234.07, 192.18) * mm, "end": v(235.69, 192.28) * mm});
            skLineSegment(sketch, "E1392", {"start": v(235.69, 192.28) * mm, "end": v(237.2, 192.5) * mm});
            skLineSegment(sketch, "E1393", {"start": v(237.2, 192.5) * mm, "end": v(238.72, 193.04) * mm});
            skLineSegment(sketch, "E1394", {"start": v(238.72, 193.04) * mm, "end": v(240.13, 193.69) * mm});
            skLineSegment(sketch, "E1395", {"start": v(240.13, 193.69) * mm, "end": v(241.42, 194.45) * mm});
            skLineSegment(sketch, "E1396", {"start": v(241.42, 194.45) * mm, "end": v(242.72, 195.42) * mm});
            skLineSegment(sketch, "E1397", {"start": v(242.72, 195.42) * mm, "end": v(243.8, 196.61) * mm});
            skLineSegment(sketch, "E1398", {"start": v(243.8, 196.61) * mm, "end": v(244.78, 197.8) * mm});
            skLineSegment(sketch, "E1399", {"start": v(244.78, 197.8) * mm, "end": v(245.64, 199.1) * mm});
            skLineSegment(sketch, "E1400", {"start": v(245.64, 199.1) * mm, "end": v(246.3, 200.62) * mm});
            skLineSegment(sketch, "E1401", {"start": v(246.3, 200.62) * mm, "end": v(246.72, 202.13) * mm});
            skLineSegment(sketch, "E1402", {"start": v(246.72, 202.13) * mm, "end": v(247.05, 203.65) * mm});
            skLineSegment(sketch, "E1403", {"start": v(247.05, 203.65) * mm, "end": v(247.16, 205.16) * mm});
            skLineSegment(sketch, "E1404", {"start": v(247.16, 205.16) * mm, "end": v(247.16, 249.22) * mm});
            skLineSegment(sketch, "E1405", {"start": v(247.16, 249.22) * mm, "end": v(247.05, 250.84) * mm});
            skLineSegment(sketch, "E1406", {"start": v(247.05, 250.84) * mm, "end": v(246.72, 252.36) * mm});
            skLineSegment(sketch, "E1407", {"start": v(246.72, 252.36) * mm, "end": v(246.3, 253.87) * mm});
            skLineSegment(sketch, "E1408", {"start": v(246.3, 253.87) * mm, "end": v(245.64, 255.28) * mm});
            skLineSegment(sketch, "E1409", {"start": v(245.64, 255.28) * mm, "end": v(244.78, 256.68) * mm});
            skLineSegment(sketch, "E1410", {"start": v(244.78, 256.68) * mm, "end": v(243.8, 257.87) * mm});
            skLineSegment(sketch, "E1411", {"start": v(243.8, 257.87) * mm, "end": v(242.72, 258.96) * mm});
            skLineSegment(sketch, "E1412", {"start": v(242.72, 258.96) * mm, "end": v(241.42, 259.93) * mm});
            skLineSegment(sketch, "E1413", {"start": v(241.42, 259.93) * mm, "end": v(240.13, 260.8) * mm});
            skLineSegment(sketch, "E1414", {"start": v(240.13, 260.8) * mm, "end": v(238.72, 261.45) * mm});
            skLineSegment(sketch, "E1415", {"start": v(238.72, 261.45) * mm, "end": v(237.2, 261.88) * mm});
            skLineSegment(sketch, "E1416", {"start": v(237.2, 261.88) * mm, "end": v(235.69, 262.2) * mm});
            skLineSegment(sketch, "E1417", {"start": v(235.69, 262.2) * mm, "end": v(234.07, 262.3) * mm});
            skLineSegment(sketch, "E1418", {"start": v(234.07, 262.3) * mm, "end": v(232.55, 262.2) * mm});
            skLineSegment(sketch, "E1419", {"start": v(232.55, 262.2) * mm, "end": v(230.92, 261.88) * mm});
            skLineSegment(sketch, "E1420", {"start": v(230.92, 261.88) * mm, "end": v(229.4, 261.45) * mm});
            skLineSegment(sketch, "E1421", {"start": v(229.4, 261.45) * mm, "end": v(228, 260.8) * mm});
            skLineSegment(sketch, "E1422", {"start": v(228, 260.8) * mm, "end": v(226.7, 259.93) * mm});
            skLineSegment(sketch, "E1423", {"start": v(226.7, 259.93) * mm, "end": v(225.4, 258.96) * mm});
            skLineSegment(sketch, "E1424", {"start": v(225.4, 258.96) * mm, "end": v(224.32, 257.87) * mm});
            skLineSegment(sketch, "E1425", {"start": v(224.32, 257.87) * mm, "end": v(223.35, 256.68) * mm});
            skLineSegment(sketch, "E1426", {"start": v(223.35, 256.68) * mm, "end": v(222.48, 255.28) * mm});
            skLineSegment(sketch, "E1427", {"start": v(222.48, 255.28) * mm, "end": v(221.83, 253.87) * mm});
            skLineSegment(sketch, "E1428", {"start": v(221.83, 253.87) * mm, "end": v(221.4, 252.36) * mm});
            skLineSegment(sketch, "E1429", {"start": v(221.4, 252.36) * mm, "end": v(221.08, 250.84) * mm});
            skLineSegment(sketch, "E1430", {"start": v(221.08, 250.84) * mm, "end": v(221.08, 249.22) * mm});
            skLineSegment(sketch, "E1431", {"start": v(183.84, 205.16) * mm, "end": v(183.95, 203.65) * mm});
            skLineSegment(sketch, "E1432", {"start": v(183.95, 203.65) * mm, "end": v(184.17, 202.13) * mm});
            skLineSegment(sketch, "E1433", {"start": v(184.17, 202.13) * mm, "end": v(184.7, 200.62) * mm});
            skLineSegment(sketch, "E1434", {"start": v(184.7, 200.62) * mm, "end": v(185.36, 199.1) * mm});
            skLineSegment(sketch, "E1435", {"start": v(185.36, 199.1) * mm, "end": v(186.11, 197.8) * mm});
            skLineSegment(sketch, "E1436", {"start": v(186.11, 197.8) * mm, "end": v(187.09, 196.61) * mm});
            skLineSegment(sketch, "E1437", {"start": v(187.09, 196.61) * mm, "end": v(188.17, 195.42) * mm});
            skLineSegment(sketch, "E1438", {"start": v(188.17, 195.42) * mm, "end": v(189.47, 194.45) * mm});
            skLineSegment(sketch, "E1439", {"start": v(189.47, 194.45) * mm, "end": v(190.77, 193.69) * mm});
            skLineSegment(sketch, "E1440", {"start": v(190.77, 193.69) * mm, "end": v(192.18, 193.04) * mm});
            skLineSegment(sketch, "E1441", {"start": v(192.18, 193.04) * mm, "end": v(193.7, 192.5) * mm});
            skLineSegment(sketch, "E1442", {"start": v(193.7, 192.5) * mm, "end": v(195.31, 192.28) * mm});
            skLineSegment(sketch, "E1443", {"start": v(195.31, 192.28) * mm, "end": v(196.83, 192.18) * mm});
            skLineSegment(sketch, "E1444", {"start": v(196.83, 192.18) * mm, "end": v(198.45, 192.28) * mm});
            skLineSegment(sketch, "E1445", {"start": v(198.45, 192.28) * mm, "end": v(199.97, 192.5) * mm});
            skLineSegment(sketch, "E1446", {"start": v(199.97, 192.5) * mm, "end": v(201.48, 193.04) * mm});
            skLineSegment(sketch, "E1447", {"start": v(201.48, 193.04) * mm, "end": v(202.9, 193.69) * mm});
            skLineSegment(sketch, "E1448", {"start": v(202.9, 193.69) * mm, "end": v(204.3, 194.45) * mm});
            skLineSegment(sketch, "E1449", {"start": v(204.3, 194.45) * mm, "end": v(205.5, 195.42) * mm});
            skLineSegment(sketch, "E1450", {"start": v(205.5, 195.42) * mm, "end": v(206.57, 196.61) * mm});
            skLineSegment(sketch, "E1451", {"start": v(206.57, 196.61) * mm, "end": v(207.54, 197.8) * mm});
            skLineSegment(sketch, "E1452", {"start": v(207.54, 197.8) * mm, "end": v(208.41, 199.1) * mm});
            skLineSegment(sketch, "E1453", {"start": v(208.41, 199.1) * mm, "end": v(209.06, 200.62) * mm});
            skLineSegment(sketch, "E1454", {"start": v(209.06, 200.62) * mm, "end": v(209.5, 202.13) * mm});
            skLineSegment(sketch, "E1455", {"start": v(209.5, 202.13) * mm, "end": v(209.82, 203.65) * mm});
            skLineSegment(sketch, "E1456", {"start": v(209.82, 203.65) * mm, "end": v(209.93, 205.16) * mm});
            skLineSegment(sketch, "E1457", {"start": v(209.93, 205.16) * mm, "end": v(209.93, 216.2) * mm});
            skLineSegment(sketch, "E1458", {"start": v(209.93, 216.2) * mm, "end": v(200.51, 216.2) * mm});
            skLineSegment(sketch, "E1459", {"start": v(200.51, 216.2) * mm, "end": v(200.51, 204.51) * mm});
            skLineSegment(sketch, "E1460", {"start": v(193.26, 204.51) * mm, "end": v(193.37, 203.65) * mm});
            skLineSegment(sketch, "E1461", {"start": v(193.37, 203.65) * mm, "end": v(193.58, 202.89) * mm});
            skLineSegment(sketch, "E1462", {"start": v(193.58, 202.89) * mm, "end": v(194.02, 202.24) * mm});
            skLineSegment(sketch, "E1463", {"start": v(194.02, 202.24) * mm, "end": v(194.56, 201.6) * mm});
            skLineSegment(sketch, "E1464", {"start": v(194.56, 201.6) * mm, "end": v(195.31, 201.16) * mm});
            skLineSegment(sketch, "E1465", {"start": v(195.31, 201.16) * mm, "end": v(196.07, 200.94) * mm});
            skLineSegment(sketch, "E1466", {"start": v(196.07, 200.94) * mm, "end": v(196.83, 200.83) * mm});
            skLineSegment(sketch, "E1467", {"start": v(196.83, 200.83) * mm, "end": v(197.7, 200.94) * mm});
            skLineSegment(sketch, "E1468", {"start": v(197.7, 200.94) * mm, "end": v(198.45, 201.16) * mm});
            skLineSegment(sketch, "E1469", {"start": v(198.45, 201.16) * mm, "end": v(199.1, 201.6) * mm});
            skLineSegment(sketch, "E1470", {"start": v(199.1, 201.6) * mm, "end": v(199.64, 202.24) * mm});
            skLineSegment(sketch, "E1471", {"start": v(199.64, 202.24) * mm, "end": v(200.08, 202.89) * mm});
            skLineSegment(sketch, "E1472", {"start": v(200.08, 202.89) * mm, "end": v(200.4, 203.65) * mm});
            skLineSegment(sketch, "E1473", {"start": v(200.4, 203.65) * mm, "end": v(200.51, 204.51) * mm});
            skLineSegment(sketch, "E1474", {"start": v(193.26, 204.51) * mm, "end": v(193.26, 249.97) * mm});
            skLineSegment(sketch, "E1475", {"start": v(200.51, 249.97) * mm, "end": v(200.4, 250.84) * mm});
            skLineSegment(sketch, "E1476", {"start": v(200.4, 250.84) * mm, "end": v(200.08, 251.6) * mm});
            skLineSegment(sketch, "E1477", {"start": v(200.08, 251.6) * mm, "end": v(199.64, 252.25) * mm});
            skLineSegment(sketch, "E1478", {"start": v(199.64, 252.25) * mm, "end": v(199.1, 252.78) * mm});
            skLineSegment(sketch, "E1479", {"start": v(199.1, 252.78) * mm, "end": v(198.45, 253.22) * mm});
            skLineSegment(sketch, "E1480", {"start": v(198.45, 253.22) * mm, "end": v(197.7, 253.54) * mm});
            skLineSegment(sketch, "E1481", {"start": v(197.7, 253.54) * mm, "end": v(196.83, 253.65) * mm});
            skLineSegment(sketch, "E1482", {"start": v(196.83, 253.65) * mm, "end": v(196.07, 253.54) * mm});
            skLineSegment(sketch, "E1483", {"start": v(196.07, 253.54) * mm, "end": v(195.31, 253.22) * mm});
            skLineSegment(sketch, "E1484", {"start": v(195.31, 253.22) * mm, "end": v(194.56, 252.78) * mm});
            skLineSegment(sketch, "E1485", {"start": v(194.56, 252.78) * mm, "end": v(194.02, 252.25) * mm});
            skLineSegment(sketch, "E1486", {"start": v(194.02, 252.25) * mm, "end": v(193.58, 251.6) * mm});
            skLineSegment(sketch, "E1487", {"start": v(193.58, 251.6) * mm, "end": v(193.37, 250.84) * mm});
            skLineSegment(sketch, "E1488", {"start": v(193.37, 250.84) * mm, "end": v(193.26, 249.97) * mm});
            skLineSegment(sketch, "E1489", {"start": v(200.51, 249.97) * mm, "end": v(200.51, 238.28) * mm});
            skLineSegment(sketch, "E1490", {"start": v(200.51, 238.28) * mm, "end": v(209.93, 238.28) * mm});
            skLineSegment(sketch, "E1491", {"start": v(209.93, 238.28) * mm, "end": v(209.93, 249.22) * mm});
            skLineSegment(sketch, "E1492", {"start": v(209.93, 249.22) * mm, "end": v(209.82, 250.84) * mm});
            skLineSegment(sketch, "E1493", {"start": v(209.82, 250.84) * mm, "end": v(209.5, 252.36) * mm});
            skLineSegment(sketch, "E1494", {"start": v(209.5, 252.36) * mm, "end": v(209.06, 253.87) * mm});
            skLineSegment(sketch, "E1495", {"start": v(209.06, 253.87) * mm, "end": v(208.41, 255.28) * mm});
            skLineSegment(sketch, "E1496", {"start": v(208.41, 255.28) * mm, "end": v(207.54, 256.68) * mm});
            skLineSegment(sketch, "E1497", {"start": v(207.54, 256.68) * mm, "end": v(206.57, 257.87) * mm});
            skLineSegment(sketch, "E1498", {"start": v(206.57, 257.87) * mm, "end": v(205.5, 258.96) * mm});
            skLineSegment(sketch, "E1499", {"start": v(205.5, 258.96) * mm, "end": v(204.3, 259.93) * mm});
            skLineSegment(sketch, "E1500", {"start": v(204.3, 259.93) * mm, "end": v(202.9, 260.8) * mm});
            skLineSegment(sketch, "E1501", {"start": v(202.9, 260.8) * mm, "end": v(201.48, 261.45) * mm});
            skLineSegment(sketch, "E1502", {"start": v(201.48, 261.45) * mm, "end": v(199.97, 261.88) * mm});
            skLineSegment(sketch, "E1503", {"start": v(199.97, 261.88) * mm, "end": v(198.45, 262.2) * mm});
            skLineSegment(sketch, "E1504", {"start": v(198.45, 262.2) * mm, "end": v(196.83, 262.3) * mm});
            skLineSegment(sketch, "E1505", {"start": v(196.83, 262.3) * mm, "end": v(195.31, 262.2) * mm});
            skLineSegment(sketch, "E1506", {"start": v(195.31, 262.2) * mm, "end": v(193.7, 261.88) * mm});
            skLineSegment(sketch, "E1507", {"start": v(193.7, 261.88) * mm, "end": v(192.18, 261.45) * mm});
            skLineSegment(sketch, "E1508", {"start": v(192.18, 261.45) * mm, "end": v(190.77, 260.8) * mm});
            skLineSegment(sketch, "E1509", {"start": v(190.77, 260.8) * mm, "end": v(189.47, 259.93) * mm});
            skLineSegment(sketch, "E1510", {"start": v(189.47, 259.93) * mm, "end": v(188.17, 258.96) * mm});
            skLineSegment(sketch, "E1511", {"start": v(188.17, 258.96) * mm, "end": v(187.09, 257.87) * mm});
            skLineSegment(sketch, "E1512", {"start": v(187.09, 257.87) * mm, "end": v(186.11, 256.68) * mm});
            skLineSegment(sketch, "E1513", {"start": v(186.11, 256.68) * mm, "end": v(185.36, 255.28) * mm});
            skLineSegment(sketch, "E1514", {"start": v(185.36, 255.28) * mm, "end": v(184.7, 253.87) * mm});
            skLineSegment(sketch, "E1515", {"start": v(184.7, 253.87) * mm, "end": v(184.17, 252.36) * mm});
            skLineSegment(sketch, "E1516", {"start": v(184.17, 252.36) * mm, "end": v(183.95, 250.84) * mm});
            skLineSegment(sketch, "E1517", {"start": v(183.95, 250.84) * mm, "end": v(183.84, 249.22) * mm});
            skLineSegment(sketch, "E1518", {"start": v(183.84, 249.22) * mm, "end": v(183.84, 205.16) * mm});
            skLineSegment(sketch, "E1519", {"start": v(-19.1, 249.97) * mm, "end": v(-19.1, 204.51) * mm});
            skLineSegment(sketch, "E1520", {"start": v(-26.35, 204.51) * mm, "end": v(-26.25, 203.65) * mm});
            skLineSegment(sketch, "E1521", {"start": v(-26.25, 203.65) * mm, "end": v(-25.92, 202.89) * mm});
            skLineSegment(sketch, "E1522", {"start": v(-25.92, 202.89) * mm, "end": v(-25.49, 202.24) * mm});
            skLineSegment(sketch, "E1523", {"start": v(-25.49, 202.24) * mm, "end": v(-24.95, 201.6) * mm});
            skLineSegment(sketch, "E1524", {"start": v(-24.95, 201.6) * mm, "end": v(-24.3, 201.16) * mm});
            skLineSegment(sketch, "E1525", {"start": v(-24.3, 201.16) * mm, "end": v(-23.54, 200.94) * mm});
            skLineSegment(sketch, "E1526", {"start": v(-23.54, 200.94) * mm, "end": v(-22.67, 200.83) * mm});
            skLineSegment(sketch, "E1527", {"start": v(-22.67, 200.83) * mm, "end": v(-21.92, 200.94) * mm});
            skLineSegment(sketch, "E1528", {"start": v(-21.92, 200.94) * mm, "end": v(-21.16, 201.16) * mm});
            skLineSegment(sketch, "E1529", {"start": v(-21.16, 201.16) * mm, "end": v(-20.4, 201.6) * mm});
            skLineSegment(sketch, "E1530", {"start": v(-20.4, 201.6) * mm, "end": v(-19.86, 202.24) * mm});
            skLineSegment(sketch, "E1531", {"start": v(-19.86, 202.24) * mm, "end": v(-19.43, 202.89) * mm});
            skLineSegment(sketch, "E1532", {"start": v(-19.43, 202.89) * mm, "end": v(-19.1, 203.65) * mm});
            skLineSegment(sketch, "E1533", {"start": v(-19.1, 203.65) * mm, "end": v(-19.1, 204.51) * mm});
            skLineSegment(sketch, "E1534", {"start": v(-26.35, 204.51) * mm, "end": v(-26.35, 249.97) * mm});
            skLineSegment(sketch, "E1535", {"start": v(-19.1, 249.97) * mm, "end": v(-19.1, 250.84) * mm});
            skLineSegment(sketch, "E1536", {"start": v(-19.1, 250.84) * mm, "end": v(-19.43, 251.6) * mm});
            skLineSegment(sketch, "E1537", {"start": v(-19.43, 251.6) * mm, "end": v(-19.86, 252.25) * mm});
            skLineSegment(sketch, "E1538", {"start": v(-19.86, 252.25) * mm, "end": v(-20.4, 252.78) * mm});
            skLineSegment(sketch, "E1539", {"start": v(-20.4, 252.78) * mm, "end": v(-21.16, 253.22) * mm});
            skLineSegment(sketch, "E1540", {"start": v(-21.16, 253.22) * mm, "end": v(-21.92, 253.54) * mm});
            skLineSegment(sketch, "E1541", {"start": v(-21.92, 253.54) * mm, "end": v(-22.67, 253.65) * mm});
            skLineSegment(sketch, "E1542", {"start": v(-22.67, 253.65) * mm, "end": v(-23.54, 253.54) * mm});
            skLineSegment(sketch, "E1543", {"start": v(-23.54, 253.54) * mm, "end": v(-24.3, 253.22) * mm});
            skLineSegment(sketch, "E1544", {"start": v(-24.3, 253.22) * mm, "end": v(-24.95, 252.78) * mm});
            skLineSegment(sketch, "E1545", {"start": v(-24.95, 252.78) * mm, "end": v(-25.49, 252.25) * mm});
            skLineSegment(sketch, "E1546", {"start": v(-25.49, 252.25) * mm, "end": v(-25.92, 251.6) * mm});
            skLineSegment(sketch, "E1547", {"start": v(-25.92, 251.6) * mm, "end": v(-26.25, 250.84) * mm});
            skLineSegment(sketch, "E1548", {"start": v(-26.25, 250.84) * mm, "end": v(-26.35, 249.97) * mm});
            skLineSegment(sketch, "E1549", {"start": v(-35.77, 249.22) * mm, "end": v(-35.77, 205.16) * mm});
            skLineSegment(sketch, "E1550", {"start": v(-35.77, 205.16) * mm, "end": v(-35.66, 203.65) * mm});
            skLineSegment(sketch, "E1551", {"start": v(-35.66, 203.65) * mm, "end": v(-35.34, 202.13) * mm});
            skLineSegment(sketch, "E1552", {"start": v(-35.34, 202.13) * mm, "end": v(-34.9, 200.62) * mm});
            skLineSegment(sketch, "E1553", {"start": v(-34.9, 200.62) * mm, "end": v(-34.26, 199.1) * mm});
            skLineSegment(sketch, "E1554", {"start": v(-34.26, 199.1) * mm, "end": v(-33.4, 197.8) * mm});
            skLineSegment(sketch, "E1555", {"start": v(-33.4, 197.8) * mm, "end": v(-32.42, 196.61) * mm});
            skLineSegment(sketch, "E1556", {"start": v(-32.42, 196.61) * mm, "end": v(-31.33, 195.42) * mm});
            skLineSegment(sketch, "E1557", {"start": v(-31.33, 195.42) * mm, "end": v(-30.14, 194.45) * mm});
            skLineSegment(sketch, "E1558", {"start": v(-30.14, 194.45) * mm, "end": v(-28.74, 193.69) * mm});
            skLineSegment(sketch, "E1559", {"start": v(-28.74, 193.69) * mm, "end": v(-27.33, 193.04) * mm});
            skLineSegment(sketch, "E1560", {"start": v(-27.33, 193.04) * mm, "end": v(-25.81, 192.5) * mm});
            skLineSegment(sketch, "E1561", {"start": v(-25.81, 192.5) * mm, "end": v(-24.3, 192.28) * mm});
            skLineSegment(sketch, "E1562", {"start": v(-24.3, 192.28) * mm, "end": v(-22.67, 192.18) * mm});
            skLineSegment(sketch, "E1563", {"start": v(-22.67, 192.18) * mm, "end": v(-21.16, 192.28) * mm});
            skLineSegment(sketch, "E1564", {"start": v(-21.16, 192.28) * mm, "end": v(-19.54, 192.5) * mm});
            skLineSegment(sketch, "E1565", {"start": v(-19.54, 192.5) * mm, "end": v(-18.02, 193.04) * mm});
            skLineSegment(sketch, "E1566", {"start": v(-18.02, 193.04) * mm, "end": v(-16.61, 193.69) * mm});
            skLineSegment(sketch, "E1567", {"start": v(-16.61, 193.69) * mm, "end": v(-15.31, 194.45) * mm});
            skLineSegment(sketch, "E1568", {"start": v(-15.31, 194.45) * mm, "end": v(-14.02, 195.42) * mm});
            skLineSegment(sketch, "E1569", {"start": v(-14.02, 195.42) * mm, "end": v(-12.93, 196.61) * mm});
            skLineSegment(sketch, "E1570", {"start": v(-12.93, 196.61) * mm, "end": v(-11.96, 197.8) * mm});
            skLineSegment(sketch, "E1571", {"start": v(-11.96, 197.8) * mm, "end": v(-11.1, 199.1) * mm});
            skLineSegment(sketch, "E1572", {"start": v(-11.1, 199.1) * mm, "end": v(-10.45, 200.62) * mm});
            skLineSegment(sketch, "E1573", {"start": v(-10.45, 200.62) * mm, "end": v(-10.01, 202.13) * mm});
            skLineSegment(sketch, "E1574", {"start": v(-10.01, 202.13) * mm, "end": v(-9.69, 203.65) * mm});
            skLineSegment(sketch, "E1575", {"start": v(-9.69, 203.65) * mm, "end": v(-9.69, 205.16) * mm});
            skLineSegment(sketch, "E1576", {"start": v(-9.69, 205.16) * mm, "end": v(-9.69, 249.22) * mm});
            skLineSegment(sketch, "E1577", {"start": v(-9.69, 249.22) * mm, "end": v(-9.69, 250.84) * mm});
            skLineSegment(sketch, "E1578", {"start": v(-9.69, 250.84) * mm, "end": v(-10.01, 252.36) * mm});
            skLineSegment(sketch, "E1579", {"start": v(-10.01, 252.36) * mm, "end": v(-10.45, 253.87) * mm});
            skLineSegment(sketch, "E1580", {"start": v(-10.45, 253.87) * mm, "end": v(-11.1, 255.28) * mm});
            skLineSegment(sketch, "E1581", {"start": v(-11.1, 255.28) * mm, "end": v(-11.96, 256.68) * mm});
            skLineSegment(sketch, "E1582", {"start": v(-11.96, 256.68) * mm, "end": v(-12.93, 257.87) * mm});
            skLineSegment(sketch, "E1583", {"start": v(-12.93, 257.87) * mm, "end": v(-14.02, 258.96) * mm});
            skLineSegment(sketch, "E1584", {"start": v(-14.02, 258.96) * mm, "end": v(-15.31, 259.93) * mm});
            skLineSegment(sketch, "E1585", {"start": v(-15.31, 259.93) * mm, "end": v(-16.61, 260.8) * mm});
            skLineSegment(sketch, "E1586", {"start": v(-16.61, 260.8) * mm, "end": v(-18.02, 261.45) * mm});
            skLineSegment(sketch, "E1587", {"start": v(-18.02, 261.45) * mm, "end": v(-19.54, 261.88) * mm});
            skLineSegment(sketch, "E1588", {"start": v(-19.54, 261.88) * mm, "end": v(-21.16, 262.2) * mm});
            skLineSegment(sketch, "E1589", {"start": v(-21.16, 262.2) * mm, "end": v(-22.67, 262.3) * mm});
            skLineSegment(sketch, "E1590", {"start": v(-22.67, 262.3) * mm, "end": v(-24.3, 262.2) * mm});
            skLineSegment(sketch, "E1591", {"start": v(-24.3, 262.2) * mm, "end": v(-25.81, 261.88) * mm});
            skLineSegment(sketch, "E1592", {"start": v(-25.81, 261.88) * mm, "end": v(-27.33, 261.45) * mm});
            skLineSegment(sketch, "E1593", {"start": v(-27.33, 261.45) * mm, "end": v(-28.74, 260.8) * mm});
            skLineSegment(sketch, "E1594", {"start": v(-28.74, 260.8) * mm, "end": v(-30.14, 259.93) * mm});
            skLineSegment(sketch, "E1595", {"start": v(-30.14, 259.93) * mm, "end": v(-31.33, 258.96) * mm});
            skLineSegment(sketch, "E1596", {"start": v(-31.33, 258.96) * mm, "end": v(-32.42, 257.87) * mm});
            skLineSegment(sketch, "E1597", {"start": v(-32.42, 257.87) * mm, "end": v(-33.4, 256.68) * mm});
            skLineSegment(sketch, "E1598", {"start": v(-33.4, 256.68) * mm, "end": v(-34.26, 255.28) * mm});
            skLineSegment(sketch, "E1599", {"start": v(-34.26, 255.28) * mm, "end": v(-34.9, 253.87) * mm});
            skLineSegment(sketch, "E1600", {"start": v(-34.9, 253.87) * mm, "end": v(-35.34, 252.36) * mm});
            skLineSegment(sketch, "E1601", {"start": v(-35.34, 252.36) * mm, "end": v(-35.66, 250.84) * mm});
            skLineSegment(sketch, "E1602", {"start": v(-35.66, 250.84) * mm, "end": v(-35.77, 249.22) * mm});
            skLineSegment(sketch, "E1603", {"start": v(-76.58, 249.97) * mm, "end": v(-76.58, 204.51) * mm});
            skLineSegment(sketch, "E1604", {"start": v(-83.83, 204.51) * mm, "end": v(-83.72, 203.65) * mm});
            skLineSegment(sketch, "E1605", {"start": v(-83.72, 203.65) * mm, "end": v(-83.5, 202.89) * mm});
            skLineSegment(sketch, "E1606", {"start": v(-83.5, 202.89) * mm, "end": v(-83.07, 202.24) * mm});
            skLineSegment(sketch, "E1607", {"start": v(-83.07, 202.24) * mm, "end": v(-82.53, 201.6) * mm});
            skLineSegment(sketch, "E1608", {"start": v(-82.53, 201.6) * mm, "end": v(-81.77, 201.16) * mm});
            skLineSegment(sketch, "E1609", {"start": v(-81.77, 201.16) * mm, "end": v(-81.01, 200.94) * mm});
            skLineSegment(sketch, "E1610", {"start": v(-81.01, 200.94) * mm, "end": v(-80.26, 200.83) * mm});
            skLineSegment(sketch, "E1611", {"start": v(-80.26, 200.83) * mm, "end": v(-79.39, 200.94) * mm});
            skLineSegment(sketch, "E1612", {"start": v(-79.39, 200.94) * mm, "end": v(-78.63, 201.16) * mm});
            skLineSegment(sketch, "E1613", {"start": v(-78.63, 201.16) * mm, "end": v(-77.98, 201.6) * mm});
            skLineSegment(sketch, "E1614", {"start": v(-77.98, 201.6) * mm, "end": v(-77.44, 202.24) * mm});
            skLineSegment(sketch, "E1615", {"start": v(-77.44, 202.24) * mm, "end": v(-77.01, 202.89) * mm});
            skLineSegment(sketch, "E1616", {"start": v(-77.01, 202.89) * mm, "end": v(-76.68, 203.65) * mm});
            skLineSegment(sketch, "E1617", {"start": v(-76.68, 203.65) * mm, "end": v(-76.58, 204.51) * mm});
            skLineSegment(sketch, "E1618", {"start": v(-83.83, 204.51) * mm, "end": v(-83.83, 249.97) * mm});
            skLineSegment(sketch, "E1619", {"start": v(-76.58, 249.97) * mm, "end": v(-76.68, 250.84) * mm});
            skLineSegment(sketch, "E1620", {"start": v(-76.68, 250.84) * mm, "end": v(-77.01, 251.6) * mm});
            skLineSegment(sketch, "E1621", {"start": v(-77.01, 251.6) * mm, "end": v(-77.44, 252.25) * mm});
            skLineSegment(sketch, "E1622", {"start": v(-77.44, 252.25) * mm, "end": v(-77.98, 252.78) * mm});
            skLineSegment(sketch, "E1623", {"start": v(-77.98, 252.78) * mm, "end": v(-78.63, 253.22) * mm});
            skLineSegment(sketch, "E1624", {"start": v(-78.63, 253.22) * mm, "end": v(-79.39, 253.54) * mm});
            skLineSegment(sketch, "E1625", {"start": v(-79.39, 253.54) * mm, "end": v(-80.26, 253.65) * mm});
            skLineSegment(sketch, "E1626", {"start": v(-80.26, 253.65) * mm, "end": v(-81.01, 253.54) * mm});
            skLineSegment(sketch, "E1627", {"start": v(-81.01, 253.54) * mm, "end": v(-81.77, 253.22) * mm});
            skLineSegment(sketch, "E1628", {"start": v(-81.77, 253.22) * mm, "end": v(-82.53, 252.78) * mm});
            skLineSegment(sketch, "E1629", {"start": v(-82.53, 252.78) * mm, "end": v(-83.07, 252.25) * mm});
            skLineSegment(sketch, "E1630", {"start": v(-83.07, 252.25) * mm, "end": v(-83.5, 251.6) * mm});
            skLineSegment(sketch, "E1631", {"start": v(-83.5, 251.6) * mm, "end": v(-83.72, 250.84) * mm});
            skLineSegment(sketch, "E1632", {"start": v(-83.72, 250.84) * mm, "end": v(-83.83, 249.97) * mm});
            skLineSegment(sketch, "E1633", {"start": v(-93.25, 249.22) * mm, "end": v(-93.25, 205.16) * mm});
            skLineSegment(sketch, "E1634", {"start": v(-93.25, 205.16) * mm, "end": v(-93.14, 203.65) * mm});
            skLineSegment(sketch, "E1635", {"start": v(-93.14, 203.65) * mm, "end": v(-92.92, 202.13) * mm});
            skLineSegment(sketch, "E1636", {"start": v(-92.92, 202.13) * mm, "end": v(-92.38, 200.62) * mm});
            skLineSegment(sketch, "E1637", {"start": v(-92.38, 200.62) * mm, "end": v(-91.84, 199.1) * mm});
            skLineSegment(sketch, "E1638", {"start": v(-91.84, 199.1) * mm, "end": v(-90.97, 197.8) * mm});
            skLineSegment(sketch, "E1639", {"start": v(-90.97, 197.8) * mm, "end": v(-90, 196.61) * mm});
            skLineSegment(sketch, "E1640", {"start": v(-90, 196.61) * mm, "end": v(-88.91, 195.42) * mm});
            skLineSegment(sketch, "E1641", {"start": v(-88.91, 195.42) * mm, "end": v(-87.62, 194.45) * mm});
            skLineSegment(sketch, "E1642", {"start": v(-87.62, 194.45) * mm, "end": v(-86.32, 193.69) * mm});
            skLineSegment(sketch, "E1643", {"start": v(-86.32, 193.69) * mm, "end": v(-84.91, 193.04) * mm});
            skLineSegment(sketch, "E1644", {"start": v(-84.91, 193.04) * mm, "end": v(-83.4, 192.5) * mm});
            skLineSegment(sketch, "E1645", {"start": v(-83.4, 192.5) * mm, "end": v(-81.77, 192.28) * mm});
            skLineSegment(sketch, "E1646", {"start": v(-81.77, 192.28) * mm, "end": v(-80.26, 192.18) * mm});
            skLineSegment(sketch, "E1647", {"start": v(-80.26, 192.18) * mm, "end": v(-78.63, 192.28) * mm});
            skLineSegment(sketch, "E1648", {"start": v(-78.63, 192.28) * mm, "end": v(-77.12, 192.5) * mm});
            skLineSegment(sketch, "E1649", {"start": v(-77.12, 192.5) * mm, "end": v(-75.6, 193.04) * mm});
            skLineSegment(sketch, "E1650", {"start": v(-75.6, 193.04) * mm, "end": v(-74.2, 193.69) * mm});
            skLineSegment(sketch, "E1651", {"start": v(-74.2, 193.69) * mm, "end": v(-72.79, 194.45) * mm});
            skLineSegment(sketch, "E1652", {"start": v(-72.79, 194.45) * mm, "end": v(-71.6, 195.42) * mm});
            skLineSegment(sketch, "E1653", {"start": v(-71.6, 195.42) * mm, "end": v(-70.52, 196.61) * mm});
            skLineSegment(sketch, "E1654", {"start": v(-70.52, 196.61) * mm, "end": v(-69.54, 197.8) * mm});
            skLineSegment(sketch, "E1655", {"start": v(-69.54, 197.8) * mm, "end": v(-68.67, 199.1) * mm});
            skLineSegment(sketch, "E1656", {"start": v(-68.67, 199.1) * mm, "end": v(-68.03, 200.62) * mm});
            skLineSegment(sketch, "E1657", {"start": v(-68.03, 200.62) * mm, "end": v(-67.6, 202.13) * mm});
            skLineSegment(sketch, "E1658", {"start": v(-67.6, 202.13) * mm, "end": v(-67.27, 203.65) * mm});
            skLineSegment(sketch, "E1659", {"start": v(-67.27, 203.65) * mm, "end": v(-67.16, 205.16) * mm});
            skLineSegment(sketch, "E1660", {"start": v(-67.16, 205.16) * mm, "end": v(-67.16, 249.22) * mm});
            skLineSegment(sketch, "E1661", {"start": v(-67.16, 249.22) * mm, "end": v(-67.27, 250.84) * mm});
            skLineSegment(sketch, "E1662", {"start": v(-67.27, 250.84) * mm, "end": v(-67.6, 252.36) * mm});
            skLineSegment(sketch, "E1663", {"start": v(-67.6, 252.36) * mm, "end": v(-68.03, 253.87) * mm});
            skLineSegment(sketch, "E1664", {"start": v(-68.03, 253.87) * mm, "end": v(-68.67, 255.28) * mm});
            skLineSegment(sketch, "E1665", {"start": v(-68.67, 255.28) * mm, "end": v(-69.54, 256.68) * mm});
            skLineSegment(sketch, "E1666", {"start": v(-69.54, 256.68) * mm, "end": v(-70.52, 257.87) * mm});
            skLineSegment(sketch, "E1667", {"start": v(-70.52, 257.87) * mm, "end": v(-71.6, 258.96) * mm});
            skLineSegment(sketch, "E1668", {"start": v(-71.6, 258.96) * mm, "end": v(-72.79, 259.93) * mm});
            skLineSegment(sketch, "E1669", {"start": v(-72.79, 259.93) * mm, "end": v(-74.2, 260.8) * mm});
            skLineSegment(sketch, "E1670", {"start": v(-74.2, 260.8) * mm, "end": v(-75.6, 261.45) * mm});
            skLineSegment(sketch, "E1671", {"start": v(-75.6, 261.45) * mm, "end": v(-77.12, 261.88) * mm});
            skLineSegment(sketch, "E1672", {"start": v(-77.12, 261.88) * mm, "end": v(-78.63, 262.2) * mm});
            skLineSegment(sketch, "E1673", {"start": v(-78.63, 262.2) * mm, "end": v(-80.26, 262.3) * mm});
            skLineSegment(sketch, "E1674", {"start": v(-80.26, 262.3) * mm, "end": v(-81.77, 262.2) * mm});
            skLineSegment(sketch, "E1675", {"start": v(-81.77, 262.2) * mm, "end": v(-83.4, 261.88) * mm});
            skLineSegment(sketch, "E1676", {"start": v(-83.4, 261.88) * mm, "end": v(-84.91, 261.45) * mm});
            skLineSegment(sketch, "E1677", {"start": v(-84.91, 261.45) * mm, "end": v(-86.32, 260.8) * mm});
            skLineSegment(sketch, "E1678", {"start": v(-86.32, 260.8) * mm, "end": v(-87.62, 259.93) * mm});
            skLineSegment(sketch, "E1679", {"start": v(-87.62, 259.93) * mm, "end": v(-88.91, 258.96) * mm});
            skLineSegment(sketch, "E1680", {"start": v(-88.91, 258.96) * mm, "end": v(-90, 257.87) * mm});
            skLineSegment(sketch, "E1681", {"start": v(-90, 257.87) * mm, "end": v(-90.97, 256.68) * mm});
            skLineSegment(sketch, "E1682", {"start": v(-90.97, 256.68) * mm, "end": v(-91.84, 255.28) * mm});
            skLineSegment(sketch, "E1683", {"start": v(-91.84, 255.28) * mm, "end": v(-92.38, 253.87) * mm});
            skLineSegment(sketch, "E1684", {"start": v(-92.38, 253.87) * mm, "end": v(-92.92, 252.36) * mm});
            skLineSegment(sketch, "E1685", {"start": v(-92.92, 252.36) * mm, "end": v(-93.14, 250.84) * mm});
            skLineSegment(sketch, "E1686", {"start": v(-93.14, 250.84) * mm, "end": v(-93.25, 249.22) * mm});
            skLineSegment(sketch, "E1687", {"start": v(-246.72, 205.16) * mm, "end": v(-246.62, 203.65) * mm});
            skLineSegment(sketch, "E1688", {"start": v(-246.62, 203.65) * mm, "end": v(-246.3, 202.13) * mm});
            skLineSegment(sketch, "E1689", {"start": v(-246.3, 202.13) * mm, "end": v(-245.86, 200.62) * mm});
            skLineSegment(sketch, "E1690", {"start": v(-245.86, 200.62) * mm, "end": v(-245.21, 199.1) * mm});
            skLineSegment(sketch, "E1691", {"start": v(-245.21, 199.1) * mm, "end": v(-244.34, 197.8) * mm});
            skLineSegment(sketch, "E1692", {"start": v(-244.34, 197.8) * mm, "end": v(-243.37, 196.61) * mm});
            skLineSegment(sketch, "E1693", {"start": v(-243.37, 196.61) * mm, "end": v(-242.29, 195.42) * mm});
            skLineSegment(sketch, "E1694", {"start": v(-242.29, 195.42) * mm, "end": v(-240.99, 194.45) * mm});
            skLineSegment(sketch, "E1695", {"start": v(-240.99, 194.45) * mm, "end": v(-239.69, 193.69) * mm});
            skLineSegment(sketch, "E1696", {"start": v(-239.69, 193.69) * mm, "end": v(-238.28, 193.04) * mm});
            skLineSegment(sketch, "E1697", {"start": v(-238.28, 193.04) * mm, "end": v(-236.77, 192.5) * mm});
            skLineSegment(sketch, "E1698", {"start": v(-236.77, 192.5) * mm, "end": v(-235.25, 192.28) * mm});
            skLineSegment(sketch, "E1699", {"start": v(-235.25, 192.28) * mm, "end": v(-233.63, 192.18) * mm});
            skLineSegment(sketch, "E1700", {"start": v(-233.63, 192.18) * mm, "end": v(-232.11, 192.28) * mm});
            skLineSegment(sketch, "E1701", {"start": v(-232.11, 192.28) * mm, "end": v(-230.49, 192.5) * mm});
            skLineSegment(sketch, "E1702", {"start": v(-230.49, 192.5) * mm, "end": v(-228.97, 193.04) * mm});
            skLineSegment(sketch, "E1703", {"start": v(-228.97, 193.04) * mm, "end": v(-227.57, 193.69) * mm});
            skLineSegment(sketch, "E1704", {"start": v(-227.57, 193.69) * mm, "end": v(-226.27, 194.45) * mm});
            skLineSegment(sketch, "E1705", {"start": v(-226.27, 194.45) * mm, "end": v(-224.97, 195.42) * mm});
            skLineSegment(sketch, "E1706", {"start": v(-224.97, 195.42) * mm, "end": v(-223.89, 196.61) * mm});
            skLineSegment(sketch, "E1707", {"start": v(-223.89, 196.61) * mm, "end": v(-222.91, 197.8) * mm});
            skLineSegment(sketch, "E1708", {"start": v(-222.91, 197.8) * mm, "end": v(-222.05, 199.1) * mm});
            skLineSegment(sketch, "E1709", {"start": v(-222.05, 199.1) * mm, "end": v(-221.4, 200.62) * mm});
            skLineSegment(sketch, "E1710", {"start": v(-221.4, 200.62) * mm, "end": v(-220.96, 202.13) * mm});
            skLineSegment(sketch, "E1711", {"start": v(-220.96, 202.13) * mm, "end": v(-220.64, 203.65) * mm});
            skLineSegment(sketch, "E1712", {"start": v(-220.64, 203.65) * mm, "end": v(-220.64, 205.16) * mm});
            skLineSegment(sketch, "E1713", {"start": v(-220.64, 205.16) * mm, "end": v(-220.64, 216.2) * mm});
            skLineSegment(sketch, "E1714", {"start": v(-220.64, 216.2) * mm, "end": v(-230.06, 216.2) * mm});
            skLineSegment(sketch, "E1715", {"start": v(-230.06, 216.2) * mm, "end": v(-230.06, 204.51) * mm});
            skLineSegment(sketch, "E1716", {"start": v(-237.3, 204.51) * mm, "end": v(-237.2, 203.65) * mm});
            skLineSegment(sketch, "E1717", {"start": v(-237.2, 203.65) * mm, "end": v(-236.88, 202.89) * mm});
            skLineSegment(sketch, "E1718", {"start": v(-236.88, 202.89) * mm, "end": v(-236.44, 202.24) * mm});
            skLineSegment(sketch, "E1719", {"start": v(-236.44, 202.24) * mm, "end": v(-235.9, 201.6) * mm});
            skLineSegment(sketch, "E1720", {"start": v(-235.9, 201.6) * mm, "end": v(-235.25, 201.16) * mm});
            skLineSegment(sketch, "E1721", {"start": v(-235.25, 201.16) * mm, "end": v(-234.39, 200.94) * mm});
            skLineSegment(sketch, "E1722", {"start": v(-234.39, 200.94) * mm, "end": v(-233.63, 200.83) * mm});
            skLineSegment(sketch, "E1723", {"start": v(-233.63, 200.83) * mm, "end": v(-232.87, 200.94) * mm});
            skLineSegment(sketch, "E1724", {"start": v(-232.87, 200.94) * mm, "end": v(-232.11, 201.16) * mm});
            skLineSegment(sketch, "E1725", {"start": v(-232.11, 201.16) * mm, "end": v(-231.36, 201.6) * mm});
            skLineSegment(sketch, "E1726", {"start": v(-231.36, 201.6) * mm, "end": v(-230.82, 202.24) * mm});
            skLineSegment(sketch, "E1727", {"start": v(-230.82, 202.24) * mm, "end": v(-230.38, 202.89) * mm});
            skLineSegment(sketch, "E1728", {"start": v(-230.38, 202.89) * mm, "end": v(-230.06, 203.65) * mm});
            skLineSegment(sketch, "E1729", {"start": v(-230.06, 203.65) * mm, "end": v(-230.06, 204.51) * mm});
            skLineSegment(sketch, "E1730", {"start": v(-237.3, 204.51) * mm, "end": v(-237.3, 249.97) * mm});
            skLineSegment(sketch, "E1731", {"start": v(-230.06, 249.97) * mm, "end": v(-230.06, 250.84) * mm});
            skLineSegment(sketch, "E1732", {"start": v(-230.06, 250.84) * mm, "end": v(-230.38, 251.6) * mm});
            skLineSegment(sketch, "E1733", {"start": v(-230.38, 251.6) * mm, "end": v(-230.82, 252.25) * mm});
            skLineSegment(sketch, "E1734", {"start": v(-230.82, 252.25) * mm, "end": v(-231.36, 252.78) * mm});
            skLineSegment(sketch, "E1735", {"start": v(-231.36, 252.78) * mm, "end": v(-232.11, 253.22) * mm});
            skLineSegment(sketch, "E1736", {"start": v(-232.11, 253.22) * mm, "end": v(-232.87, 253.54) * mm});
            skLineSegment(sketch, "E1737", {"start": v(-232.87, 253.54) * mm, "end": v(-233.63, 253.65) * mm});
            skLineSegment(sketch, "E1738", {"start": v(-233.63, 253.65) * mm, "end": v(-234.39, 253.54) * mm});
            skLineSegment(sketch, "E1739", {"start": v(-234.39, 253.54) * mm, "end": v(-235.25, 253.22) * mm});
            skLineSegment(sketch, "E1740", {"start": v(-235.25, 253.22) * mm, "end": v(-235.9, 252.78) * mm});
            skLineSegment(sketch, "E1741", {"start": v(-235.9, 252.78) * mm, "end": v(-236.44, 252.25) * mm});
            skLineSegment(sketch, "E1742", {"start": v(-236.44, 252.25) * mm, "end": v(-236.88, 251.6) * mm});
            skLineSegment(sketch, "E1743", {"start": v(-236.88, 251.6) * mm, "end": v(-237.2, 250.84) * mm});
            skLineSegment(sketch, "E1744", {"start": v(-237.2, 250.84) * mm, "end": v(-237.3, 249.97) * mm});
            skLineSegment(sketch, "E1745", {"start": v(-230.06, 249.97) * mm, "end": v(-230.06, 238.28) * mm});
            skLineSegment(sketch, "E1746", {"start": v(-230.06, 238.28) * mm, "end": v(-220.64, 238.28) * mm});
            skLineSegment(sketch, "E1747", {"start": v(-220.64, 238.28) * mm, "end": v(-220.64, 249.22) * mm});
            skLineSegment(sketch, "E1748", {"start": v(-220.64, 249.22) * mm, "end": v(-220.64, 250.84) * mm});
            skLineSegment(sketch, "E1749", {"start": v(-220.64, 250.84) * mm, "end": v(-220.96, 252.36) * mm});
            skLineSegment(sketch, "E1750", {"start": v(-220.96, 252.36) * mm, "end": v(-221.4, 253.87) * mm});
            skLineSegment(sketch, "E1751", {"start": v(-221.4, 253.87) * mm, "end": v(-222.05, 255.28) * mm});
            skLineSegment(sketch, "E1752", {"start": v(-222.05, 255.28) * mm, "end": v(-222.91, 256.68) * mm});
            skLineSegment(sketch, "E1753", {"start": v(-222.91, 256.68) * mm, "end": v(-223.89, 257.87) * mm});
            skLineSegment(sketch, "E1754", {"start": v(-223.89, 257.87) * mm, "end": v(-224.97, 258.96) * mm});
            skLineSegment(sketch, "E1755", {"start": v(-224.97, 258.96) * mm, "end": v(-226.27, 259.93) * mm});
            skLineSegment(sketch, "E1756", {"start": v(-226.27, 259.93) * mm, "end": v(-227.57, 260.8) * mm});
            skLineSegment(sketch, "E1757", {"start": v(-227.57, 260.8) * mm, "end": v(-228.97, 261.45) * mm});
            skLineSegment(sketch, "E1758", {"start": v(-228.97, 261.45) * mm, "end": v(-230.49, 261.88) * mm});
            skLineSegment(sketch, "E1759", {"start": v(-230.49, 261.88) * mm, "end": v(-232.11, 262.2) * mm});
            skLineSegment(sketch, "E1760", {"start": v(-232.11, 262.2) * mm, "end": v(-233.63, 262.3) * mm});
            skLineSegment(sketch, "E1761", {"start": v(-233.63, 262.3) * mm, "end": v(-235.25, 262.2) * mm});
            skLineSegment(sketch, "E1762", {"start": v(-235.25, 262.2) * mm, "end": v(-236.77, 261.88) * mm});
            skLineSegment(sketch, "E1763", {"start": v(-236.77, 261.88) * mm, "end": v(-238.28, 261.45) * mm});
            skLineSegment(sketch, "E1764", {"start": v(-238.28, 261.45) * mm, "end": v(-239.69, 260.8) * mm});
            skLineSegment(sketch, "E1765", {"start": v(-239.69, 260.8) * mm, "end": v(-240.99, 259.93) * mm});
            skLineSegment(sketch, "E1766", {"start": v(-240.99, 259.93) * mm, "end": v(-242.29, 258.96) * mm});
            skLineSegment(sketch, "E1767", {"start": v(-242.29, 258.96) * mm, "end": v(-243.37, 257.87) * mm});
            skLineSegment(sketch, "E1768", {"start": v(-243.37, 257.87) * mm, "end": v(-244.34, 256.68) * mm});
            skLineSegment(sketch, "E1769", {"start": v(-244.34, 256.68) * mm, "end": v(-245.21, 255.28) * mm});
            skLineSegment(sketch, "E1770", {"start": v(-245.21, 255.28) * mm, "end": v(-245.86, 253.87) * mm});
            skLineSegment(sketch, "E1771", {"start": v(-245.86, 253.87) * mm, "end": v(-246.3, 252.36) * mm});
            skLineSegment(sketch, "E1772", {"start": v(-246.3, 252.36) * mm, "end": v(-246.62, 250.84) * mm});
            skLineSegment(sketch, "E1773", {"start": v(-246.62, 250.84) * mm, "end": v(-246.72, 249.22) * mm});
            skLineSegment(sketch, "E1774", {"start": v(-246.72, 249.22) * mm, "end": v(-246.72, 205.16) * mm});
            skLineSegment(sketch, "E1775", {"start": v(-169.99, 205.16) * mm, "end": v(-169.88, 203.65) * mm});
            skLineSegment(sketch, "E1776", {"start": v(-169.88, 203.65) * mm, "end": v(-169.66, 202.13) * mm});
            skLineSegment(sketch, "E1777", {"start": v(-169.66, 202.13) * mm, "end": v(-169.12, 200.62) * mm});
            skLineSegment(sketch, "E1778", {"start": v(-169.12, 200.62) * mm, "end": v(-168.47, 199.1) * mm});
            skLineSegment(sketch, "E1779", {"start": v(-168.47, 199.1) * mm, "end": v(-167.71, 197.8) * mm});
            skLineSegment(sketch, "E1780", {"start": v(-167.71, 197.8) * mm, "end": v(-166.74, 196.61) * mm});
            skLineSegment(sketch, "E1781", {"start": v(-166.74, 196.61) * mm, "end": v(-165.55, 195.42) * mm});
            skLineSegment(sketch, "E1782", {"start": v(-165.55, 195.42) * mm, "end": v(-164.36, 194.45) * mm});
            skLineSegment(sketch, "E1783", {"start": v(-164.36, 194.45) * mm, "end": v(-163.06, 193.69) * mm});
            skLineSegment(sketch, "E1784", {"start": v(-163.06, 193.69) * mm, "end": v(-161.54, 193.04) * mm});
            skLineSegment(sketch, "E1785", {"start": v(-161.54, 193.04) * mm, "end": v(-160.03, 192.5) * mm});
            skLineSegment(sketch, "E1786", {"start": v(-160.03, 192.5) * mm, "end": v(-158.51, 192.28) * mm});
            skLineSegment(sketch, "E1787", {"start": v(-158.51, 192.28) * mm, "end": v(-157, 192.18) * mm});
            skLineSegment(sketch, "E1788", {"start": v(-157, 192.18) * mm, "end": v(-155.37, 192.28) * mm});
            skLineSegment(sketch, "E1789", {"start": v(-155.37, 192.28) * mm, "end": v(-153.86, 192.5) * mm});
            skLineSegment(sketch, "E1790", {"start": v(-153.86, 192.5) * mm, "end": v(-152.34, 193.04) * mm});
            skLineSegment(sketch, "E1791", {"start": v(-152.34, 193.04) * mm, "end": v(-150.94, 193.69) * mm});
            skLineSegment(sketch, "E1792", {"start": v(-150.94, 193.69) * mm, "end": v(-149.53, 194.45) * mm});
            skLineSegment(sketch, "E1793", {"start": v(-149.53, 194.45) * mm, "end": v(-148.34, 195.42) * mm});
            skLineSegment(sketch, "E1794", {"start": v(-148.34, 195.42) * mm, "end": v(-147.15, 196.61) * mm});
            skLineSegment(sketch, "E1795", {"start": v(-147.15, 196.61) * mm, "end": v(-146.17, 197.8) * mm});
            skLineSegment(sketch, "E1796", {"start": v(-146.17, 197.8) * mm, "end": v(-145.42, 199.1) * mm});
            skLineSegment(sketch, "E1797", {"start": v(-145.42, 199.1) * mm, "end": v(-144.77, 200.62) * mm});
            skLineSegment(sketch, "E1798", {"start": v(-144.77, 200.62) * mm, "end": v(-144.33, 202.13) * mm});
            skLineSegment(sketch, "E1799", {"start": v(-144.33, 202.13) * mm, "end": v(-144, 203.65) * mm});
            skLineSegment(sketch, "E1800", {"start": v(-144, 203.65) * mm, "end": v(-143.9, 205.16) * mm});
            skLineSegment(sketch, "E1801", {"start": v(-143.9, 205.16) * mm, "end": v(-143.9, 216.2) * mm});
            skLineSegment(sketch, "E1802", {"start": v(-143.9, 216.2) * mm, "end": v(-153.32, 216.2) * mm});
            skLineSegment(sketch, "E1803", {"start": v(-153.32, 216.2) * mm, "end": v(-153.32, 204.51) * mm});
            skLineSegment(sketch, "E1804", {"start": v(-160.57, 204.51) * mm, "end": v(-160.46, 203.65) * mm});
            skLineSegment(sketch, "E1805", {"start": v(-160.46, 203.65) * mm, "end": v(-160.24, 202.89) * mm});
            skLineSegment(sketch, "E1806", {"start": v(-160.24, 202.89) * mm, "end": v(-159.81, 202.24) * mm});
            skLineSegment(sketch, "E1807", {"start": v(-159.81, 202.24) * mm, "end": v(-159.16, 201.6) * mm});
            skLineSegment(sketch, "E1808", {"start": v(-159.16, 201.6) * mm, "end": v(-158.51, 201.16) * mm});
            skLineSegment(sketch, "E1809", {"start": v(-158.51, 201.16) * mm, "end": v(-157.76, 200.94) * mm});
            skLineSegment(sketch, "E1810", {"start": v(-157.76, 200.94) * mm, "end": v(-157, 200.83) * mm});
            skLineSegment(sketch, "E1811", {"start": v(-157, 200.83) * mm, "end": v(-156.13, 200.94) * mm});
            skLineSegment(sketch, "E1812", {"start": v(-156.13, 200.94) * mm, "end": v(-155.37, 201.16) * mm});
            skLineSegment(sketch, "E1813", {"start": v(-155.37, 201.16) * mm, "end": v(-154.73, 201.6) * mm});
            skLineSegment(sketch, "E1814", {"start": v(-154.73, 201.6) * mm, "end": v(-154.07, 202.24) * mm});
            skLineSegment(sketch, "E1815", {"start": v(-154.07, 202.24) * mm, "end": v(-153.64, 202.89) * mm});
            skLineSegment(sketch, "E1816", {"start": v(-153.64, 202.89) * mm, "end": v(-153.42, 203.65) * mm});
            skLineSegment(sketch, "E1817", {"start": v(-153.42, 203.65) * mm, "end": v(-153.32, 204.51) * mm});
            skLineSegment(sketch, "E1818", {"start": v(-160.57, 204.51) * mm, "end": v(-160.57, 249.97) * mm});
            skLineSegment(sketch, "E1819", {"start": v(-153.32, 249.97) * mm, "end": v(-153.42, 250.84) * mm});
            skLineSegment(sketch, "E1820", {"start": v(-153.42, 250.84) * mm, "end": v(-153.64, 251.6) * mm});
            skLineSegment(sketch, "E1821", {"start": v(-153.64, 251.6) * mm, "end": v(-154.07, 252.25) * mm});
            skLineSegment(sketch, "E1822", {"start": v(-154.07, 252.25) * mm, "end": v(-154.73, 252.78) * mm});
            skLineSegment(sketch, "E1823", {"start": v(-154.73, 252.78) * mm, "end": v(-155.37, 253.22) * mm});
            skLineSegment(sketch, "E1824", {"start": v(-155.37, 253.22) * mm, "end": v(-156.13, 253.54) * mm});
            skLineSegment(sketch, "E1825", {"start": v(-156.13, 253.54) * mm, "end": v(-157, 253.65) * mm});
            skLineSegment(sketch, "E1826", {"start": v(-157, 253.65) * mm, "end": v(-157.76, 253.54) * mm});
            skLineSegment(sketch, "E1827", {"start": v(-157.76, 253.54) * mm, "end": v(-158.51, 253.22) * mm});
            skLineSegment(sketch, "E1828", {"start": v(-158.51, 253.22) * mm, "end": v(-159.16, 252.78) * mm});
            skLineSegment(sketch, "E1829", {"start": v(-159.16, 252.78) * mm, "end": v(-159.81, 252.25) * mm});
            skLineSegment(sketch, "E1830", {"start": v(-159.81, 252.25) * mm, "end": v(-160.24, 251.6) * mm});
            skLineSegment(sketch, "E1831", {"start": v(-160.24, 251.6) * mm, "end": v(-160.46, 250.84) * mm});
            skLineSegment(sketch, "E1832", {"start": v(-160.46, 250.84) * mm, "end": v(-160.57, 249.97) * mm});
            skLineSegment(sketch, "E1833", {"start": v(-153.32, 249.97) * mm, "end": v(-153.32, 238.28) * mm});
            skLineSegment(sketch, "E1834", {"start": v(-153.32, 238.28) * mm, "end": v(-143.9, 238.28) * mm});
            skLineSegment(sketch, "E1835", {"start": v(-143.9, 238.28) * mm, "end": v(-143.9, 249.22) * mm});
            skLineSegment(sketch, "E1836", {"start": v(-143.9, 249.22) * mm, "end": v(-144, 250.84) * mm});
            skLineSegment(sketch, "E1837", {"start": v(-144, 250.84) * mm, "end": v(-144.33, 252.36) * mm});
            skLineSegment(sketch, "E1838", {"start": v(-144.33, 252.36) * mm, "end": v(-144.77, 253.87) * mm});
            skLineSegment(sketch, "E1839", {"start": v(-144.77, 253.87) * mm, "end": v(-145.42, 255.28) * mm});
            skLineSegment(sketch, "E1840", {"start": v(-145.42, 255.28) * mm, "end": v(-146.17, 256.68) * mm});
            skLineSegment(sketch, "E1841", {"start": v(-146.17, 256.68) * mm, "end": v(-147.15, 257.87) * mm});
            skLineSegment(sketch, "E1842", {"start": v(-147.15, 257.87) * mm, "end": v(-148.34, 258.96) * mm});
            skLineSegment(sketch, "E1843", {"start": v(-148.34, 258.96) * mm, "end": v(-149.53, 259.93) * mm});
            skLineSegment(sketch, "E1844", {"start": v(-149.53, 259.93) * mm, "end": v(-150.94, 260.8) * mm});
            skLineSegment(sketch, "E1845", {"start": v(-150.94, 260.8) * mm, "end": v(-152.34, 261.45) * mm});
            skLineSegment(sketch, "E1846", {"start": v(-152.34, 261.45) * mm, "end": v(-153.86, 261.88) * mm});
            skLineSegment(sketch, "E1847", {"start": v(-153.86, 261.88) * mm, "end": v(-155.37, 262.2) * mm});
            skLineSegment(sketch, "E1848", {"start": v(-155.37, 262.2) * mm, "end": v(-157, 262.3) * mm});
            skLineSegment(sketch, "E1849", {"start": v(-157, 262.3) * mm, "end": v(-158.51, 262.2) * mm});
            skLineSegment(sketch, "E1850", {"start": v(-158.51, 262.2) * mm, "end": v(-160.03, 261.88) * mm});
            skLineSegment(sketch, "E1851", {"start": v(-160.03, 261.88) * mm, "end": v(-161.54, 261.45) * mm});
            skLineSegment(sketch, "E1852", {"start": v(-161.54, 261.45) * mm, "end": v(-163.06, 260.8) * mm});
            skLineSegment(sketch, "E1853", {"start": v(-163.06, 260.8) * mm, "end": v(-164.36, 259.93) * mm});
            skLineSegment(sketch, "E1854", {"start": v(-164.36, 259.93) * mm, "end": v(-165.55, 258.96) * mm});
            skLineSegment(sketch, "E1855", {"start": v(-165.55, 258.96) * mm, "end": v(-166.74, 257.87) * mm});
            skLineSegment(sketch, "E1856", {"start": v(-166.74, 257.87) * mm, "end": v(-167.71, 256.68) * mm});
            skLineSegment(sketch, "E1857", {"start": v(-167.71, 256.68) * mm, "end": v(-168.47, 255.28) * mm});
            skLineSegment(sketch, "E1858", {"start": v(-168.47, 255.28) * mm, "end": v(-169.12, 253.87) * mm});
            skLineSegment(sketch, "E1859", {"start": v(-169.12, 253.87) * mm, "end": v(-169.66, 252.36) * mm});
            skLineSegment(sketch, "E1860", {"start": v(-169.66, 252.36) * mm, "end": v(-169.88, 250.84) * mm});
            skLineSegment(sketch, "E1861", {"start": v(-169.88, 250.84) * mm, "end": v(-169.99, 249.22) * mm});
            skLineSegment(sketch, "E1862", {"start": v(-169.99, 249.22) * mm, "end": v(-169.99, 205.16) * mm});
            skLineSegment(sketch, "E1863", {"start": v(129.07, 262.3) * mm, "end": v(119.77, 262.3) * mm});
            skLineSegment(sketch, "E1864", {"start": v(119.77, 262.3) * mm, "end": v(119.77, 192.18) * mm});
            skLineSegment(sketch, "E1865", {"start": v(119.77, 192.18) * mm, "end": v(129.07, 192.18) * mm});
            skLineSegment(sketch, "E1866", {"start": v(129.07, 192.18) * mm, "end": v(129.07, 231.79) * mm});
            skLineSegment(sketch, "E1867", {"start": v(129.07, 231.79) * mm, "end": v(130.05, 231.79) * mm});
            skLineSegment(sketch, "E1868", {"start": v(130.05, 231.79) * mm, "end": v(140.54, 192.18) * mm});
            skLineSegment(sketch, "E1869", {"start": v(140.54, 192.18) * mm, "end": v(149.31, 192.18) * mm});
            skLineSegment(sketch, "E1870", {"start": v(149.31, 192.18) * mm, "end": v(149.31, 262.3) * mm});
            skLineSegment(sketch, "E1871", {"start": v(149.31, 262.3) * mm, "end": v(140.54, 262.3) * mm});
            skLineSegment(sketch, "E1872", {"start": v(140.54, 262.3) * mm, "end": v(140.54, 221.83) * mm});
            skLineSegment(sketch, "E1873", {"start": v(140.54, 221.83) * mm, "end": v(139.36, 221.83) * mm});
            skLineSegment(sketch, "E1874", {"start": v(139.36, 221.83) * mm, "end": v(129.07, 262.3) * mm});
            skLineSegment(sketch, "E1875", {"start": v(57.53, 249.97) * mm, "end": v(57.53, 238.28) * mm});
            skLineSegment(sketch, "E1876", {"start": v(57.53, 238.28) * mm, "end": v(66.95, 238.28) * mm});
            skLineSegment(sketch, "E1877", {"start": v(66.95, 238.28) * mm, "end": v(66.95, 249.22) * mm});
            skLineSegment(sketch, "E1878", {"start": v(66.95, 249.22) * mm, "end": v(66.84, 250.84) * mm});
            skLineSegment(sketch, "E1879", {"start": v(66.84, 250.84) * mm, "end": v(66.62, 252.36) * mm});
            skLineSegment(sketch, "E1880", {"start": v(66.62, 252.36) * mm, "end": v(66.08, 253.87) * mm});
            skLineSegment(sketch, "E1881", {"start": v(66.08, 253.87) * mm, "end": v(65.43, 255.28) * mm});
            skLineSegment(sketch, "E1882", {"start": v(65.43, 255.28) * mm, "end": v(64.67, 256.68) * mm});
            skLineSegment(sketch, "E1883", {"start": v(64.67, 256.68) * mm, "end": v(63.7, 257.87) * mm});
            skLineSegment(sketch, "E1884", {"start": v(63.7, 257.87) * mm, "end": v(62.5, 258.96) * mm});
            skLineSegment(sketch, "E1885", {"start": v(62.5, 258.96) * mm, "end": v(61.31, 259.93) * mm});
            skLineSegment(sketch, "E1886", {"start": v(61.31, 259.93) * mm, "end": v(60.02, 260.8) * mm});
            skLineSegment(sketch, "E1887", {"start": v(60.02, 260.8) * mm, "end": v(58.5, 261.45) * mm});
            skLineSegment(sketch, "E1888", {"start": v(58.5, 261.45) * mm, "end": v(56.99, 261.88) * mm});
            skLineSegment(sketch, "E1889", {"start": v(56.99, 261.88) * mm, "end": v(55.47, 262.2) * mm});
            skLineSegment(sketch, "E1890", {"start": v(55.47, 262.2) * mm, "end": v(53.96, 262.3) * mm});
            skLineSegment(sketch, "E1891", {"start": v(53.96, 262.3) * mm, "end": v(52.33, 262.2) * mm});
            skLineSegment(sketch, "E1892", {"start": v(52.33, 262.2) * mm, "end": v(50.82, 261.88) * mm});
            skLineSegment(sketch, "E1893", {"start": v(50.82, 261.88) * mm, "end": v(49.3, 261.45) * mm});
            skLineSegment(sketch, "E1894", {"start": v(49.3, 261.45) * mm, "end": v(47.9, 260.8) * mm});
            skLineSegment(sketch, "E1895", {"start": v(47.9, 260.8) * mm, "end": v(46.49, 259.93) * mm});
            skLineSegment(sketch, "E1896", {"start": v(46.49, 259.93) * mm, "end": v(45.3, 258.96) * mm});
            skLineSegment(sketch, "E1897", {"start": v(45.3, 258.96) * mm, "end": v(44.1, 257.87) * mm});
            skLineSegment(sketch, "E1898", {"start": v(44.1, 257.87) * mm, "end": v(43.13, 256.68) * mm});
            skLineSegment(sketch, "E1899", {"start": v(43.13, 256.68) * mm, "end": v(42.37, 255.28) * mm});
            skLineSegment(sketch, "E1900", {"start": v(42.37, 255.28) * mm, "end": v(41.73, 253.87) * mm});
            skLineSegment(sketch, "E1901", {"start": v(41.73, 253.87) * mm, "end": v(41.19, 252.36) * mm});
            skLineSegment(sketch, "E1902", {"start": v(41.19, 252.36) * mm, "end": v(40.97, 250.84) * mm});
            skLineSegment(sketch, "E1903", {"start": v(40.97, 250.84) * mm, "end": v(40.86, 249.22) * mm});
            skLineSegment(sketch, "E1904", {"start": v(40.86, 249.22) * mm, "end": v(40.86, 205.16) * mm});
            skLineSegment(sketch, "E1905", {"start": v(40.86, 205.16) * mm, "end": v(40.97, 203.65) * mm});
            skLineSegment(sketch, "E1906", {"start": v(40.97, 203.65) * mm, "end": v(41.19, 202.13) * mm});
            skLineSegment(sketch, "E1907", {"start": v(41.19, 202.13) * mm, "end": v(41.73, 200.62) * mm});
            skLineSegment(sketch, "E1908", {"start": v(41.73, 200.62) * mm, "end": v(42.37, 199.1) * mm});
            skLineSegment(sketch, "E1909", {"start": v(42.37, 199.1) * mm, "end": v(43.13, 197.8) * mm});
            skLineSegment(sketch, "E1910", {"start": v(43.13, 197.8) * mm, "end": v(44.1, 196.61) * mm});
            skLineSegment(sketch, "E1911", {"start": v(44.1, 196.61) * mm, "end": v(45.3, 195.42) * mm});
            skLineSegment(sketch, "E1912", {"start": v(45.3, 195.42) * mm, "end": v(46.49, 194.45) * mm});
            skLineSegment(sketch, "E1913", {"start": v(46.49, 194.45) * mm, "end": v(47.9, 193.69) * mm});
            skLineSegment(sketch, "E1914", {"start": v(47.9, 193.69) * mm, "end": v(49.3, 193.04) * mm});
            skLineSegment(sketch, "E1915", {"start": v(49.3, 193.04) * mm, "end": v(50.82, 192.5) * mm});
            skLineSegment(sketch, "E1916", {"start": v(50.82, 192.5) * mm, "end": v(52.33, 192.28) * mm});
            skLineSegment(sketch, "E1917", {"start": v(52.33, 192.28) * mm, "end": v(53.96, 192.18) * mm});
            skLineSegment(sketch, "E1918", {"start": v(53.96, 192.18) * mm, "end": v(55.04, 192.4) * mm});
            skLineSegment(sketch, "E1919", {"start": v(55.04, 192.4) * mm, "end": v(56.23, 192.71) * mm});
            skLineSegment(sketch, "E1920", {"start": v(56.23, 192.71) * mm, "end": v(57.2, 193.25) * mm});
            skLineSegment(sketch, "E1921", {"start": v(57.2, 193.25) * mm, "end": v(58.18, 194.01) * mm});
            skLineSegment(sketch, "E1922", {"start": v(58.18, 194.01) * mm, "end": v(59.04, 194.88) * mm});
            skLineSegment(sketch, "E1923", {"start": v(59.04, 194.88) * mm, "end": v(59.7, 195.85) * mm});
            skLineSegment(sketch, "E1924", {"start": v(59.7, 195.85) * mm, "end": v(61.42, 194.66) * mm});
            skLineSegment(sketch, "E1925", {"start": v(61.42, 194.66) * mm, "end": v(61.42, 192.18) * mm});
            skLineSegment(sketch, "E1926", {"start": v(61.42, 192.18) * mm, "end": v(66.95, 192.18) * mm});
            skLineSegment(sketch, "E1927", {"start": v(66.95, 192.18) * mm, "end": v(66.95, 226.7) * mm});
            skLineSegment(sketch, "E1928", {"start": v(66.95, 226.7) * mm, "end": v(53.74, 226.7) * mm});
            skLineSegment(sketch, "E1929", {"start": v(53.74, 226.7) * mm, "end": v(53.74, 218.37) * mm});
            skLineSegment(sketch, "E1930", {"start": v(53.74, 218.37) * mm, "end": v(57.53, 218.37) * mm});
            skLineSegment(sketch, "E1931", {"start": v(57.53, 218.37) * mm, "end": v(57.53, 204.51) * mm});
            skLineSegment(sketch, "E1932", {"start": v(50.28, 204.51) * mm, "end": v(50.38, 203.65) * mm});
            skLineSegment(sketch, "E1933", {"start": v(50.38, 203.65) * mm, "end": v(50.6, 202.89) * mm});
            skLineSegment(sketch, "E1934", {"start": v(50.6, 202.89) * mm, "end": v(51.04, 202.24) * mm});
            skLineSegment(sketch, "E1935", {"start": v(51.04, 202.24) * mm, "end": v(51.69, 201.6) * mm});
            skLineSegment(sketch, "E1936", {"start": v(51.69, 201.6) * mm, "end": v(52.33, 201.16) * mm});
            skLineSegment(sketch, "E1937", {"start": v(52.33, 201.16) * mm, "end": v(53.1, 200.94) * mm});
            skLineSegment(sketch, "E1938", {"start": v(53.1, 200.94) * mm, "end": v(53.96, 200.83) * mm});
            skLineSegment(sketch, "E1939", {"start": v(53.96, 200.83) * mm, "end": v(54.72, 200.94) * mm});
            skLineSegment(sketch, "E1940", {"start": v(54.72, 200.94) * mm, "end": v(55.47, 201.16) * mm});
            skLineSegment(sketch, "E1941", {"start": v(55.47, 201.16) * mm, "end": v(56.12, 201.6) * mm});
            skLineSegment(sketch, "E1942", {"start": v(56.12, 201.6) * mm, "end": v(56.77, 202.24) * mm});
            skLineSegment(sketch, "E1943", {"start": v(56.77, 202.24) * mm, "end": v(57.2, 202.89) * mm});
            skLineSegment(sketch, "E1944", {"start": v(57.2, 202.89) * mm, "end": v(57.42, 203.65) * mm});
            skLineSegment(sketch, "E1945", {"start": v(57.42, 203.65) * mm, "end": v(57.53, 204.51) * mm});
            skLineSegment(sketch, "E1946", {"start": v(50.28, 204.51) * mm, "end": v(50.28, 249.97) * mm});
            skLineSegment(sketch, "E1947", {"start": v(57.53, 249.97) * mm, "end": v(57.42, 250.84) * mm});
            skLineSegment(sketch, "E1948", {"start": v(57.42, 250.84) * mm, "end": v(57.2, 251.6) * mm});
            skLineSegment(sketch, "E1949", {"start": v(57.2, 251.6) * mm, "end": v(56.77, 252.25) * mm});
            skLineSegment(sketch, "E1950", {"start": v(56.77, 252.25) * mm, "end": v(56.12, 252.78) * mm});
            skLineSegment(sketch, "E1951", {"start": v(56.12, 252.78) * mm, "end": v(55.47, 253.22) * mm});
            skLineSegment(sketch, "E1952", {"start": v(55.47, 253.22) * mm, "end": v(54.72, 253.54) * mm});
            skLineSegment(sketch, "E1953", {"start": v(54.72, 253.54) * mm, "end": v(53.96, 253.65) * mm});
            skLineSegment(sketch, "E1954", {"start": v(53.96, 253.65) * mm, "end": v(53.1, 253.54) * mm});
            skLineSegment(sketch, "E1955", {"start": v(53.1, 253.54) * mm, "end": v(52.33, 253.22) * mm});
            skLineSegment(sketch, "E1956", {"start": v(52.33, 253.22) * mm, "end": v(51.69, 252.78) * mm});
            skLineSegment(sketch, "E1957", {"start": v(51.69, 252.78) * mm, "end": v(51.04, 252.25) * mm});
            skLineSegment(sketch, "E1958", {"start": v(51.04, 252.25) * mm, "end": v(50.6, 251.6) * mm});
            skLineSegment(sketch, "E1959", {"start": v(50.6, 251.6) * mm, "end": v(50.38, 250.84) * mm});
            skLineSegment(sketch, "E1960", {"start": v(50.38, 250.84) * mm, "end": v(50.28, 249.97) * mm});
            skLineSegment(sketch, "E1961", {"start": v(18.35, 233.41) * mm, "end": v(19.21, 235.14) * mm});
            skLineSegment(sketch, "E1962", {"start": v(19.21, 235.14) * mm, "end": v(19.86, 236.87) * mm});
            skLineSegment(sketch, "E1963", {"start": v(19.86, 236.87) * mm, "end": v(20.18, 238.72) * mm});
            skLineSegment(sketch, "E1964", {"start": v(20.18, 238.72) * mm, "end": v(20.4, 240.66) * mm});
            skLineSegment(sketch, "E1965", {"start": v(20.4, 240.66) * mm, "end": v(20.4, 242.5) * mm});
            skLineSegment(sketch, "E1966", {"start": v(20.4, 242.5) * mm, "end": v(20.18, 244.45) * mm});
            skLineSegment(sketch, "E1967", {"start": v(20.18, 244.45) * mm, "end": v(19.86, 246.3) * mm});
            skLineSegment(sketch, "E1968", {"start": v(19.86, 246.3) * mm, "end": v(19.21, 248.13) * mm});
            skLineSegment(sketch, "E1969", {"start": v(19.21, 248.13) * mm, "end": v(18.35, 249.75) * mm});
            skLineSegment(sketch, "E1970", {"start": v(12.07, 230.81) * mm, "end": v(13.8, 231.14) * mm});
            skLineSegment(sketch, "E1971", {"start": v(13.8, 231.14) * mm, "end": v(15.42, 231.57) * mm});
            skLineSegment(sketch, "E1972", {"start": v(15.42, 231.57) * mm, "end": v(16.94, 232.44) * mm});
            skLineSegment(sketch, "E1973", {"start": v(16.94, 232.44) * mm, "end": v(18.35, 233.41) * mm});
            skLineSegment(sketch, "E1974", {"start": v(12.07, 230.81) * mm, "end": v(12.07, 252.36) * mm});
            skLineSegment(sketch, "E1975", {"start": v(18.35, 249.75) * mm, "end": v(16.94, 250.84) * mm});
            skLineSegment(sketch, "E1976", {"start": v(16.94, 250.84) * mm, "end": v(15.42, 251.6) * mm});
            skLineSegment(sketch, "E1977", {"start": v(15.42, 251.6) * mm, "end": v(13.8, 252.14) * mm});
            skLineSegment(sketch, "E1978", {"start": v(13.8, 252.14) * mm, "end": v(12.07, 252.36) * mm});
            skLineSegment(sketch, "E1979", {"start": v(12.07, 262.3) * mm, "end": v(2.76, 262.3) * mm});
            skLineSegment(sketch, "E1980", {"start": v(2.76, 262.3) * mm, "end": v(2.76, 192.18) * mm});
            skLineSegment(sketch, "E1981", {"start": v(2.76, 192.18) * mm, "end": v(12.07, 192.18) * mm});
            skLineSegment(sketch, "E1982", {"start": v(12.07, 192.18) * mm, "end": v(12.07, 222.8) * mm});
            skLineSegment(sketch, "E1983", {"start": v(12.07, 222.8) * mm, "end": v(12.83, 222.48) * mm});
            skLineSegment(sketch, "E1984", {"start": v(12.83, 222.48) * mm, "end": v(13.59, 222.37) * mm});
            skLineSegment(sketch, "E1985", {"start": v(13.59, 222.37) * mm, "end": v(14.34, 222.48) * mm});
            skLineSegment(sketch, "E1986", {"start": v(14.34, 222.48) * mm, "end": v(15, 222.8) * mm});
            skLineSegment(sketch, "E1987", {"start": v(15, 222.8) * mm, "end": v(20.4, 192.18) * mm});
            skLineSegment(sketch, "E1988", {"start": v(20.4, 192.18) * mm, "end": v(30.14, 192.18) * mm});
            skLineSegment(sketch, "E1989", {"start": v(30.14, 192.18) * mm, "end": v(24.4, 225.5) * mm});
            skLineSegment(sketch, "E1990", {"start": v(24.4, 225.5) * mm, "end": v(25.7, 227.35) * mm});
            skLineSegment(sketch, "E1991", {"start": v(25.7, 227.35) * mm, "end": v(26.9, 229.4) * mm});
            skLineSegment(sketch, "E1992", {"start": v(26.9, 229.4) * mm, "end": v(27.87, 231.46) * mm});
            skLineSegment(sketch, "E1993", {"start": v(27.87, 231.46) * mm, "end": v(28.63, 233.63) * mm});
            skLineSegment(sketch, "E1994", {"start": v(28.63, 233.63) * mm, "end": v(29.28, 235.9) * mm});
            skLineSegment(sketch, "E1995", {"start": v(29.28, 235.9) * mm, "end": v(29.6, 238.17) * mm});
            skLineSegment(sketch, "E1996", {"start": v(29.6, 238.17) * mm, "end": v(29.82, 240.45) * mm});
            skLineSegment(sketch, "E1997", {"start": v(29.82, 240.45) * mm, "end": v(29.82, 242.72) * mm});
            skLineSegment(sketch, "E1998", {"start": v(29.82, 242.72) * mm, "end": v(29.6, 245.1) * mm});
            skLineSegment(sketch, "E1999", {"start": v(29.6, 245.1) * mm, "end": v(29.28, 247.37) * mm});
            skLineSegment(sketch, "E2000", {"start": v(29.28, 247.37) * mm, "end": v(28.63, 249.54) * mm});
            skLineSegment(sketch, "E2001", {"start": v(28.63, 249.54) * mm, "end": v(27.87, 251.7) * mm});
            skLineSegment(sketch, "E2002", {"start": v(27.87, 251.7) * mm, "end": v(26.9, 253.87) * mm});
            skLineSegment(sketch, "E2003", {"start": v(26.9, 253.87) * mm, "end": v(25.7, 255.82) * mm});
            skLineSegment(sketch, "E2004", {"start": v(25.7, 255.82) * mm, "end": v(24.4, 257.77) * mm});
            skLineSegment(sketch, "E2005", {"start": v(24.4, 257.77) * mm, "end": v(22.9, 258.85) * mm});
            skLineSegment(sketch, "E2006", {"start": v(22.9, 258.85) * mm, "end": v(21.16, 259.82) * mm});
            skLineSegment(sketch, "E2007", {"start": v(21.16, 259.82) * mm, "end": v(19.54, 260.69) * mm});
            skLineSegment(sketch, "E2008", {"start": v(19.54, 260.69) * mm, "end": v(17.7, 261.34) * mm});
            skLineSegment(sketch, "E2009", {"start": v(17.7, 261.34) * mm, "end": v(15.86, 261.77) * mm});
            skLineSegment(sketch, "E2010", {"start": v(15.86, 261.77) * mm, "end": v(14.01, 262.1) * mm});
            skLineSegment(sketch, "E2011", {"start": v(14.01, 262.1) * mm, "end": v(12.07, 262.3) * mm});
            skLineSegment(sketch, "E2012", {"start": v(-50.5, 170.52) * mm, "end": v(-40.1, 170.52) * mm});
            skLineSegment(sketch, "E2013", {"start": v(-45.3, 155.16) * mm, "end": v(-41.94, 132.1) * mm});
            skLineSegment(sketch, "E2014", {"start": v(-41.94, 132.1) * mm, "end": v(-48.65, 132.1) * mm});
            skLineSegment(sketch, "E2015", {"start": v(-48.65, 132.1) * mm, "end": v(-45.3, 155.16) * mm});
            skLineSegment(sketch, "E2016", {"start": v(-40.1, 170.52) * mm, "end": v(-50.5, 170.52) * mm});
            skLineSegment(sketch, "E2017", {"start": v(-50.5, 170.52) * mm, "end": v(-59.15, 111.54) * mm});
            skLineSegment(sketch, "E2018", {"start": v(-59.15, 111.54) * mm, "end": v(-51.68, 111.54) * mm});
            skLineSegment(sketch, "E2019", {"start": v(-51.68, 111.54) * mm, "end": v(-49.95, 123.23) * mm});
            skLineSegment(sketch, "E2020", {"start": v(-49.95, 123.23) * mm, "end": v(-40.64, 123.23) * mm});
            skLineSegment(sketch, "E2021", {"start": v(-40.64, 123.23) * mm, "end": v(-38.91, 111.54) * mm});
            skLineSegment(sketch, "E2022", {"start": v(-38.91, 111.54) * mm, "end": v(-31.55, 111.54) * mm});
            skLineSegment(sketch, "E2023", {"start": v(-31.55, 111.54) * mm, "end": v(-40.1, 170.52) * mm});
            skLineSegment(sketch, "E2024", {"start": v(56.55, 170.52) * mm, "end": v(66.95, 170.52) * mm});
            skLineSegment(sketch, "E2025", {"start": v(61.75, 155.16) * mm, "end": v(65.1, 132.1) * mm});
            skLineSegment(sketch, "E2026", {"start": v(65.1, 132.1) * mm, "end": v(58.4, 132.1) * mm});
            skLineSegment(sketch, "E2027", {"start": v(58.4, 132.1) * mm, "end": v(61.75, 155.16) * mm});
            skLineSegment(sketch, "E2028", {"start": v(66.95, 170.52) * mm, "end": v(56.55, 170.52) * mm});
            skLineSegment(sketch, "E2029", {"start": v(56.55, 170.52) * mm, "end": v(48, 111.54) * mm});
            skLineSegment(sketch, "E2030", {"start": v(48, 111.54) * mm, "end": v(55.36, 111.54) * mm});
            skLineSegment(sketch, "E2031", {"start": v(55.36, 111.54) * mm, "end": v(57.1, 123.23) * mm});
            skLineSegment(sketch, "E2032", {"start": v(57.1, 123.23) * mm, "end": v(66.4, 123.23) * mm});
            skLineSegment(sketch, "E2033", {"start": v(66.4, 123.23) * mm, "end": v(68.13, 111.54) * mm});
            skLineSegment(sketch, "E2034", {"start": v(68.13, 111.54) * mm, "end": v(75.6, 111.54) * mm});
            skLineSegment(sketch, "E2035", {"start": v(75.6, 111.54) * mm, "end": v(66.95, 170.52) * mm});
            skLineSegment(sketch, "E2036", {"start": v(133.73, 170.52) * mm, "end": v(144.12, 170.52) * mm});
            skLineSegment(sketch, "E2037", {"start": v(138.92, 155.16) * mm, "end": v(142.28, 132.1) * mm});
            skLineSegment(sketch, "E2038", {"start": v(142.28, 132.1) * mm, "end": v(135.57, 132.1) * mm});
            skLineSegment(sketch, "E2039", {"start": v(135.57, 132.1) * mm, "end": v(138.92, 155.16) * mm});
            skLineSegment(sketch, "E2040", {"start": v(144.12, 170.52) * mm, "end": v(133.73, 170.52) * mm});
            skLineSegment(sketch, "E2041", {"start": v(133.73, 170.52) * mm, "end": v(125.18, 111.54) * mm});
            skLineSegment(sketch, "E2042", {"start": v(125.18, 111.54) * mm, "end": v(132.54, 111.54) * mm});
            skLineSegment(sketch, "E2043", {"start": v(132.54, 111.54) * mm, "end": v(134.27, 123.23) * mm});
            skLineSegment(sketch, "E2044", {"start": v(134.27, 123.23) * mm, "end": v(143.58, 123.23) * mm});
            skLineSegment(sketch, "E2045", {"start": v(143.58, 123.23) * mm, "end": v(145.3, 111.54) * mm});
            skLineSegment(sketch, "E2046", {"start": v(145.3, 111.54) * mm, "end": v(152.78, 111.54) * mm});
            skLineSegment(sketch, "E2047", {"start": v(152.78, 111.54) * mm, "end": v(144.12, 170.52) * mm});
            skLineSegment(sketch, "E2048", {"start": v(-248.03, 122.47) * mm, "end": v(-247.92, 121.06) * mm});
            skLineSegment(sketch, "E2049", {"start": v(-247.92, 121.06) * mm, "end": v(-247.6, 119.65) * mm});
            skLineSegment(sketch, "E2050", {"start": v(-247.6, 119.65) * mm, "end": v(-247.16, 118.25) * mm});
            skLineSegment(sketch, "E2051", {"start": v(-247.16, 118.25) * mm, "end": v(-246.5, 116.95) * mm});
            skLineSegment(sketch, "E2052", {"start": v(-246.5, 116.95) * mm, "end": v(-245.75, 115.76) * mm});
            skLineSegment(sketch, "E2053", {"start": v(-245.75, 115.76) * mm, "end": v(-244.78, 114.68) * mm});
            skLineSegment(sketch, "E2054", {"start": v(-244.78, 114.68) * mm, "end": v(-243.7, 113.8) * mm});
            skLineSegment(sketch, "E2055", {"start": v(-243.7, 113.8) * mm, "end": v(-242.5, 112.95) * mm});
            skLineSegment(sketch, "E2056", {"start": v(-242.5, 112.95) * mm, "end": v(-241.2, 112.3) * mm});
            skLineSegment(sketch, "E2057", {"start": v(-241.2, 112.3) * mm, "end": v(-239.9, 111.86) * mm});
            skLineSegment(sketch, "E2058", {"start": v(-239.9, 111.86) * mm, "end": v(-238.5, 111.54) * mm});
            skLineSegment(sketch, "E2059", {"start": v(-238.5, 111.54) * mm, "end": v(-235.58, 111.54) * mm});
            skLineSegment(sketch, "E2060", {"start": v(-235.58, 111.54) * mm, "end": v(-234.17, 111.86) * mm});
            skLineSegment(sketch, "E2061", {"start": v(-234.17, 111.86) * mm, "end": v(-232.87, 112.3) * mm});
            skLineSegment(sketch, "E2062", {"start": v(-232.87, 112.3) * mm, "end": v(-231.57, 112.95) * mm});
            skLineSegment(sketch, "E2063", {"start": v(-231.57, 112.95) * mm, "end": v(-230.38, 113.8) * mm});
            skLineSegment(sketch, "E2064", {"start": v(-230.38, 113.8) * mm, "end": v(-229.3, 114.68) * mm});
            skLineSegment(sketch, "E2065", {"start": v(-229.3, 114.68) * mm, "end": v(-228.33, 115.76) * mm});
            skLineSegment(sketch, "E2066", {"start": v(-228.33, 115.76) * mm, "end": v(-227.57, 116.95) * mm});
            skLineSegment(sketch, "E2067", {"start": v(-227.57, 116.95) * mm, "end": v(-226.92, 118.25) * mm});
            skLineSegment(sketch, "E2068", {"start": v(-226.92, 118.25) * mm, "end": v(-226.38, 119.65) * mm});
            skLineSegment(sketch, "E2069", {"start": v(-226.38, 119.65) * mm, "end": v(-226.16, 121.06) * mm});
            skLineSegment(sketch, "E2070", {"start": v(-226.16, 121.06) * mm, "end": v(-226.05, 122.47) * mm});
            skLineSegment(sketch, "E2071", {"start": v(-226.05, 122.47) * mm, "end": v(-226.05, 131.67) * mm});
            skLineSegment(sketch, "E2072", {"start": v(-226.05, 131.67) * mm, "end": v(-233.95, 131.67) * mm});
            skLineSegment(sketch, "E2073", {"start": v(-233.95, 131.67) * mm, "end": v(-233.95, 121.82) * mm});
            skLineSegment(sketch, "E2074", {"start": v(-240.12, 121.82) * mm, "end": v(-240.01, 121.06) * mm});
            skLineSegment(sketch, "E2075", {"start": v(-240.01, 121.06) * mm, "end": v(-239.69, 120.3) * mm});
            skLineSegment(sketch, "E2076", {"start": v(-239.69, 120.3) * mm, "end": v(-239.15, 119.65) * mm});
            skLineSegment(sketch, "E2077", {"start": v(-239.15, 119.65) * mm, "end": v(-238.5, 119.22) * mm});
            skLineSegment(sketch, "E2078", {"start": v(-238.5, 119.22) * mm, "end": v(-237.85, 118.9) * mm});
            skLineSegment(sketch, "E2079", {"start": v(-237.85, 118.9) * mm, "end": v(-236.98, 118.79) * mm});
            skLineSegment(sketch, "E2080", {"start": v(-236.98, 118.79) * mm, "end": v(-236.23, 118.9) * mm});
            skLineSegment(sketch, "E2081", {"start": v(-236.23, 118.9) * mm, "end": v(-235.47, 119.22) * mm});
            skLineSegment(sketch, "E2082", {"start": v(-235.47, 119.22) * mm, "end": v(-234.82, 119.65) * mm});
            skLineSegment(sketch, "E2083", {"start": v(-234.82, 119.65) * mm, "end": v(-234.39, 120.3) * mm});
            skLineSegment(sketch, "E2084", {"start": v(-234.39, 120.3) * mm, "end": v(-234.06, 121.06) * mm});
            skLineSegment(sketch, "E2085", {"start": v(-234.06, 121.06) * mm, "end": v(-233.95, 121.82) * mm});
            skLineSegment(sketch, "E2086", {"start": v(-240.12, 121.82) * mm, "end": v(-240.12, 160.14) * mm});
            skLineSegment(sketch, "E2087", {"start": v(-233.95, 160.14) * mm, "end": v(-234.06, 161) * mm});
            skLineSegment(sketch, "E2088", {"start": v(-234.06, 161) * mm, "end": v(-234.39, 161.65) * mm});
            skLineSegment(sketch, "E2089", {"start": v(-234.39, 161.65) * mm, "end": v(-234.82, 162.3) * mm});
            skLineSegment(sketch, "E2090", {"start": v(-234.82, 162.3) * mm, "end": v(-235.47, 162.84) * mm});
            skLineSegment(sketch, "E2091", {"start": v(-235.47, 162.84) * mm, "end": v(-236.23, 163.17) * mm});
            skLineSegment(sketch, "E2092", {"start": v(-236.23, 163.17) * mm, "end": v(-237.85, 163.17) * mm});
            skLineSegment(sketch, "E2093", {"start": v(-237.85, 163.17) * mm, "end": v(-238.5, 162.84) * mm});
            skLineSegment(sketch, "E2094", {"start": v(-238.5, 162.84) * mm, "end": v(-239.15, 162.3) * mm});
            skLineSegment(sketch, "E2095", {"start": v(-239.15, 162.3) * mm, "end": v(-239.69, 161.65) * mm});
            skLineSegment(sketch, "E2096", {"start": v(-239.69, 161.65) * mm, "end": v(-240.01, 161) * mm});
            skLineSegment(sketch, "E2097", {"start": v(-240.01, 161) * mm, "end": v(-240.12, 160.14) * mm});
            skLineSegment(sketch, "E2098", {"start": v(-233.95, 160.14) * mm, "end": v(-233.95, 150.29) * mm});
            skLineSegment(sketch, "E2099", {"start": v(-233.95, 150.29) * mm, "end": v(-226.05, 150.29) * mm});
            skLineSegment(sketch, "E2100", {"start": v(-226.05, 150.29) * mm, "end": v(-226.05, 159.6) * mm});
            skLineSegment(sketch, "E2101", {"start": v(-226.05, 159.6) * mm, "end": v(-226.16, 161) * mm});
            skLineSegment(sketch, "E2102", {"start": v(-226.16, 161) * mm, "end": v(-226.38, 162.4) * mm});
            skLineSegment(sketch, "E2103", {"start": v(-226.38, 162.4) * mm, "end": v(-226.92, 163.7) * mm});
            skLineSegment(sketch, "E2104", {"start": v(-226.92, 163.7) * mm, "end": v(-227.57, 165) * mm});
            skLineSegment(sketch, "E2105", {"start": v(-227.57, 165) * mm, "end": v(-228.33, 166.2) * mm});
            skLineSegment(sketch, "E2106", {"start": v(-228.33, 166.2) * mm, "end": v(-229.3, 167.28) * mm});
            skLineSegment(sketch, "E2107", {"start": v(-229.3, 167.28) * mm, "end": v(-230.38, 168.25) * mm});
            skLineSegment(sketch, "E2108", {"start": v(-230.38, 168.25) * mm, "end": v(-231.57, 169.01) * mm});
            skLineSegment(sketch, "E2109", {"start": v(-231.57, 169.01) * mm, "end": v(-232.87, 169.66) * mm});
            skLineSegment(sketch, "E2110", {"start": v(-232.87, 169.66) * mm, "end": v(-234.17, 170.2) * mm});
            skLineSegment(sketch, "E2111", {"start": v(-234.17, 170.2) * mm, "end": v(-235.58, 170.42) * mm});
            skLineSegment(sketch, "E2112", {"start": v(-235.58, 170.42) * mm, "end": v(-236.98, 170.52) * mm});
            skLineSegment(sketch, "E2113", {"start": v(-236.98, 170.52) * mm, "end": v(-238.5, 170.42) * mm});
            skLineSegment(sketch, "E2114", {"start": v(-238.5, 170.42) * mm, "end": v(-239.9, 170.2) * mm});
            skLineSegment(sketch, "E2115", {"start": v(-239.9, 170.2) * mm, "end": v(-241.2, 169.66) * mm});
            skLineSegment(sketch, "E2116", {"start": v(-241.2, 169.66) * mm, "end": v(-242.5, 169.01) * mm});
            skLineSegment(sketch, "E2117", {"start": v(-242.5, 169.01) * mm, "end": v(-243.7, 168.25) * mm});
            skLineSegment(sketch, "E2118", {"start": v(-243.7, 168.25) * mm, "end": v(-244.78, 167.28) * mm});
            skLineSegment(sketch, "E2119", {"start": v(-244.78, 167.28) * mm, "end": v(-245.75, 166.2) * mm});
            skLineSegment(sketch, "E2120", {"start": v(-245.75, 166.2) * mm, "end": v(-246.5, 165) * mm});
            skLineSegment(sketch, "E2121", {"start": v(-246.5, 165) * mm, "end": v(-247.16, 163.7) * mm});
            skLineSegment(sketch, "E2122", {"start": v(-247.16, 163.7) * mm, "end": v(-247.6, 162.4) * mm});
            skLineSegment(sketch, "E2123", {"start": v(-247.6, 162.4) * mm, "end": v(-247.92, 161) * mm});
            skLineSegment(sketch, "E2124", {"start": v(-247.92, 161) * mm, "end": v(-248.03, 159.6) * mm});
            skLineSegment(sketch, "E2125", {"start": v(-248.03, 159.6) * mm, "end": v(-248.03, 122.47) * mm});
            skLineSegment(sketch, "E2126", {"start": v(-149.64, 122.47) * mm, "end": v(-149.53, 121.06) * mm});
            skLineSegment(sketch, "E2127", {"start": v(-149.53, 121.06) * mm, "end": v(-149.2, 119.65) * mm});
            skLineSegment(sketch, "E2128", {"start": v(-149.2, 119.65) * mm, "end": v(-148.77, 118.25) * mm});
            skLineSegment(sketch, "E2129", {"start": v(-148.77, 118.25) * mm, "end": v(-148.12, 116.95) * mm});
            skLineSegment(sketch, "E2130", {"start": v(-148.12, 116.95) * mm, "end": v(-147.36, 115.76) * mm});
            skLineSegment(sketch, "E2131", {"start": v(-147.36, 115.76) * mm, "end": v(-146.39, 114.68) * mm});
            skLineSegment(sketch, "E2132", {"start": v(-146.39, 114.68) * mm, "end": v(-145.3, 113.8) * mm});
            skLineSegment(sketch, "E2133", {"start": v(-145.3, 113.8) * mm, "end": v(-144.12, 112.95) * mm});
            skLineSegment(sketch, "E2134", {"start": v(-144.12, 112.95) * mm, "end": v(-142.82, 112.3) * mm});
            skLineSegment(sketch, "E2135", {"start": v(-142.82, 112.3) * mm, "end": v(-141.41, 111.86) * mm});
            skLineSegment(sketch, "E2136", {"start": v(-141.41, 111.86) * mm, "end": v(-140, 111.54) * mm});
            skLineSegment(sketch, "E2137", {"start": v(-140, 111.54) * mm, "end": v(-137.19, 111.54) * mm});
            skLineSegment(sketch, "E2138", {"start": v(-137.19, 111.54) * mm, "end": v(-135.78, 111.86) * mm});
            skLineSegment(sketch, "E2139", {"start": v(-135.78, 111.86) * mm, "end": v(-134.37, 112.3) * mm});
            skLineSegment(sketch, "E2140", {"start": v(-134.37, 112.3) * mm, "end": v(-133.08, 112.95) * mm});
            skLineSegment(sketch, "E2141", {"start": v(-133.08, 112.95) * mm, "end": v(-131.89, 113.8) * mm});
            skLineSegment(sketch, "E2142", {"start": v(-131.89, 113.8) * mm, "end": v(-130.8, 114.68) * mm});
            skLineSegment(sketch, "E2143", {"start": v(-130.8, 114.68) * mm, "end": v(-129.94, 115.76) * mm});
            skLineSegment(sketch, "E2144", {"start": v(-129.94, 115.76) * mm, "end": v(-129.07, 116.95) * mm});
            skLineSegment(sketch, "E2145", {"start": v(-129.07, 116.95) * mm, "end": v(-128.42, 118.25) * mm});
            skLineSegment(sketch, "E2146", {"start": v(-128.42, 118.25) * mm, "end": v(-127.99, 119.65) * mm});
            skLineSegment(sketch, "E2147", {"start": v(-127.99, 119.65) * mm, "end": v(-127.77, 121.06) * mm});
            skLineSegment(sketch, "E2148", {"start": v(-127.77, 121.06) * mm, "end": v(-127.66, 122.47) * mm});
            skLineSegment(sketch, "E2149", {"start": v(-127.66, 122.47) * mm, "end": v(-127.66, 131.67) * mm});
            skLineSegment(sketch, "E2150", {"start": v(-127.66, 131.67) * mm, "end": v(-135.57, 131.67) * mm});
            skLineSegment(sketch, "E2151", {"start": v(-135.57, 131.67) * mm, "end": v(-135.57, 121.82) * mm});
            skLineSegment(sketch, "E2152", {"start": v(-141.63, 121.82) * mm, "end": v(-141.52, 121.06) * mm});
            skLineSegment(sketch, "E2153", {"start": v(-141.52, 121.06) * mm, "end": v(-141.3, 120.3) * mm});
            skLineSegment(sketch, "E2154", {"start": v(-141.3, 120.3) * mm, "end": v(-140.76, 119.65) * mm});
            skLineSegment(sketch, "E2155", {"start": v(-140.76, 119.65) * mm, "end": v(-140.11, 119.22) * mm});
            skLineSegment(sketch, "E2156", {"start": v(-140.11, 119.22) * mm, "end": v(-139.36, 118.9) * mm});
            skLineSegment(sketch, "E2157", {"start": v(-139.36, 118.9) * mm, "end": v(-138.6, 118.79) * mm});
            skLineSegment(sketch, "E2158", {"start": v(-138.6, 118.79) * mm, "end": v(-137.84, 118.9) * mm});
            skLineSegment(sketch, "E2159", {"start": v(-137.84, 118.9) * mm, "end": v(-137.08, 119.22) * mm});
            skLineSegment(sketch, "E2160", {"start": v(-137.08, 119.22) * mm, "end": v(-136.43, 119.65) * mm});
            skLineSegment(sketch, "E2161", {"start": v(-136.43, 119.65) * mm, "end": v(-136, 120.3) * mm});
            skLineSegment(sketch, "E2162", {"start": v(-136, 120.3) * mm, "end": v(-135.68, 121.06) * mm});
            skLineSegment(sketch, "E2163", {"start": v(-135.68, 121.06) * mm, "end": v(-135.57, 121.82) * mm});
            skLineSegment(sketch, "E2164", {"start": v(-141.63, 121.82) * mm, "end": v(-141.63, 160.14) * mm});
            skLineSegment(sketch, "E2165", {"start": v(-135.57, 160.14) * mm, "end": v(-135.68, 161) * mm});
            skLineSegment(sketch, "E2166", {"start": v(-135.68, 161) * mm, "end": v(-136, 161.65) * mm});
            skLineSegment(sketch, "E2167", {"start": v(-136, 161.65) * mm, "end": v(-136.43, 162.3) * mm});
            skLineSegment(sketch, "E2168", {"start": v(-136.43, 162.3) * mm, "end": v(-137.08, 162.84) * mm});
            skLineSegment(sketch, "E2169", {"start": v(-137.08, 162.84) * mm, "end": v(-137.84, 163.17) * mm});
            skLineSegment(sketch, "E2170", {"start": v(-137.84, 163.17) * mm, "end": v(-139.36, 163.17) * mm});
            skLineSegment(sketch, "E2171", {"start": v(-139.36, 163.17) * mm, "end": v(-140.11, 162.84) * mm});
            skLineSegment(sketch, "E2172", {"start": v(-140.11, 162.84) * mm, "end": v(-140.76, 162.3) * mm});
            skLineSegment(sketch, "E2173", {"start": v(-140.76, 162.3) * mm, "end": v(-141.3, 161.65) * mm});
            skLineSegment(sketch, "E2174", {"start": v(-141.3, 161.65) * mm, "end": v(-141.52, 161) * mm});
            skLineSegment(sketch, "E2175", {"start": v(-141.52, 161) * mm, "end": v(-141.63, 160.14) * mm});
            skLineSegment(sketch, "E2176", {"start": v(-135.57, 160.14) * mm, "end": v(-135.57, 150.29) * mm});
            skLineSegment(sketch, "E2177", {"start": v(-135.57, 150.29) * mm, "end": v(-127.66, 150.29) * mm});
            skLineSegment(sketch, "E2178", {"start": v(-127.66, 150.29) * mm, "end": v(-127.66, 159.6) * mm});
            skLineSegment(sketch, "E2179", {"start": v(-127.66, 159.6) * mm, "end": v(-127.77, 161) * mm});
            skLineSegment(sketch, "E2180", {"start": v(-127.77, 161) * mm, "end": v(-127.99, 162.4) * mm});
            skLineSegment(sketch, "E2181", {"start": v(-127.99, 162.4) * mm, "end": v(-128.42, 163.7) * mm});
            skLineSegment(sketch, "E2182", {"start": v(-128.42, 163.7) * mm, "end": v(-129.07, 165) * mm});
            skLineSegment(sketch, "E2183", {"start": v(-129.07, 165) * mm, "end": v(-129.94, 166.2) * mm});
            skLineSegment(sketch, "E2184", {"start": v(-129.94, 166.2) * mm, "end": v(-130.8, 167.28) * mm});
            skLineSegment(sketch, "E2185", {"start": v(-130.8, 167.28) * mm, "end": v(-131.89, 168.25) * mm});
            skLineSegment(sketch, "E2186", {"start": v(-131.89, 168.25) * mm, "end": v(-133.08, 169.01) * mm});
            skLineSegment(sketch, "E2187", {"start": v(-133.08, 169.01) * mm, "end": v(-134.37, 169.66) * mm});
            skLineSegment(sketch, "E2188", {"start": v(-134.37, 169.66) * mm, "end": v(-135.78, 170.2) * mm});
            skLineSegment(sketch, "E2189", {"start": v(-135.78, 170.2) * mm, "end": v(-137.19, 170.42) * mm});
            skLineSegment(sketch, "E2190", {"start": v(-137.19, 170.42) * mm, "end": v(-138.6, 170.52) * mm});
            skLineSegment(sketch, "E2191", {"start": v(-138.6, 170.52) * mm, "end": v(-140, 170.42) * mm});
            skLineSegment(sketch, "E2192", {"start": v(-140, 170.42) * mm, "end": v(-141.41, 170.2) * mm});
            skLineSegment(sketch, "E2193", {"start": v(-141.41, 170.2) * mm, "end": v(-142.82, 169.66) * mm});
            skLineSegment(sketch, "E2194", {"start": v(-142.82, 169.66) * mm, "end": v(-144.12, 169.01) * mm});
            skLineSegment(sketch, "E2195", {"start": v(-144.12, 169.01) * mm, "end": v(-145.3, 168.25) * mm});
            skLineSegment(sketch, "E2196", {"start": v(-145.3, 168.25) * mm, "end": v(-146.39, 167.28) * mm});
            skLineSegment(sketch, "E2197", {"start": v(-146.39, 167.28) * mm, "end": v(-147.36, 166.2) * mm});
            skLineSegment(sketch, "E2198", {"start": v(-147.36, 166.2) * mm, "end": v(-148.12, 165) * mm});
            skLineSegment(sketch, "E2199", {"start": v(-148.12, 165) * mm, "end": v(-148.77, 163.7) * mm});
            skLineSegment(sketch, "E2200", {"start": v(-148.77, 163.7) * mm, "end": v(-149.2, 162.4) * mm});
            skLineSegment(sketch, "E2201", {"start": v(-149.2, 162.4) * mm, "end": v(-149.53, 161) * mm});
            skLineSegment(sketch, "E2202", {"start": v(-149.53, 161) * mm, "end": v(-149.64, 159.6) * mm});
            skLineSegment(sketch, "E2203", {"start": v(-149.64, 159.6) * mm, "end": v(-149.64, 122.47) * mm});
            skLineSegment(sketch, "E2204", {"start": v(-167.93, 160.14) * mm, "end": v(-167.93, 121.82) * mm});
            skLineSegment(sketch, "E2205", {"start": v(-174.1, 121.82) * mm, "end": v(-174, 121.06) * mm});
            skLineSegment(sketch, "E2206", {"start": v(-174, 121.06) * mm, "end": v(-173.67, 120.3) * mm});
            skLineSegment(sketch, "E2207", {"start": v(-173.67, 120.3) * mm, "end": v(-173.23, 119.65) * mm});
            skLineSegment(sketch, "E2208", {"start": v(-173.23, 119.65) * mm, "end": v(-172.58, 119.22) * mm});
            skLineSegment(sketch, "E2209", {"start": v(-172.58, 119.22) * mm, "end": v(-171.82, 118.9) * mm});
            skLineSegment(sketch, "E2210", {"start": v(-171.82, 118.9) * mm, "end": v(-171.07, 118.79) * mm});
            skLineSegment(sketch, "E2211", {"start": v(-171.07, 118.79) * mm, "end": v(-170.2, 118.9) * mm});
            skLineSegment(sketch, "E2212", {"start": v(-170.2, 118.9) * mm, "end": v(-169.55, 119.22) * mm});
            skLineSegment(sketch, "E2213", {"start": v(-169.55, 119.22) * mm, "end": v(-168.9, 119.65) * mm});
            skLineSegment(sketch, "E2214", {"start": v(-168.9, 119.65) * mm, "end": v(-168.36, 120.3) * mm});
            skLineSegment(sketch, "E2215", {"start": v(-168.36, 120.3) * mm, "end": v(-168.04, 121.06) * mm});
            skLineSegment(sketch, "E2216", {"start": v(-168.04, 121.06) * mm, "end": v(-167.93, 121.82) * mm});
            skLineSegment(sketch, "E2217", {"start": v(-174.1, 121.82) * mm, "end": v(-174.1, 160.14) * mm});
            skLineSegment(sketch, "E2218", {"start": v(-167.93, 160.14) * mm, "end": v(-168.04, 161) * mm});
            skLineSegment(sketch, "E2219", {"start": v(-168.04, 161) * mm, "end": v(-168.36, 161.65) * mm});
            skLineSegment(sketch, "E2220", {"start": v(-168.36, 161.65) * mm, "end": v(-168.9, 162.3) * mm});
            skLineSegment(sketch, "E2221", {"start": v(-168.9, 162.3) * mm, "end": v(-169.55, 162.84) * mm});
            skLineSegment(sketch, "E2222", {"start": v(-169.55, 162.84) * mm, "end": v(-170.2, 163.17) * mm});
            skLineSegment(sketch, "E2223", {"start": v(-170.2, 163.17) * mm, "end": v(-171.82, 163.17) * mm});
            skLineSegment(sketch, "E2224", {"start": v(-171.82, 163.17) * mm, "end": v(-172.58, 162.84) * mm});
            skLineSegment(sketch, "E2225", {"start": v(-172.58, 162.84) * mm, "end": v(-173.23, 162.3) * mm});
            skLineSegment(sketch, "E2226", {"start": v(-173.23, 162.3) * mm, "end": v(-173.67, 161.65) * mm});
            skLineSegment(sketch, "E2227", {"start": v(-173.67, 161.65) * mm, "end": v(-174, 161) * mm});
            skLineSegment(sketch, "E2228", {"start": v(-174, 161) * mm, "end": v(-174.1, 160.14) * mm});
            skLineSegment(sketch, "E2229", {"start": v(-182, 159.6) * mm, "end": v(-182, 122.47) * mm});
            skLineSegment(sketch, "E2230", {"start": v(-182, 122.47) * mm, "end": v(-181.9, 121.06) * mm});
            skLineSegment(sketch, "E2231", {"start": v(-181.9, 121.06) * mm, "end": v(-181.67, 119.65) * mm});
            skLineSegment(sketch, "E2232", {"start": v(-181.67, 119.65) * mm, "end": v(-181.13, 118.25) * mm});
            skLineSegment(sketch, "E2233", {"start": v(-181.13, 118.25) * mm, "end": v(-180.49, 116.95) * mm});
            skLineSegment(sketch, "E2234", {"start": v(-180.49, 116.95) * mm, "end": v(-179.73, 115.76) * mm});
            skLineSegment(sketch, "E2235", {"start": v(-179.73, 115.76) * mm, "end": v(-178.75, 114.68) * mm});
            skLineSegment(sketch, "E2236", {"start": v(-178.75, 114.68) * mm, "end": v(-177.67, 113.8) * mm});
            skLineSegment(sketch, "E2237", {"start": v(-177.67, 113.8) * mm, "end": v(-176.48, 112.95) * mm});
            skLineSegment(sketch, "E2238", {"start": v(-176.48, 112.95) * mm, "end": v(-175.18, 112.3) * mm});
            skLineSegment(sketch, "E2239", {"start": v(-175.18, 112.3) * mm, "end": v(-173.88, 111.86) * mm});
            skLineSegment(sketch, "E2240", {"start": v(-173.88, 111.86) * mm, "end": v(-172.47, 111.54) * mm});
            skLineSegment(sketch, "E2241", {"start": v(-172.47, 111.54) * mm, "end": v(-169.55, 111.54) * mm});
            skLineSegment(sketch, "E2242", {"start": v(-169.55, 111.54) * mm, "end": v(-168.14, 111.86) * mm});
            skLineSegment(sketch, "E2243", {"start": v(-168.14, 111.86) * mm, "end": v(-166.85, 112.3) * mm});
            skLineSegment(sketch, "E2244", {"start": v(-166.85, 112.3) * mm, "end": v(-165.55, 112.95) * mm});
            skLineSegment(sketch, "E2245", {"start": v(-165.55, 112.95) * mm, "end": v(-164.36, 113.8) * mm});
            skLineSegment(sketch, "E2246", {"start": v(-164.36, 113.8) * mm, "end": v(-163.27, 114.68) * mm});
            skLineSegment(sketch, "E2247", {"start": v(-163.27, 114.68) * mm, "end": v(-162.3, 115.76) * mm});
            skLineSegment(sketch, "E2248", {"start": v(-162.3, 115.76) * mm, "end": v(-161.54, 116.95) * mm});
            skLineSegment(sketch, "E2249", {"start": v(-161.54, 116.95) * mm, "end": v(-160.9, 118.25) * mm});
            skLineSegment(sketch, "E2250", {"start": v(-160.9, 118.25) * mm, "end": v(-160.46, 119.65) * mm});
            skLineSegment(sketch, "E2251", {"start": v(-160.46, 119.65) * mm, "end": v(-160.14, 121.06) * mm});
            skLineSegment(sketch, "E2252", {"start": v(-160.14, 121.06) * mm, "end": v(-160.03, 122.47) * mm});
            skLineSegment(sketch, "E2253", {"start": v(-160.03, 122.47) * mm, "end": v(-160.03, 159.6) * mm});
            skLineSegment(sketch, "E2254", {"start": v(-160.03, 159.6) * mm, "end": v(-160.14, 161) * mm});
            skLineSegment(sketch, "E2255", {"start": v(-160.14, 161) * mm, "end": v(-160.46, 162.4) * mm});
            skLineSegment(sketch, "E2256", {"start": v(-160.46, 162.4) * mm, "end": v(-160.9, 163.7) * mm});
            skLineSegment(sketch, "E2257", {"start": v(-160.9, 163.7) * mm, "end": v(-161.54, 165) * mm});
            skLineSegment(sketch, "E2258", {"start": v(-161.54, 165) * mm, "end": v(-162.3, 166.2) * mm});
            skLineSegment(sketch, "E2259", {"start": v(-162.3, 166.2) * mm, "end": v(-163.27, 167.28) * mm});
            skLineSegment(sketch, "E2260", {"start": v(-163.27, 167.28) * mm, "end": v(-164.36, 168.25) * mm});
            skLineSegment(sketch, "E2261", {"start": v(-164.36, 168.25) * mm, "end": v(-165.55, 169.01) * mm});
            skLineSegment(sketch, "E2262", {"start": v(-165.55, 169.01) * mm, "end": v(-166.85, 169.66) * mm});
            skLineSegment(sketch, "E2263", {"start": v(-166.85, 169.66) * mm, "end": v(-168.14, 170.2) * mm});
            skLineSegment(sketch, "E2264", {"start": v(-168.14, 170.2) * mm, "end": v(-169.55, 170.42) * mm});
            skLineSegment(sketch, "E2265", {"start": v(-169.55, 170.42) * mm, "end": v(-171.07, 170.52) * mm});
            skLineSegment(sketch, "E2266", {"start": v(-171.07, 170.52) * mm, "end": v(-172.47, 170.42) * mm});
            skLineSegment(sketch, "E2267", {"start": v(-172.47, 170.42) * mm, "end": v(-173.88, 170.2) * mm});
            skLineSegment(sketch, "E2268", {"start": v(-173.88, 170.2) * mm, "end": v(-175.18, 169.66) * mm});
            skLineSegment(sketch, "E2269", {"start": v(-175.18, 169.66) * mm, "end": v(-176.48, 169.01) * mm});
            skLineSegment(sketch, "E2270", {"start": v(-176.48, 169.01) * mm, "end": v(-177.67, 168.25) * mm});
            skLineSegment(sketch, "E2271", {"start": v(-177.67, 168.25) * mm, "end": v(-178.75, 167.28) * mm});
            skLineSegment(sketch, "E2272", {"start": v(-178.75, 167.28) * mm, "end": v(-179.73, 166.2) * mm});
            skLineSegment(sketch, "E2273", {"start": v(-179.73, 166.2) * mm, "end": v(-180.49, 165) * mm});
            skLineSegment(sketch, "E2274", {"start": v(-180.49, 165) * mm, "end": v(-181.13, 163.7) * mm});
            skLineSegment(sketch, "E2275", {"start": v(-181.13, 163.7) * mm, "end": v(-181.67, 162.4) * mm});
            skLineSegment(sketch, "E2276", {"start": v(-181.67, 162.4) * mm, "end": v(-181.9, 161) * mm});
            skLineSegment(sketch, "E2277", {"start": v(-181.9, 161) * mm, "end": v(-182, 159.6) * mm});
            skLineSegment(sketch, "E2278", {"start": v(-103.85, 160.14) * mm, "end": v(-103.85, 121.82) * mm});
            skLineSegment(sketch, "E2279", {"start": v(-110.02, 121.82) * mm, "end": v(-109.91, 121.06) * mm});
            skLineSegment(sketch, "E2280", {"start": v(-109.91, 121.06) * mm, "end": v(-109.59, 120.3) * mm});
            skLineSegment(sketch, "E2281", {"start": v(-109.59, 120.3) * mm, "end": v(-109.05, 119.65) * mm});
            skLineSegment(sketch, "E2282", {"start": v(-109.05, 119.65) * mm, "end": v(-108.4, 119.22) * mm});
            skLineSegment(sketch, "E2283", {"start": v(-108.4, 119.22) * mm, "end": v(-107.75, 118.9) * mm});
            skLineSegment(sketch, "E2284", {"start": v(-107.75, 118.9) * mm, "end": v(-106.88, 118.79) * mm});
            skLineSegment(sketch, "E2285", {"start": v(-106.88, 118.79) * mm, "end": v(-106.13, 118.9) * mm});
            skLineSegment(sketch, "E2286", {"start": v(-106.13, 118.9) * mm, "end": v(-105.37, 119.22) * mm});
            skLineSegment(sketch, "E2287", {"start": v(-105.37, 119.22) * mm, "end": v(-104.72, 119.65) * mm});
            skLineSegment(sketch, "E2288", {"start": v(-104.72, 119.65) * mm, "end": v(-104.29, 120.3) * mm});
            skLineSegment(sketch, "E2289", {"start": v(-104.29, 120.3) * mm, "end": v(-103.96, 121.06) * mm});
            skLineSegment(sketch, "E2290", {"start": v(-103.96, 121.06) * mm, "end": v(-103.85, 121.82) * mm});
            skLineSegment(sketch, "E2291", {"start": v(-110.02, 121.82) * mm, "end": v(-110.02, 160.14) * mm});
            skLineSegment(sketch, "E2292", {"start": v(-103.85, 160.14) * mm, "end": v(-103.96, 161) * mm});
            skLineSegment(sketch, "E2293", {"start": v(-103.96, 161) * mm, "end": v(-104.29, 161.65) * mm});
            skLineSegment(sketch, "E2294", {"start": v(-104.29, 161.65) * mm, "end": v(-104.72, 162.3) * mm});
            skLineSegment(sketch, "E2295", {"start": v(-104.72, 162.3) * mm, "end": v(-105.37, 162.84) * mm});
            skLineSegment(sketch, "E2296", {"start": v(-105.37, 162.84) * mm, "end": v(-106.13, 163.17) * mm});
            skLineSegment(sketch, "E2297", {"start": v(-106.13, 163.17) * mm, "end": v(-107.75, 163.17) * mm});
            skLineSegment(sketch, "E2298", {"start": v(-107.75, 163.17) * mm, "end": v(-108.4, 162.84) * mm});
            skLineSegment(sketch, "E2299", {"start": v(-108.4, 162.84) * mm, "end": v(-109.05, 162.3) * mm});
            skLineSegment(sketch, "E2300", {"start": v(-109.05, 162.3) * mm, "end": v(-109.59, 161.65) * mm});
            skLineSegment(sketch, "E2301", {"start": v(-109.59, 161.65) * mm, "end": v(-109.91, 161) * mm});
            skLineSegment(sketch, "E2302", {"start": v(-109.91, 161) * mm, "end": v(-110.02, 160.14) * mm});
            skLineSegment(sketch, "E2303", {"start": v(-117.92, 159.6) * mm, "end": v(-117.92, 122.47) * mm});
            skLineSegment(sketch, "E2304", {"start": v(-117.92, 122.47) * mm, "end": v(-117.82, 121.06) * mm});
            skLineSegment(sketch, "E2305", {"start": v(-117.82, 121.06) * mm, "end": v(-117.5, 119.65) * mm});
            skLineSegment(sketch, "E2306", {"start": v(-117.5, 119.65) * mm, "end": v(-117.06, 118.25) * mm});
            skLineSegment(sketch, "E2307", {"start": v(-117.06, 118.25) * mm, "end": v(-116.4, 116.95) * mm});
            skLineSegment(sketch, "E2308", {"start": v(-116.4, 116.95) * mm, "end": v(-115.65, 115.76) * mm});
            skLineSegment(sketch, "E2309", {"start": v(-115.65, 115.76) * mm, "end": v(-114.68, 114.68) * mm});
            skLineSegment(sketch, "E2310", {"start": v(-114.68, 114.68) * mm, "end": v(-113.6, 113.8) * mm});
            skLineSegment(sketch, "E2311", {"start": v(-113.6, 113.8) * mm, "end": v(-112.4, 112.95) * mm});
            skLineSegment(sketch, "E2312", {"start": v(-112.4, 112.95) * mm, "end": v(-111.1, 112.3) * mm});
            skLineSegment(sketch, "E2313", {"start": v(-111.1, 112.3) * mm, "end": v(-109.8, 111.86) * mm});
            skLineSegment(sketch, "E2314", {"start": v(-109.8, 111.86) * mm, "end": v(-108.4, 111.54) * mm});
            skLineSegment(sketch, "E2315", {"start": v(-108.4, 111.54) * mm, "end": v(-105.48, 111.54) * mm});
            skLineSegment(sketch, "E2316", {"start": v(-105.48, 111.54) * mm, "end": v(-104.07, 111.86) * mm});
            skLineSegment(sketch, "E2317", {"start": v(-104.07, 111.86) * mm, "end": v(-102.66, 112.3) * mm});
            skLineSegment(sketch, "E2318", {"start": v(-102.66, 112.3) * mm, "end": v(-101.47, 112.95) * mm});
            skLineSegment(sketch, "E2319", {"start": v(-101.47, 112.95) * mm, "end": v(-100.28, 113.8) * mm});
            skLineSegment(sketch, "E2320", {"start": v(-100.28, 113.8) * mm, "end": v(-99.2, 114.68) * mm});
            skLineSegment(sketch, "E2321", {"start": v(-99.2, 114.68) * mm, "end": v(-98.23, 115.76) * mm});
            skLineSegment(sketch, "E2322", {"start": v(-98.23, 115.76) * mm, "end": v(-97.36, 116.95) * mm});
            skLineSegment(sketch, "E2323", {"start": v(-97.36, 116.95) * mm, "end": v(-96.82, 118.25) * mm});
            skLineSegment(sketch, "E2324", {"start": v(-96.82, 118.25) * mm, "end": v(-96.28, 119.65) * mm});
            skLineSegment(sketch, "E2325", {"start": v(-96.28, 119.65) * mm, "end": v(-96.06, 121.06) * mm});
            skLineSegment(sketch, "E2326", {"start": v(-96.06, 121.06) * mm, "end": v(-95.95, 122.47) * mm});
            skLineSegment(sketch, "E2327", {"start": v(-95.95, 122.47) * mm, "end": v(-95.95, 159.6) * mm});
            skLineSegment(sketch, "E2328", {"start": v(-95.95, 159.6) * mm, "end": v(-96.06, 161) * mm});
            skLineSegment(sketch, "E2329", {"start": v(-96.06, 161) * mm, "end": v(-96.28, 162.4) * mm});
            skLineSegment(sketch, "E2330", {"start": v(-96.28, 162.4) * mm, "end": v(-96.82, 163.7) * mm});
            skLineSegment(sketch, "E2331", {"start": v(-96.82, 163.7) * mm, "end": v(-97.36, 165) * mm});
            skLineSegment(sketch, "E2332", {"start": v(-97.36, 165) * mm, "end": v(-98.23, 166.2) * mm});
            skLineSegment(sketch, "E2333", {"start": v(-98.23, 166.2) * mm, "end": v(-99.2, 167.28) * mm});
            skLineSegment(sketch, "E2334", {"start": v(-99.2, 167.28) * mm, "end": v(-100.28, 168.25) * mm});
            skLineSegment(sketch, "E2335", {"start": v(-100.28, 168.25) * mm, "end": v(-101.47, 169.01) * mm});
            skLineSegment(sketch, "E2336", {"start": v(-101.47, 169.01) * mm, "end": v(-102.66, 169.66) * mm});
            skLineSegment(sketch, "E2337", {"start": v(-102.66, 169.66) * mm, "end": v(-104.07, 170.2) * mm});
            skLineSegment(sketch, "E2338", {"start": v(-104.07, 170.2) * mm, "end": v(-105.48, 170.42) * mm});
            skLineSegment(sketch, "E2339", {"start": v(-105.48, 170.42) * mm, "end": v(-106.88, 170.52) * mm});
            skLineSegment(sketch, "E2340", {"start": v(-106.88, 170.52) * mm, "end": v(-108.4, 170.42) * mm});
            skLineSegment(sketch, "E2341", {"start": v(-108.4, 170.42) * mm, "end": v(-109.8, 170.2) * mm});
            skLineSegment(sketch, "E2342", {"start": v(-109.8, 170.2) * mm, "end": v(-111.1, 169.66) * mm});
            skLineSegment(sketch, "E2343", {"start": v(-111.1, 169.66) * mm, "end": v(-112.4, 169.01) * mm});
            skLineSegment(sketch, "E2344", {"start": v(-112.4, 169.01) * mm, "end": v(-113.6, 168.25) * mm});
            skLineSegment(sketch, "E2345", {"start": v(-113.6, 168.25) * mm, "end": v(-114.68, 167.28) * mm});
            skLineSegment(sketch, "E2346", {"start": v(-114.68, 167.28) * mm, "end": v(-115.65, 166.2) * mm});
            skLineSegment(sketch, "E2347", {"start": v(-115.65, 166.2) * mm, "end": v(-116.4, 165) * mm});
            skLineSegment(sketch, "E2348", {"start": v(-116.4, 165) * mm, "end": v(-117.06, 163.7) * mm});
            skLineSegment(sketch, "E2349", {"start": v(-117.06, 163.7) * mm, "end": v(-117.5, 162.4) * mm});
            skLineSegment(sketch, "E2350", {"start": v(-117.5, 162.4) * mm, "end": v(-117.82, 161) * mm});
            skLineSegment(sketch, "E2351", {"start": v(-117.82, 161) * mm, "end": v(-117.92, 159.6) * mm});
            skLineSegment(sketch, "E2352", {"start": v(240.55, 160.14) * mm, "end": v(240.55, 121.82) * mm});
            skLineSegment(sketch, "E2353", {"start": v(234.5, 121.82) * mm, "end": v(234.6, 121.06) * mm});
            skLineSegment(sketch, "E2354", {"start": v(234.6, 121.06) * mm, "end": v(234.93, 120.3) * mm});
            skLineSegment(sketch, "E2355", {"start": v(234.93, 120.3) * mm, "end": v(235.36, 119.65) * mm});
            skLineSegment(sketch, "E2356", {"start": v(235.36, 119.65) * mm, "end": v(236.01, 119.22) * mm});
            skLineSegment(sketch, "E2357", {"start": v(236.01, 119.22) * mm, "end": v(236.77, 118.9) * mm});
            skLineSegment(sketch, "E2358", {"start": v(236.77, 118.9) * mm, "end": v(237.52, 118.79) * mm});
            skLineSegment(sketch, "E2359", {"start": v(237.52, 118.79) * mm, "end": v(238.4, 118.9) * mm});
            skLineSegment(sketch, "E2360", {"start": v(238.4, 118.9) * mm, "end": v(239.04, 119.22) * mm});
            skLineSegment(sketch, "E2361", {"start": v(239.04, 119.22) * mm, "end": v(239.7, 119.65) * mm});
            skLineSegment(sketch, "E2362", {"start": v(239.7, 119.65) * mm, "end": v(240.23, 120.3) * mm});
            skLineSegment(sketch, "E2363", {"start": v(240.23, 120.3) * mm, "end": v(240.55, 121.06) * mm});
            skLineSegment(sketch, "E2364", {"start": v(240.55, 121.06) * mm, "end": v(240.55, 121.82) * mm});
            skLineSegment(sketch, "E2365", {"start": v(234.5, 121.82) * mm, "end": v(234.5, 160.14) * mm});
            skLineSegment(sketch, "E2366", {"start": v(240.55, 160.14) * mm, "end": v(240.55, 161) * mm});
            skLineSegment(sketch, "E2367", {"start": v(240.55, 161) * mm, "end": v(240.23, 161.65) * mm});
            skLineSegment(sketch, "E2368", {"start": v(240.23, 161.65) * mm, "end": v(239.7, 162.3) * mm});
            skLineSegment(sketch, "E2369", {"start": v(239.7, 162.3) * mm, "end": v(239.04, 162.84) * mm});
            skLineSegment(sketch, "E2370", {"start": v(239.04, 162.84) * mm, "end": v(238.4, 163.17) * mm});
            skLineSegment(sketch, "E2371", {"start": v(238.4, 163.17) * mm, "end": v(236.77, 163.17) * mm});
            skLineSegment(sketch, "E2372", {"start": v(236.77, 163.17) * mm, "end": v(236.01, 162.84) * mm});
            skLineSegment(sketch, "E2373", {"start": v(236.01, 162.84) * mm, "end": v(235.36, 162.3) * mm});
            skLineSegment(sketch, "E2374", {"start": v(235.36, 162.3) * mm, "end": v(234.93, 161.65) * mm});
            skLineSegment(sketch, "E2375", {"start": v(234.93, 161.65) * mm, "end": v(234.6, 161) * mm});
            skLineSegment(sketch, "E2376", {"start": v(234.6, 161) * mm, "end": v(234.5, 160.14) * mm});
            skLineSegment(sketch, "E2377", {"start": v(226.6, 159.6) * mm, "end": v(226.6, 122.47) * mm});
            skLineSegment(sketch, "E2378", {"start": v(226.6, 122.47) * mm, "end": v(226.7, 121.06) * mm});
            skLineSegment(sketch, "E2379", {"start": v(226.7, 121.06) * mm, "end": v(226.92, 119.65) * mm});
            skLineSegment(sketch, "E2380", {"start": v(226.92, 119.65) * mm, "end": v(227.46, 118.25) * mm});
            skLineSegment(sketch, "E2381", {"start": v(227.46, 118.25) * mm, "end": v(228, 116.95) * mm});
            skLineSegment(sketch, "E2382", {"start": v(228, 116.95) * mm, "end": v(228.87, 115.76) * mm});
            skLineSegment(sketch, "E2383", {"start": v(228.87, 115.76) * mm, "end": v(229.84, 114.68) * mm});
            skLineSegment(sketch, "E2384", {"start": v(229.84, 114.68) * mm, "end": v(230.92, 113.8) * mm});
            skLineSegment(sketch, "E2385", {"start": v(230.92, 113.8) * mm, "end": v(232.12, 112.95) * mm});
            skLineSegment(sketch, "E2386", {"start": v(232.12, 112.95) * mm, "end": v(233.3, 112.3) * mm});
            skLineSegment(sketch, "E2387", {"start": v(233.3, 112.3) * mm, "end": v(234.71, 111.86) * mm});
            skLineSegment(sketch, "E2388", {"start": v(234.71, 111.86) * mm, "end": v(236.12, 111.54) * mm});
            skLineSegment(sketch, "E2389", {"start": v(236.12, 111.54) * mm, "end": v(239.04, 111.54) * mm});
            skLineSegment(sketch, "E2390", {"start": v(239.04, 111.54) * mm, "end": v(240.45, 111.86) * mm});
            skLineSegment(sketch, "E2391", {"start": v(240.45, 111.86) * mm, "end": v(241.75, 112.3) * mm});
            skLineSegment(sketch, "E2392", {"start": v(241.75, 112.3) * mm, "end": v(243.05, 112.95) * mm});
            skLineSegment(sketch, "E2393", {"start": v(243.05, 112.95) * mm, "end": v(244.24, 113.8) * mm});
            skLineSegment(sketch, "E2394", {"start": v(244.24, 113.8) * mm, "end": v(245.32, 114.68) * mm});
            skLineSegment(sketch, "E2395", {"start": v(245.32, 114.68) * mm, "end": v(246.3, 115.76) * mm});
            skLineSegment(sketch, "E2396", {"start": v(246.3, 115.76) * mm, "end": v(247.05, 116.95) * mm});
            skLineSegment(sketch, "E2397", {"start": v(247.05, 116.95) * mm, "end": v(247.7, 118.25) * mm});
            skLineSegment(sketch, "E2398", {"start": v(247.7, 118.25) * mm, "end": v(248.14, 119.65) * mm});
            skLineSegment(sketch, "E2399", {"start": v(248.14, 119.65) * mm, "end": v(248.46, 121.06) * mm});
            skLineSegment(sketch, "E2400", {"start": v(248.46, 121.06) * mm, "end": v(248.57, 122.47) * mm});
            skLineSegment(sketch, "E2401", {"start": v(248.57, 122.47) * mm, "end": v(248.57, 159.6) * mm});
            skLineSegment(sketch, "E2402", {"start": v(248.57, 159.6) * mm, "end": v(248.46, 161) * mm});
            skLineSegment(sketch, "E2403", {"start": v(248.46, 161) * mm, "end": v(248.14, 162.4) * mm});
            skLineSegment(sketch, "E2404", {"start": v(248.14, 162.4) * mm, "end": v(247.7, 163.7) * mm});
            skLineSegment(sketch, "E2405", {"start": v(247.7, 163.7) * mm, "end": v(247.05, 165) * mm});
            skLineSegment(sketch, "E2406", {"start": v(247.05, 165) * mm, "end": v(246.3, 166.2) * mm});
            skLineSegment(sketch, "E2407", {"start": v(246.3, 166.2) * mm, "end": v(245.32, 167.28) * mm});
            skLineSegment(sketch, "E2408", {"start": v(245.32, 167.28) * mm, "end": v(244.24, 168.25) * mm});
            skLineSegment(sketch, "E2409", {"start": v(244.24, 168.25) * mm, "end": v(243.05, 169.01) * mm});
            skLineSegment(sketch, "E2410", {"start": v(243.05, 169.01) * mm, "end": v(241.75, 169.66) * mm});
            skLineSegment(sketch, "E2411", {"start": v(241.75, 169.66) * mm, "end": v(240.45, 170.2) * mm});
            skLineSegment(sketch, "E2412", {"start": v(240.45, 170.2) * mm, "end": v(239.04, 170.42) * mm});
            skLineSegment(sketch, "E2413", {"start": v(239.04, 170.42) * mm, "end": v(237.52, 170.52) * mm});
            skLineSegment(sketch, "E2414", {"start": v(237.52, 170.52) * mm, "end": v(236.12, 170.42) * mm});
            skLineSegment(sketch, "E2415", {"start": v(236.12, 170.42) * mm, "end": v(234.71, 170.2) * mm});
            skLineSegment(sketch, "E2416", {"start": v(234.71, 170.2) * mm, "end": v(233.3, 169.66) * mm});
            skLineSegment(sketch, "E2417", {"start": v(233.3, 169.66) * mm, "end": v(232.12, 169.01) * mm});
            skLineSegment(sketch, "E2418", {"start": v(232.12, 169.01) * mm, "end": v(230.92, 168.25) * mm});
            skLineSegment(sketch, "E2419", {"start": v(230.92, 168.25) * mm, "end": v(229.84, 167.28) * mm});
            skLineSegment(sketch, "E2420", {"start": v(229.84, 167.28) * mm, "end": v(228.87, 166.2) * mm});
            skLineSegment(sketch, "E2421", {"start": v(228.87, 166.2) * mm, "end": v(228, 165) * mm});
            skLineSegment(sketch, "E2422", {"start": v(228, 165) * mm, "end": v(227.46, 163.7) * mm});
            skLineSegment(sketch, "E2423", {"start": v(227.46, 163.7) * mm, "end": v(226.92, 162.4) * mm});
            skLineSegment(sketch, "E2424", {"start": v(226.92, 162.4) * mm, "end": v(226.7, 161) * mm});
            skLineSegment(sketch, "E2425", {"start": v(226.7, 161) * mm, "end": v(226.6, 159.6) * mm});
            skLineSegment(sketch, "E2426", {"start": v(-192.93, 170.52) * mm, "end": v(-200.94, 170.52) * mm});
            skLineSegment(sketch, "E2427", {"start": v(-200.94, 170.52) * mm, "end": v(-200.94, 145.63) * mm});
            skLineSegment(sketch, "E2428", {"start": v(-200.94, 145.63) * mm, "end": v(-208.2, 145.63) * mm});
            skLineSegment(sketch, "E2429", {"start": v(-208.2, 145.63) * mm, "end": v(-208.2, 170.52) * mm});
            skLineSegment(sketch, "E2430", {"start": v(-208.2, 170.52) * mm, "end": v(-215.88, 170.52) * mm});
            skLineSegment(sketch, "E2431", {"start": v(-215.88, 170.52) * mm, "end": v(-215.88, 111.54) * mm});
            skLineSegment(sketch, "E2432", {"start": v(-215.88, 111.54) * mm, "end": v(-208.2, 111.54) * mm});
            skLineSegment(sketch, "E2433", {"start": v(-208.2, 111.54) * mm, "end": v(-208.2, 137.2) * mm});
            skLineSegment(sketch, "E2434", {"start": v(-208.2, 137.2) * mm, "end": v(-200.94, 137.2) * mm});
            skLineSegment(sketch, "E2435", {"start": v(-200.94, 137.2) * mm, "end": v(-200.94, 111.54) * mm});
            skLineSegment(sketch, "E2436", {"start": v(-200.94, 111.54) * mm, "end": v(-192.93, 111.54) * mm});
            skLineSegment(sketch, "E2437", {"start": v(-192.93, 111.54) * mm, "end": v(-192.93, 170.52) * mm});
            skLineSegment(sketch, "E2438", {"start": v(-77.23, 170.52) * mm, "end": v(-85.35, 170.52) * mm});
            skLineSegment(sketch, "E2439", {"start": v(-85.35, 170.52) * mm, "end": v(-85.35, 111.54) * mm});
            skLineSegment(sketch, "E2440", {"start": v(-85.35, 111.54) * mm, "end": v(-65.86, 111.54) * mm});
            skLineSegment(sketch, "E2441", {"start": v(-65.86, 111.54) * mm, "end": v(-65.86, 118.9) * mm});
            skLineSegment(sketch, "E2442", {"start": v(-65.86, 118.9) * mm, "end": v(-77.23, 118.9) * mm});
            skLineSegment(sketch, "E2443", {"start": v(-77.23, 118.9) * mm, "end": v(-77.23, 170.52) * mm});
            skLineSegment(sketch, "E2444", {"start": v(24.3, 170.52) * mm, "end": v(5.03, 170.52) * mm});
            skLineSegment(sketch, "E2445", {"start": v(5.03, 170.52) * mm, "end": v(5.03, 111.54) * mm});
            skLineSegment(sketch, "E2446", {"start": v(5.03, 111.54) * mm, "end": v(24.3, 111.54) * mm});
            skLineSegment(sketch, "E2447", {"start": v(24.3, 111.54) * mm, "end": v(24.3, 119.65) * mm});
            skLineSegment(sketch, "E2448", {"start": v(24.3, 119.65) * mm, "end": v(13.04, 119.65) * mm});
            skLineSegment(sketch, "E2449", {"start": v(13.04, 119.65) * mm, "end": v(13.04, 136.76) * mm});
            skLineSegment(sketch, "E2450", {"start": v(13.04, 136.76) * mm, "end": v(21.16, 136.76) * mm});
            skLineSegment(sketch, "E2451", {"start": v(21.16, 136.76) * mm, "end": v(21.16, 145.52) * mm});
            skLineSegment(sketch, "E2452", {"start": v(21.16, 145.52) * mm, "end": v(13.04, 145.52) * mm});
            skLineSegment(sketch, "E2453", {"start": v(13.04, 145.52) * mm, "end": v(13.04, 161) * mm});
            skLineSegment(sketch, "E2454", {"start": v(13.04, 161) * mm, "end": v(24.3, 161) * mm});
            skLineSegment(sketch, "E2455", {"start": v(24.3, 161) * mm, "end": v(24.3, 170.52) * mm});
            skLineSegment(sketch, "E2456", {"start": v(-3.08, 170.52) * mm, "end": v(-27.11, 170.52) * mm});
            skLineSegment(sketch, "E2457", {"start": v(-27.11, 170.52) * mm, "end": v(-27.11, 161) * mm});
            skLineSegment(sketch, "E2458", {"start": v(-27.11, 161) * mm, "end": v(-19.54, 161) * mm});
            skLineSegment(sketch, "E2459", {"start": v(-19.54, 161) * mm, "end": v(-19.54, 111.54) * mm});
            skLineSegment(sketch, "E2460", {"start": v(-19.54, 111.54) * mm, "end": v(-11.2, 111.54) * mm});
            skLineSegment(sketch, "E2461", {"start": v(-11.2, 111.54) * mm, "end": v(-11.2, 161) * mm});
            skLineSegment(sketch, "E2462", {"start": v(-11.2, 161) * mm, "end": v(-3.08, 161) * mm});
            skLineSegment(sketch, "E2463", {"start": v(-3.08, 161) * mm, "end": v(-3.08, 170.52) * mm});
            skLineSegment(sketch, "E2464", {"start": v(94.65, 170.52) * mm, "end": v(85.02, 170.52) * mm});
            skLineSegment(sketch, "E2465", {"start": v(85.02, 170.52) * mm, "end": v(85.02, 111.54) * mm});
            skLineSegment(sketch, "E2466", {"start": v(85.02, 111.54) * mm, "end": v(92.27, 111.54) * mm});
            skLineSegment(sketch, "E2467", {"start": v(92.27, 111.54) * mm, "end": v(92.27, 151.26) * mm});
            skLineSegment(sketch, "E2468", {"start": v(92.27, 151.26) * mm, "end": v(92.92, 151.26) * mm});
            skLineSegment(sketch, "E2469", {"start": v(92.92, 151.26) * mm, "end": v(98.88, 111.54) * mm});
            skLineSegment(sketch, "E2470", {"start": v(98.88, 111.54) * mm, "end": v(102.34, 111.54) * mm});
            skLineSegment(sketch, "E2471", {"start": v(102.34, 111.54) * mm, "end": v(108.18, 151.26) * mm});
            skLineSegment(sketch, "E2472", {"start": v(108.18, 151.26) * mm, "end": v(108.83, 151.26) * mm});
            skLineSegment(sketch, "E2473", {"start": v(108.83, 151.26) * mm, "end": v(108.83, 111.54) * mm});
            skLineSegment(sketch, "E2474", {"start": v(108.83, 111.54) * mm, "end": v(116.08, 111.54) * mm});
            skLineSegment(sketch, "E2475", {"start": v(116.08, 111.54) * mm, "end": v(116.08, 170.52) * mm});
            skLineSegment(sketch, "E2476", {"start": v(116.08, 170.52) * mm, "end": v(106.45, 170.52) * mm});
            skLineSegment(sketch, "E2477", {"start": v(106.45, 170.52) * mm, "end": v(101.15, 140.65) * mm});
            skLineSegment(sketch, "E2478", {"start": v(101.15, 140.65) * mm, "end": v(99.96, 140.65) * mm});
            skLineSegment(sketch, "E2479", {"start": v(99.96, 140.65) * mm, "end": v(94.65, 170.52) * mm});
            skLineSegment(sketch, "E2480", {"start": v(208.09, 160.14) * mm, "end": v(208.09, 150.29) * mm});
            skLineSegment(sketch, "E2481", {"start": v(208.09, 150.29) * mm, "end": v(215.99, 150.29) * mm});
            skLineSegment(sketch, "E2482", {"start": v(215.99, 150.29) * mm, "end": v(215.99, 159.6) * mm});
            skLineSegment(sketch, "E2483", {"start": v(215.99, 159.6) * mm, "end": v(215.88, 161) * mm});
            skLineSegment(sketch, "E2484", {"start": v(215.88, 161) * mm, "end": v(215.66, 162.4) * mm});
            skLineSegment(sketch, "E2485", {"start": v(215.66, 162.4) * mm, "end": v(215.12, 163.7) * mm});
            skLineSegment(sketch, "E2486", {"start": v(215.12, 163.7) * mm, "end": v(214.58, 165) * mm});
            skLineSegment(sketch, "E2487", {"start": v(214.58, 165) * mm, "end": v(213.71, 166.2) * mm});
            skLineSegment(sketch, "E2488", {"start": v(213.71, 166.2) * mm, "end": v(212.74, 167.28) * mm});
            skLineSegment(sketch, "E2489", {"start": v(212.74, 167.28) * mm, "end": v(211.77, 168.25) * mm});
            skLineSegment(sketch, "E2490", {"start": v(211.77, 168.25) * mm, "end": v(210.47, 169.01) * mm});
            skLineSegment(sketch, "E2491", {"start": v(210.47, 169.01) * mm, "end": v(209.28, 169.66) * mm});
            skLineSegment(sketch, "E2492", {"start": v(209.28, 169.66) * mm, "end": v(207.87, 170.2) * mm});
            skLineSegment(sketch, "E2493", {"start": v(207.87, 170.2) * mm, "end": v(206.46, 170.42) * mm});
            skLineSegment(sketch, "E2494", {"start": v(206.46, 170.42) * mm, "end": v(205.06, 170.52) * mm});
            skLineSegment(sketch, "E2495", {"start": v(205.06, 170.52) * mm, "end": v(203.54, 170.42) * mm});
            skLineSegment(sketch, "E2496", {"start": v(203.54, 170.42) * mm, "end": v(202.13, 170.2) * mm});
            skLineSegment(sketch, "E2497", {"start": v(202.13, 170.2) * mm, "end": v(200.83, 169.66) * mm});
            skLineSegment(sketch, "E2498", {"start": v(200.83, 169.66) * mm, "end": v(199.53, 169.01) * mm});
            skLineSegment(sketch, "E2499", {"start": v(199.53, 169.01) * mm, "end": v(198.35, 168.25) * mm});
            skLineSegment(sketch, "E2500", {"start": v(198.35, 168.25) * mm, "end": v(197.26, 167.28) * mm});
            skLineSegment(sketch, "E2501", {"start": v(197.26, 167.28) * mm, "end": v(196.29, 166.2) * mm});
            skLineSegment(sketch, "E2502", {"start": v(196.29, 166.2) * mm, "end": v(195.53, 165) * mm});
            skLineSegment(sketch, "E2503", {"start": v(195.53, 165) * mm, "end": v(194.88, 163.7) * mm});
            skLineSegment(sketch, "E2504", {"start": v(194.88, 163.7) * mm, "end": v(194.45, 162.4) * mm});
            skLineSegment(sketch, "E2505", {"start": v(194.45, 162.4) * mm, "end": v(194.12, 161) * mm});
            skLineSegment(sketch, "E2506", {"start": v(194.12, 161) * mm, "end": v(194.02, 159.6) * mm});
            skLineSegment(sketch, "E2507", {"start": v(194.02, 159.6) * mm, "end": v(194.02, 122.47) * mm});
            skLineSegment(sketch, "E2508", {"start": v(194.02, 122.47) * mm, "end": v(194.12, 121.06) * mm});
            skLineSegment(sketch, "E2509", {"start": v(194.12, 121.06) * mm, "end": v(194.45, 119.65) * mm});
            skLineSegment(sketch, "E2510", {"start": v(194.45, 119.65) * mm, "end": v(194.88, 118.25) * mm});
            skLineSegment(sketch, "E2511", {"start": v(194.88, 118.25) * mm, "end": v(195.53, 116.95) * mm});
            skLineSegment(sketch, "E2512", {"start": v(195.53, 116.95) * mm, "end": v(196.29, 115.76) * mm});
            skLineSegment(sketch, "E2513", {"start": v(196.29, 115.76) * mm, "end": v(197.26, 114.68) * mm});
            skLineSegment(sketch, "E2514", {"start": v(197.26, 114.68) * mm, "end": v(198.35, 113.8) * mm});
            skLineSegment(sketch, "E2515", {"start": v(198.35, 113.8) * mm, "end": v(199.53, 112.95) * mm});
            skLineSegment(sketch, "E2516", {"start": v(199.53, 112.95) * mm, "end": v(200.83, 112.3) * mm});
            skLineSegment(sketch, "E2517", {"start": v(200.83, 112.3) * mm, "end": v(202.13, 111.86) * mm});
            skLineSegment(sketch, "E2518", {"start": v(202.13, 111.86) * mm, "end": v(203.54, 111.54) * mm});
            skLineSegment(sketch, "E2519", {"start": v(203.54, 111.54) * mm, "end": v(205.06, 111.54) * mm});
            skLineSegment(sketch, "E2520", {"start": v(205.06, 111.54) * mm, "end": v(206.25, 111.76) * mm});
            skLineSegment(sketch, "E2521", {"start": v(206.25, 111.76) * mm, "end": v(207.33, 112.19) * mm});
            skLineSegment(sketch, "E2522", {"start": v(207.33, 112.19) * mm, "end": v(208.3, 112.84) * mm});
            skLineSegment(sketch, "E2523", {"start": v(208.3, 112.84) * mm, "end": v(209.17, 113.6) * mm});
            skLineSegment(sketch, "E2524", {"start": v(209.17, 113.6) * mm, "end": v(209.93, 114.57) * mm});
            skLineSegment(sketch, "E2525", {"start": v(209.93, 114.57) * mm, "end": v(211.33, 113.6) * mm});
            skLineSegment(sketch, "E2526", {"start": v(211.33, 113.6) * mm, "end": v(211.33, 111.54) * mm});
            skLineSegment(sketch, "E2527", {"start": v(211.33, 111.54) * mm, "end": v(215.99, 111.54) * mm});
            skLineSegment(sketch, "E2528", {"start": v(215.99, 111.54) * mm, "end": v(215.99, 140.54) * mm});
            skLineSegment(sketch, "E2529", {"start": v(215.99, 140.54) * mm, "end": v(204.84, 140.54) * mm});
            skLineSegment(sketch, "E2530", {"start": v(204.84, 140.54) * mm, "end": v(204.84, 133.62) * mm});
            skLineSegment(sketch, "E2531", {"start": v(204.84, 133.62) * mm, "end": v(208.09, 133.62) * mm});
            skLineSegment(sketch, "E2532", {"start": v(208.09, 133.62) * mm, "end": v(208.09, 121.82) * mm});
            skLineSegment(sketch, "E2533", {"start": v(202.03, 121.82) * mm, "end": v(202.03, 121.06) * mm});
            skLineSegment(sketch, "E2534", {"start": v(202.03, 121.06) * mm, "end": v(202.35, 120.3) * mm});
            skLineSegment(sketch, "E2535", {"start": v(202.35, 120.3) * mm, "end": v(202.9, 119.65) * mm});
            skLineSegment(sketch, "E2536", {"start": v(202.9, 119.65) * mm, "end": v(203.54, 119.22) * mm});
            skLineSegment(sketch, "E2537", {"start": v(203.54, 119.22) * mm, "end": v(204.19, 118.9) * mm});
            skLineSegment(sketch, "E2538", {"start": v(204.19, 118.9) * mm, "end": v(205.06, 118.79) * mm});
            skLineSegment(sketch, "E2539", {"start": v(205.06, 118.79) * mm, "end": v(205.81, 118.9) * mm});
            skLineSegment(sketch, "E2540", {"start": v(205.81, 118.9) * mm, "end": v(206.57, 119.22) * mm});
            skLineSegment(sketch, "E2541", {"start": v(206.57, 119.22) * mm, "end": v(207.22, 119.65) * mm});
            skLineSegment(sketch, "E2542", {"start": v(207.22, 119.65) * mm, "end": v(207.65, 120.3) * mm});
            skLineSegment(sketch, "E2543", {"start": v(207.65, 120.3) * mm, "end": v(207.98, 121.06) * mm});
            skLineSegment(sketch, "E2544", {"start": v(207.98, 121.06) * mm, "end": v(208.09, 121.82) * mm});
            skLineSegment(sketch, "E2545", {"start": v(202.03, 121.82) * mm, "end": v(202.03, 160.14) * mm});
            skLineSegment(sketch, "E2546", {"start": v(208.09, 160.14) * mm, "end": v(207.98, 161) * mm});
            skLineSegment(sketch, "E2547", {"start": v(207.98, 161) * mm, "end": v(207.65, 161.65) * mm});
            skLineSegment(sketch, "E2548", {"start": v(207.65, 161.65) * mm, "end": v(207.22, 162.3) * mm});
            skLineSegment(sketch, "E2549", {"start": v(207.22, 162.3) * mm, "end": v(206.57, 162.84) * mm});
            skLineSegment(sketch, "E2550", {"start": v(206.57, 162.84) * mm, "end": v(205.81, 163.17) * mm});
            skLineSegment(sketch, "E2551", {"start": v(205.81, 163.17) * mm, "end": v(204.19, 163.17) * mm});
            skLineSegment(sketch, "E2552", {"start": v(204.19, 163.17) * mm, "end": v(203.54, 162.84) * mm});
            skLineSegment(sketch, "E2553", {"start": v(203.54, 162.84) * mm, "end": v(202.9, 162.3) * mm});
            skLineSegment(sketch, "E2554", {"start": v(202.9, 162.3) * mm, "end": v(202.35, 161.65) * mm});
            skLineSegment(sketch, "E2555", {"start": v(202.35, 161.65) * mm, "end": v(202.03, 161) * mm});
            skLineSegment(sketch, "E2556", {"start": v(202.03, 161) * mm, "end": v(202.03, 160.14) * mm});
            skLineSegment(sketch, "E2557", {"start": v(175.07, 146.17) * mm, "end": v(175.83, 147.8) * mm});
            skLineSegment(sketch, "E2558", {"start": v(175.83, 147.8) * mm, "end": v(176.48, 149.53) * mm});
            skLineSegment(sketch, "E2559", {"start": v(176.48, 149.53) * mm, "end": v(176.8, 151.26) * mm});
            skLineSegment(sketch, "E2560", {"start": v(176.8, 151.26) * mm, "end": v(176.92, 153.1) * mm});
            skLineSegment(sketch, "E2561", {"start": v(176.92, 153.1) * mm, "end": v(176.8, 154.94) * mm});
            skLineSegment(sketch, "E2562", {"start": v(176.8, 154.94) * mm, "end": v(176.48, 156.67) * mm});
            skLineSegment(sketch, "E2563", {"start": v(176.48, 156.67) * mm, "end": v(175.83, 158.4) * mm});
            skLineSegment(sketch, "E2564", {"start": v(175.83, 158.4) * mm, "end": v(175.07, 160.03) * mm});
            skLineSegment(sketch, "E2565", {"start": v(169.88, 144) * mm, "end": v(171.29, 144.23) * mm});
            skLineSegment(sketch, "E2566", {"start": v(171.29, 144.23) * mm, "end": v(172.7, 144.66) * mm});
            skLineSegment(sketch, "E2567", {"start": v(172.7, 144.66) * mm, "end": v(173.88, 145.3) * mm});
            skLineSegment(sketch, "E2568", {"start": v(173.88, 145.3) * mm, "end": v(175.07, 146.17) * mm});
            skLineSegment(sketch, "E2569", {"start": v(169.88, 144) * mm, "end": v(169.88, 162.2) * mm});
            skLineSegment(sketch, "E2570", {"start": v(175.07, 160.03) * mm, "end": v(173.88, 160.9) * mm});
            skLineSegment(sketch, "E2571", {"start": v(173.88, 160.9) * mm, "end": v(172.7, 161.54) * mm});
            skLineSegment(sketch, "E2572", {"start": v(172.7, 161.54) * mm, "end": v(171.29, 161.98) * mm});
            skLineSegment(sketch, "E2573", {"start": v(171.29, 161.98) * mm, "end": v(169.88, 162.2) * mm});
            skLineSegment(sketch, "E2574", {"start": v(169.88, 170.52) * mm, "end": v(161.98, 170.52) * mm});
            skLineSegment(sketch, "E2575", {"start": v(161.98, 170.52) * mm, "end": v(161.98, 111.54) * mm});
            skLineSegment(sketch, "E2576", {"start": v(161.98, 111.54) * mm, "end": v(169.88, 111.54) * mm});
            skLineSegment(sketch, "E2577", {"start": v(169.88, 111.54) * mm, "end": v(169.88, 137.3) * mm});
            skLineSegment(sketch, "E2578", {"start": v(169.88, 137.3) * mm, "end": v(170.42, 136.97) * mm});
            skLineSegment(sketch, "E2579", {"start": v(170.42, 136.97) * mm, "end": v(171.72, 136.97) * mm});
            skLineSegment(sketch, "E2580", {"start": v(171.72, 136.97) * mm, "end": v(172.26, 137.3) * mm});
            skLineSegment(sketch, "E2581", {"start": v(172.26, 137.3) * mm, "end": v(176.8, 111.54) * mm});
            skLineSegment(sketch, "E2582", {"start": v(176.8, 111.54) * mm, "end": v(185.03, 111.54) * mm});
            skLineSegment(sketch, "E2583", {"start": v(185.03, 111.54) * mm, "end": v(180.16, 139.57) * mm});
            skLineSegment(sketch, "E2584", {"start": v(180.16, 139.57) * mm, "end": v(181.46, 141.41) * mm});
            skLineSegment(sketch, "E2585", {"start": v(181.46, 141.41) * mm, "end": v(182.54, 143.36) * mm});
            skLineSegment(sketch, "E2586", {"start": v(182.54, 143.36) * mm, "end": v(183.4, 145.41) * mm});
            skLineSegment(sketch, "E2587", {"start": v(183.4, 145.41) * mm, "end": v(184.06, 147.58) * mm});
            skLineSegment(sketch, "E2588", {"start": v(184.06, 147.58) * mm, "end": v(184.5, 149.74) * mm});
            skLineSegment(sketch, "E2589", {"start": v(184.5, 149.74) * mm, "end": v(184.82, 152.02) * mm});
            skLineSegment(sketch, "E2590", {"start": v(184.82, 152.02) * mm, "end": v(184.82, 154.18) * mm});
            skLineSegment(sketch, "E2591", {"start": v(184.82, 154.18) * mm, "end": v(184.5, 156.46) * mm});
            skLineSegment(sketch, "E2592", {"start": v(184.5, 156.46) * mm, "end": v(184.06, 158.62) * mm});
            skLineSegment(sketch, "E2593", {"start": v(184.06, 158.62) * mm, "end": v(183.4, 160.78) * mm});
            skLineSegment(sketch, "E2594", {"start": v(183.4, 160.78) * mm, "end": v(182.54, 162.84) * mm});
            skLineSegment(sketch, "E2595", {"start": v(182.54, 162.84) * mm, "end": v(181.46, 164.79) * mm});
            skLineSegment(sketch, "E2596", {"start": v(181.46, 164.79) * mm, "end": v(180.16, 166.63) * mm});
            skLineSegment(sketch, "E2597", {"start": v(180.16, 166.63) * mm, "end": v(178.64, 167.82) * mm});
            skLineSegment(sketch, "E2598", {"start": v(178.64, 167.82) * mm, "end": v(177.02, 168.69) * mm});
            skLineSegment(sketch, "E2599", {"start": v(177.02, 168.69) * mm, "end": v(175.3, 169.44) * mm});
            skLineSegment(sketch, "E2600", {"start": v(175.3, 169.44) * mm, "end": v(173.56, 169.99) * mm});
            skLineSegment(sketch, "E2601", {"start": v(173.56, 169.99) * mm, "end": v(171.72, 170.3) * mm});
            skLineSegment(sketch, "E2602", {"start": v(171.72, 170.3) * mm, "end": v(169.88, 170.52) * mm});
            skLineSegment(sketch, "E2603", {"start": v(89.68, 268.37) * mm, "end": v(94.87, 277.03) * mm});
            skLineSegment(sketch, "E2604", {"start": v(94.87, 277.03) * mm, "end": v(104.18, 277.03) * mm});
            skLineSegment(sketch, "E2605", {"start": v(104.18, 277.03) * mm, "end": v(97.03, 268.37) * mm});
            skLineSegment(sketch, "E2606", {"start": v(97.03, 268.37) * mm, "end": v(89.68, 268.37) * mm});
            skLineSegment(sketch, "E2607", {"start": v(223.02, 86) * mm, "end": v(195.2, 86) * mm});
            skLineSegment(sketch, "E2608", {"start": v(195.2, 86) * mm, "end": v(76.04, -238.18) * mm});
            skLineSegment(sketch, "E2609", {"start": v(76.04, -238.18) * mm, "end": v(106.02, -238.18) * mm});
            skLineSegment(sketch, "E2610", {"start": v(106.02, -238.18) * mm, "end": v(223.02, 86) * mm});
            skLineSegment(sketch, "E2611", {"start": v(-127.77, 86) * mm, "end": v(-247.8, 86) * mm});
            skLineSegment(sketch, "E2612", {"start": v(-247.8, 86) * mm, "end": v(-247.8, 38.26) * mm});
            skLineSegment(sketch, "E2613", {"start": v(-247.8, 38.26) * mm, "end": v(-175.83, 38.26) * mm});
            skLineSegment(sketch, "E2614", {"start": v(-175.83, 38.26) * mm, "end": v(-223.67, -238.18) * mm});
            skLineSegment(sketch, "E2615", {"start": v(-223.67, -238.18) * mm, "end": v(-175.18, -238.18) * mm});
            skLineSegment(sketch, "E2616", {"start": v(-175.18, -238.18) * mm, "end": v(-127.77, 36.1) * mm});
            skLineSegment(sketch, "E2617", {"start": v(-127.77, 36.1) * mm, "end": v(-127.77, 86) * mm});
            skLineSegment(sketch, "E2618", {"start": v(-22.57, 31.66) * mm, "end": v(-22.57, -182.65) * mm});
            skLineSegment(sketch, "E2619", {"start": v(-56.66, -182.65) * mm, "end": v(-56.55, -184.6) * mm});
            skLineSegment(sketch, "E2620", {"start": v(-56.55, -184.6) * mm, "end": v(-56.23, -186.44) * mm});
            skLineSegment(sketch, "E2621", {"start": v(-56.23, -186.44) * mm, "end": v(-55.69, -188.28) * mm});
            skLineSegment(sketch, "E2622", {"start": v(-55.69, -188.28) * mm, "end": v(-55.04, -190.12) * mm});
            skLineSegment(sketch, "E2623", {"start": v(-55.04, -190.12) * mm, "end": v(-54.06, -191.74) * mm});
            skLineSegment(sketch, "E2624", {"start": v(-54.06, -191.74) * mm, "end": v(-52.98, -193.26) * mm});
            skLineSegment(sketch, "E2625", {"start": v(-52.98, -193.26) * mm, "end": v(-51.68, -194.77) * mm});
            skLineSegment(sketch, "E2626", {"start": v(-51.68, -194.77) * mm, "end": v(-50.28, -195.96) * mm});
            skLineSegment(sketch, "E2627", {"start": v(-50.28, -195.96) * mm, "end": v(-48.65, -197.16) * mm});
            skLineSegment(sketch, "E2628", {"start": v(-48.65, -197.16) * mm, "end": v(-47.03, -198.02) * mm});
            skLineSegment(sketch, "E2629", {"start": v(-47.03, -198.02) * mm, "end": v(-45.3, -198.78) * mm});
            skLineSegment(sketch, "E2630", {"start": v(-45.3, -198.78) * mm, "end": v(-43.46, -199.32) * mm});
            skLineSegment(sketch, "E2631", {"start": v(-43.46, -199.32) * mm, "end": v(-41.5, -199.64) * mm});
            skLineSegment(sketch, "E2632", {"start": v(-41.5, -199.64) * mm, "end": v(-39.56, -199.75) * mm});
            skLineSegment(sketch, "E2633", {"start": v(-39.56, -199.75) * mm, "end": v(-37.72, -199.64) * mm});
            skLineSegment(sketch, "E2634", {"start": v(-37.72, -199.64) * mm, "end": v(-35.77, -199.32) * mm});
            skLineSegment(sketch, "E2635", {"start": v(-35.77, -199.32) * mm, "end": v(-33.93, -198.78) * mm});
            skLineSegment(sketch, "E2636", {"start": v(-33.93, -198.78) * mm, "end": v(-32.2, -198.02) * mm});
            skLineSegment(sketch, "E2637", {"start": v(-32.2, -198.02) * mm, "end": v(-30.57, -197.16) * mm});
            skLineSegment(sketch, "E2638", {"start": v(-30.57, -197.16) * mm, "end": v(-28.95, -195.96) * mm});
            skLineSegment(sketch, "E2639", {"start": v(-28.95, -195.96) * mm, "end": v(-27.54, -194.77) * mm});
            skLineSegment(sketch, "E2640", {"start": v(-27.54, -194.77) * mm, "end": v(-26.25, -193.26) * mm});
            skLineSegment(sketch, "E2641", {"start": v(-26.25, -193.26) * mm, "end": v(-25.16, -191.74) * mm});
            skLineSegment(sketch, "E2642", {"start": v(-25.16, -191.74) * mm, "end": v(-24.2, -190.12) * mm});
            skLineSegment(sketch, "E2643", {"start": v(-24.2, -190.12) * mm, "end": v(-23.54, -188.28) * mm});
            skLineSegment(sketch, "E2644", {"start": v(-23.54, -188.28) * mm, "end": v(-23, -186.44) * mm});
            skLineSegment(sketch, "E2645", {"start": v(-23, -186.44) * mm, "end": v(-22.67, -184.6) * mm});
            skLineSegment(sketch, "E2646", {"start": v(-22.67, -184.6) * mm, "end": v(-22.57, -182.65) * mm});
            skLineSegment(sketch, "E2647", {"start": v(-56.66, -182.65) * mm, "end": v(-56.66, 31.66) * mm});
            skLineSegment(sketch, "E2648", {"start": v(-22.57, 31.66) * mm, "end": v(-22.67, 33.5) * mm});
            skLineSegment(sketch, "E2649", {"start": v(-22.67, 33.5) * mm, "end": v(-23, 35.45) * mm});
            skLineSegment(sketch, "E2650", {"start": v(-23, 35.45) * mm, "end": v(-23.54, 37.28) * mm});
            skLineSegment(sketch, "E2651", {"start": v(-23.54, 37.28) * mm, "end": v(-24.2, 39.02) * mm});
            skLineSegment(sketch, "E2652", {"start": v(-24.2, 39.02) * mm, "end": v(-25.16, 40.75) * mm});
            skLineSegment(sketch, "E2653", {"start": v(-25.16, 40.75) * mm, "end": v(-26.25, 42.26) * mm});
            skLineSegment(sketch, "E2654", {"start": v(-26.25, 42.26) * mm, "end": v(-27.54, 43.67) * mm});
            skLineSegment(sketch, "E2655", {"start": v(-27.54, 43.67) * mm, "end": v(-28.95, 44.97) * mm});
            skLineSegment(sketch, "E2656", {"start": v(-28.95, 44.97) * mm, "end": v(-30.57, 46.05) * mm});
            skLineSegment(sketch, "E2657", {"start": v(-30.57, 46.05) * mm, "end": v(-32.2, 47.03) * mm});
            skLineSegment(sketch, "E2658", {"start": v(-32.2, 47.03) * mm, "end": v(-33.93, 47.79) * mm});
            skLineSegment(sketch, "E2659", {"start": v(-33.93, 47.79) * mm, "end": v(-35.77, 48.22) * mm});
            skLineSegment(sketch, "E2660", {"start": v(-35.77, 48.22) * mm, "end": v(-37.72, 48.55) * mm});
            skLineSegment(sketch, "E2661", {"start": v(-37.72, 48.55) * mm, "end": v(-39.56, 48.65) * mm});
            skLineSegment(sketch, "E2662", {"start": v(-39.56, 48.65) * mm, "end": v(-41.5, 48.55) * mm});
            skLineSegment(sketch, "E2663", {"start": v(-41.5, 48.55) * mm, "end": v(-43.46, 48.22) * mm});
            skLineSegment(sketch, "E2664", {"start": v(-43.46, 48.22) * mm, "end": v(-45.3, 47.79) * mm});
            skLineSegment(sketch, "E2665", {"start": v(-45.3, 47.79) * mm, "end": v(-47.03, 47.03) * mm});
            skLineSegment(sketch, "E2666", {"start": v(-47.03, 47.03) * mm, "end": v(-48.65, 46.05) * mm});
            skLineSegment(sketch, "E2667", {"start": v(-48.65, 46.05) * mm, "end": v(-50.28, 44.97) * mm});
            skLineSegment(sketch, "E2668", {"start": v(-50.28, 44.97) * mm, "end": v(-51.68, 43.67) * mm});
            skLineSegment(sketch, "E2669", {"start": v(-51.68, 43.67) * mm, "end": v(-52.98, 42.26) * mm});
            skLineSegment(sketch, "E2670", {"start": v(-52.98, 42.26) * mm, "end": v(-54.06, 40.75) * mm});
            skLineSegment(sketch, "E2671", {"start": v(-54.06, 40.75) * mm, "end": v(-55.04, 39.02) * mm});
            skLineSegment(sketch, "E2672", {"start": v(-55.04, 39.02) * mm, "end": v(-55.69, 37.28) * mm});
            skLineSegment(sketch, "E2673", {"start": v(-55.69, 37.28) * mm, "end": v(-56.23, 35.45) * mm});
            skLineSegment(sketch, "E2674", {"start": v(-56.23, 35.45) * mm, "end": v(-56.55, 33.5) * mm});
            skLineSegment(sketch, "E2675", {"start": v(-56.55, 33.5) * mm, "end": v(-56.66, 31.66) * mm});
            skLineSegment(sketch, "E2676", {"start": v(-101.04, 28.09) * mm, "end": v(-101.04, -179.19) * mm});
            skLineSegment(sketch, "E2677", {"start": v(-101.04, -179.19) * mm, "end": v(-100.93, -182.76) * mm});
            skLineSegment(sketch, "E2678", {"start": v(-100.93, -182.76) * mm, "end": v(-100.6, -186.33) * mm});
            skLineSegment(sketch, "E2679", {"start": v(-100.6, -186.33) * mm, "end": v(-100.07, -189.8) * mm});
            skLineSegment(sketch, "E2680", {"start": v(-100.07, -189.8) * mm, "end": v(-99.41, -193.37) * mm});
            skLineSegment(sketch, "E2681", {"start": v(-99.41, -193.37) * mm, "end": v(-98.44, -196.83) * mm});
            skLineSegment(sketch, "E2682", {"start": v(-98.44, -196.83) * mm, "end": v(-97.36, -200.19) * mm});
            skLineSegment(sketch, "E2683", {"start": v(-97.36, -200.19) * mm, "end": v(-95.95, -203.54) * mm});
            skLineSegment(sketch, "E2684", {"start": v(-95.95, -203.54) * mm, "end": v(-94.54, -206.79) * mm});
            skLineSegment(sketch, "E2685", {"start": v(-94.54, -206.79) * mm, "end": v(-92.81, -209.93) * mm});
            skLineSegment(sketch, "E2686", {"start": v(-92.81, -209.93) * mm, "end": v(-90.97, -212.96) * mm});
            skLineSegment(sketch, "E2687", {"start": v(-90.97, -212.96) * mm, "end": v(-88.91, -215.88) * mm});
            skLineSegment(sketch, "E2688", {"start": v(-88.91, -215.88) * mm, "end": v(-86.64, -218.7) * mm});
            skLineSegment(sketch, "E2689", {"start": v(-86.64, -218.7) * mm, "end": v(-84.26, -221.3) * mm});
            skLineSegment(sketch, "E2690", {"start": v(-84.26, -221.3) * mm, "end": v(-81.77, -223.89) * mm});
            skLineSegment(sketch, "E2691", {"start": v(-81.77, -223.89) * mm, "end": v(-79.07, -226.27) * mm});
            skLineSegment(sketch, "E2692", {"start": v(-79.07, -226.27) * mm, "end": v(-76.25, -228.43) * mm});
            skLineSegment(sketch, "E2693", {"start": v(-76.25, -228.43) * mm, "end": v(-73.33, -230.5) * mm});
            skLineSegment(sketch, "E2694", {"start": v(-73.33, -230.5) * mm, "end": v(-70.3, -232.33) * mm});
            skLineSegment(sketch, "E2695", {"start": v(-70.3, -232.33) * mm, "end": v(-67.16, -234.06) * mm});
            skLineSegment(sketch, "E2696", {"start": v(-67.16, -234.06) * mm, "end": v(-63.91, -235.58) * mm});
            skLineSegment(sketch, "E2697", {"start": v(-63.91, -235.58) * mm, "end": v(-60.66, -236.88) * mm});
            skLineSegment(sketch, "E2698", {"start": v(-60.66, -236.88) * mm, "end": v(-57.2, -238.07) * mm});
            skLineSegment(sketch, "E2699", {"start": v(-57.2, -238.07) * mm, "end": v(-53.74, -238.93) * mm});
            skLineSegment(sketch, "E2700", {"start": v(-53.74, -238.93) * mm, "end": v(-50.28, -239.7) * mm});
            skLineSegment(sketch, "E2701", {"start": v(-50.28, -239.7) * mm, "end": v(-46.7, -240.23) * mm});
            skLineSegment(sketch, "E2702", {"start": v(-46.7, -240.23) * mm, "end": v(-43.13, -240.45) * mm});
            skLineSegment(sketch, "E2703", {"start": v(-43.13, -240.45) * mm, "end": v(-39.56, -240.56) * mm});
            skLineSegment(sketch, "E2704", {"start": v(-39.56, -240.56) * mm, "end": v(-36.1, -240.45) * mm});
            skLineSegment(sketch, "E2705", {"start": v(-36.1, -240.45) * mm, "end": v(-32.52, -240.23) * mm});
            skLineSegment(sketch, "E2706", {"start": v(-32.52, -240.23) * mm, "end": v(-28.95, -239.7) * mm});
            skLineSegment(sketch, "E2707", {"start": v(-28.95, -239.7) * mm, "end": v(-25.49, -238.93) * mm});
            skLineSegment(sketch, "E2708", {"start": v(-25.49, -238.93) * mm, "end": v(-22.03, -238.07) * mm});
            skLineSegment(sketch, "E2709", {"start": v(-22.03, -238.07) * mm, "end": v(-18.56, -236.88) * mm});
            skLineSegment(sketch, "E2710", {"start": v(-18.56, -236.88) * mm, "end": v(-15.31, -235.58) * mm});
            skLineSegment(sketch, "E2711", {"start": v(-15.31, -235.58) * mm, "end": v(-12.07, -234.06) * mm});
            skLineSegment(sketch, "E2712", {"start": v(-12.07, -234.06) * mm, "end": v(-8.93, -232.33) * mm});
            skLineSegment(sketch, "E2713", {"start": v(-8.93, -232.33) * mm, "end": v(-5.9, -230.5) * mm});
            skLineSegment(sketch, "E2714", {"start": v(-5.9, -230.5) * mm, "end": v(-2.98, -228.43) * mm});
            skLineSegment(sketch, "E2715", {"start": v(-2.98, -228.43) * mm, "end": v(-0.16, -226.27) * mm});
            skLineSegment(sketch, "E2716", {"start": v(-0.16, -226.27) * mm, "end": v(2.55, -223.89) * mm});
            skLineSegment(sketch, "E2717", {"start": v(2.55, -223.89) * mm, "end": v(5.03, -221.3) * mm});
            skLineSegment(sketch, "E2718", {"start": v(5.03, -221.3) * mm, "end": v(7.42, -218.7) * mm});
            skLineSegment(sketch, "E2719", {"start": v(7.42, -218.7) * mm, "end": v(9.69, -215.88) * mm});
            skLineSegment(sketch, "E2720", {"start": v(9.69, -215.88) * mm, "end": v(11.74, -212.96) * mm});
            skLineSegment(sketch, "E2721", {"start": v(11.74, -212.96) * mm, "end": v(13.59, -209.93) * mm});
            skLineSegment(sketch, "E2722", {"start": v(13.59, -209.93) * mm, "end": v(15.32, -206.79) * mm});
            skLineSegment(sketch, "E2723", {"start": v(15.32, -206.79) * mm, "end": v(16.72, -203.54) * mm});
            skLineSegment(sketch, "E2724", {"start": v(16.72, -203.54) * mm, "end": v(18.13, -200.19) * mm});
            skLineSegment(sketch, "E2725", {"start": v(18.13, -200.19) * mm, "end": v(19.21, -196.83) * mm});
            skLineSegment(sketch, "E2726", {"start": v(19.21, -196.83) * mm, "end": v(20.18, -193.37) * mm});
            skLineSegment(sketch, "E2727", {"start": v(20.18, -193.37) * mm, "end": v(20.84, -189.8) * mm});
            skLineSegment(sketch, "E2728", {"start": v(20.84, -189.8) * mm, "end": v(21.38, -186.33) * mm});
            skLineSegment(sketch, "E2729", {"start": v(21.38, -186.33) * mm, "end": v(21.7, -182.76) * mm});
            skLineSegment(sketch, "E2730", {"start": v(21.7, -182.76) * mm, "end": v(21.81, -179.19) * mm});
            skLineSegment(sketch, "E2731", {"start": v(21.81, -179.19) * mm, "end": v(21.81, 28.09) * mm});
            skLineSegment(sketch, "E2732", {"start": v(21.81, 28.09) * mm, "end": v(21.7, 31.66) * mm});
            skLineSegment(sketch, "E2733", {"start": v(21.7, 31.66) * mm, "end": v(21.38, 35.23) * mm});
            skLineSegment(sketch, "E2734", {"start": v(21.38, 35.23) * mm, "end": v(20.84, 38.8) * mm});
            skLineSegment(sketch, "E2735", {"start": v(20.84, 38.8) * mm, "end": v(20.18, 42.26) * mm});
            skLineSegment(sketch, "E2736", {"start": v(20.18, 42.26) * mm, "end": v(19.21, 45.73) * mm});
            skLineSegment(sketch, "E2737", {"start": v(19.21, 45.73) * mm, "end": v(18.13, 49.08) * mm});
            skLineSegment(sketch, "E2738", {"start": v(18.13, 49.08) * mm, "end": v(16.72, 52.44) * mm});
            skLineSegment(sketch, "E2739", {"start": v(16.72, 52.44) * mm, "end": v(15.32, 55.69) * mm});
            skLineSegment(sketch, "E2740", {"start": v(15.32, 55.69) * mm, "end": v(13.59, 58.83) * mm});
            skLineSegment(sketch, "E2741", {"start": v(13.59, 58.83) * mm, "end": v(11.74, 61.86) * mm});
            skLineSegment(sketch, "E2742", {"start": v(11.74, 61.86) * mm, "end": v(9.69, 64.78) * mm});
            skLineSegment(sketch, "E2743", {"start": v(9.69, 64.78) * mm, "end": v(7.42, 67.6) * mm});
            skLineSegment(sketch, "E2744", {"start": v(7.42, 67.6) * mm, "end": v(5.03, 70.3) * mm});
            skLineSegment(sketch, "E2745", {"start": v(5.03, 70.3) * mm, "end": v(2.55, 72.79) * mm});
            skLineSegment(sketch, "E2746", {"start": v(2.55, 72.79) * mm, "end": v(-0.16, 75.17) * mm});
            skLineSegment(sketch, "E2747", {"start": v(-0.16, 75.17) * mm, "end": v(-2.98, 77.44) * mm});
            skLineSegment(sketch, "E2748", {"start": v(-2.98, 77.44) * mm, "end": v(-5.9, 79.5) * mm});
            skLineSegment(sketch, "E2749", {"start": v(-5.9, 79.5) * mm, "end": v(-8.93, 81.34) * mm});
            skLineSegment(sketch, "E2750", {"start": v(-8.93, 81.34) * mm, "end": v(-12.07, 83.07) * mm});
            skLineSegment(sketch, "E2751", {"start": v(-12.07, 83.07) * mm, "end": v(-15.31, 84.48) * mm});
            skLineSegment(sketch, "E2752", {"start": v(-15.31, 84.48) * mm, "end": v(-18.56, 85.89) * mm});
            skLineSegment(sketch, "E2753", {"start": v(-18.56, 85.89) * mm, "end": v(-22.03, 86.97) * mm});
            skLineSegment(sketch, "E2754", {"start": v(-22.03, 86.97) * mm, "end": v(-25.49, 87.94) * mm});
            skLineSegment(sketch, "E2755", {"start": v(-25.49, 87.94) * mm, "end": v(-28.95, 88.6) * mm});
            skLineSegment(sketch, "E2756", {"start": v(-28.95, 88.6) * mm, "end": v(-32.52, 89.13) * mm});
            skLineSegment(sketch, "E2757", {"start": v(-32.52, 89.13) * mm, "end": v(-36.1, 89.46) * mm});
            skLineSegment(sketch, "E2758", {"start": v(-36.1, 89.46) * mm, "end": v(-39.56, 89.57) * mm});
            skLineSegment(sketch, "E2759", {"start": v(-39.56, 89.57) * mm, "end": v(-43.13, 89.46) * mm});
            skLineSegment(sketch, "E2760", {"start": v(-43.13, 89.46) * mm, "end": v(-46.7, 89.13) * mm});
            skLineSegment(sketch, "E2761", {"start": v(-46.7, 89.13) * mm, "end": v(-50.28, 88.6) * mm});
            skLineSegment(sketch, "E2762", {"start": v(-50.28, 88.6) * mm, "end": v(-53.74, 87.94) * mm});
            skLineSegment(sketch, "E2763", {"start": v(-53.74, 87.94) * mm, "end": v(-57.2, 86.97) * mm});
            skLineSegment(sketch, "E2764", {"start": v(-57.2, 86.97) * mm, "end": v(-60.66, 85.89) * mm});
            skLineSegment(sketch, "E2765", {"start": v(-60.66, 85.89) * mm, "end": v(-63.91, 84.48) * mm});
            skLineSegment(sketch, "E2766", {"start": v(-63.91, 84.48) * mm, "end": v(-67.16, 83.07) * mm});
            skLineSegment(sketch, "E2767", {"start": v(-67.16, 83.07) * mm, "end": v(-70.3, 81.34) * mm});
            skLineSegment(sketch, "E2768", {"start": v(-70.3, 81.34) * mm, "end": v(-73.33, 79.5) * mm});
            skLineSegment(sketch, "E2769", {"start": v(-73.33, 79.5) * mm, "end": v(-76.25, 77.44) * mm});
            skLineSegment(sketch, "E2770", {"start": v(-76.25, 77.44) * mm, "end": v(-79.07, 75.17) * mm});
            skLineSegment(sketch, "E2771", {"start": v(-79.07, 75.17) * mm, "end": v(-81.77, 72.79) * mm});
            skLineSegment(sketch, "E2772", {"start": v(-81.77, 72.79) * mm, "end": v(-84.26, 70.3) * mm});
            skLineSegment(sketch, "E2773", {"start": v(-84.26, 70.3) * mm, "end": v(-86.64, 67.6) * mm});
            skLineSegment(sketch, "E2774", {"start": v(-86.64, 67.6) * mm, "end": v(-88.91, 64.78) * mm});
            skLineSegment(sketch, "E2775", {"start": v(-88.91, 64.78) * mm, "end": v(-90.97, 61.86) * mm});
            skLineSegment(sketch, "E2776", {"start": v(-90.97, 61.86) * mm, "end": v(-92.81, 58.83) * mm});
            skLineSegment(sketch, "E2777", {"start": v(-92.81, 58.83) * mm, "end": v(-94.54, 55.69) * mm});
            skLineSegment(sketch, "E2778", {"start": v(-94.54, 55.69) * mm, "end": v(-95.95, 52.44) * mm});
            skLineSegment(sketch, "E2779", {"start": v(-95.95, 52.44) * mm, "end": v(-97.36, 49.08) * mm});
            skLineSegment(sketch, "E2780", {"start": v(-97.36, 49.08) * mm, "end": v(-98.44, 45.73) * mm});
            skLineSegment(sketch, "E2781", {"start": v(-98.44, 45.73) * mm, "end": v(-99.41, 42.26) * mm});
            skLineSegment(sketch, "E2782", {"start": v(-99.41, 42.26) * mm, "end": v(-100.07, 38.8) * mm});
            skLineSegment(sketch, "E2783", {"start": v(-100.07, 38.8) * mm, "end": v(-100.6, 35.23) * mm});
            skLineSegment(sketch, "E2784", {"start": v(-100.6, 35.23) * mm, "end": v(-100.93, 31.66) * mm});
            skLineSegment(sketch, "E2785", {"start": v(-100.93, 31.66) * mm, "end": v(-101.04, 28.09) * mm});
            skLineSegment(sketch, "E2786", {"start": v(220.75, -101.9) * mm, "end": v(220.75, -211.12) * mm});
            skLineSegment(sketch, "E2787", {"start": v(203.33, -211.12) * mm, "end": v(203.43, -212.42) * mm});
            skLineSegment(sketch, "E2788", {"start": v(203.43, -212.42) * mm, "end": v(203.76, -213.82) * mm});
            skLineSegment(sketch, "E2789", {"start": v(203.76, -213.82) * mm, "end": v(204.3, -215.01) * mm});
            skLineSegment(sketch, "E2790", {"start": v(204.3, -215.01) * mm, "end": v(205.06, -216.2) * mm});
            skLineSegment(sketch, "E2791", {"start": v(205.06, -216.2) * mm, "end": v(205.92, -217.29) * mm});
            skLineSegment(sketch, "E2792", {"start": v(205.92, -217.29) * mm, "end": v(206.9, -218.15) * mm});
            skLineSegment(sketch, "E2793", {"start": v(206.9, -218.15) * mm, "end": v(208.09, -218.8) * mm});
            skLineSegment(sketch, "E2794", {"start": v(208.09, -218.8) * mm, "end": v(209.39, -219.35) * mm});
            skLineSegment(sketch, "E2795", {"start": v(209.39, -219.35) * mm, "end": v(210.68, -219.67) * mm});
            skLineSegment(sketch, "E2796", {"start": v(210.68, -219.67) * mm, "end": v(212.09, -219.78) * mm});
            skLineSegment(sketch, "E2797", {"start": v(212.09, -219.78) * mm, "end": v(213.4, -219.67) * mm});
            skLineSegment(sketch, "E2798", {"start": v(213.4, -219.67) * mm, "end": v(214.69, -219.35) * mm});
            skLineSegment(sketch, "E2799", {"start": v(214.69, -219.35) * mm, "end": v(215.99, -218.8) * mm});
            skLineSegment(sketch, "E2800", {"start": v(215.99, -218.8) * mm, "end": v(217.18, -218.15) * mm});
            skLineSegment(sketch, "E2801", {"start": v(217.18, -218.15) * mm, "end": v(218.15, -217.29) * mm});
            skLineSegment(sketch, "E2802", {"start": v(218.15, -217.29) * mm, "end": v(219.13, -216.2) * mm});
            skLineSegment(sketch, "E2803", {"start": v(219.13, -216.2) * mm, "end": v(219.78, -215.01) * mm});
            skLineSegment(sketch, "E2804", {"start": v(219.78, -215.01) * mm, "end": v(220.32, -213.82) * mm});
            skLineSegment(sketch, "E2805", {"start": v(220.32, -213.82) * mm, "end": v(220.64, -212.42) * mm});
            skLineSegment(sketch, "E2806", {"start": v(220.64, -212.42) * mm, "end": v(220.75, -211.12) * mm});
            skLineSegment(sketch, "E2807", {"start": v(203.33, -211.12) * mm, "end": v(203.33, -101.9) * mm});
            skLineSegment(sketch, "E2808", {"start": v(220.75, -101.9) * mm, "end": v(220.64, -100.5) * mm});
            skLineSegment(sketch, "E2809", {"start": v(220.64, -100.5) * mm, "end": v(220.32, -99.2) * mm});
            skLineSegment(sketch, "E2810", {"start": v(220.32, -99.2) * mm, "end": v(219.78, -97.9) * mm});
            skLineSegment(sketch, "E2811", {"start": v(219.78, -97.9) * mm, "end": v(219.13, -96.82) * mm});
            skLineSegment(sketch, "E2812", {"start": v(219.13, -96.82) * mm, "end": v(218.15, -95.74) * mm});
            skLineSegment(sketch, "E2813", {"start": v(218.15, -95.74) * mm, "end": v(217.18, -94.87) * mm});
            skLineSegment(sketch, "E2814", {"start": v(217.18, -94.87) * mm, "end": v(215.99, -94.12) * mm});
            skLineSegment(sketch, "E2815", {"start": v(215.99, -94.12) * mm, "end": v(214.69, -93.57) * mm});
            skLineSegment(sketch, "E2816", {"start": v(214.69, -93.57) * mm, "end": v(213.4, -93.25) * mm});
            skLineSegment(sketch, "E2817", {"start": v(213.4, -93.25) * mm, "end": v(212.09, -93.14) * mm});
            skLineSegment(sketch, "E2818", {"start": v(212.09, -93.14) * mm, "end": v(210.68, -93.25) * mm});
            skLineSegment(sketch, "E2819", {"start": v(210.68, -93.25) * mm, "end": v(209.39, -93.57) * mm});
            skLineSegment(sketch, "E2820", {"start": v(209.39, -93.57) * mm, "end": v(208.09, -94.12) * mm});
            skLineSegment(sketch, "E2821", {"start": v(208.09, -94.12) * mm, "end": v(206.9, -94.87) * mm});
            skLineSegment(sketch, "E2822", {"start": v(206.9, -94.87) * mm, "end": v(205.92, -95.74) * mm});
            skLineSegment(sketch, "E2823", {"start": v(205.92, -95.74) * mm, "end": v(205.06, -96.82) * mm});
            skLineSegment(sketch, "E2824", {"start": v(205.06, -96.82) * mm, "end": v(204.3, -97.9) * mm});
            skLineSegment(sketch, "E2825", {"start": v(204.3, -97.9) * mm, "end": v(203.76, -99.2) * mm});
            skLineSegment(sketch, "E2826", {"start": v(203.76, -99.2) * mm, "end": v(203.43, -100.5) * mm});
            skLineSegment(sketch, "E2827", {"start": v(203.43, -100.5) * mm, "end": v(203.33, -101.9) * mm});
            skLineSegment(sketch, "E2828", {"start": v(180.7, -103.64) * mm, "end": v(180.7, -209.28) * mm});
            skLineSegment(sketch, "E2829", {"start": v(180.7, -209.28) * mm, "end": v(180.81, -211.88) * mm});
            skLineSegment(sketch, "E2830", {"start": v(180.81, -211.88) * mm, "end": v(181.14, -214.47) * mm});
            skLineSegment(sketch, "E2831", {"start": v(181.14, -214.47) * mm, "end": v(181.68, -216.96) * mm});
            skLineSegment(sketch, "E2832", {"start": v(181.68, -216.96) * mm, "end": v(182.43, -219.45) * mm});
            skLineSegment(sketch, "E2833", {"start": v(182.43, -219.45) * mm, "end": v(183.4, -221.83) * mm});
            skLineSegment(sketch, "E2834", {"start": v(183.4, -221.83) * mm, "end": v(184.5, -224.21) * mm});
            skLineSegment(sketch, "E2835", {"start": v(184.5, -224.21) * mm, "end": v(185.79, -226.38) * mm});
            skLineSegment(sketch, "E2836", {"start": v(185.79, -226.38) * mm, "end": v(187.3, -228.54) * mm});
            skLineSegment(sketch, "E2837", {"start": v(187.3, -228.54) * mm, "end": v(189.04, -230.5) * mm});
            skLineSegment(sketch, "E2838", {"start": v(189.04, -230.5) * mm, "end": v(190.88, -232.33) * mm});
            skLineSegment(sketch, "E2839", {"start": v(190.88, -232.33) * mm, "end": v(192.82, -233.96) * mm});
            skLineSegment(sketch, "E2840", {"start": v(192.82, -233.96) * mm, "end": v(194.88, -235.47) * mm});
            skLineSegment(sketch, "E2841", {"start": v(194.88, -235.47) * mm, "end": v(197.16, -236.88) * mm});
            skLineSegment(sketch, "E2842", {"start": v(197.16, -236.88) * mm, "end": v(199.43, -237.96) * mm});
            skLineSegment(sketch, "E2843", {"start": v(199.43, -237.96) * mm, "end": v(201.92, -238.93) * mm});
            skLineSegment(sketch, "E2844", {"start": v(201.92, -238.93) * mm, "end": v(204.4, -239.7) * mm});
            skLineSegment(sketch, "E2845", {"start": v(204.4, -239.7) * mm, "end": v(206.9, -240.12) * mm});
            skLineSegment(sketch, "E2846", {"start": v(206.9, -240.12) * mm, "end": v(209.5, -240.45) * mm});
            skLineSegment(sketch, "E2847", {"start": v(209.5, -240.45) * mm, "end": v(212.09, -240.56) * mm});
            skLineSegment(sketch, "E2848", {"start": v(212.09, -240.56) * mm, "end": v(214.58, -240.45) * mm});
            skLineSegment(sketch, "E2849", {"start": v(214.58, -240.45) * mm, "end": v(217.18, -240.12) * mm});
            skLineSegment(sketch, "E2850", {"start": v(217.18, -240.12) * mm, "end": v(219.78, -239.7) * mm});
            skLineSegment(sketch, "E2851", {"start": v(219.78, -239.7) * mm, "end": v(222.16, -238.93) * mm});
            skLineSegment(sketch, "E2852", {"start": v(222.16, -238.93) * mm, "end": v(224.64, -237.96) * mm});
            skLineSegment(sketch, "E2853", {"start": v(224.64, -237.96) * mm, "end": v(226.92, -236.88) * mm});
            skLineSegment(sketch, "E2854", {"start": v(226.92, -236.88) * mm, "end": v(229.2, -235.47) * mm});
            skLineSegment(sketch, "E2855", {"start": v(229.2, -235.47) * mm, "end": v(231.25, -233.96) * mm});
            skLineSegment(sketch, "E2856", {"start": v(231.25, -233.96) * mm, "end": v(233.2, -232.33) * mm});
            skLineSegment(sketch, "E2857", {"start": v(233.2, -232.33) * mm, "end": v(235.04, -230.5) * mm});
            skLineSegment(sketch, "E2858", {"start": v(235.04, -230.5) * mm, "end": v(236.77, -228.54) * mm});
            skLineSegment(sketch, "E2859", {"start": v(236.77, -228.54) * mm, "end": v(238.28, -226.38) * mm});
            skLineSegment(sketch, "E2860", {"start": v(238.28, -226.38) * mm, "end": v(239.58, -224.21) * mm});
            skLineSegment(sketch, "E2861", {"start": v(239.58, -224.21) * mm, "end": v(240.66, -221.83) * mm});
            skLineSegment(sketch, "E2862", {"start": v(240.66, -221.83) * mm, "end": v(241.64, -219.45) * mm});
            skLineSegment(sketch, "E2863", {"start": v(241.64, -219.45) * mm, "end": v(242.4, -216.96) * mm});
            skLineSegment(sketch, "E2864", {"start": v(242.4, -216.96) * mm, "end": v(242.94, -214.47) * mm});
            skLineSegment(sketch, "E2865", {"start": v(242.94, -214.47) * mm, "end": v(243.26, -211.88) * mm});
            skLineSegment(sketch, "E2866", {"start": v(243.26, -211.88) * mm, "end": v(243.37, -209.28) * mm});
            skLineSegment(sketch, "E2867", {"start": v(243.37, -209.28) * mm, "end": v(243.37, -103.64) * mm});
            skLineSegment(sketch, "E2868", {"start": v(243.37, -103.64) * mm, "end": v(243.26, -101.04) * mm});
            skLineSegment(sketch, "E2869", {"start": v(243.26, -101.04) * mm, "end": v(242.94, -98.55) * mm});
            skLineSegment(sketch, "E2870", {"start": v(242.94, -98.55) * mm, "end": v(242.4, -95.95) * mm});
            skLineSegment(sketch, "E2871", {"start": v(242.4, -95.95) * mm, "end": v(241.64, -93.47) * mm});
            skLineSegment(sketch, "E2872", {"start": v(241.64, -93.47) * mm, "end": v(240.66, -91.09) * mm});
            skLineSegment(sketch, "E2873", {"start": v(240.66, -91.09) * mm, "end": v(239.58, -88.8) * mm});
            skLineSegment(sketch, "E2874", {"start": v(239.58, -88.8) * mm, "end": v(238.28, -86.54) * mm});
            skLineSegment(sketch, "E2875", {"start": v(238.28, -86.54) * mm, "end": v(236.77, -84.48) * mm});
            skLineSegment(sketch, "E2876", {"start": v(236.77, -84.48) * mm, "end": v(235.04, -82.42) * mm});
            skLineSegment(sketch, "E2877", {"start": v(235.04, -82.42) * mm, "end": v(233.2, -80.7) * mm});
            skLineSegment(sketch, "E2878", {"start": v(233.2, -80.7) * mm, "end": v(231.25, -78.96) * mm});
            skLineSegment(sketch, "E2879", {"start": v(231.25, -78.96) * mm, "end": v(229.2, -77.45) * mm});
            skLineSegment(sketch, "E2880", {"start": v(229.2, -77.45) * mm, "end": v(226.92, -76.15) * mm});
            skLineSegment(sketch, "E2881", {"start": v(226.92, -76.15) * mm, "end": v(224.64, -74.96) * mm});
            skLineSegment(sketch, "E2882", {"start": v(224.64, -74.96) * mm, "end": v(222.16, -74.09) * mm});
            skLineSegment(sketch, "E2883", {"start": v(222.16, -74.09) * mm, "end": v(219.78, -73.33) * mm});
            skLineSegment(sketch, "E2884", {"start": v(219.78, -73.33) * mm, "end": v(217.18, -72.79) * mm});
            skLineSegment(sketch, "E2885", {"start": v(217.18, -72.79) * mm, "end": v(214.58, -72.46) * mm});
            skLineSegment(sketch, "E2886", {"start": v(214.58, -72.46) * mm, "end": v(212.09, -72.36) * mm});
            skLineSegment(sketch, "E2887", {"start": v(212.09, -72.36) * mm, "end": v(209.5, -72.46) * mm});
            skLineSegment(sketch, "E2888", {"start": v(209.5, -72.46) * mm, "end": v(206.9, -72.79) * mm});
            skLineSegment(sketch, "E2889", {"start": v(206.9, -72.79) * mm, "end": v(204.4, -73.33) * mm});
            skLineSegment(sketch, "E2890", {"start": v(204.4, -73.33) * mm, "end": v(201.92, -74.09) * mm});
            skLineSegment(sketch, "E2891", {"start": v(201.92, -74.09) * mm, "end": v(199.43, -74.96) * mm});
            skLineSegment(sketch, "E2892", {"start": v(199.43, -74.96) * mm, "end": v(197.16, -76.15) * mm});
            skLineSegment(sketch, "E2893", {"start": v(197.16, -76.15) * mm, "end": v(194.88, -77.45) * mm});
            skLineSegment(sketch, "E2894", {"start": v(194.88, -77.45) * mm, "end": v(192.82, -78.96) * mm});
            skLineSegment(sketch, "E2895", {"start": v(192.82, -78.96) * mm, "end": v(190.88, -80.7) * mm});
            skLineSegment(sketch, "E2896", {"start": v(190.88, -80.7) * mm, "end": v(189.04, -82.42) * mm});
            skLineSegment(sketch, "E2897", {"start": v(189.04, -82.42) * mm, "end": v(187.3, -84.48) * mm});
            skLineSegment(sketch, "E2898", {"start": v(187.3, -84.48) * mm, "end": v(185.79, -86.54) * mm});
            skLineSegment(sketch, "E2899", {"start": v(185.79, -86.54) * mm, "end": v(184.5, -88.8) * mm});
            skLineSegment(sketch, "E2900", {"start": v(184.5, -88.8) * mm, "end": v(183.4, -91.09) * mm});
            skLineSegment(sketch, "E2901", {"start": v(183.4, -91.09) * mm, "end": v(182.43, -93.47) * mm});
            skLineSegment(sketch, "E2902", {"start": v(182.43, -93.47) * mm, "end": v(181.68, -95.95) * mm});
            skLineSegment(sketch, "E2903", {"start": v(181.68, -95.95) * mm, "end": v(181.14, -98.55) * mm});
            skLineSegment(sketch, "E2904", {"start": v(181.14, -98.55) * mm, "end": v(180.81, -101.04) * mm});
            skLineSegment(sketch, "E2905", {"start": v(180.81, -101.04) * mm, "end": v(180.7, -103.64) * mm});
            skLineSegment(sketch, "E2906", {"start": v(96.93, 60.02) * mm, "end": v(96.93, -49.2) * mm});
            skLineSegment(sketch, "E2907", {"start": v(79.5, -49.2) * mm, "end": v(79.61, -50.5) * mm});
            skLineSegment(sketch, "E2908", {"start": v(79.61, -50.5) * mm, "end": v(79.94, -51.9) * mm});
            skLineSegment(sketch, "E2909", {"start": v(79.94, -51.9) * mm, "end": v(80.47, -53.09) * mm});
            skLineSegment(sketch, "E2910", {"start": v(80.47, -53.09) * mm, "end": v(81.12, -54.28) * mm});
            skLineSegment(sketch, "E2911", {"start": v(81.12, -54.28) * mm, "end": v(81.99, -55.37) * mm});
            skLineSegment(sketch, "E2912", {"start": v(81.99, -55.37) * mm, "end": v(83.07, -56.23) * mm});
            skLineSegment(sketch, "E2913", {"start": v(83.07, -56.23) * mm, "end": v(84.26, -56.88) * mm});
            skLineSegment(sketch, "E2914", {"start": v(84.26, -56.88) * mm, "end": v(85.45, -57.42) * mm});
            skLineSegment(sketch, "E2915", {"start": v(85.45, -57.42) * mm, "end": v(86.86, -57.75) * mm});
            skLineSegment(sketch, "E2916", {"start": v(86.86, -57.75) * mm, "end": v(88.16, -57.85) * mm});
            skLineSegment(sketch, "E2917", {"start": v(88.16, -57.85) * mm, "end": v(89.57, -57.75) * mm});
            skLineSegment(sketch, "E2918", {"start": v(89.57, -57.75) * mm, "end": v(90.86, -57.42) * mm});
            skLineSegment(sketch, "E2919", {"start": v(90.86, -57.42) * mm, "end": v(92.16, -56.88) * mm});
            skLineSegment(sketch, "E2920", {"start": v(92.16, -56.88) * mm, "end": v(93.24, -56.23) * mm});
            skLineSegment(sketch, "E2921", {"start": v(93.24, -56.23) * mm, "end": v(94.33, -55.37) * mm});
            skLineSegment(sketch, "E2922", {"start": v(94.33, -55.37) * mm, "end": v(95.2, -54.28) * mm});
            skLineSegment(sketch, "E2923", {"start": v(95.2, -54.28) * mm, "end": v(95.95, -53.09) * mm});
            skLineSegment(sketch, "E2924", {"start": v(95.95, -53.09) * mm, "end": v(96.5, -51.9) * mm});
            skLineSegment(sketch, "E2925", {"start": v(96.5, -51.9) * mm, "end": v(96.82, -50.5) * mm});
            skLineSegment(sketch, "E2926", {"start": v(96.82, -50.5) * mm, "end": v(96.93, -49.2) * mm});
            skLineSegment(sketch, "E2927", {"start": v(79.5, -49.2) * mm, "end": v(79.5, 60.02) * mm});
            skLineSegment(sketch, "E2928", {"start": v(96.93, 60.02) * mm, "end": v(96.82, 61.42) * mm});
            skLineSegment(sketch, "E2929", {"start": v(96.82, 61.42) * mm, "end": v(96.5, 62.72) * mm});
            skLineSegment(sketch, "E2930", {"start": v(96.5, 62.72) * mm, "end": v(95.95, 64.02) * mm});
            skLineSegment(sketch, "E2931", {"start": v(95.95, 64.02) * mm, "end": v(95.2, 65.1) * mm});
            skLineSegment(sketch, "E2932", {"start": v(95.2, 65.1) * mm, "end": v(94.33, 66.18) * mm});
            skLineSegment(sketch, "E2933", {"start": v(94.33, 66.18) * mm, "end": v(93.24, 67.05) * mm});
            skLineSegment(sketch, "E2934", {"start": v(93.24, 67.05) * mm, "end": v(92.16, 67.8) * mm});
            skLineSegment(sketch, "E2935", {"start": v(92.16, 67.8) * mm, "end": v(90.86, 68.35) * mm});
            skLineSegment(sketch, "E2936", {"start": v(90.86, 68.35) * mm, "end": v(89.57, 68.68) * mm});
            skLineSegment(sketch, "E2937", {"start": v(89.57, 68.68) * mm, "end": v(88.16, 68.78) * mm});
            skLineSegment(sketch, "E2938", {"start": v(88.16, 68.78) * mm, "end": v(86.86, 68.68) * mm});
            skLineSegment(sketch, "E2939", {"start": v(86.86, 68.68) * mm, "end": v(85.45, 68.35) * mm});
            skLineSegment(sketch, "E2940", {"start": v(85.45, 68.35) * mm, "end": v(84.26, 67.8) * mm});
            skLineSegment(sketch, "E2941", {"start": v(84.26, 67.8) * mm, "end": v(83.07, 67.05) * mm});
            skLineSegment(sketch, "E2942", {"start": v(83.07, 67.05) * mm, "end": v(81.99, 66.18) * mm});
            skLineSegment(sketch, "E2943", {"start": v(81.99, 66.18) * mm, "end": v(81.12, 65.1) * mm});
            skLineSegment(sketch, "E2944", {"start": v(81.12, 65.1) * mm, "end": v(80.47, 64.02) * mm});
            skLineSegment(sketch, "E2945", {"start": v(80.47, 64.02) * mm, "end": v(79.94, 62.72) * mm});
            skLineSegment(sketch, "E2946", {"start": v(79.94, 62.72) * mm, "end": v(79.61, 61.42) * mm});
            skLineSegment(sketch, "E2947", {"start": v(79.61, 61.42) * mm, "end": v(79.5, 60.02) * mm});
            skLineSegment(sketch, "E2948", {"start": v(56.88, 58.28) * mm, "end": v(56.88, -47.35) * mm});
            skLineSegment(sketch, "E2949", {"start": v(56.88, -47.35) * mm, "end": v(56.99, -49.96) * mm});
            skLineSegment(sketch, "E2950", {"start": v(56.99, -49.96) * mm, "end": v(57.31, -52.55) * mm});
            skLineSegment(sketch, "E2951", {"start": v(57.31, -52.55) * mm, "end": v(57.86, -55.04) * mm});
            skLineSegment(sketch, "E2952", {"start": v(57.86, -55.04) * mm, "end": v(58.6, -57.53) * mm});
            skLineSegment(sketch, "E2953", {"start": v(58.6, -57.53) * mm, "end": v(59.48, -59.9) * mm});
            skLineSegment(sketch, "E2954", {"start": v(59.48, -59.9) * mm, "end": v(60.67, -62.29) * mm});
            skLineSegment(sketch, "E2955", {"start": v(60.67, -62.29) * mm, "end": v(61.97, -64.46) * mm});
            skLineSegment(sketch, "E2956", {"start": v(61.97, -64.46) * mm, "end": v(63.48, -66.62) * mm});
            skLineSegment(sketch, "E2957", {"start": v(63.48, -66.62) * mm, "end": v(65.21, -68.57) * mm});
            skLineSegment(sketch, "E2958", {"start": v(65.21, -68.57) * mm, "end": v(66.95, -70.4) * mm});
            skLineSegment(sketch, "E2959", {"start": v(66.95, -70.4) * mm, "end": v(69, -72.04) * mm});
            skLineSegment(sketch, "E2960", {"start": v(69, -72.04) * mm, "end": v(71.06, -73.55) * mm});
            skLineSegment(sketch, "E2961", {"start": v(71.06, -73.55) * mm, "end": v(73.33, -74.96) * mm});
            skLineSegment(sketch, "E2962", {"start": v(73.33, -74.96) * mm, "end": v(75.6, -76.04) * mm});
            skLineSegment(sketch, "E2963", {"start": v(75.6, -76.04) * mm, "end": v(77.98, -77.01) * mm});
            skLineSegment(sketch, "E2964", {"start": v(77.98, -77.01) * mm, "end": v(80.47, -77.77) * mm});
            skLineSegment(sketch, "E2965", {"start": v(80.47, -77.77) * mm, "end": v(83.07, -78.3) * mm});
            skLineSegment(sketch, "E2966", {"start": v(83.07, -78.3) * mm, "end": v(85.56, -78.53) * mm});
            skLineSegment(sketch, "E2967", {"start": v(85.56, -78.53) * mm, "end": v(88.16, -78.63) * mm});
            skLineSegment(sketch, "E2968", {"start": v(88.16, -78.63) * mm, "end": v(90.76, -78.53) * mm});
            skLineSegment(sketch, "E2969", {"start": v(90.76, -78.53) * mm, "end": v(93.35, -78.3) * mm});
            skLineSegment(sketch, "E2970", {"start": v(93.35, -78.3) * mm, "end": v(95.85, -77.77) * mm});
            skLineSegment(sketch, "E2971", {"start": v(95.85, -77.77) * mm, "end": v(98.33, -77.01) * mm});
            skLineSegment(sketch, "E2972", {"start": v(98.33, -77.01) * mm, "end": v(100.72, -76.04) * mm});
            skLineSegment(sketch, "E2973", {"start": v(100.72, -76.04) * mm, "end": v(103.1, -74.96) * mm});
            skLineSegment(sketch, "E2974", {"start": v(103.1, -74.96) * mm, "end": v(105.26, -73.55) * mm});
            skLineSegment(sketch, "E2975", {"start": v(105.26, -73.55) * mm, "end": v(107.43, -72.04) * mm});
            skLineSegment(sketch, "E2976", {"start": v(107.43, -72.04) * mm, "end": v(109.37, -70.4) * mm});
            skLineSegment(sketch, "E2977", {"start": v(109.37, -70.4) * mm, "end": v(111.21, -68.57) * mm});
            skLineSegment(sketch, "E2978", {"start": v(111.21, -68.57) * mm, "end": v(112.84, -66.62) * mm});
            skLineSegment(sketch, "E2979", {"start": v(112.84, -66.62) * mm, "end": v(114.35, -64.46) * mm});
            skLineSegment(sketch, "E2980", {"start": v(114.35, -64.46) * mm, "end": v(115.76, -62.29) * mm});
            skLineSegment(sketch, "E2981", {"start": v(115.76, -62.29) * mm, "end": v(116.84, -59.9) * mm});
            skLineSegment(sketch, "E2982", {"start": v(116.84, -59.9) * mm, "end": v(117.82, -57.53) * mm});
            skLineSegment(sketch, "E2983", {"start": v(117.82, -57.53) * mm, "end": v(118.57, -55.04) * mm});
            skLineSegment(sketch, "E2984", {"start": v(118.57, -55.04) * mm, "end": v(119, -52.55) * mm});
            skLineSegment(sketch, "E2985", {"start": v(119, -52.55) * mm, "end": v(119.33, -49.96) * mm});
            skLineSegment(sketch, "E2986", {"start": v(119.33, -49.96) * mm, "end": v(119.44, -47.35) * mm});
            skLineSegment(sketch, "E2987", {"start": v(119.44, -47.35) * mm, "end": v(119.44, 58.28) * mm});
            skLineSegment(sketch, "E2988", {"start": v(119.44, 58.28) * mm, "end": v(119.33, 60.88) * mm});
            skLineSegment(sketch, "E2989", {"start": v(119.33, 60.88) * mm, "end": v(119, 63.37) * mm});
            skLineSegment(sketch, "E2990", {"start": v(119, 63.37) * mm, "end": v(118.57, 65.97) * mm});
            skLineSegment(sketch, "E2991", {"start": v(118.57, 65.97) * mm, "end": v(117.82, 68.46) * mm});
            skLineSegment(sketch, "E2992", {"start": v(117.82, 68.46) * mm, "end": v(116.84, 70.84) * mm});
            skLineSegment(sketch, "E2993", {"start": v(116.84, 70.84) * mm, "end": v(115.76, 73.11) * mm});
            skLineSegment(sketch, "E2994", {"start": v(115.76, 73.11) * mm, "end": v(114.35, 75.38) * mm});
            skLineSegment(sketch, "E2995", {"start": v(114.35, 75.38) * mm, "end": v(112.84, 77.44) * mm});
            skLineSegment(sketch, "E2996", {"start": v(112.84, 77.44) * mm, "end": v(111.21, 79.5) * mm});
            skLineSegment(sketch, "E2997", {"start": v(111.21, 79.5) * mm, "end": v(109.37, 81.23) * mm});
            skLineSegment(sketch, "E2998", {"start": v(109.37, 81.23) * mm, "end": v(107.43, 82.96) * mm});
            skLineSegment(sketch, "E2999", {"start": v(107.43, 82.96) * mm, "end": v(105.26, 84.48) * mm});
            skLineSegment(sketch, "E3000", {"start": v(105.26, 84.48) * mm, "end": v(103.1, 85.78) * mm});
            skLineSegment(sketch, "E3001", {"start": v(103.1, 85.78) * mm, "end": v(100.72, 86.97) * mm});
            skLineSegment(sketch, "E3002", {"start": v(100.72, 86.97) * mm, "end": v(98.33, 87.83) * mm});
            skLineSegment(sketch, "E3003", {"start": v(98.33, 87.83) * mm, "end": v(95.85, 88.6) * mm});
            skLineSegment(sketch, "E3004", {"start": v(95.85, 88.6) * mm, "end": v(93.35, 89.13) * mm});
            skLineSegment(sketch, "E3005", {"start": v(93.35, 89.13) * mm, "end": v(90.76, 89.46) * mm});
            skLineSegment(sketch, "E3006", {"start": v(90.76, 89.46) * mm, "end": v(88.16, 89.57) * mm});
            skLineSegment(sketch, "E3007", {"start": v(88.16, 89.57) * mm, "end": v(85.56, 89.46) * mm});
            skLineSegment(sketch, "E3008", {"start": v(85.56, 89.46) * mm, "end": v(83.07, 89.13) * mm});
            skLineSegment(sketch, "E3009", {"start": v(83.07, 89.13) * mm, "end": v(80.47, 88.6) * mm});
            skLineSegment(sketch, "E3010", {"start": v(80.47, 88.6) * mm, "end": v(77.98, 87.83) * mm});
            skLineSegment(sketch, "E3011", {"start": v(77.98, 87.83) * mm, "end": v(75.6, 86.97) * mm});
            skLineSegment(sketch, "E3012", {"start": v(75.6, 86.97) * mm, "end": v(73.33, 85.78) * mm});
            skLineSegment(sketch, "E3013", {"start": v(73.33, 85.78) * mm, "end": v(71.06, 84.48) * mm});
            skLineSegment(sketch, "E3014", {"start": v(71.06, 84.48) * mm, "end": v(69, 82.96) * mm});
            skLineSegment(sketch, "E3015", {"start": v(69, 82.96) * mm, "end": v(66.95, 81.23) * mm});
            skLineSegment(sketch, "E3016", {"start": v(66.95, 81.23) * mm, "end": v(65.21, 79.5) * mm});
            skLineSegment(sketch, "E3017", {"start": v(65.21, 79.5) * mm, "end": v(63.48, 77.44) * mm});
            skLineSegment(sketch, "E3018", {"start": v(63.48, 77.44) * mm, "end": v(61.97, 75.38) * mm});
            skLineSegment(sketch, "E3019", {"start": v(61.97, 75.38) * mm, "end": v(60.67, 73.11) * mm});
            skLineSegment(sketch, "E3020", {"start": v(60.67, 73.11) * mm, "end": v(59.48, 70.84) * mm});
            skLineSegment(sketch, "E3021", {"start": v(59.48, 70.84) * mm, "end": v(58.6, 68.46) * mm});
            skLineSegment(sketch, "E3022", {"start": v(58.6, 68.46) * mm, "end": v(57.86, 65.97) * mm});
            skLineSegment(sketch, "E3023", {"start": v(57.86, 65.97) * mm, "end": v(57.31, 63.37) * mm});
            skLineSegment(sketch, "E3024", {"start": v(57.31, 63.37) * mm, "end": v(56.99, 60.88) * mm});
            skLineSegment(sketch, "E3025", {"start": v(56.99, 60.88) * mm, "end": v(56.88, 58.28) * mm});
            skLineSegment(sketch, "E3026", {"start": v(-63.26, -328.45) * mm, "end": v(-82.64, -328.45) * mm});
            skLineSegment(sketch, "E3027", {"start": v(-82.64, -328.45) * mm, "end": v(-82.64, -387.54) * mm});
            skLineSegment(sketch, "E3028", {"start": v(-82.64, -387.54) * mm, "end": v(-63.26, -387.54) * mm});
            skLineSegment(sketch, "E3029", {"start": v(-63.26, -387.54) * mm, "end": v(-63.26, -379.32) * mm});
            skLineSegment(sketch, "E3030", {"start": v(-63.26, -379.32) * mm, "end": v(-74.63, -379.32) * mm});
            skLineSegment(sketch, "E3031", {"start": v(-74.63, -379.32) * mm, "end": v(-74.63, -362.33) * mm});
            skLineSegment(sketch, "E3032", {"start": v(-74.63, -362.33) * mm, "end": v(-66.51, -362.33) * mm});
            skLineSegment(sketch, "E3033", {"start": v(-66.51, -362.33) * mm, "end": v(-66.51, -353.45) * mm});
            skLineSegment(sketch, "E3034", {"start": v(-66.51, -353.45) * mm, "end": v(-74.63, -353.45) * mm});
            skLineSegment(sketch, "E3035", {"start": v(-74.63, -353.45) * mm, "end": v(-74.63, -338.08) * mm});
            skLineSegment(sketch, "E3036", {"start": v(-74.63, -338.08) * mm, "end": v(-63.26, -338.08) * mm});
            skLineSegment(sketch, "E3037", {"start": v(-63.26, -338.08) * mm, "end": v(-63.26, -328.45) * mm});
            skLineSegment(sketch, "E3038", {"start": v(48.98, -328.45) * mm, "end": v(29.6, -328.45) * mm});
            skLineSegment(sketch, "E3039", {"start": v(29.6, -328.45) * mm, "end": v(29.6, -387.98) * mm});
            skLineSegment(sketch, "E3040", {"start": v(29.6, -387.98) * mm, "end": v(48.98, -387.98) * mm});
            skLineSegment(sketch, "E3041", {"start": v(48.98, -387.98) * mm, "end": v(48.98, -379.32) * mm});
            skLineSegment(sketch, "E3042", {"start": v(48.98, -379.32) * mm, "end": v(37.72, -379.32) * mm});
            skLineSegment(sketch, "E3043", {"start": v(37.72, -379.32) * mm, "end": v(37.72, -362.33) * mm});
            skLineSegment(sketch, "E3044", {"start": v(37.72, -362.33) * mm, "end": v(45.73, -362.33) * mm});
            skLineSegment(sketch, "E3045", {"start": v(45.73, -362.33) * mm, "end": v(45.73, -353.45) * mm});
            skLineSegment(sketch, "E3046", {"start": v(45.73, -353.45) * mm, "end": v(37.72, -353.45) * mm});
            skLineSegment(sketch, "E3047", {"start": v(37.72, -353.45) * mm, "end": v(37.72, -338.08) * mm});
            skLineSegment(sketch, "E3048", {"start": v(37.72, -338.08) * mm, "end": v(48.98, -338.08) * mm});
            skLineSegment(sketch, "E3049", {"start": v(48.98, -338.08) * mm, "end": v(48.98, -328.45) * mm});
            skLineSegment(sketch, "E3050", {"start": v(113.38, -328.45) * mm, "end": v(123.88, -328.45) * mm});
            skLineSegment(sketch, "E3051", {"start": v(118.68, -343.92) * mm, "end": v(122.04, -367.2) * mm});
            skLineSegment(sketch, "E3052", {"start": v(122.04, -367.2) * mm, "end": v(115.22, -367.2) * mm});
            skLineSegment(sketch, "E3053", {"start": v(115.22, -367.2) * mm, "end": v(118.68, -343.92) * mm});
            skLineSegment(sketch, "E3054", {"start": v(123.88, -328.45) * mm, "end": v(113.38, -328.45) * mm});
            skLineSegment(sketch, "E3055", {"start": v(113.38, -328.45) * mm, "end": v(104.72, -387.98) * mm});
            skLineSegment(sketch, "E3056", {"start": v(104.72, -387.98) * mm, "end": v(112.2, -387.98) * mm});
            skLineSegment(sketch, "E3057", {"start": v(112.2, -387.98) * mm, "end": v(113.92, -376.18) * mm});
            skLineSegment(sketch, "E3058", {"start": v(113.92, -376.18) * mm, "end": v(123.34, -376.18) * mm});
            skLineSegment(sketch, "E3059", {"start": v(123.34, -376.18) * mm, "end": v(125.07, -387.98) * mm});
            skLineSegment(sketch, "E3060", {"start": v(125.07, -387.98) * mm, "end": v(132.54, -387.98) * mm});
            skLineSegment(sketch, "E3061", {"start": v(132.54, -387.98) * mm, "end": v(123.88, -328.45) * mm});
            skLineSegment(sketch, "E3062", {"start": v(184.82, -343.92) * mm, "end": v(188.17, -367.2) * mm});
            skLineSegment(sketch, "E3063", {"start": v(188.17, -367.2) * mm, "end": v(181.35, -367.2) * mm});
            skLineSegment(sketch, "E3064", {"start": v(181.35, -367.2) * mm, "end": v(184.82, -343.92) * mm});
            skLineSegment(sketch, "E3065", {"start": v(190, -328.45) * mm, "end": v(179.51, -328.45) * mm});
            skLineSegment(sketch, "E3066", {"start": v(179.51, -328.45) * mm, "end": v(170.85, -387.98) * mm});
            skLineSegment(sketch, "E3067", {"start": v(170.85, -387.98) * mm, "end": v(178.32, -387.98) * mm});
            skLineSegment(sketch, "E3068", {"start": v(178.32, -387.98) * mm, "end": v(180.05, -376.18) * mm});
            skLineSegment(sketch, "E3069", {"start": v(180.05, -376.18) * mm, "end": v(189.47, -376.18) * mm});
            skLineSegment(sketch, "E3070", {"start": v(189.47, -376.18) * mm, "end": v(191.2, -387.98) * mm});
            skLineSegment(sketch, "E3071", {"start": v(191.2, -387.98) * mm, "end": v(198.67, -387.98) * mm});
            skLineSegment(sketch, "E3072", {"start": v(198.67, -387.98) * mm, "end": v(190, -328.45) * mm});
            skLineSegment(sketch, "E3073", {"start": v(-200.18, -338.84) * mm, "end": v(-200.18, -377.15) * mm});
            skLineSegment(sketch, "E3074", {"start": v(-206.24, -377.15) * mm, "end": v(-206.24, -377.8) * mm});
            skLineSegment(sketch, "E3075", {"start": v(-206.24, -377.8) * mm, "end": v(-206.03, -378.34) * mm});
            skLineSegment(sketch, "E3076", {"start": v(-206.03, -378.34) * mm, "end": v(-205.7, -378.89) * mm});
            skLineSegment(sketch, "E3077", {"start": v(-205.7, -378.89) * mm, "end": v(-205.38, -379.32) * mm});
            skLineSegment(sketch, "E3078", {"start": v(-205.38, -379.32) * mm, "end": v(-204.95, -379.75) * mm});
            skLineSegment(sketch, "E3079", {"start": v(-204.95, -379.75) * mm, "end": v(-204.4, -379.97) * mm});
            skLineSegment(sketch, "E3080", {"start": v(-204.4, -379.97) * mm, "end": v(-203.76, -380.18) * mm});
            skLineSegment(sketch, "E3081", {"start": v(-203.76, -380.18) * mm, "end": v(-202.57, -380.18) * mm});
            skLineSegment(sketch, "E3082", {"start": v(-202.57, -380.18) * mm, "end": v(-201.48, -379.75) * mm});
            skLineSegment(sketch, "E3083", {"start": v(-201.48, -379.75) * mm, "end": v(-200.62, -378.89) * mm});
            skLineSegment(sketch, "E3084", {"start": v(-200.62, -378.89) * mm, "end": v(-200.18, -377.8) * mm});
            skLineSegment(sketch, "E3085", {"start": v(-200.18, -377.8) * mm, "end": v(-200.18, -377.15) * mm});
            skLineSegment(sketch, "E3086", {"start": v(-206.24, -377.15) * mm, "end": v(-206.24, -338.84) * mm});
            skLineSegment(sketch, "E3087", {"start": v(-200.18, -338.84) * mm, "end": v(-200.18, -338.3) * mm});
            skLineSegment(sketch, "E3088", {"start": v(-200.18, -338.3) * mm, "end": v(-200.4, -337.65) * mm});
            skLineSegment(sketch, "E3089", {"start": v(-200.4, -337.65) * mm, "end": v(-200.62, -337.21) * mm});
            skLineSegment(sketch, "E3090", {"start": v(-200.62, -337.21) * mm, "end": v(-201.05, -336.67) * mm});
            skLineSegment(sketch, "E3091", {"start": v(-201.05, -336.67) * mm, "end": v(-201.48, -336.35) * mm});
            skLineSegment(sketch, "E3092", {"start": v(-201.48, -336.35) * mm, "end": v(-202.02, -336.02) * mm});
            skLineSegment(sketch, "E3093", {"start": v(-202.02, -336.02) * mm, "end": v(-202.57, -335.91) * mm});
            skLineSegment(sketch, "E3094", {"start": v(-202.57, -335.91) * mm, "end": v(-203.21, -335.8) * mm});
            skLineSegment(sketch, "E3095", {"start": v(-203.21, -335.8) * mm, "end": v(-203.76, -335.91) * mm});
            skLineSegment(sketch, "E3096", {"start": v(-203.76, -335.91) * mm, "end": v(-204.4, -336.02) * mm});
            skLineSegment(sketch, "E3097", {"start": v(-204.4, -336.02) * mm, "end": v(-204.95, -336.35) * mm});
            skLineSegment(sketch, "E3098", {"start": v(-204.95, -336.35) * mm, "end": v(-205.38, -336.67) * mm});
            skLineSegment(sketch, "E3099", {"start": v(-205.38, -336.67) * mm, "end": v(-205.7, -337.21) * mm});
            skLineSegment(sketch, "E3100", {"start": v(-205.7, -337.21) * mm, "end": v(-206.03, -337.65) * mm});
            skLineSegment(sketch, "E3101", {"start": v(-206.03, -337.65) * mm, "end": v(-206.24, -338.3) * mm});
            skLineSegment(sketch, "E3102", {"start": v(-206.24, -338.3) * mm, "end": v(-206.24, -338.84) * mm});
            skLineSegment(sketch, "E3103", {"start": v(-214.15, -339.49) * mm, "end": v(-214.15, -376.5) * mm});
            skLineSegment(sketch, "E3104", {"start": v(-214.15, -376.5) * mm, "end": v(-214.15, -377.7) * mm});
            skLineSegment(sketch, "E3105", {"start": v(-214.15, -377.7) * mm, "end": v(-213.93, -378.89) * mm});
            skLineSegment(sketch, "E3106", {"start": v(-213.93, -378.89) * mm, "end": v(-213.6, -379.97) * mm});
            skLineSegment(sketch, "E3107", {"start": v(-213.6, -379.97) * mm, "end": v(-213.28, -381.05) * mm});
            skLineSegment(sketch, "E3108", {"start": v(-213.28, -381.05) * mm, "end": v(-212.74, -382.02) * mm});
            skLineSegment(sketch, "E3109", {"start": v(-212.74, -382.02) * mm, "end": v(-212.1, -383) * mm});
            skLineSegment(sketch, "E3110", {"start": v(-212.1, -383) * mm, "end": v(-211.33, -383.86) * mm});
            skLineSegment(sketch, "E3111", {"start": v(-211.33, -383.86) * mm, "end": v(-210.57, -384.73) * mm});
            skLineSegment(sketch, "E3112", {"start": v(-210.57, -384.73) * mm, "end": v(-209.7, -385.49) * mm});
            skLineSegment(sketch, "E3113", {"start": v(-209.7, -385.49) * mm, "end": v(-208.73, -386.03) * mm});
            skLineSegment(sketch, "E3114", {"start": v(-208.73, -386.03) * mm, "end": v(-207.65, -386.57) * mm});
            skLineSegment(sketch, "E3115", {"start": v(-207.65, -386.57) * mm, "end": v(-206.57, -387) * mm});
            skLineSegment(sketch, "E3116", {"start": v(-206.57, -387) * mm, "end": v(-205.49, -387.33) * mm});
            skLineSegment(sketch, "E3117", {"start": v(-205.49, -387.33) * mm, "end": v(-204.4, -387.44) * mm});
            skLineSegment(sketch, "E3118", {"start": v(-204.4, -387.44) * mm, "end": v(-203.21, -387.54) * mm});
            skLineSegment(sketch, "E3119", {"start": v(-203.21, -387.54) * mm, "end": v(-202.02, -387.44) * mm});
            skLineSegment(sketch, "E3120", {"start": v(-202.02, -387.44) * mm, "end": v(-200.94, -387.33) * mm});
            skLineSegment(sketch, "E3121", {"start": v(-200.94, -387.33) * mm, "end": v(-199.86, -387) * mm});
            skLineSegment(sketch, "E3122", {"start": v(-199.86, -387) * mm, "end": v(-198.78, -386.57) * mm});
            skLineSegment(sketch, "E3123", {"start": v(-198.78, -386.57) * mm, "end": v(-197.7, -386.03) * mm});
            skLineSegment(sketch, "E3124", {"start": v(-197.7, -386.03) * mm, "end": v(-196.72, -385.49) * mm});
            skLineSegment(sketch, "E3125", {"start": v(-196.72, -385.49) * mm, "end": v(-195.86, -384.73) * mm});
            skLineSegment(sketch, "E3126", {"start": v(-195.86, -384.73) * mm, "end": v(-195.1, -383.86) * mm});
            skLineSegment(sketch, "E3127", {"start": v(-195.1, -383.86) * mm, "end": v(-194.34, -383) * mm});
            skLineSegment(sketch, "E3128", {"start": v(-194.34, -383) * mm, "end": v(-193.69, -382.02) * mm});
            skLineSegment(sketch, "E3129", {"start": v(-193.69, -382.02) * mm, "end": v(-193.15, -381.05) * mm});
            skLineSegment(sketch, "E3130", {"start": v(-193.15, -381.05) * mm, "end": v(-192.72, -379.97) * mm});
            skLineSegment(sketch, "E3131", {"start": v(-192.72, -379.97) * mm, "end": v(-192.5, -378.89) * mm});
            skLineSegment(sketch, "E3132", {"start": v(-192.5, -378.89) * mm, "end": v(-192.28, -377.7) * mm});
            skLineSegment(sketch, "E3133", {"start": v(-192.28, -377.7) * mm, "end": v(-192.17, -376.5) * mm});
            skLineSegment(sketch, "E3134", {"start": v(-192.17, -376.5) * mm, "end": v(-192.17, -339.49) * mm});
            skLineSegment(sketch, "E3135", {"start": v(-192.17, -339.49) * mm, "end": v(-192.28, -338.3) * mm});
            skLineSegment(sketch, "E3136", {"start": v(-192.28, -338.3) * mm, "end": v(-192.72, -336.13) * mm});
            skLineSegment(sketch, "E3137", {"start": v(-192.72, -336.13) * mm, "end": v(-193.15, -335.05) * mm});
            skLineSegment(sketch, "E3138", {"start": v(-193.15, -335.05) * mm, "end": v(-193.69, -333.97) * mm});
            skLineSegment(sketch, "E3139", {"start": v(-193.69, -333.97) * mm, "end": v(-194.34, -333) * mm});
            skLineSegment(sketch, "E3140", {"start": v(-194.34, -333) * mm, "end": v(-195.1, -332.13) * mm});
            skLineSegment(sketch, "E3141", {"start": v(-195.1, -332.13) * mm, "end": v(-195.86, -331.37) * mm});
            skLineSegment(sketch, "E3142", {"start": v(-195.86, -331.37) * mm, "end": v(-196.72, -330.61) * mm});
            skLineSegment(sketch, "E3143", {"start": v(-196.72, -330.61) * mm, "end": v(-197.7, -329.96) * mm});
            skLineSegment(sketch, "E3144", {"start": v(-197.7, -329.96) * mm, "end": v(-198.78, -329.42) * mm});
            skLineSegment(sketch, "E3145", {"start": v(-198.78, -329.42) * mm, "end": v(-199.86, -328.99) * mm});
            skLineSegment(sketch, "E3146", {"start": v(-199.86, -328.99) * mm, "end": v(-200.94, -328.77) * mm});
            skLineSegment(sketch, "E3147", {"start": v(-200.94, -328.77) * mm, "end": v(-202.02, -328.56) * mm});
            skLineSegment(sketch, "E3148", {"start": v(-202.02, -328.56) * mm, "end": v(-203.21, -328.45) * mm});
            skLineSegment(sketch, "E3149", {"start": v(-203.21, -328.45) * mm, "end": v(-204.4, -328.56) * mm});
            skLineSegment(sketch, "E3150", {"start": v(-204.4, -328.56) * mm, "end": v(-205.49, -328.77) * mm});
            skLineSegment(sketch, "E3151", {"start": v(-205.49, -328.77) * mm, "end": v(-206.57, -328.99) * mm});
            skLineSegment(sketch, "E3152", {"start": v(-206.57, -328.99) * mm, "end": v(-207.65, -329.42) * mm});
            skLineSegment(sketch, "E3153", {"start": v(-207.65, -329.42) * mm, "end": v(-208.73, -329.96) * mm});
            skLineSegment(sketch, "E3154", {"start": v(-208.73, -329.96) * mm, "end": v(-209.7, -330.61) * mm});
            skLineSegment(sketch, "E3155", {"start": v(-209.7, -330.61) * mm, "end": v(-210.57, -331.37) * mm});
            skLineSegment(sketch, "E3156", {"start": v(-210.57, -331.37) * mm, "end": v(-211.33, -332.13) * mm});
            skLineSegment(sketch, "E3157", {"start": v(-211.33, -332.13) * mm, "end": v(-212.1, -333) * mm});
            skLineSegment(sketch, "E3158", {"start": v(-212.1, -333) * mm, "end": v(-212.74, -333.97) * mm});
            skLineSegment(sketch, "E3159", {"start": v(-212.74, -333.97) * mm, "end": v(-213.28, -335.05) * mm});
            skLineSegment(sketch, "E3160", {"start": v(-213.28, -335.05) * mm, "end": v(-213.6, -336.13) * mm});
            skLineSegment(sketch, "E3161", {"start": v(-213.6, -336.13) * mm, "end": v(-213.93, -337.21) * mm});
            skLineSegment(sketch, "E3162", {"start": v(-213.93, -337.21) * mm, "end": v(-214.15, -338.3) * mm});
            skLineSegment(sketch, "E3163", {"start": v(-214.15, -338.3) * mm, "end": v(-214.15, -339.49) * mm});
            skLineSegment(sketch, "E3164", {"start": v(222.16, -338.84) * mm, "end": v(222.16, -377.15) * mm});
            skLineSegment(sketch, "E3165", {"start": v(216.1, -377.15) * mm, "end": v(216.1, -377.8) * mm});
            skLineSegment(sketch, "E3166", {"start": v(216.1, -377.8) * mm, "end": v(216.53, -378.89) * mm});
            skLineSegment(sketch, "E3167", {"start": v(216.53, -378.89) * mm, "end": v(217.4, -379.75) * mm});
            skLineSegment(sketch, "E3168", {"start": v(217.4, -379.75) * mm, "end": v(217.94, -379.97) * mm});
            skLineSegment(sketch, "E3169", {"start": v(217.94, -379.97) * mm, "end": v(218.47, -380.18) * mm});
            skLineSegment(sketch, "E3170", {"start": v(218.47, -380.18) * mm, "end": v(219.67, -380.18) * mm});
            skLineSegment(sketch, "E3171", {"start": v(219.67, -380.18) * mm, "end": v(220.32, -379.97) * mm});
            skLineSegment(sketch, "E3172", {"start": v(220.32, -379.97) * mm, "end": v(220.75, -379.75) * mm});
            skLineSegment(sketch, "E3173", {"start": v(220.75, -379.75) * mm, "end": v(221.29, -379.32) * mm});
            skLineSegment(sketch, "E3174", {"start": v(221.29, -379.32) * mm, "end": v(221.61, -378.89) * mm});
            skLineSegment(sketch, "E3175", {"start": v(221.61, -378.89) * mm, "end": v(221.94, -378.34) * mm});
            skLineSegment(sketch, "E3176", {"start": v(221.94, -378.34) * mm, "end": v(222.05, -377.8) * mm});
            skLineSegment(sketch, "E3177", {"start": v(222.05, -377.8) * mm, "end": v(222.16, -377.15) * mm});
            skLineSegment(sketch, "E3178", {"start": v(216.1, -377.15) * mm, "end": v(216.1, -338.84) * mm});
            skLineSegment(sketch, "E3179", {"start": v(222.16, -338.84) * mm, "end": v(222.05, -338.3) * mm});
            skLineSegment(sketch, "E3180", {"start": v(222.05, -338.3) * mm, "end": v(221.94, -337.65) * mm});
            skLineSegment(sketch, "E3181", {"start": v(221.94, -337.65) * mm, "end": v(221.61, -337.21) * mm});
            skLineSegment(sketch, "E3182", {"start": v(221.61, -337.21) * mm, "end": v(221.29, -336.67) * mm});
            skLineSegment(sketch, "E3183", {"start": v(221.29, -336.67) * mm, "end": v(220.75, -336.35) * mm});
            skLineSegment(sketch, "E3184", {"start": v(220.75, -336.35) * mm, "end": v(220.32, -336.02) * mm});
            skLineSegment(sketch, "E3185", {"start": v(220.32, -336.02) * mm, "end": v(219.67, -335.91) * mm});
            skLineSegment(sketch, "E3186", {"start": v(219.67, -335.91) * mm, "end": v(219.13, -335.8) * mm});
            skLineSegment(sketch, "E3187", {"start": v(219.13, -335.8) * mm, "end": v(218.47, -335.91) * mm});
            skLineSegment(sketch, "E3188", {"start": v(218.47, -335.91) * mm, "end": v(217.94, -336.02) * mm});
            skLineSegment(sketch, "E3189", {"start": v(217.94, -336.02) * mm, "end": v(217.4, -336.35) * mm});
            skLineSegment(sketch, "E3190", {"start": v(217.4, -336.35) * mm, "end": v(216.96, -336.67) * mm});
            skLineSegment(sketch, "E3191", {"start": v(216.96, -336.67) * mm, "end": v(216.53, -337.21) * mm});
            skLineSegment(sketch, "E3192", {"start": v(216.53, -337.21) * mm, "end": v(216.31, -337.65) * mm});
            skLineSegment(sketch, "E3193", {"start": v(216.31, -337.65) * mm, "end": v(216.1, -338.3) * mm});
            skLineSegment(sketch, "E3194", {"start": v(216.1, -338.3) * mm, "end": v(216.1, -338.84) * mm});
            skLineSegment(sketch, "E3195", {"start": v(208.09, -339.49) * mm, "end": v(208.09, -376.5) * mm});
            skLineSegment(sketch, "E3196", {"start": v(208.09, -376.5) * mm, "end": v(208.2, -377.7) * mm});
            skLineSegment(sketch, "E3197", {"start": v(208.2, -377.7) * mm, "end": v(208.41, -378.89) * mm});
            skLineSegment(sketch, "E3198", {"start": v(208.41, -378.89) * mm, "end": v(208.63, -379.97) * mm});
            skLineSegment(sketch, "E3199", {"start": v(208.63, -379.97) * mm, "end": v(209.06, -381.05) * mm});
            skLineSegment(sketch, "E3200", {"start": v(209.06, -381.05) * mm, "end": v(209.6, -382.02) * mm});
            skLineSegment(sketch, "E3201", {"start": v(209.6, -382.02) * mm, "end": v(210.25, -383) * mm});
            skLineSegment(sketch, "E3202", {"start": v(210.25, -383) * mm, "end": v(210.9, -383.86) * mm});
            skLineSegment(sketch, "E3203", {"start": v(210.9, -383.86) * mm, "end": v(211.77, -384.73) * mm});
            skLineSegment(sketch, "E3204", {"start": v(211.77, -384.73) * mm, "end": v(212.63, -385.49) * mm});
            skLineSegment(sketch, "E3205", {"start": v(212.63, -385.49) * mm, "end": v(213.6, -386.03) * mm});
            skLineSegment(sketch, "E3206", {"start": v(213.6, -386.03) * mm, "end": v(214.69, -386.57) * mm});
            skLineSegment(sketch, "E3207", {"start": v(214.69, -386.57) * mm, "end": v(215.66, -387) * mm});
            skLineSegment(sketch, "E3208", {"start": v(215.66, -387) * mm, "end": v(216.85, -387.33) * mm});
            skLineSegment(sketch, "E3209", {"start": v(216.85, -387.33) * mm, "end": v(217.94, -387.44) * mm});
            skLineSegment(sketch, "E3210", {"start": v(217.94, -387.44) * mm, "end": v(219.13, -387.54) * mm});
            skLineSegment(sketch, "E3211", {"start": v(219.13, -387.54) * mm, "end": v(220.2, -387.44) * mm});
            skLineSegment(sketch, "E3212", {"start": v(220.2, -387.44) * mm, "end": v(221.4, -387.33) * mm});
            skLineSegment(sketch, "E3213", {"start": v(221.4, -387.33) * mm, "end": v(222.48, -387) * mm});
            skLineSegment(sketch, "E3214", {"start": v(222.48, -387) * mm, "end": v(223.56, -386.57) * mm});
            skLineSegment(sketch, "E3215", {"start": v(223.56, -386.57) * mm, "end": v(224.64, -386.03) * mm});
            skLineSegment(sketch, "E3216", {"start": v(224.64, -386.03) * mm, "end": v(225.51, -385.49) * mm});
            skLineSegment(sketch, "E3217", {"start": v(225.51, -385.49) * mm, "end": v(226.49, -384.73) * mm});
            skLineSegment(sketch, "E3218", {"start": v(226.49, -384.73) * mm, "end": v(227.25, -383.86) * mm});
            skLineSegment(sketch, "E3219", {"start": v(227.25, -383.86) * mm, "end": v(228, -383) * mm});
            skLineSegment(sketch, "E3220", {"start": v(228, -383) * mm, "end": v(228.65, -382.02) * mm});
            skLineSegment(sketch, "E3221", {"start": v(228.65, -382.02) * mm, "end": v(229.09, -381.05) * mm});
            skLineSegment(sketch, "E3222", {"start": v(229.09, -381.05) * mm, "end": v(229.52, -379.97) * mm});
            skLineSegment(sketch, "E3223", {"start": v(229.52, -379.97) * mm, "end": v(229.84, -378.89) * mm});
            skLineSegment(sketch, "E3224", {"start": v(229.84, -378.89) * mm, "end": v(230.06, -377.7) * mm});
            skLineSegment(sketch, "E3225", {"start": v(230.06, -377.7) * mm, "end": v(230.06, -376.5) * mm});
            skLineSegment(sketch, "E3226", {"start": v(230.06, -376.5) * mm, "end": v(230.06, -339.49) * mm});
            skLineSegment(sketch, "E3227", {"start": v(230.06, -339.49) * mm, "end": v(230.06, -338.3) * mm});
            skLineSegment(sketch, "E3228", {"start": v(230.06, -338.3) * mm, "end": v(229.84, -337.21) * mm});
            skLineSegment(sketch, "E3229", {"start": v(229.84, -337.21) * mm, "end": v(229.52, -336.13) * mm});
            skLineSegment(sketch, "E3230", {"start": v(229.52, -336.13) * mm, "end": v(229.09, -335.05) * mm});
            skLineSegment(sketch, "E3231", {"start": v(229.09, -335.05) * mm, "end": v(228.65, -333.97) * mm});
            skLineSegment(sketch, "E3232", {"start": v(228.65, -333.97) * mm, "end": v(228, -333) * mm});
            skLineSegment(sketch, "E3233", {"start": v(228, -333) * mm, "end": v(227.25, -332.13) * mm});
            skLineSegment(sketch, "E3234", {"start": v(227.25, -332.13) * mm, "end": v(226.49, -331.37) * mm});
            skLineSegment(sketch, "E3235", {"start": v(226.49, -331.37) * mm, "end": v(225.51, -330.61) * mm});
            skLineSegment(sketch, "E3236", {"start": v(225.51, -330.61) * mm, "end": v(224.64, -329.96) * mm});
            skLineSegment(sketch, "E3237", {"start": v(224.64, -329.96) * mm, "end": v(223.56, -329.42) * mm});
            skLineSegment(sketch, "E3238", {"start": v(223.56, -329.42) * mm, "end": v(222.48, -328.99) * mm});
            skLineSegment(sketch, "E3239", {"start": v(222.48, -328.99) * mm, "end": v(221.4, -328.77) * mm});
            skLineSegment(sketch, "E3240", {"start": v(221.4, -328.77) * mm, "end": v(220.2, -328.56) * mm});
            skLineSegment(sketch, "E3241", {"start": v(220.2, -328.56) * mm, "end": v(219.13, -328.45) * mm});
            skLineSegment(sketch, "E3242", {"start": v(219.13, -328.45) * mm, "end": v(217.94, -328.56) * mm});
            skLineSegment(sketch, "E3243", {"start": v(217.94, -328.56) * mm, "end": v(216.85, -328.77) * mm});
            skLineSegment(sketch, "E3244", {"start": v(216.85, -328.77) * mm, "end": v(215.66, -328.99) * mm});
            skLineSegment(sketch, "E3245", {"start": v(215.66, -328.99) * mm, "end": v(214.69, -329.42) * mm});
            skLineSegment(sketch, "E3246", {"start": v(214.69, -329.42) * mm, "end": v(213.6, -329.96) * mm});
            skLineSegment(sketch, "E3247", {"start": v(213.6, -329.96) * mm, "end": v(212.63, -330.61) * mm});
            skLineSegment(sketch, "E3248", {"start": v(212.63, -330.61) * mm, "end": v(211.77, -331.37) * mm});
            skLineSegment(sketch, "E3249", {"start": v(211.77, -331.37) * mm, "end": v(210.9, -332.13) * mm});
            skLineSegment(sketch, "E3250", {"start": v(210.9, -332.13) * mm, "end": v(210.25, -333) * mm});
            skLineSegment(sketch, "E3251", {"start": v(210.25, -333) * mm, "end": v(209.6, -333.97) * mm});
            skLineSegment(sketch, "E3252", {"start": v(209.6, -333.97) * mm, "end": v(209.06, -335.05) * mm});
            skLineSegment(sketch, "E3253", {"start": v(209.06, -335.05) * mm, "end": v(208.63, -336.13) * mm});
            skLineSegment(sketch, "E3254", {"start": v(208.63, -336.13) * mm, "end": v(208.2, -338.3) * mm});
            skLineSegment(sketch, "E3255", {"start": v(208.2, -338.3) * mm, "end": v(208.09, -339.49) * mm});
            skLineSegment(sketch, "E3256", {"start": v(75.39, -376.5) * mm, "end": v(75.5, -377.7) * mm});
            skLineSegment(sketch, "E3257", {"start": v(75.5, -377.7) * mm, "end": v(75.6, -378.89) * mm});
            skLineSegment(sketch, "E3258", {"start": v(75.6, -378.89) * mm, "end": v(75.93, -379.97) * mm});
            skLineSegment(sketch, "E3259", {"start": v(75.93, -379.97) * mm, "end": v(76.36, -381.05) * mm});
            skLineSegment(sketch, "E3260", {"start": v(76.36, -381.05) * mm, "end": v(76.9, -382.02) * mm});
            skLineSegment(sketch, "E3261", {"start": v(76.9, -382.02) * mm, "end": v(77.55, -383) * mm});
            skLineSegment(sketch, "E3262", {"start": v(77.55, -383) * mm, "end": v(78.2, -383.86) * mm});
            skLineSegment(sketch, "E3263", {"start": v(78.2, -383.86) * mm, "end": v(79.07, -384.73) * mm});
            skLineSegment(sketch, "E3264", {"start": v(79.07, -384.73) * mm, "end": v(79.94, -385.49) * mm});
            skLineSegment(sketch, "E3265", {"start": v(79.94, -385.49) * mm, "end": v(80.9, -386.03) * mm});
            skLineSegment(sketch, "E3266", {"start": v(80.9, -386.03) * mm, "end": v(81.88, -386.57) * mm});
            skLineSegment(sketch, "E3267", {"start": v(81.88, -386.57) * mm, "end": v(82.97, -387) * mm});
            skLineSegment(sketch, "E3268", {"start": v(82.97, -387) * mm, "end": v(84.15, -387.33) * mm});
            skLineSegment(sketch, "E3269", {"start": v(84.15, -387.33) * mm, "end": v(85.24, -387.44) * mm});
            skLineSegment(sketch, "E3270", {"start": v(85.24, -387.44) * mm, "end": v(86.43, -387.54) * mm});
            skLineSegment(sketch, "E3271", {"start": v(86.43, -387.54) * mm, "end": v(87.5, -387.44) * mm});
            skLineSegment(sketch, "E3272", {"start": v(87.5, -387.44) * mm, "end": v(88.7, -387.33) * mm});
            skLineSegment(sketch, "E3273", {"start": v(88.7, -387.33) * mm, "end": v(89.78, -387) * mm});
            skLineSegment(sketch, "E3274", {"start": v(89.78, -387) * mm, "end": v(90.86, -386.57) * mm});
            skLineSegment(sketch, "E3275", {"start": v(90.86, -386.57) * mm, "end": v(91.84, -386.03) * mm});
            skLineSegment(sketch, "E3276", {"start": v(91.84, -386.03) * mm, "end": v(92.82, -385.49) * mm});
            skLineSegment(sketch, "E3277", {"start": v(92.82, -385.49) * mm, "end": v(93.79, -384.73) * mm});
            skLineSegment(sketch, "E3278", {"start": v(93.79, -384.73) * mm, "end": v(94.54, -383.86) * mm});
            skLineSegment(sketch, "E3279", {"start": v(94.54, -383.86) * mm, "end": v(95.3, -383) * mm});
            skLineSegment(sketch, "E3280", {"start": v(95.3, -383) * mm, "end": v(95.95, -382.02) * mm});
            skLineSegment(sketch, "E3281", {"start": v(95.95, -382.02) * mm, "end": v(96.38, -381.05) * mm});
            skLineSegment(sketch, "E3282", {"start": v(96.38, -381.05) * mm, "end": v(96.82, -379.97) * mm});
            skLineSegment(sketch, "E3283", {"start": v(96.82, -379.97) * mm, "end": v(97.14, -378.89) * mm});
            skLineSegment(sketch, "E3284", {"start": v(97.14, -378.89) * mm, "end": v(97.36, -377.7) * mm});
            skLineSegment(sketch, "E3285", {"start": v(97.36, -377.7) * mm, "end": v(97.36, -376.5) * mm});
            skLineSegment(sketch, "E3286", {"start": v(97.36, -376.5) * mm, "end": v(97.36, -367.3) * mm});
            skLineSegment(sketch, "E3287", {"start": v(97.36, -367.3) * mm, "end": v(89.46, -367.3) * mm});
            skLineSegment(sketch, "E3288", {"start": v(89.46, -367.3) * mm, "end": v(89.46, -377.15) * mm});
            skLineSegment(sketch, "E3289", {"start": v(83.29, -377.15) * mm, "end": v(83.4, -377.8) * mm});
            skLineSegment(sketch, "E3290", {"start": v(83.4, -377.8) * mm, "end": v(83.62, -378.34) * mm});
            skLineSegment(sketch, "E3291", {"start": v(83.62, -378.34) * mm, "end": v(83.83, -378.89) * mm});
            skLineSegment(sketch, "E3292", {"start": v(83.83, -378.89) * mm, "end": v(84.7, -379.75) * mm});
            skLineSegment(sketch, "E3293", {"start": v(84.7, -379.75) * mm, "end": v(85.24, -379.97) * mm});
            skLineSegment(sketch, "E3294", {"start": v(85.24, -379.97) * mm, "end": v(85.78, -380.18) * mm});
            skLineSegment(sketch, "E3295", {"start": v(85.78, -380.18) * mm, "end": v(86.97, -380.18) * mm});
            skLineSegment(sketch, "E3296", {"start": v(86.97, -380.18) * mm, "end": v(88.05, -379.75) * mm});
            skLineSegment(sketch, "E3297", {"start": v(88.05, -379.75) * mm, "end": v(88.6, -379.32) * mm});
            skLineSegment(sketch, "E3298", {"start": v(88.6, -379.32) * mm, "end": v(88.92, -378.89) * mm});
            skLineSegment(sketch, "E3299", {"start": v(88.92, -378.89) * mm, "end": v(89.24, -378.34) * mm});
            skLineSegment(sketch, "E3300", {"start": v(89.24, -378.34) * mm, "end": v(89.35, -377.8) * mm});
            skLineSegment(sketch, "E3301", {"start": v(89.35, -377.8) * mm, "end": v(89.46, -377.15) * mm});
            skLineSegment(sketch, "E3302", {"start": v(83.29, -377.15) * mm, "end": v(83.29, -338.84) * mm});
            skLineSegment(sketch, "E3303", {"start": v(89.46, -338.84) * mm, "end": v(89.35, -338.3) * mm});
            skLineSegment(sketch, "E3304", {"start": v(89.35, -338.3) * mm, "end": v(89.24, -337.65) * mm});
            skLineSegment(sketch, "E3305", {"start": v(89.24, -337.65) * mm, "end": v(88.92, -337.21) * mm});
            skLineSegment(sketch, "E3306", {"start": v(88.92, -337.21) * mm, "end": v(88.6, -336.67) * mm});
            skLineSegment(sketch, "E3307", {"start": v(88.6, -336.67) * mm, "end": v(88.05, -336.35) * mm});
            skLineSegment(sketch, "E3308", {"start": v(88.05, -336.35) * mm, "end": v(87.5, -336.02) * mm});
            skLineSegment(sketch, "E3309", {"start": v(87.5, -336.02) * mm, "end": v(86.97, -335.91) * mm});
            skLineSegment(sketch, "E3310", {"start": v(86.97, -335.91) * mm, "end": v(86.43, -335.8) * mm});
            skLineSegment(sketch, "E3311", {"start": v(86.43, -335.8) * mm, "end": v(85.78, -335.91) * mm});
            skLineSegment(sketch, "E3312", {"start": v(85.78, -335.91) * mm, "end": v(85.24, -336.02) * mm});
            skLineSegment(sketch, "E3313", {"start": v(85.24, -336.02) * mm, "end": v(84.7, -336.35) * mm});
            skLineSegment(sketch, "E3314", {"start": v(84.7, -336.35) * mm, "end": v(84.26, -336.67) * mm});
            skLineSegment(sketch, "E3315", {"start": v(84.26, -336.67) * mm, "end": v(83.83, -337.21) * mm});
            skLineSegment(sketch, "E3316", {"start": v(83.83, -337.21) * mm, "end": v(83.62, -337.65) * mm});
            skLineSegment(sketch, "E3317", {"start": v(83.62, -337.65) * mm, "end": v(83.4, -338.3) * mm});
            skLineSegment(sketch, "E3318", {"start": v(83.4, -338.3) * mm, "end": v(83.29, -338.84) * mm});
            skLineSegment(sketch, "E3319", {"start": v(89.46, -338.84) * mm, "end": v(89.46, -348.69) * mm});
            skLineSegment(sketch, "E3320", {"start": v(89.46, -348.69) * mm, "end": v(97.36, -348.69) * mm});
            skLineSegment(sketch, "E3321", {"start": v(97.36, -348.69) * mm, "end": v(97.36, -339.49) * mm});
            skLineSegment(sketch, "E3322", {"start": v(97.36, -339.49) * mm, "end": v(97.36, -338.3) * mm});
            skLineSegment(sketch, "E3323", {"start": v(97.36, -338.3) * mm, "end": v(97.14, -337.21) * mm});
            skLineSegment(sketch, "E3324", {"start": v(97.14, -337.21) * mm, "end": v(96.82, -336.13) * mm});
            skLineSegment(sketch, "E3325", {"start": v(96.82, -336.13) * mm, "end": v(96.38, -335.05) * mm});
            skLineSegment(sketch, "E3326", {"start": v(96.38, -335.05) * mm, "end": v(95.95, -333.97) * mm});
            skLineSegment(sketch, "E3327", {"start": v(95.95, -333.97) * mm, "end": v(95.3, -333) * mm});
            skLineSegment(sketch, "E3328", {"start": v(95.3, -333) * mm, "end": v(94.54, -332.13) * mm});
            skLineSegment(sketch, "E3329", {"start": v(94.54, -332.13) * mm, "end": v(93.79, -331.37) * mm});
            skLineSegment(sketch, "E3330", {"start": v(93.79, -331.37) * mm, "end": v(92.82, -330.61) * mm});
            skLineSegment(sketch, "E3331", {"start": v(92.82, -330.61) * mm, "end": v(91.84, -329.96) * mm});
            skLineSegment(sketch, "E3332", {"start": v(91.84, -329.96) * mm, "end": v(90.86, -329.42) * mm});
            skLineSegment(sketch, "E3333", {"start": v(90.86, -329.42) * mm, "end": v(89.78, -328.99) * mm});
            skLineSegment(sketch, "E3334", {"start": v(89.78, -328.99) * mm, "end": v(88.7, -328.77) * mm});
            skLineSegment(sketch, "E3335", {"start": v(88.7, -328.77) * mm, "end": v(87.5, -328.56) * mm});
            skLineSegment(sketch, "E3336", {"start": v(87.5, -328.56) * mm, "end": v(86.43, -328.45) * mm});
            skLineSegment(sketch, "E3337", {"start": v(86.43, -328.45) * mm, "end": v(85.24, -328.56) * mm});
            skLineSegment(sketch, "E3338", {"start": v(85.24, -328.56) * mm, "end": v(84.15, -328.77) * mm});
            skLineSegment(sketch, "E3339", {"start": v(84.15, -328.77) * mm, "end": v(82.97, -328.99) * mm});
            skLineSegment(sketch, "E3340", {"start": v(82.97, -328.99) * mm, "end": v(81.88, -329.42) * mm});
            skLineSegment(sketch, "E3341", {"start": v(81.88, -329.42) * mm, "end": v(80.9, -329.96) * mm});
            skLineSegment(sketch, "E3342", {"start": v(80.9, -329.96) * mm, "end": v(79.94, -330.61) * mm});
            skLineSegment(sketch, "E3343", {"start": v(79.94, -330.61) * mm, "end": v(79.07, -331.37) * mm});
            skLineSegment(sketch, "E3344", {"start": v(79.07, -331.37) * mm, "end": v(78.2, -332.13) * mm});
            skLineSegment(sketch, "E3345", {"start": v(78.2, -332.13) * mm, "end": v(77.55, -333) * mm});
            skLineSegment(sketch, "E3346", {"start": v(77.55, -333) * mm, "end": v(76.9, -333.97) * mm});
            skLineSegment(sketch, "E3347", {"start": v(76.9, -333.97) * mm, "end": v(76.36, -335.05) * mm});
            skLineSegment(sketch, "E3348", {"start": v(76.36, -335.05) * mm, "end": v(75.93, -336.13) * mm});
            skLineSegment(sketch, "E3349", {"start": v(75.93, -336.13) * mm, "end": v(75.6, -337.21) * mm});
            skLineSegment(sketch, "E3350", {"start": v(75.6, -337.21) * mm, "end": v(75.5, -338.3) * mm});
            skLineSegment(sketch, "E3351", {"start": v(75.5, -338.3) * mm, "end": v(75.39, -339.49) * mm});
            skLineSegment(sketch, "E3352", {"start": v(75.39, -339.49) * mm, "end": v(75.39, -376.5) * mm});
            skLineSegment(sketch, "E3353", {"start": v(141.63, -376.5) * mm, "end": v(141.74, -377.7) * mm});
            skLineSegment(sketch, "E3354", {"start": v(141.74, -377.7) * mm, "end": v(141.95, -378.89) * mm});
            skLineSegment(sketch, "E3355", {"start": v(141.95, -378.89) * mm, "end": v(142.17, -379.97) * mm});
            skLineSegment(sketch, "E3356", {"start": v(142.17, -379.97) * mm, "end": v(142.6, -381.05) * mm});
            skLineSegment(sketch, "E3357", {"start": v(142.6, -381.05) * mm, "end": v(143.15, -382.02) * mm});
            skLineSegment(sketch, "E3358", {"start": v(143.15, -382.02) * mm, "end": v(143.8, -383) * mm});
            skLineSegment(sketch, "E3359", {"start": v(143.8, -383) * mm, "end": v(144.44, -383.86) * mm});
            skLineSegment(sketch, "E3360", {"start": v(144.44, -383.86) * mm, "end": v(145.3, -384.73) * mm});
            skLineSegment(sketch, "E3361", {"start": v(145.3, -384.73) * mm, "end": v(146.18, -385.49) * mm});
            skLineSegment(sketch, "E3362", {"start": v(146.18, -385.49) * mm, "end": v(147.15, -386.03) * mm});
            skLineSegment(sketch, "E3363", {"start": v(147.15, -386.03) * mm, "end": v(148.23, -386.57) * mm});
            skLineSegment(sketch, "E3364", {"start": v(148.23, -386.57) * mm, "end": v(149.2, -387) * mm});
            skLineSegment(sketch, "E3365", {"start": v(149.2, -387) * mm, "end": v(150.4, -387.33) * mm});
            skLineSegment(sketch, "E3366", {"start": v(150.4, -387.33) * mm, "end": v(151.48, -387.44) * mm});
            skLineSegment(sketch, "E3367", {"start": v(151.48, -387.44) * mm, "end": v(152.67, -387.54) * mm});
            skLineSegment(sketch, "E3368", {"start": v(152.67, -387.54) * mm, "end": v(153.75, -387.44) * mm});
            skLineSegment(sketch, "E3369", {"start": v(153.75, -387.44) * mm, "end": v(154.94, -387.33) * mm});
            skLineSegment(sketch, "E3370", {"start": v(154.94, -387.33) * mm, "end": v(156.02, -387) * mm});
            skLineSegment(sketch, "E3371", {"start": v(156.02, -387) * mm, "end": v(157.1, -386.57) * mm});
            skLineSegment(sketch, "E3372", {"start": v(157.1, -386.57) * mm, "end": v(158.19, -386.03) * mm});
            skLineSegment(sketch, "E3373", {"start": v(158.19, -386.03) * mm, "end": v(159.06, -385.49) * mm});
            skLineSegment(sketch, "E3374", {"start": v(159.06, -385.49) * mm, "end": v(160.03, -384.73) * mm});
            skLineSegment(sketch, "E3375", {"start": v(160.03, -384.73) * mm, "end": v(160.79, -383.86) * mm});
            skLineSegment(sketch, "E3376", {"start": v(160.79, -383.86) * mm, "end": v(161.54, -383) * mm});
            skLineSegment(sketch, "E3377", {"start": v(161.54, -383) * mm, "end": v(162.2, -382.02) * mm});
            skLineSegment(sketch, "E3378", {"start": v(162.2, -382.02) * mm, "end": v(162.74, -381.05) * mm});
            skLineSegment(sketch, "E3379", {"start": v(162.74, -381.05) * mm, "end": v(163.06, -379.97) * mm});
            skLineSegment(sketch, "E3380", {"start": v(163.06, -379.97) * mm, "end": v(163.38, -378.89) * mm});
            skLineSegment(sketch, "E3381", {"start": v(163.38, -378.89) * mm, "end": v(163.6, -377.7) * mm});
            skLineSegment(sketch, "E3382", {"start": v(163.6, -377.7) * mm, "end": v(163.6, -376.5) * mm});
            skLineSegment(sketch, "E3383", {"start": v(163.6, -376.5) * mm, "end": v(163.6, -367.3) * mm});
            skLineSegment(sketch, "E3384", {"start": v(163.6, -367.3) * mm, "end": v(155.7, -367.3) * mm});
            skLineSegment(sketch, "E3385", {"start": v(155.7, -367.3) * mm, "end": v(155.7, -377.15) * mm});
            skLineSegment(sketch, "E3386", {"start": v(149.64, -377.15) * mm, "end": v(149.64, -377.8) * mm});
            skLineSegment(sketch, "E3387", {"start": v(149.64, -377.8) * mm, "end": v(149.86, -378.34) * mm});
            skLineSegment(sketch, "E3388", {"start": v(149.86, -378.34) * mm, "end": v(150.07, -378.89) * mm});
            skLineSegment(sketch, "E3389", {"start": v(150.07, -378.89) * mm, "end": v(150.94, -379.75) * mm});
            skLineSegment(sketch, "E3390", {"start": v(150.94, -379.75) * mm, "end": v(151.48, -379.97) * mm});
            skLineSegment(sketch, "E3391", {"start": v(151.48, -379.97) * mm, "end": v(152.02, -380.18) * mm});
            skLineSegment(sketch, "E3392", {"start": v(152.02, -380.18) * mm, "end": v(153.21, -380.18) * mm});
            skLineSegment(sketch, "E3393", {"start": v(153.21, -380.18) * mm, "end": v(153.86, -379.97) * mm});
            skLineSegment(sketch, "E3394", {"start": v(153.86, -379.97) * mm, "end": v(154.3, -379.75) * mm});
            skLineSegment(sketch, "E3395", {"start": v(154.3, -379.75) * mm, "end": v(154.83, -379.32) * mm});
            skLineSegment(sketch, "E3396", {"start": v(154.83, -379.32) * mm, "end": v(155.16, -378.89) * mm});
            skLineSegment(sketch, "E3397", {"start": v(155.16, -378.89) * mm, "end": v(155.48, -378.34) * mm});
            skLineSegment(sketch, "E3398", {"start": v(155.48, -378.34) * mm, "end": v(155.6, -377.8) * mm});
            skLineSegment(sketch, "E3399", {"start": v(155.6, -377.8) * mm, "end": v(155.7, -377.15) * mm});
            skLineSegment(sketch, "E3400", {"start": v(149.64, -377.15) * mm, "end": v(149.64, -338.84) * mm});
            skLineSegment(sketch, "E3401", {"start": v(155.7, -338.84) * mm, "end": v(155.6, -338.3) * mm});
            skLineSegment(sketch, "E3402", {"start": v(155.6, -338.3) * mm, "end": v(155.48, -337.65) * mm});
            skLineSegment(sketch, "E3403", {"start": v(155.48, -337.65) * mm, "end": v(155.16, -337.21) * mm});
            skLineSegment(sketch, "E3404", {"start": v(155.16, -337.21) * mm, "end": v(154.83, -336.67) * mm});
            skLineSegment(sketch, "E3405", {"start": v(154.83, -336.67) * mm, "end": v(154.3, -336.35) * mm});
            skLineSegment(sketch, "E3406", {"start": v(154.3, -336.35) * mm, "end": v(153.86, -336.02) * mm});
            skLineSegment(sketch, "E3407", {"start": v(153.86, -336.02) * mm, "end": v(153.21, -335.91) * mm});
            skLineSegment(sketch, "E3408", {"start": v(153.21, -335.91) * mm, "end": v(152.67, -335.8) * mm});
            skLineSegment(sketch, "E3409", {"start": v(152.67, -335.8) * mm, "end": v(152.02, -335.91) * mm});
            skLineSegment(sketch, "E3410", {"start": v(152.02, -335.91) * mm, "end": v(151.48, -336.02) * mm});
            skLineSegment(sketch, "E3411", {"start": v(151.48, -336.02) * mm, "end": v(150.94, -336.35) * mm});
            skLineSegment(sketch, "E3412", {"start": v(150.94, -336.35) * mm, "end": v(150.5, -336.67) * mm});
            skLineSegment(sketch, "E3413", {"start": v(150.5, -336.67) * mm, "end": v(150.07, -337.21) * mm});
            skLineSegment(sketch, "E3414", {"start": v(150.07, -337.21) * mm, "end": v(149.86, -337.65) * mm});
            skLineSegment(sketch, "E3415", {"start": v(149.86, -337.65) * mm, "end": v(149.64, -338.3) * mm});
            skLineSegment(sketch, "E3416", {"start": v(149.64, -338.3) * mm, "end": v(149.64, -338.84) * mm});
            skLineSegment(sketch, "E3417", {"start": v(155.7, -338.84) * mm, "end": v(155.7, -348.69) * mm});
            skLineSegment(sketch, "E3418", {"start": v(155.7, -348.69) * mm, "end": v(163.6, -348.69) * mm});
            skLineSegment(sketch, "E3419", {"start": v(163.6, -348.69) * mm, "end": v(163.6, -339.49) * mm});
            skLineSegment(sketch, "E3420", {"start": v(163.6, -339.49) * mm, "end": v(163.6, -338.3) * mm});
            skLineSegment(sketch, "E3421", {"start": v(163.6, -338.3) * mm, "end": v(163.38, -337.21) * mm});
            skLineSegment(sketch, "E3422", {"start": v(163.38, -337.21) * mm, "end": v(163.06, -336.13) * mm});
            skLineSegment(sketch, "E3423", {"start": v(163.06, -336.13) * mm, "end": v(162.74, -335.05) * mm});
            skLineSegment(sketch, "E3424", {"start": v(162.74, -335.05) * mm, "end": v(162.2, -333.97) * mm});
            skLineSegment(sketch, "E3425", {"start": v(162.2, -333.97) * mm, "end": v(161.54, -333) * mm});
            skLineSegment(sketch, "E3426", {"start": v(161.54, -333) * mm, "end": v(160.79, -332.13) * mm});
            skLineSegment(sketch, "E3427", {"start": v(160.79, -332.13) * mm, "end": v(160.03, -331.37) * mm});
            skLineSegment(sketch, "E3428", {"start": v(160.03, -331.37) * mm, "end": v(159.06, -330.61) * mm});
            skLineSegment(sketch, "E3429", {"start": v(159.06, -330.61) * mm, "end": v(158.19, -329.96) * mm});
            skLineSegment(sketch, "E3430", {"start": v(158.19, -329.96) * mm, "end": v(157.1, -329.42) * mm});
            skLineSegment(sketch, "E3431", {"start": v(157.1, -329.42) * mm, "end": v(156.02, -328.99) * mm});
            skLineSegment(sketch, "E3432", {"start": v(156.02, -328.99) * mm, "end": v(154.94, -328.77) * mm});
            skLineSegment(sketch, "E3433", {"start": v(154.94, -328.77) * mm, "end": v(153.75, -328.56) * mm});
            skLineSegment(sketch, "E3434", {"start": v(153.75, -328.56) * mm, "end": v(152.67, -328.45) * mm});
            skLineSegment(sketch, "E3435", {"start": v(152.67, -328.45) * mm, "end": v(151.48, -328.56) * mm});
            skLineSegment(sketch, "E3436", {"start": v(151.48, -328.56) * mm, "end": v(150.4, -328.77) * mm});
            skLineSegment(sketch, "E3437", {"start": v(150.4, -328.77) * mm, "end": v(149.2, -328.99) * mm});
            skLineSegment(sketch, "E3438", {"start": v(149.2, -328.99) * mm, "end": v(148.23, -329.42) * mm});
            skLineSegment(sketch, "E3439", {"start": v(148.23, -329.42) * mm, "end": v(147.15, -329.96) * mm});
            skLineSegment(sketch, "E3440", {"start": v(147.15, -329.96) * mm, "end": v(146.18, -330.61) * mm});
            skLineSegment(sketch, "E3441", {"start": v(146.18, -330.61) * mm, "end": v(145.3, -331.37) * mm});
            skLineSegment(sketch, "E3442", {"start": v(145.3, -331.37) * mm, "end": v(144.44, -332.13) * mm});
            skLineSegment(sketch, "E3443", {"start": v(144.44, -332.13) * mm, "end": v(143.8, -333) * mm});
            skLineSegment(sketch, "E3444", {"start": v(143.8, -333) * mm, "end": v(143.15, -333.97) * mm});
            skLineSegment(sketch, "E3445", {"start": v(143.15, -333.97) * mm, "end": v(142.6, -335.05) * mm});
            skLineSegment(sketch, "E3446", {"start": v(142.6, -335.05) * mm, "end": v(142.17, -336.13) * mm});
            skLineSegment(sketch, "E3447", {"start": v(142.17, -336.13) * mm, "end": v(141.74, -338.3) * mm});
            skLineSegment(sketch, "E3448", {"start": v(141.74, -338.3) * mm, "end": v(141.63, -339.49) * mm});
            skLineSegment(sketch, "E3449", {"start": v(141.63, -339.49) * mm, "end": v(141.63, -376.5) * mm});
            skSolve(sketch);
        }
        {
            var Q0;
            Q0 = qSketchRegion(id + "F0", true);
            extrude(context, id + "F1", {"entities" : qUnion([Q0]), "depth" : 25.4 * mm, "offsetDistance" : 25.4 * mm});
        }
        {
            var Q0;
            Q0=qCreatedBy(makeId("Top.planeOp"),FACE);
            var sketch = newSketch(context, id + "F2", { "sketchPlane" : qUnion([Q0])});
            skLineSegment(sketch, "E3450.bottom", {"start": v(-279.84, 429.7) * mm, "end": v(282.03, 429.7) * mm});
            skLineSegment(sketch, "E3450.top", {"start": v(-279.84, -426.73) * mm, "end": v(282.03, -426.73) * mm});
            skLineSegment(sketch, "E3450.left", {"start": v(-279.84, 429.7) * mm, "end": v(-279.84, -426.73) * mm});
            skLineSegment(sketch, "E3450.right", {"start": v(282.03, 429.7) * mm, "end": v(282.03, -426.73) * mm});
            skSolve(sketch);
        }
        {
            var Q0;
            Q0=makeQuery(id+"F2.imprint","IMPRINT",FACE,{"disambiguationData":[TD([[makeQuery(id+"F2.imprint","IMPRINT",EDGE,{"derivedFrom":sQuery(id+"F2.wireOp",EDGE,"E3450.bottom")}),-1.0]])]});
            extrude(context, id + "F3", {"entities" : qUnion([Q0]), "endBound" : BoundingType.SYMMETRIC, "depth" : 25.4 * mm, "offsetDistance" : 25.4 * mm});
        }
        {
            var Q0;
            Q0=makeQuery(id+"F1.opExtrude","SWEPT_BODY",BODY,{"disambiguationData":[OSD([sQuery(id+"F0.wireOp",EDGE,"E321"),sQuery(id+"F0.wireOp",EDGE,"E322"),sQuery(id+"F0.wireOp",EDGE,"E323"),sQuery(id+"F0.wireOp",EDGE,"E324"),sQuery(id+"F0.wireOp",EDGE,"E325"),sQuery(id+"F0.wireOp",EDGE,"E326"),sQuery(id+"F0.wireOp",EDGE,"E327"),sQuery(id+"F0.wireOp",EDGE,"E328"),sQuery(id+"F0.wireOp",EDGE,"E329"),sQuery(id+"F0.wireOp",EDGE,"E330"),sQuery(id+"F0.wireOp",EDGE,"E331"),sQuery(id+"F0.wireOp",EDGE,"E332"),sQuery(id+"F0.wireOp",EDGE,"E333"),sQuery(id+"F0.wireOp",EDGE,"E334"),sQuery(id+"F0.wireOp",EDGE,"E335"),sQuery(id+"F0.wireOp",EDGE,"E336"),sQuery(id+"F0.wireOp",EDGE,"E337"),sQuery(id+"F0.wireOp",EDGE,"E338"),sQuery(id+"F0.wireOp",EDGE,"E339"),sQuery(id+"F0.wireOp",EDGE,"E340"),sQuery(id+"F0.wireOp",EDGE,"E341"),sQuery(id+"F0.wireOp",EDGE,"E342"),sQuery(id+"F0.wireOp",EDGE,"E343"),sQuery(id+"F0.wireOp",EDGE,"E344"),sQuery(id+"F0.wireOp",EDGE,"E345"),sQuery(id+"F0.wireOp",EDGE,"E346"),sQuery(id+"F0.wireOp",EDGE,"E347"),sQuery(id+"F0.wireOp",EDGE,"E348"),sQuery(id+"F0.wireOp",EDGE,"E349"),sQuery(id+"F0.wireOp",EDGE,"E350"),sQuery(id+"F0.wireOp",EDGE,"E351"),sQuery(id+"F0.wireOp",EDGE,"E352"),sQuery(id+"F0.wireOp",EDGE,"E353"),sQuery(id+"F0.wireOp",EDGE,"E354"),sQuery(id+"F0.wireOp",EDGE,"E355"),sQuery(id+"F0.wireOp",EDGE,"E356"),sQuery(id+"F0.wireOp",EDGE,"E357"),sQuery(id+"F0.wireOp",EDGE,"E358"),sQuery(id+"F0.wireOp",EDGE,"E359"),sQuery(id+"F0.wireOp",EDGE,"E360"),sQuery(id+"F0.wireOp",EDGE,"E361"),sQuery(id+"F0.wireOp",EDGE,"E362"),sQuery(id+"F0.wireOp",EDGE,"E363"),sQuery(id+"F0.wireOp",EDGE,"E364"),sQuery(id+"F0.wireOp",EDGE,"E365"),sQuery(id+"F0.wireOp",EDGE,"E366"),sQuery(id+"F0.wireOp",EDGE,"E367"),sQuery(id+"F0.wireOp",EDGE,"E368"),sQuery(id+"F0.wireOp",EDGE,"E369"),sQuery(id+"F0.wireOp",EDGE,"E370"),sQuery(id+"F0.wireOp",EDGE,"E371"),sQuery(id+"F0.wireOp",EDGE,"E372"),sQuery(id+"F0.wireOp",EDGE,"E373"),sQuery(id+"F0.wireOp",EDGE,"E374"),sQuery(id+"F0.wireOp",EDGE,"E375"),sQuery(id+"F0.wireOp",EDGE,"E376"),sQuery(id+"F0.wireOp",EDGE,"E377"),sQuery(id+"F0.wireOp",EDGE,"E378"),sQuery(id+"F0.wireOp",EDGE,"E379"),sQuery(id+"F0.wireOp",EDGE,"E380"),sQuery(id+"F0.wireOp",EDGE,"E381"),sQuery(id+"F0.wireOp",EDGE,"E382"),sQuery(id+"F0.wireOp",EDGE,"E383"),sQuery(id+"F0.wireOp",EDGE,"E384"),sQuery(id+"F0.wireOp",EDGE,"E385"),sQuery(id+"F0.wireOp",EDGE,"E386"),sQuery(id+"F0.wireOp",EDGE,"E387"),sQuery(id+"F0.wireOp",EDGE,"E388"),sQuery(id+"F0.wireOp",EDGE,"E389"),sQuery(id+"F0.wireOp",EDGE,"E390"),sQuery(id+"F0.wireOp",EDGE,"E391"),sQuery(id+"F0.wireOp",EDGE,"E392"),sQuery(id+"F0.wireOp",EDGE,"E393"),sQuery(id+"F0.wireOp",EDGE,"E394"),sQuery(id+"F0.wireOp",EDGE,"E395"),sQuery(id+"F0.wireOp",EDGE,"E396"),sQuery(id+"F0.wireOp",EDGE,"E397"),sQuery(id+"F0.wireOp",EDGE,"E398"),sQuery(id+"F0.wireOp",EDGE,"E399"),sQuery(id+"F0.wireOp",EDGE,"E400"),sQuery(id+"F0.wireOp",EDGE,"E401"),sQuery(id+"F0.wireOp",EDGE,"E402"),sQuery(id+"F0.wireOp",EDGE,"E403"),sQuery(id+"F0.wireOp",EDGE,"E404"),sQuery(id+"F0.wireOp",EDGE,"E405"),sQuery(id+"F0.wireOp",EDGE,"E406"),sQuery(id+"F0.wireOp",EDGE,"E407"),sQuery(id+"F0.wireOp",EDGE,"E408"),sQuery(id+"F0.wireOp",EDGE,"E409"),sQuery(id+"F0.wireOp",EDGE,"E410"),sQuery(id+"F0.wireOp",EDGE,"E411"),sQuery(id+"F0.wireOp",EDGE,"E412"),sQuery(id+"F0.wireOp",EDGE,"E413"),sQuery(id+"F0.wireOp",EDGE,"E414"),sQuery(id+"F0.wireOp",EDGE,"E415"),sQuery(id+"F0.wireOp",EDGE,"E416"),sQuery(id+"F0.wireOp",EDGE,"E417"),sQuery(id+"F0.wireOp",EDGE,"E418"),sQuery(id+"F0.wireOp",EDGE,"E419"),sQuery(id+"F0.wireOp",EDGE,"E420"),sQuery(id+"F0.wireOp",EDGE,"E421"),sQuery(id+"F0.wireOp",EDGE,"E422"),sQuery(id+"F0.wireOp",EDGE,"E423"),sQuery(id+"F0.wireOp",EDGE,"E424"),sQuery(id+"F0.wireOp",EDGE,"E425"),sQuery(id+"F0.wireOp",EDGE,"E426"),sQuery(id+"F0.wireOp",EDGE,"E427"),sQuery(id+"F0.wireOp",EDGE,"E428"),sQuery(id+"F0.wireOp",EDGE,"E429"),sQuery(id+"F0.wireOp",EDGE,"E430"),sQuery(id+"F0.wireOp",EDGE,"E431"),sQuery(id+"F0.wireOp",EDGE,"E432"),sQuery(id+"F0.wireOp",EDGE,"E433"),sQuery(id+"F0.wireOp",EDGE,"E434"),sQuery(id+"F0.wireOp",EDGE,"E435"),sQuery(id+"F0.wireOp",EDGE,"E436"),sQuery(id+"F0.wireOp",EDGE,"E437"),sQuery(id+"F0.wireOp",EDGE,"E438"),sQuery(id+"F0.wireOp",EDGE,"E439"),sQuery(id+"F0.wireOp",EDGE,"E440"),sQuery(id+"F0.wireOp",EDGE,"E441")])]});
            var Q1;
            Q1=makeQuery(id+"F1.opExtrude","SWEPT_BODY",BODY,{"disambiguationData":[OSD([sQuery(id+"F0.wireOp",EDGE,"E538"),sQuery(id+"F0.wireOp",EDGE,"E539"),sQuery(id+"F0.wireOp",EDGE,"E540"),sQuery(id+"F0.wireOp",EDGE,"E541")])]});
            var Q2;
            Q2=makeQuery(id+"F1.opExtrude","SWEPT_BODY",BODY,{"disambiguationData":[OSD([sQuery(id+"F0.wireOp",EDGE,"E973"),sQuery(id+"F0.wireOp",EDGE,"E974"),sQuery(id+"F0.wireOp",EDGE,"E975"),sQuery(id+"F0.wireOp",EDGE,"E976"),sQuery(id+"F0.wireOp",EDGE,"E977"),sQuery(id+"F0.wireOp",EDGE,"E978"),sQuery(id+"F0.wireOp",EDGE,"E979"),sQuery(id+"F0.wireOp",EDGE,"E980"),sQuery(id+"F0.wireOp",EDGE,"E981"),sQuery(id+"F0.wireOp",EDGE,"E982"),sQuery(id+"F0.wireOp",EDGE,"E983"),sQuery(id+"F0.wireOp",EDGE,"E984"),sQuery(id+"F0.wireOp",EDGE,"E985"),sQuery(id+"F0.wireOp",EDGE,"E986"),sQuery(id+"F0.wireOp",EDGE,"E987"),sQuery(id+"F0.wireOp",EDGE,"E988"),sQuery(id+"F0.wireOp",EDGE,"E989"),sQuery(id+"F0.wireOp",EDGE,"E990"),sQuery(id+"F0.wireOp",EDGE,"E991"),sQuery(id+"F0.wireOp",EDGE,"E992"),sQuery(id+"F0.wireOp",EDGE,"E993"),sQuery(id+"F0.wireOp",EDGE,"E994"),sQuery(id+"F0.wireOp",EDGE,"E995"),sQuery(id+"F0.wireOp",EDGE,"E996"),sQuery(id+"F0.wireOp",EDGE,"E997"),sQuery(id+"F0.wireOp",EDGE,"E998"),sQuery(id+"F0.wireOp",EDGE,"E999"),sQuery(id+"F0.wireOp",EDGE,"E1000"),sQuery(id+"F0.wireOp",EDGE,"E1001"),sQuery(id+"F0.wireOp",EDGE,"E1002"),sQuery(id+"F0.wireOp",EDGE,"E1003"),sQuery(id+"F0.wireOp",EDGE,"E1004"),sQuery(id+"F0.wireOp",EDGE,"E1005"),sQuery(id+"F0.wireOp",EDGE,"E1006"),sQuery(id+"F0.wireOp",EDGE,"E1007"),sQuery(id+"F0.wireOp",EDGE,"E1008"),sQuery(id+"F0.wireOp",EDGE,"E1009"),sQuery(id+"F0.wireOp",EDGE,"E1010"),sQuery(id+"F0.wireOp",EDGE,"E1011"),sQuery(id+"F0.wireOp",EDGE,"E1012"),sQuery(id+"F0.wireOp",EDGE,"E1013"),sQuery(id+"F0.wireOp",EDGE,"E1014"),sQuery(id+"F0.wireOp",EDGE,"E1015"),sQuery(id+"F0.wireOp",EDGE,"E1016"),sQuery(id+"F0.wireOp",EDGE,"E1017"),sQuery(id+"F0.wireOp",EDGE,"E1018"),sQuery(id+"F0.wireOp",EDGE,"E1019"),sQuery(id+"F0.wireOp",EDGE,"E1020"),sQuery(id+"F0.wireOp",EDGE,"E1021"),sQuery(id+"F0.wireOp",EDGE,"E1022"),sQuery(id+"F0.wireOp",EDGE,"E1023"),sQuery(id+"F0.wireOp",EDGE,"E1024"),sQuery(id+"F0.wireOp",EDGE,"E1025"),sQuery(id+"F0.wireOp",EDGE,"E1026"),sQuery(id+"F0.wireOp",EDGE,"E1027"),sQuery(id+"F0.wireOp",EDGE,"E1028"),sQuery(id+"F0.wireOp",EDGE,"E1029"),sQuery(id+"F0.wireOp",EDGE,"E1030"),sQuery(id+"F0.wireOp",EDGE,"E1031"),sQuery(id+"F0.wireOp",EDGE,"E1032"),sQuery(id+"F0.wireOp",EDGE,"E1033"),sQuery(id+"F0.wireOp",EDGE,"E1034"),sQuery(id+"F0.wireOp",EDGE,"E1035"),sQuery(id+"F0.wireOp",EDGE,"E1036"),sQuery(id+"F0.wireOp",EDGE,"E1037"),sQuery(id+"F0.wireOp",EDGE,"E1038"),sQuery(id+"F0.wireOp",EDGE,"E1039"),sQuery(id+"F0.wireOp",EDGE,"E1040"),sQuery(id+"F0.wireOp",EDGE,"E1041"),sQuery(id+"F0.wireOp",EDGE,"E1042"),sQuery(id+"F0.wireOp",EDGE,"E1043"),sQuery(id+"F0.wireOp",EDGE,"E1044"),sQuery(id+"F0.wireOp",EDGE,"E1045"),sQuery(id+"F0.wireOp",EDGE,"E1046"),sQuery(id+"F0.wireOp",EDGE,"E1047"),sQuery(id+"F0.wireOp",EDGE,"E1048"),sQuery(id+"F0.wireOp",EDGE,"E1049"),sQuery(id+"F0.wireOp",EDGE,"E1050"),sQuery(id+"F0.wireOp",EDGE,"E1051"),sQuery(id+"F0.wireOp",EDGE,"E1052"),sQuery(id+"F0.wireOp",EDGE,"E1053"),sQuery(id+"F0.wireOp",EDGE,"E1054"),sQuery(id+"F0.wireOp",EDGE,"E1055"),sQuery(id+"F0.wireOp",EDGE,"E1056"),sQuery(id+"F0.wireOp",EDGE,"E1057"),sQuery(id+"F0.wireOp",EDGE,"E1058"),sQuery(id+"F0.wireOp",EDGE,"E1059"),sQuery(id+"F0.wireOp",EDGE,"E1060"),sQuery(id+"F0.wireOp",EDGE,"E1061"),sQuery(id+"F0.wireOp",EDGE,"E1062"),sQuery(id+"F0.wireOp",EDGE,"E1063"),sQuery(id+"F0.wireOp",EDGE,"E1064"),sQuery(id+"F0.wireOp",EDGE,"E1065"),sQuery(id+"F0.wireOp",EDGE,"E1066"),sQuery(id+"F0.wireOp",EDGE,"E1067"),sQuery(id+"F0.wireOp",EDGE,"E1068"),sQuery(id+"F0.wireOp",EDGE,"E1069"),sQuery(id+"F0.wireOp",EDGE,"E1070"),sQuery(id+"F0.wireOp",EDGE,"E1071"),sQuery(id+"F0.wireOp",EDGE,"E1072"),sQuery(id+"F0.wireOp",EDGE,"E1073"),sQuery(id+"F0.wireOp",EDGE,"E1074"),sQuery(id+"F0.wireOp",EDGE,"E1075")])]});
            var Q3;
            Q3=makeQuery(id+"F1.opExtrude","SWEPT_BODY",BODY,{"disambiguationData":[OSD([sQuery(id+"F0.wireOp",EDGE,"E1265"),sQuery(id+"F0.wireOp",EDGE,"E1266"),sQuery(id+"F0.wireOp",EDGE,"E1267"),sQuery(id+"F0.wireOp",EDGE,"E1268"),sQuery(id+"F0.wireOp",EDGE,"E1269"),sQuery(id+"F0.wireOp",EDGE,"E1270"),sQuery(id+"F0.wireOp",EDGE,"E1271"),sQuery(id+"F0.wireOp",EDGE,"E1272"),sQuery(id+"F0.wireOp",EDGE,"E1273"),sQuery(id+"F0.wireOp",EDGE,"E1274"),sQuery(id+"F0.wireOp",EDGE,"E1275"),sQuery(id+"F0.wireOp",EDGE,"E1276"),sQuery(id+"F0.wireOp",EDGE,"E1277"),sQuery(id+"F0.wireOp",EDGE,"E1278"),sQuery(id+"F0.wireOp",EDGE,"E1279"),sQuery(id+"F0.wireOp",EDGE,"E1280")])]});
            var Q4;
            Q4=makeQuery(id+"F1.opExtrude","SWEPT_BODY",BODY,{"disambiguationData":[OSD([sQuery(id+"F0.wireOp",EDGE,"E2352"),sQuery(id+"F0.wireOp",EDGE,"E2353"),sQuery(id+"F0.wireOp",EDGE,"E2354"),sQuery(id+"F0.wireOp",EDGE,"E2355"),sQuery(id+"F0.wireOp",EDGE,"E2356"),sQuery(id+"F0.wireOp",EDGE,"E2357"),sQuery(id+"F0.wireOp",EDGE,"E2358"),sQuery(id+"F0.wireOp",EDGE,"E2359"),sQuery(id+"F0.wireOp",EDGE,"E2360"),sQuery(id+"F0.wireOp",EDGE,"E2361"),sQuery(id+"F0.wireOp",EDGE,"E2362"),sQuery(id+"F0.wireOp",EDGE,"E2363"),sQuery(id+"F0.wireOp",EDGE,"E2364"),sQuery(id+"F0.wireOp",EDGE,"E2365"),sQuery(id+"F0.wireOp",EDGE,"E2366"),sQuery(id+"F0.wireOp",EDGE,"E2367"),sQuery(id+"F0.wireOp",EDGE,"E2368"),sQuery(id+"F0.wireOp",EDGE,"E2369"),sQuery(id+"F0.wireOp",EDGE,"E2370"),sQuery(id+"F0.wireOp",EDGE,"E2371"),sQuery(id+"F0.wireOp",EDGE,"E2372"),sQuery(id+"F0.wireOp",EDGE,"E2373"),sQuery(id+"F0.wireOp",EDGE,"E2374"),sQuery(id+"F0.wireOp",EDGE,"E2375"),sQuery(id+"F0.wireOp",EDGE,"E2376"),sQuery(id+"F0.wireOp",EDGE,"E2377"),sQuery(id+"F0.wireOp",EDGE,"E2378"),sQuery(id+"F0.wireOp",EDGE,"E2379"),sQuery(id+"F0.wireOp",EDGE,"E2380"),sQuery(id+"F0.wireOp",EDGE,"E2381"),sQuery(id+"F0.wireOp",EDGE,"E2382"),sQuery(id+"F0.wireOp",EDGE,"E2383"),sQuery(id+"F0.wireOp",EDGE,"E2384"),sQuery(id+"F0.wireOp",EDGE,"E2385"),sQuery(id+"F0.wireOp",EDGE,"E2386"),sQuery(id+"F0.wireOp",EDGE,"E2387"),sQuery(id+"F0.wireOp",EDGE,"E2388"),sQuery(id+"F0.wireOp",EDGE,"E2389"),sQuery(id+"F0.wireOp",EDGE,"E2390"),sQuery(id+"F0.wireOp",EDGE,"E2391"),sQuery(id+"F0.wireOp",EDGE,"E2392"),sQuery(id+"F0.wireOp",EDGE,"E2393"),sQuery(id+"F0.wireOp",EDGE,"E2394"),sQuery(id+"F0.wireOp",EDGE,"E2395"),sQuery(id+"F0.wireOp",EDGE,"E2396"),sQuery(id+"F0.wireOp",EDGE,"E2397"),sQuery(id+"F0.wireOp",EDGE,"E2398"),sQuery(id+"F0.wireOp",EDGE,"E2399"),sQuery(id+"F0.wireOp",EDGE,"E2400"),sQuery(id+"F0.wireOp",EDGE,"E2401"),sQuery(id+"F0.wireOp",EDGE,"E2402"),sQuery(id+"F0.wireOp",EDGE,"E2403"),sQuery(id+"F0.wireOp",EDGE,"E2404"),sQuery(id+"F0.wireOp",EDGE,"E2405"),sQuery(id+"F0.wireOp",EDGE,"E2406"),sQuery(id+"F0.wireOp",EDGE,"E2407"),sQuery(id+"F0.wireOp",EDGE,"E2408"),sQuery(id+"F0.wireOp",EDGE,"E2409"),sQuery(id+"F0.wireOp",EDGE,"E2410"),sQuery(id+"F0.wireOp",EDGE,"E2411"),sQuery(id+"F0.wireOp",EDGE,"E2412"),sQuery(id+"F0.wireOp",EDGE,"E2413"),sQuery(id+"F0.wireOp",EDGE,"E2414"),sQuery(id+"F0.wireOp",EDGE,"E2415"),sQuery(id+"F0.wireOp",EDGE,"E2416"),sQuery(id+"F0.wireOp",EDGE,"E2417"),sQuery(id+"F0.wireOp",EDGE,"E2418"),sQuery(id+"F0.wireOp",EDGE,"E2419"),sQuery(id+"F0.wireOp",EDGE,"E2420"),sQuery(id+"F0.wireOp",EDGE,"E2421"),sQuery(id+"F0.wireOp",EDGE,"E2422"),sQuery(id+"F0.wireOp",EDGE,"E2423"),sQuery(id+"F0.wireOp",EDGE,"E2424"),sQuery(id+"F0.wireOp",EDGE,"E2425")])]});
            var Q5;
            Q5=makeQuery(id+"F1.opExtrude","SWEPT_BODY",BODY,{"disambiguationData":[OSD([sQuery(id+"F0.wireOp",EDGE,"E2607"),sQuery(id+"F0.wireOp",EDGE,"E2608"),sQuery(id+"F0.wireOp",EDGE,"E2609"),sQuery(id+"F0.wireOp",EDGE,"E2610")])]});
            var Q6;
            Q6=makeQuery(id+"F1.opExtrude","SWEPT_BODY",BODY,{"disambiguationData":[OSD([sQuery(id+"F0.wireOp",EDGE,"E2611"),sQuery(id+"F0.wireOp",EDGE,"E2612"),sQuery(id+"F0.wireOp",EDGE,"E2613"),sQuery(id+"F0.wireOp",EDGE,"E2614"),sQuery(id+"F0.wireOp",EDGE,"E2615"),sQuery(id+"F0.wireOp",EDGE,"E2616"),sQuery(id+"F0.wireOp",EDGE,"E2617")])]});
            var Q7;
            Q7=makeQuery(id+"F1.opExtrude","SWEPT_BODY",BODY,{"disambiguationData":[OSD([sQuery(id+"F0.wireOp",EDGE,"E2786"),sQuery(id+"F0.wireOp",EDGE,"E2787"),sQuery(id+"F0.wireOp",EDGE,"E2788"),sQuery(id+"F0.wireOp",EDGE,"E2789"),sQuery(id+"F0.wireOp",EDGE,"E2790"),sQuery(id+"F0.wireOp",EDGE,"E2791"),sQuery(id+"F0.wireOp",EDGE,"E2792"),sQuery(id+"F0.wireOp",EDGE,"E2793"),sQuery(id+"F0.wireOp",EDGE,"E2794"),sQuery(id+"F0.wireOp",EDGE,"E2795"),sQuery(id+"F0.wireOp",EDGE,"E2796"),sQuery(id+"F0.wireOp",EDGE,"E2797"),sQuery(id+"F0.wireOp",EDGE,"E2798"),sQuery(id+"F0.wireOp",EDGE,"E2799"),sQuery(id+"F0.wireOp",EDGE,"E2800"),sQuery(id+"F0.wireOp",EDGE,"E2801"),sQuery(id+"F0.wireOp",EDGE,"E2802"),sQuery(id+"F0.wireOp",EDGE,"E2803"),sQuery(id+"F0.wireOp",EDGE,"E2804"),sQuery(id+"F0.wireOp",EDGE,"E2805"),sQuery(id+"F0.wireOp",EDGE,"E2806"),sQuery(id+"F0.wireOp",EDGE,"E2807"),sQuery(id+"F0.wireOp",EDGE,"E2808"),sQuery(id+"F0.wireOp",EDGE,"E2809"),sQuery(id+"F0.wireOp",EDGE,"E2810"),sQuery(id+"F0.wireOp",EDGE,"E2811"),sQuery(id+"F0.wireOp",EDGE,"E2812"),sQuery(id+"F0.wireOp",EDGE,"E2813"),sQuery(id+"F0.wireOp",EDGE,"E2814"),sQuery(id+"F0.wireOp",EDGE,"E2815"),sQuery(id+"F0.wireOp",EDGE,"E2816"),sQuery(id+"F0.wireOp",EDGE,"E2817"),sQuery(id+"F0.wireOp",EDGE,"E2818"),sQuery(id+"F0.wireOp",EDGE,"E2819"),sQuery(id+"F0.wireOp",EDGE,"E2820"),sQuery(id+"F0.wireOp",EDGE,"E2821"),sQuery(id+"F0.wireOp",EDGE,"E2822"),sQuery(id+"F0.wireOp",EDGE,"E2823"),sQuery(id+"F0.wireOp",EDGE,"E2824"),sQuery(id+"F0.wireOp",EDGE,"E2825"),sQuery(id+"F0.wireOp",EDGE,"E2826"),sQuery(id+"F0.wireOp",EDGE,"E2827"),sQuery(id+"F0.wireOp",EDGE,"E2828"),sQuery(id+"F0.wireOp",EDGE,"E2829"),sQuery(id+"F0.wireOp",EDGE,"E2830"),sQuery(id+"F0.wireOp",EDGE,"E2831"),sQuery(id+"F0.wireOp",EDGE,"E2832"),sQuery(id+"F0.wireOp",EDGE,"E2833"),sQuery(id+"F0.wireOp",EDGE,"E2834"),sQuery(id+"F0.wireOp",EDGE,"E2835"),sQuery(id+"F0.wireOp",EDGE,"E2836"),sQuery(id+"F0.wireOp",EDGE,"E2837"),sQuery(id+"F0.wireOp",EDGE,"E2838"),sQuery(id+"F0.wireOp",EDGE,"E2839"),sQuery(id+"F0.wireOp",EDGE,"E2840"),sQuery(id+"F0.wireOp",EDGE,"E2841"),sQuery(id+"F0.wireOp",EDGE,"E2842"),sQuery(id+"F0.wireOp",EDGE,"E2843"),sQuery(id+"F0.wireOp",EDGE,"E2844"),sQuery(id+"F0.wireOp",EDGE,"E2845"),sQuery(id+"F0.wireOp",EDGE,"E2846"),sQuery(id+"F0.wireOp",EDGE,"E2847"),sQuery(id+"F0.wireOp",EDGE,"E2848"),sQuery(id+"F0.wireOp",EDGE,"E2849"),sQuery(id+"F0.wireOp",EDGE,"E2850"),sQuery(id+"F0.wireOp",EDGE,"E2851"),sQuery(id+"F0.wireOp",EDGE,"E2852"),sQuery(id+"F0.wireOp",EDGE,"E2853"),sQuery(id+"F0.wireOp",EDGE,"E2854"),sQuery(id+"F0.wireOp",EDGE,"E2855"),sQuery(id+"F0.wireOp",EDGE,"E2856"),sQuery(id+"F0.wireOp",EDGE,"E2857"),sQuery(id+"F0.wireOp",EDGE,"E2858"),sQuery(id+"F0.wireOp",EDGE,"E2859"),sQuery(id+"F0.wireOp",EDGE,"E2860"),sQuery(id+"F0.wireOp",EDGE,"E2861"),sQuery(id+"F0.wireOp",EDGE,"E2862"),sQuery(id+"F0.wireOp",EDGE,"E2863"),sQuery(id+"F0.wireOp",EDGE,"E2864"),sQuery(id+"F0.wireOp",EDGE,"E2865"),sQuery(id+"F0.wireOp",EDGE,"E2866"),sQuery(id+"F0.wireOp",EDGE,"E2867"),sQuery(id+"F0.wireOp",EDGE,"E2868"),sQuery(id+"F0.wireOp",EDGE,"E2869"),sQuery(id+"F0.wireOp",EDGE,"E2870"),sQuery(id+"F0.wireOp",EDGE,"E2871"),sQuery(id+"F0.wireOp",EDGE,"E2872"),sQuery(id+"F0.wireOp",EDGE,"E2873"),sQuery(id+"F0.wireOp",EDGE,"E2874"),sQuery(id+"F0.wireOp",EDGE,"E2875"),sQuery(id+"F0.wireOp",EDGE,"E2876"),sQuery(id+"F0.wireOp",EDGE,"E2877"),sQuery(id+"F0.wireOp",EDGE,"E2878"),sQuery(id+"F0.wireOp",EDGE,"E2879"),sQuery(id+"F0.wireOp",EDGE,"E2880"),sQuery(id+"F0.wireOp",EDGE,"E2881"),sQuery(id+"F0.wireOp",EDGE,"E2882"),sQuery(id+"F0.wireOp",EDGE,"E2883"),sQuery(id+"F0.wireOp",EDGE,"E2884"),sQuery(id+"F0.wireOp",EDGE,"E2885"),sQuery(id+"F0.wireOp",EDGE,"E2886"),sQuery(id+"F0.wireOp",EDGE,"E2887"),sQuery(id+"F0.wireOp",EDGE,"E2888"),sQuery(id+"F0.wireOp",EDGE,"E2889"),sQuery(id+"F0.wireOp",EDGE,"E2890"),sQuery(id+"F0.wireOp",EDGE,"E2891"),sQuery(id+"F0.wireOp",EDGE,"E2892"),sQuery(id+"F0.wireOp",EDGE,"E2893"),sQuery(id+"F0.wireOp",EDGE,"E2894"),sQuery(id+"F0.wireOp",EDGE,"E2895"),sQuery(id+"F0.wireOp",EDGE,"E2896"),sQuery(id+"F0.wireOp",EDGE,"E2897"),sQuery(id+"F0.wireOp",EDGE,"E2898"),sQuery(id+"F0.wireOp",EDGE,"E2899"),sQuery(id+"F0.wireOp",EDGE,"E2900"),sQuery(id+"F0.wireOp",EDGE,"E2901"),sQuery(id+"F0.wireOp",EDGE,"E2902"),sQuery(id+"F0.wireOp",EDGE,"E2903"),sQuery(id+"F0.wireOp",EDGE,"E2904"),sQuery(id+"F0.wireOp",EDGE,"E2905")])]});
            var Q8;
            Q8=makeQuery(id+"F1.opExtrude","SWEPT_BODY",BODY,{"disambiguationData":[OSD([sQuery(id+"F0.wireOp",EDGE,"E2906"),sQuery(id+"F0.wireOp",EDGE,"E2907"),sQuery(id+"F0.wireOp",EDGE,"E2908"),sQuery(id+"F0.wireOp",EDGE,"E2909"),sQuery(id+"F0.wireOp",EDGE,"E2910"),sQuery(id+"F0.wireOp",EDGE,"E2911"),sQuery(id+"F0.wireOp",EDGE,"E2912"),sQuery(id+"F0.wireOp",EDGE,"E2913"),sQuery(id+"F0.wireOp",EDGE,"E2914"),sQuery(id+"F0.wireOp",EDGE,"E2915"),sQuery(id+"F0.wireOp",EDGE,"E2916"),sQuery(id+"F0.wireOp",EDGE,"E2917"),sQuery(id+"F0.wireOp",EDGE,"E2918"),sQuery(id+"F0.wireOp",EDGE,"E2919"),sQuery(id+"F0.wireOp",EDGE,"E2920"),sQuery(id+"F0.wireOp",EDGE,"E2921"),sQuery(id+"F0.wireOp",EDGE,"E2922"),sQuery(id+"F0.wireOp",EDGE,"E2923"),sQuery(id+"F0.wireOp",EDGE,"E2924"),sQuery(id+"F0.wireOp",EDGE,"E2925"),sQuery(id+"F0.wireOp",EDGE,"E2926"),sQuery(id+"F0.wireOp",EDGE,"E2927"),sQuery(id+"F0.wireOp",EDGE,"E2928"),sQuery(id+"F0.wireOp",EDGE,"E2929"),sQuery(id+"F0.wireOp",EDGE,"E2930"),sQuery(id+"F0.wireOp",EDGE,"E2931"),sQuery(id+"F0.wireOp",EDGE,"E2932"),sQuery(id+"F0.wireOp",EDGE,"E2933"),sQuery(id+"F0.wireOp",EDGE,"E2934"),sQuery(id+"F0.wireOp",EDGE,"E2935"),sQuery(id+"F0.wireOp",EDGE,"E2936"),sQuery(id+"F0.wireOp",EDGE,"E2937"),sQuery(id+"F0.wireOp",EDGE,"E2938"),sQuery(id+"F0.wireOp",EDGE,"E2939"),sQuery(id+"F0.wireOp",EDGE,"E2940"),sQuery(id+"F0.wireOp",EDGE,"E2941"),sQuery(id+"F0.wireOp",EDGE,"E2942"),sQuery(id+"F0.wireOp",EDGE,"E2943"),sQuery(id+"F0.wireOp",EDGE,"E2944"),sQuery(id+"F0.wireOp",EDGE,"E2945"),sQuery(id+"F0.wireOp",EDGE,"E2946"),sQuery(id+"F0.wireOp",EDGE,"E2947"),sQuery(id+"F0.wireOp",EDGE,"E2948"),sQuery(id+"F0.wireOp",EDGE,"E2949"),sQuery(id+"F0.wireOp",EDGE,"E2950"),sQuery(id+"F0.wireOp",EDGE,"E2951"),sQuery(id+"F0.wireOp",EDGE,"E2952"),sQuery(id+"F0.wireOp",EDGE,"E2953"),sQuery(id+"F0.wireOp",EDGE,"E2954"),sQuery(id+"F0.wireOp",EDGE,"E2955"),sQuery(id+"F0.wireOp",EDGE,"E2956"),sQuery(id+"F0.wireOp",EDGE,"E2957"),sQuery(id+"F0.wireOp",EDGE,"E2958"),sQuery(id+"F0.wireOp",EDGE,"E2959"),sQuery(id+"F0.wireOp",EDGE,"E2960"),sQuery(id+"F0.wireOp",EDGE,"E2961"),sQuery(id+"F0.wireOp",EDGE,"E2962"),sQuery(id+"F0.wireOp",EDGE,"E2963"),sQuery(id+"F0.wireOp",EDGE,"E2964"),sQuery(id+"F0.wireOp",EDGE,"E2965"),sQuery(id+"F0.wireOp",EDGE,"E2966"),sQuery(id+"F0.wireOp",EDGE,"E2967"),sQuery(id+"F0.wireOp",EDGE,"E2968"),sQuery(id+"F0.wireOp",EDGE,"E2969"),sQuery(id+"F0.wireOp",EDGE,"E2970"),sQuery(id+"F0.wireOp",EDGE,"E2971"),sQuery(id+"F0.wireOp",EDGE,"E2972"),sQuery(id+"F0.wireOp",EDGE,"E2973"),sQuery(id+"F0.wireOp",EDGE,"E2974"),sQuery(id+"F0.wireOp",EDGE,"E2975"),sQuery(id+"F0.wireOp",EDGE,"E2976"),sQuery(id+"F0.wireOp",EDGE,"E2977"),sQuery(id+"F0.wireOp",EDGE,"E2978"),sQuery(id+"F0.wireOp",EDGE,"E2979"),sQuery(id+"F0.wireOp",EDGE,"E2980"),sQuery(id+"F0.wireOp",EDGE,"E2981"),sQuery(id+"F0.wireOp",EDGE,"E2982"),sQuery(id+"F0.wireOp",EDGE,"E2983"),sQuery(id+"F0.wireOp",EDGE,"E2984"),sQuery(id+"F0.wireOp",EDGE,"E2985"),sQuery(id+"F0.wireOp",EDGE,"E2986"),sQuery(id+"F0.wireOp",EDGE,"E2987"),sQuery(id+"F0.wireOp",EDGE,"E2988"),sQuery(id+"F0.wireOp",EDGE,"E2989"),sQuery(id+"F0.wireOp",EDGE,"E2990"),sQuery(id+"F0.wireOp",EDGE,"E2991"),sQuery(id+"F0.wireOp",EDGE,"E2992"),sQuery(id+"F0.wireOp",EDGE,"E2993"),sQuery(id+"F0.wireOp",EDGE,"E2994"),sQuery(id+"F0.wireOp",EDGE,"E2995"),sQuery(id+"F0.wireOp",EDGE,"E2996"),sQuery(id+"F0.wireOp",EDGE,"E2997"),sQuery(id+"F0.wireOp",EDGE,"E2998"),sQuery(id+"F0.wireOp",EDGE,"E2999"),sQuery(id+"F0.wireOp",EDGE,"E3000"),sQuery(id+"F0.wireOp",EDGE,"E3001"),sQuery(id+"F0.wireOp",EDGE,"E3002"),sQuery(id+"F0.wireOp",EDGE,"E3003"),sQuery(id+"F0.wireOp",EDGE,"E3004"),sQuery(id+"F0.wireOp",EDGE,"E3005"),sQuery(id+"F0.wireOp",EDGE,"E3006"),sQuery(id+"F0.wireOp",EDGE,"E3007"),sQuery(id+"F0.wireOp",EDGE,"E3008"),sQuery(id+"F0.wireOp",EDGE,"E3009"),sQuery(id+"F0.wireOp",EDGE,"E3010"),sQuery(id+"F0.wireOp",EDGE,"E3011"),sQuery(id+"F0.wireOp",EDGE,"E3012"),sQuery(id+"F0.wireOp",EDGE,"E3013"),sQuery(id+"F0.wireOp",EDGE,"E3014"),sQuery(id+"F0.wireOp",EDGE,"E3015"),sQuery(id+"F0.wireOp",EDGE,"E3016"),sQuery(id+"F0.wireOp",EDGE,"E3017"),sQuery(id+"F0.wireOp",EDGE,"E3018"),sQuery(id+"F0.wireOp",EDGE,"E3019"),sQuery(id+"F0.wireOp",EDGE,"E3020"),sQuery(id+"F0.wireOp",EDGE,"E3021"),sQuery(id+"F0.wireOp",EDGE,"E3022"),sQuery(id+"F0.wireOp",EDGE,"E3023"),sQuery(id+"F0.wireOp",EDGE,"E3024"),sQuery(id+"F0.wireOp",EDGE,"E3025")])]});
            var Q9;
            Q9=makeQuery(id+"F3.opExtrude","SWEPT_BODY",BODY,{"disambiguationData":[OSD([sQuery(id+"F2.wireOp",EDGE,"E3450.bottom"),sQuery(id+"F2.wireOp",EDGE,"E3450.top"),sQuery(id+"F2.wireOp",EDGE,"E3450.left"),sQuery(id+"F2.wireOp",EDGE,"E3450.right")])]});
            var Q10;
            Q10=makeQuery(id+"F1.opExtrude","SWEPT_BODY",BODY,{"disambiguationData":[OSD([sQuery(id+"F0.wireOp",EDGE,"E0"),sQuery(id+"F0.wireOp",EDGE,"E1"),sQuery(id+"F0.wireOp",EDGE,"E2"),sQuery(id+"F0.wireOp",EDGE,"E3"),sQuery(id+"F0.wireOp",EDGE,"E4"),sQuery(id+"F0.wireOp",EDGE,"E5"),sQuery(id+"F0.wireOp",EDGE,"E6"),sQuery(id+"F0.wireOp",EDGE,"E7"),sQuery(id+"F0.wireOp",EDGE,"E8"),sQuery(id+"F0.wireOp",EDGE,"E9"),sQuery(id+"F0.wireOp",EDGE,"E10"),sQuery(id+"F0.wireOp",EDGE,"E11"),sQuery(id+"F0.wireOp",EDGE,"E12"),sQuery(id+"F0.wireOp",EDGE,"E13"),sQuery(id+"F0.wireOp",EDGE,"E14"),sQuery(id+"F0.wireOp",EDGE,"E15"),sQuery(id+"F0.wireOp",EDGE,"E16"),sQuery(id+"F0.wireOp",EDGE,"E17"),sQuery(id+"F0.wireOp",EDGE,"E18"),sQuery(id+"F0.wireOp",EDGE,"E19"),sQuery(id+"F0.wireOp",EDGE,"E20"),sQuery(id+"F0.wireOp",EDGE,"E21"),sQuery(id+"F0.wireOp",EDGE,"E22"),sQuery(id+"F0.wireOp",EDGE,"E23"),sQuery(id+"F0.wireOp",EDGE,"E24"),sQuery(id+"F0.wireOp",EDGE,"E25"),sQuery(id+"F0.wireOp",EDGE,"E26"),sQuery(id+"F0.wireOp",EDGE,"E27"),sQuery(id+"F0.wireOp",EDGE,"E28"),sQuery(id+"F0.wireOp",EDGE,"E29"),sQuery(id+"F0.wireOp",EDGE,"E30"),sQuery(id+"F0.wireOp",EDGE,"E31"),sQuery(id+"F0.wireOp",EDGE,"E32"),sQuery(id+"F0.wireOp",EDGE,"E33"),sQuery(id+"F0.wireOp",EDGE,"E34"),sQuery(id+"F0.wireOp",EDGE,"E35"),sQuery(id+"F0.wireOp",EDGE,"E36"),sQuery(id+"F0.wireOp",EDGE,"E37"),sQuery(id+"F0.wireOp",EDGE,"E38"),sQuery(id+"F0.wireOp",EDGE,"E39"),sQuery(id+"F0.wireOp",EDGE,"E40"),sQuery(id+"F0.wireOp",EDGE,"E41"),sQuery(id+"F0.wireOp",EDGE,"E42"),sQuery(id+"F0.wireOp",EDGE,"E43"),sQuery(id+"F0.wireOp",EDGE,"E44"),sQuery(id+"F0.wireOp",EDGE,"E45"),sQuery(id+"F0.wireOp",EDGE,"E46"),sQuery(id+"F0.wireOp",EDGE,"E47"),sQuery(id+"F0.wireOp",EDGE,"E48"),sQuery(id+"F0.wireOp",EDGE,"E49")])]});
            var Q11;
            Q11=makeQuery(id+"F1.opExtrude","SWEPT_BODY",BODY,{"disambiguationData":[OSD([sQuery(id+"F0.wireOp",EDGE,"E50"),sQuery(id+"F0.wireOp",EDGE,"E51"),sQuery(id+"F0.wireOp",EDGE,"E52"),sQuery(id+"F0.wireOp",EDGE,"E53"),sQuery(id+"F0.wireOp",EDGE,"E54"),sQuery(id+"F0.wireOp",EDGE,"E55"),sQuery(id+"F0.wireOp",EDGE,"E56"),sQuery(id+"F0.wireOp",EDGE,"E57"),sQuery(id+"F0.wireOp",EDGE,"E58"),sQuery(id+"F0.wireOp",EDGE,"E59"),sQuery(id+"F0.wireOp",EDGE,"E60"),sQuery(id+"F0.wireOp",EDGE,"E61"),sQuery(id+"F0.wireOp",EDGE,"E62"),sQuery(id+"F0.wireOp",EDGE,"E63"),sQuery(id+"F0.wireOp",EDGE,"E64"),sQuery(id+"F0.wireOp",EDGE,"E65"),sQuery(id+"F0.wireOp",EDGE,"E66"),sQuery(id+"F0.wireOp",EDGE,"E67"),sQuery(id+"F0.wireOp",EDGE,"E68"),sQuery(id+"F0.wireOp",EDGE,"E69"),sQuery(id+"F0.wireOp",EDGE,"E70"),sQuery(id+"F0.wireOp",EDGE,"E71"),sQuery(id+"F0.wireOp",EDGE,"E72"),sQuery(id+"F0.wireOp",EDGE,"E73"),sQuery(id+"F0.wireOp",EDGE,"E74"),sQuery(id+"F0.wireOp",EDGE,"E75"),sQuery(id+"F0.wireOp",EDGE,"E76"),sQuery(id+"F0.wireOp",EDGE,"E77"),sQuery(id+"F0.wireOp",EDGE,"E78"),sQuery(id+"F0.wireOp",EDGE,"E79"),sQuery(id+"F0.wireOp",EDGE,"E80"),sQuery(id+"F0.wireOp",EDGE,"E81"),sQuery(id+"F0.wireOp",EDGE,"E82"),sQuery(id+"F0.wireOp",EDGE,"E83"),sQuery(id+"F0.wireOp",EDGE,"E84"),sQuery(id+"F0.wireOp",EDGE,"E85"),sQuery(id+"F0.wireOp",EDGE,"E86"),sQuery(id+"F0.wireOp",EDGE,"E87"),sQuery(id+"F0.wireOp",EDGE,"E88"),sQuery(id+"F0.wireOp",EDGE,"E89"),sQuery(id+"F0.wireOp",EDGE,"E90"),sQuery(id+"F0.wireOp",EDGE,"E91"),sQuery(id+"F0.wireOp",EDGE,"E92"),sQuery(id+"F0.wireOp",EDGE,"E93"),sQuery(id+"F0.wireOp",EDGE,"E94"),sQuery(id+"F0.wireOp",EDGE,"E95"),sQuery(id+"F0.wireOp",EDGE,"E96"),sQuery(id+"F0.wireOp",EDGE,"E97")])]});
            var Q12;
            Q12=makeQuery(id+"F1.opExtrude","SWEPT_BODY",BODY,{"disambiguationData":[OSD([sQuery(id+"F0.wireOp",EDGE,"E1207"),sQuery(id+"F0.wireOp",EDGE,"E1208"),sQuery(id+"F0.wireOp",EDGE,"E1209"),sQuery(id+"F0.wireOp",EDGE,"E1210"),sQuery(id+"F0.wireOp",EDGE,"E1211"),sQuery(id+"F0.wireOp",EDGE,"E1212"),sQuery(id+"F0.wireOp",EDGE,"E1213"),sQuery(id+"F0.wireOp",EDGE,"E1214"),sQuery(id+"F0.wireOp",EDGE,"E1215"),sQuery(id+"F0.wireOp",EDGE,"E1216"),sQuery(id+"F0.wireOp",EDGE,"E1217"),sQuery(id+"F0.wireOp",EDGE,"E1218")])]});
            var Q13;
            Q13=makeQuery(id+"F1.opExtrude","SWEPT_BODY",BODY,{"disambiguationData":[OSD([sQuery(id+"F0.wireOp",EDGE,"E1219"),sQuery(id+"F0.wireOp",EDGE,"E1220"),sQuery(id+"F0.wireOp",EDGE,"E1221"),sQuery(id+"F0.wireOp",EDGE,"E1222"),sQuery(id+"F0.wireOp",EDGE,"E1223"),sQuery(id+"F0.wireOp",EDGE,"E1224"),sQuery(id+"F0.wireOp",EDGE,"E1225"),sQuery(id+"F0.wireOp",EDGE,"E1226"),sQuery(id+"F0.wireOp",EDGE,"E1227"),sQuery(id+"F0.wireOp",EDGE,"E1228"),sQuery(id+"F0.wireOp",EDGE,"E1229")])]});
            var Q14;
            Q14=makeQuery(id+"F1.opExtrude","SWEPT_BODY",BODY,{"disambiguationData":[OSD([sQuery(id+"F0.wireOp",EDGE,"E1230"),sQuery(id+"F0.wireOp",EDGE,"E1231"),sQuery(id+"F0.wireOp",EDGE,"E1232"),sQuery(id+"F0.wireOp",EDGE,"E1233"),sQuery(id+"F0.wireOp",EDGE,"E1234"),sQuery(id+"F0.wireOp",EDGE,"E1235"),sQuery(id+"F0.wireOp",EDGE,"E1236"),sQuery(id+"F0.wireOp",EDGE,"E1237"),sQuery(id+"F0.wireOp",EDGE,"E1238"),sQuery(id+"F0.wireOp",EDGE,"E1239"),sQuery(id+"F0.wireOp",EDGE,"E1240")])]});
            var Q15;
            Q15=makeQuery(id+"F1.opExtrude","SWEPT_BODY",BODY,{"disambiguationData":[OSD([sQuery(id+"F0.wireOp",EDGE,"E1242"),sQuery(id+"F0.wireOp",EDGE,"E1243"),sQuery(id+"F0.wireOp",EDGE,"E1244"),sQuery(id+"F0.wireOp",EDGE,"E1245"),sQuery(id+"F0.wireOp",EDGE,"E1246"),sQuery(id+"F0.wireOp",EDGE,"E1247"),sQuery(id+"F0.wireOp",EDGE,"E1248"),sQuery(id+"F0.wireOp",EDGE,"E1249"),sQuery(id+"F0.wireOp",EDGE,"E1250"),sQuery(id+"F0.wireOp",EDGE,"E1251"),sQuery(id+"F0.wireOp",EDGE,"E1252")])]});
            var Q16;
            Q16=makeQuery(id+"F1.opExtrude","SWEPT_BODY",BODY,{"disambiguationData":[OSD([sQuery(id+"F0.wireOp",EDGE,"E1254"),sQuery(id+"F0.wireOp",EDGE,"E1255"),sQuery(id+"F0.wireOp",EDGE,"E1256"),sQuery(id+"F0.wireOp",EDGE,"E1257"),sQuery(id+"F0.wireOp",EDGE,"E1258"),sQuery(id+"F0.wireOp",EDGE,"E1259"),sQuery(id+"F0.wireOp",EDGE,"E1260"),sQuery(id+"F0.wireOp",EDGE,"E1261"),sQuery(id+"F0.wireOp",EDGE,"E1262"),sQuery(id+"F0.wireOp",EDGE,"E1263"),sQuery(id+"F0.wireOp",EDGE,"E1264")])]});
            var Q17;
            Q17=makeQuery(id+"F1.opExtrude","SWEPT_BODY",BODY,{"disambiguationData":[OSD([sQuery(id+"F0.wireOp",EDGE,"E1281"),sQuery(id+"F0.wireOp",EDGE,"E1282"),sQuery(id+"F0.wireOp",EDGE,"E1283"),sQuery(id+"F0.wireOp",EDGE,"E1284"),sQuery(id+"F0.wireOp",EDGE,"E1285"),sQuery(id+"F0.wireOp",EDGE,"E1286"),sQuery(id+"F0.wireOp",EDGE,"E1287"),sQuery(id+"F0.wireOp",EDGE,"E1288"),sQuery(id+"F0.wireOp",EDGE,"E1289"),sQuery(id+"F0.wireOp",EDGE,"E1290")])]});
            var Q18;
            Q18=makeQuery(id+"F1.opExtrude","SWEPT_BODY",BODY,{"disambiguationData":[OSD([sQuery(id+"F0.wireOp",EDGE,"E1291"),sQuery(id+"F0.wireOp",EDGE,"E1292"),sQuery(id+"F0.wireOp",EDGE,"E1293"),sQuery(id+"F0.wireOp",EDGE,"E1294"),sQuery(id+"F0.wireOp",EDGE,"E1295"),sQuery(id+"F0.wireOp",EDGE,"E1296"),sQuery(id+"F0.wireOp",EDGE,"E1297"),sQuery(id+"F0.wireOp",EDGE,"E1298"),sQuery(id+"F0.wireOp",EDGE,"E1299"),sQuery(id+"F0.wireOp",EDGE,"E1300"),sQuery(id+"F0.wireOp",EDGE,"E1301"),sQuery(id+"F0.wireOp",EDGE,"E1302"),sQuery(id+"F0.wireOp",EDGE,"E1303"),sQuery(id+"F0.wireOp",EDGE,"E1304"),sQuery(id+"F0.wireOp",EDGE,"E1305"),sQuery(id+"F0.wireOp",EDGE,"E1306")])]});
            var Q19;
            Q19=makeQuery(id+"F1.opExtrude","SWEPT_BODY",BODY,{"disambiguationData":[OSD([sQuery(id+"F0.wireOp",EDGE,"E1347"),sQuery(id+"F0.wireOp",EDGE,"E1348"),sQuery(id+"F0.wireOp",EDGE,"E1349"),sQuery(id+"F0.wireOp",EDGE,"E1350"),sQuery(id+"F0.wireOp",EDGE,"E1351"),sQuery(id+"F0.wireOp",EDGE,"E1352"),sQuery(id+"F0.wireOp",EDGE,"E1353"),sQuery(id+"F0.wireOp",EDGE,"E1354"),sQuery(id+"F0.wireOp",EDGE,"E1355"),sQuery(id+"F0.wireOp",EDGE,"E1356"),sQuery(id+"F0.wireOp",EDGE,"E1357"),sQuery(id+"F0.wireOp",EDGE,"E1358"),sQuery(id+"F0.wireOp",EDGE,"E1359"),sQuery(id+"F0.wireOp",EDGE,"E1360"),sQuery(id+"F0.wireOp",EDGE,"E1361"),sQuery(id+"F0.wireOp",EDGE,"E1362"),sQuery(id+"F0.wireOp",EDGE,"E1363"),sQuery(id+"F0.wireOp",EDGE,"E1364"),sQuery(id+"F0.wireOp",EDGE,"E1365"),sQuery(id+"F0.wireOp",EDGE,"E1366"),sQuery(id+"F0.wireOp",EDGE,"E1367"),sQuery(id+"F0.wireOp",EDGE,"E1368"),sQuery(id+"F0.wireOp",EDGE,"E1369"),sQuery(id+"F0.wireOp",EDGE,"E1370"),sQuery(id+"F0.wireOp",EDGE,"E1371"),sQuery(id+"F0.wireOp",EDGE,"E1372"),sQuery(id+"F0.wireOp",EDGE,"E1373"),sQuery(id+"F0.wireOp",EDGE,"E1374"),sQuery(id+"F0.wireOp",EDGE,"E1375"),sQuery(id+"F0.wireOp",EDGE,"E1376"),sQuery(id+"F0.wireOp",EDGE,"E1377"),sQuery(id+"F0.wireOp",EDGE,"E1378"),sQuery(id+"F0.wireOp",EDGE,"E1379"),sQuery(id+"F0.wireOp",EDGE,"E1380"),sQuery(id+"F0.wireOp",EDGE,"E1381"),sQuery(id+"F0.wireOp",EDGE,"E1382"),sQuery(id+"F0.wireOp",EDGE,"E1383"),sQuery(id+"F0.wireOp",EDGE,"E1384"),sQuery(id+"F0.wireOp",EDGE,"E1385"),sQuery(id+"F0.wireOp",EDGE,"E1386"),sQuery(id+"F0.wireOp",EDGE,"E1387"),sQuery(id+"F0.wireOp",EDGE,"E1388"),sQuery(id+"F0.wireOp",EDGE,"E1389"),sQuery(id+"F0.wireOp",EDGE,"E1390"),sQuery(id+"F0.wireOp",EDGE,"E1391"),sQuery(id+"F0.wireOp",EDGE,"E1392"),sQuery(id+"F0.wireOp",EDGE,"E1393"),sQuery(id+"F0.wireOp",EDGE,"E1394"),sQuery(id+"F0.wireOp",EDGE,"E1395"),sQuery(id+"F0.wireOp",EDGE,"E1396"),sQuery(id+"F0.wireOp",EDGE,"E1397"),sQuery(id+"F0.wireOp",EDGE,"E1398"),sQuery(id+"F0.wireOp",EDGE,"E1399"),sQuery(id+"F0.wireOp",EDGE,"E1400"),sQuery(id+"F0.wireOp",EDGE,"E1401"),sQuery(id+"F0.wireOp",EDGE,"E1402"),sQuery(id+"F0.wireOp",EDGE,"E1403"),sQuery(id+"F0.wireOp",EDGE,"E1404"),sQuery(id+"F0.wireOp",EDGE,"E1405"),sQuery(id+"F0.wireOp",EDGE,"E1406"),sQuery(id+"F0.wireOp",EDGE,"E1407"),sQuery(id+"F0.wireOp",EDGE,"E1408"),sQuery(id+"F0.wireOp",EDGE,"E1409"),sQuery(id+"F0.wireOp",EDGE,"E1410"),sQuery(id+"F0.wireOp",EDGE,"E1411"),sQuery(id+"F0.wireOp",EDGE,"E1412"),sQuery(id+"F0.wireOp",EDGE,"E1413"),sQuery(id+"F0.wireOp",EDGE,"E1414"),sQuery(id+"F0.wireOp",EDGE,"E1415"),sQuery(id+"F0.wireOp",EDGE,"E1416"),sQuery(id+"F0.wireOp",EDGE,"E1417"),sQuery(id+"F0.wireOp",EDGE,"E1418"),sQuery(id+"F0.wireOp",EDGE,"E1419"),sQuery(id+"F0.wireOp",EDGE,"E1420"),sQuery(id+"F0.wireOp",EDGE,"E1421"),sQuery(id+"F0.wireOp",EDGE,"E1422"),sQuery(id+"F0.wireOp",EDGE,"E1423"),sQuery(id+"F0.wireOp",EDGE,"E1424"),sQuery(id+"F0.wireOp",EDGE,"E1425"),sQuery(id+"F0.wireOp",EDGE,"E1426"),sQuery(id+"F0.wireOp",EDGE,"E1427"),sQuery(id+"F0.wireOp",EDGE,"E1428"),sQuery(id+"F0.wireOp",EDGE,"E1429"),sQuery(id+"F0.wireOp",EDGE,"E1430")])]});
            var Q20;
            Q20=makeQuery(id+"F1.opExtrude","SWEPT_BODY",BODY,{"disambiguationData":[OSD([sQuery(id+"F0.wireOp",EDGE,"E2037"),sQuery(id+"F0.wireOp",EDGE,"E2038"),sQuery(id+"F0.wireOp",EDGE,"E2039"),sQuery(id+"F0.wireOp",EDGE,"E2040"),sQuery(id+"F0.wireOp",EDGE,"E2041"),sQuery(id+"F0.wireOp",EDGE,"E2042"),sQuery(id+"F0.wireOp",EDGE,"E2043"),sQuery(id+"F0.wireOp",EDGE,"E2044"),sQuery(id+"F0.wireOp",EDGE,"E2045"),sQuery(id+"F0.wireOp",EDGE,"E2046"),sQuery(id+"F0.wireOp",EDGE,"E2047")])]});
            var Q21;
            Q21=makeQuery(id+"F1.opExtrude","SWEPT_BODY",BODY,{"disambiguationData":[OSD([sQuery(id+"F0.wireOp",EDGE,"E3038"),sQuery(id+"F0.wireOp",EDGE,"E3039"),sQuery(id+"F0.wireOp",EDGE,"E3040"),sQuery(id+"F0.wireOp",EDGE,"E3041"),sQuery(id+"F0.wireOp",EDGE,"E3042"),sQuery(id+"F0.wireOp",EDGE,"E3043"),sQuery(id+"F0.wireOp",EDGE,"E3044"),sQuery(id+"F0.wireOp",EDGE,"E3045"),sQuery(id+"F0.wireOp",EDGE,"E3046"),sQuery(id+"F0.wireOp",EDGE,"E3047"),sQuery(id+"F0.wireOp",EDGE,"E3048"),sQuery(id+"F0.wireOp",EDGE,"E3049")])]});
            var Q22;
            Q22=makeQuery(id+"F1.opExtrude","SWEPT_BODY",BODY,{"disambiguationData":[OSD([sQuery(id+"F0.wireOp",EDGE,"E3051"),sQuery(id+"F0.wireOp",EDGE,"E3052"),sQuery(id+"F0.wireOp",EDGE,"E3053"),sQuery(id+"F0.wireOp",EDGE,"E3054"),sQuery(id+"F0.wireOp",EDGE,"E3055"),sQuery(id+"F0.wireOp",EDGE,"E3056"),sQuery(id+"F0.wireOp",EDGE,"E3057"),sQuery(id+"F0.wireOp",EDGE,"E3058"),sQuery(id+"F0.wireOp",EDGE,"E3059"),sQuery(id+"F0.wireOp",EDGE,"E3060"),sQuery(id+"F0.wireOp",EDGE,"E3061")])]});
            var Q23;
            Q23=makeQuery(id+"F1.opExtrude","SWEPT_BODY",BODY,{"disambiguationData":[OSD([sQuery(id+"F0.wireOp",EDGE,"E3062"),sQuery(id+"F0.wireOp",EDGE,"E3063"),sQuery(id+"F0.wireOp",EDGE,"E3064"),sQuery(id+"F0.wireOp",EDGE,"E3065"),sQuery(id+"F0.wireOp",EDGE,"E3066"),sQuery(id+"F0.wireOp",EDGE,"E3067"),sQuery(id+"F0.wireOp",EDGE,"E3068"),sQuery(id+"F0.wireOp",EDGE,"E3069"),sQuery(id+"F0.wireOp",EDGE,"E3070"),sQuery(id+"F0.wireOp",EDGE,"E3071"),sQuery(id+"F0.wireOp",EDGE,"E3072")])]});
            var Q24;
            Q24=makeQuery(id+"F1.opExtrude","SWEPT_BODY",BODY,{"disambiguationData":[OSD([sQuery(id+"F0.wireOp",EDGE,"E3164"),sQuery(id+"F0.wireOp",EDGE,"E3165"),sQuery(id+"F0.wireOp",EDGE,"E3166"),sQuery(id+"F0.wireOp",EDGE,"E3167"),sQuery(id+"F0.wireOp",EDGE,"E3168"),sQuery(id+"F0.wireOp",EDGE,"E3169"),sQuery(id+"F0.wireOp",EDGE,"E3170"),sQuery(id+"F0.wireOp",EDGE,"E3171"),sQuery(id+"F0.wireOp",EDGE,"E3172"),sQuery(id+"F0.wireOp",EDGE,"E3173"),sQuery(id+"F0.wireOp",EDGE,"E3174"),sQuery(id+"F0.wireOp",EDGE,"E3175"),sQuery(id+"F0.wireOp",EDGE,"E3176"),sQuery(id+"F0.wireOp",EDGE,"E3177"),sQuery(id+"F0.wireOp",EDGE,"E3178"),sQuery(id+"F0.wireOp",EDGE,"E3179"),sQuery(id+"F0.wireOp",EDGE,"E3180"),sQuery(id+"F0.wireOp",EDGE,"E3181"),sQuery(id+"F0.wireOp",EDGE,"E3182"),sQuery(id+"F0.wireOp",EDGE,"E3183"),sQuery(id+"F0.wireOp",EDGE,"E3184"),sQuery(id+"F0.wireOp",EDGE,"E3185"),sQuery(id+"F0.wireOp",EDGE,"E3186"),sQuery(id+"F0.wireOp",EDGE,"E3187"),sQuery(id+"F0.wireOp",EDGE,"E3188"),sQuery(id+"F0.wireOp",EDGE,"E3189"),sQuery(id+"F0.wireOp",EDGE,"E3190"),sQuery(id+"F0.wireOp",EDGE,"E3191"),sQuery(id+"F0.wireOp",EDGE,"E3192"),sQuery(id+"F0.wireOp",EDGE,"E3193"),sQuery(id+"F0.wireOp",EDGE,"E3194"),sQuery(id+"F0.wireOp",EDGE,"E3195"),sQuery(id+"F0.wireOp",EDGE,"E3196"),sQuery(id+"F0.wireOp",EDGE,"E3197"),sQuery(id+"F0.wireOp",EDGE,"E3198"),sQuery(id+"F0.wireOp",EDGE,"E3199"),sQuery(id+"F0.wireOp",EDGE,"E3200"),sQuery(id+"F0.wireOp",EDGE,"E3201"),sQuery(id+"F0.wireOp",EDGE,"E3202"),sQuery(id+"F0.wireOp",EDGE,"E3203"),sQuery(id+"F0.wireOp",EDGE,"E3204"),sQuery(id+"F0.wireOp",EDGE,"E3205"),sQuery(id+"F0.wireOp",EDGE,"E3206"),sQuery(id+"F0.wireOp",EDGE,"E3207"),sQuery(id+"F0.wireOp",EDGE,"E3208"),sQuery(id+"F0.wireOp",EDGE,"E3209"),sQuery(id+"F0.wireOp",EDGE,"E3210"),sQuery(id+"F0.wireOp",EDGE,"E3211"),sQuery(id+"F0.wireOp",EDGE,"E3212"),sQuery(id+"F0.wireOp",EDGE,"E3213"),sQuery(id+"F0.wireOp",EDGE,"E3214"),sQuery(id+"F0.wireOp",EDGE,"E3215"),sQuery(id+"F0.wireOp",EDGE,"E3216"),sQuery(id+"F0.wireOp",EDGE,"E3217"),sQuery(id+"F0.wireOp",EDGE,"E3218"),sQuery(id+"F0.wireOp",EDGE,"E3219"),sQuery(id+"F0.wireOp",EDGE,"E3220"),sQuery(id+"F0.wireOp",EDGE,"E3221"),sQuery(id+"F0.wireOp",EDGE,"E3222"),sQuery(id+"F0.wireOp",EDGE,"E3223"),sQuery(id+"F0.wireOp",EDGE,"E3224"),sQuery(id+"F0.wireOp",EDGE,"E3225"),sQuery(id+"F0.wireOp",EDGE,"E3226"),sQuery(id+"F0.wireOp",EDGE,"E3227"),sQuery(id+"F0.wireOp",EDGE,"E3228"),sQuery(id+"F0.wireOp",EDGE,"E3229"),sQuery(id+"F0.wireOp",EDGE,"E3230"),sQuery(id+"F0.wireOp",EDGE,"E3231"),sQuery(id+"F0.wireOp",EDGE,"E3232"),sQuery(id+"F0.wireOp",EDGE,"E3233"),sQuery(id+"F0.wireOp",EDGE,"E3234"),sQuery(id+"F0.wireOp",EDGE,"E3235"),sQuery(id+"F0.wireOp",EDGE,"E3236"),sQuery(id+"F0.wireOp",EDGE,"E3237"),sQuery(id+"F0.wireOp",EDGE,"E3238"),sQuery(id+"F0.wireOp",EDGE,"E3239"),sQuery(id+"F0.wireOp",EDGE,"E3240"),sQuery(id+"F0.wireOp",EDGE,"E3241"),sQuery(id+"F0.wireOp",EDGE,"E3242"),sQuery(id+"F0.wireOp",EDGE,"E3243"),sQuery(id+"F0.wireOp",EDGE,"E3244"),sQuery(id+"F0.wireOp",EDGE,"E3245"),sQuery(id+"F0.wireOp",EDGE,"E3246"),sQuery(id+"F0.wireOp",EDGE,"E3247"),sQuery(id+"F0.wireOp",EDGE,"E3248"),sQuery(id+"F0.wireOp",EDGE,"E3249"),sQuery(id+"F0.wireOp",EDGE,"E3250"),sQuery(id+"F0.wireOp",EDGE,"E3251"),sQuery(id+"F0.wireOp",EDGE,"E3252"),sQuery(id+"F0.wireOp",EDGE,"E3253"),sQuery(id+"F0.wireOp",EDGE,"E3254"),sQuery(id+"F0.wireOp",EDGE,"E3255")])]});
            var Q25;
            Q25=makeQuery(id+"F1.opExtrude","SWEPT_BODY",BODY,{"disambiguationData":[OSD([sQuery(id+"F0.wireOp",EDGE,"E3256"),sQuery(id+"F0.wireOp",EDGE,"E3257"),sQuery(id+"F0.wireOp",EDGE,"E3258"),sQuery(id+"F0.wireOp",EDGE,"E3259"),sQuery(id+"F0.wireOp",EDGE,"E3260"),sQuery(id+"F0.wireOp",EDGE,"E3261"),sQuery(id+"F0.wireOp",EDGE,"E3262"),sQuery(id+"F0.wireOp",EDGE,"E3263"),sQuery(id+"F0.wireOp",EDGE,"E3264"),sQuery(id+"F0.wireOp",EDGE,"E3265"),sQuery(id+"F0.wireOp",EDGE,"E3266"),sQuery(id+"F0.wireOp",EDGE,"E3267"),sQuery(id+"F0.wireOp",EDGE,"E3268"),sQuery(id+"F0.wireOp",EDGE,"E3269"),sQuery(id+"F0.wireOp",EDGE,"E3270"),sQuery(id+"F0.wireOp",EDGE,"E3271"),sQuery(id+"F0.wireOp",EDGE,"E3272"),sQuery(id+"F0.wireOp",EDGE,"E3273"),sQuery(id+"F0.wireOp",EDGE,"E3274"),sQuery(id+"F0.wireOp",EDGE,"E3275"),sQuery(id+"F0.wireOp",EDGE,"E3276"),sQuery(id+"F0.wireOp",EDGE,"E3277"),sQuery(id+"F0.wireOp",EDGE,"E3278"),sQuery(id+"F0.wireOp",EDGE,"E3279"),sQuery(id+"F0.wireOp",EDGE,"E3280"),sQuery(id+"F0.wireOp",EDGE,"E3281"),sQuery(id+"F0.wireOp",EDGE,"E3282"),sQuery(id+"F0.wireOp",EDGE,"E3283"),sQuery(id+"F0.wireOp",EDGE,"E3284"),sQuery(id+"F0.wireOp",EDGE,"E3285"),sQuery(id+"F0.wireOp",EDGE,"E3286"),sQuery(id+"F0.wireOp",EDGE,"E3287"),sQuery(id+"F0.wireOp",EDGE,"E3288"),sQuery(id+"F0.wireOp",EDGE,"E3289"),sQuery(id+"F0.wireOp",EDGE,"E3290"),sQuery(id+"F0.wireOp",EDGE,"E3291"),sQuery(id+"F0.wireOp",EDGE,"E3292"),sQuery(id+"F0.wireOp",EDGE,"E3293"),sQuery(id+"F0.wireOp",EDGE,"E3294"),sQuery(id+"F0.wireOp",EDGE,"E3295"),sQuery(id+"F0.wireOp",EDGE,"E3296"),sQuery(id+"F0.wireOp",EDGE,"E3297"),sQuery(id+"F0.wireOp",EDGE,"E3298"),sQuery(id+"F0.wireOp",EDGE,"E3299"),sQuery(id+"F0.wireOp",EDGE,"E3300"),sQuery(id+"F0.wireOp",EDGE,"E3301"),sQuery(id+"F0.wireOp",EDGE,"E3302"),sQuery(id+"F0.wireOp",EDGE,"E3303"),sQuery(id+"F0.wireOp",EDGE,"E3304"),sQuery(id+"F0.wireOp",EDGE,"E3305"),sQuery(id+"F0.wireOp",EDGE,"E3306"),sQuery(id+"F0.wireOp",EDGE,"E3307"),sQuery(id+"F0.wireOp",EDGE,"E3308"),sQuery(id+"F0.wireOp",EDGE,"E3309"),sQuery(id+"F0.wireOp",EDGE,"E3310"),sQuery(id+"F0.wireOp",EDGE,"E3311"),sQuery(id+"F0.wireOp",EDGE,"E3312"),sQuery(id+"F0.wireOp",EDGE,"E3313"),sQuery(id+"F0.wireOp",EDGE,"E3314"),sQuery(id+"F0.wireOp",EDGE,"E3315"),sQuery(id+"F0.wireOp",EDGE,"E3316"),sQuery(id+"F0.wireOp",EDGE,"E3317"),sQuery(id+"F0.wireOp",EDGE,"E3318"),sQuery(id+"F0.wireOp",EDGE,"E3319"),sQuery(id+"F0.wireOp",EDGE,"E3320"),sQuery(id+"F0.wireOp",EDGE,"E3321"),sQuery(id+"F0.wireOp",EDGE,"E3322"),sQuery(id+"F0.wireOp",EDGE,"E3323"),sQuery(id+"F0.wireOp",EDGE,"E3324"),sQuery(id+"F0.wireOp",EDGE,"E3325"),sQuery(id+"F0.wireOp",EDGE,"E3326"),sQuery(id+"F0.wireOp",EDGE,"E3327"),sQuery(id+"F0.wireOp",EDGE,"E3328"),sQuery(id+"F0.wireOp",EDGE,"E3329"),sQuery(id+"F0.wireOp",EDGE,"E3330"),sQuery(id+"F0.wireOp",EDGE,"E3331"),sQuery(id+"F0.wireOp",EDGE,"E3332"),sQuery(id+"F0.wireOp",EDGE,"E3333"),sQuery(id+"F0.wireOp",EDGE,"E3334"),sQuery(id+"F0.wireOp",EDGE,"E3335"),sQuery(id+"F0.wireOp",EDGE,"E3336"),sQuery(id+"F0.wireOp",EDGE,"E3337"),sQuery(id+"F0.wireOp",EDGE,"E3338"),sQuery(id+"F0.wireOp",EDGE,"E3339"),sQuery(id+"F0.wireOp",EDGE,"E3340"),sQuery(id+"F0.wireOp",EDGE,"E3341"),sQuery(id+"F0.wireOp",EDGE,"E3342"),sQuery(id+"F0.wireOp",EDGE,"E3343"),sQuery(id+"F0.wireOp",EDGE,"E3344"),sQuery(id+"F0.wireOp",EDGE,"E3345"),sQuery(id+"F0.wireOp",EDGE,"E3346"),sQuery(id+"F0.wireOp",EDGE,"E3347"),sQuery(id+"F0.wireOp",EDGE,"E3348"),sQuery(id+"F0.wireOp",EDGE,"E3349"),sQuery(id+"F0.wireOp",EDGE,"E3350"),sQuery(id+"F0.wireOp",EDGE,"E3351"),sQuery(id+"F0.wireOp",EDGE,"E3352")])]});
            var Q26;
            Q26=makeQuery(id+"F1.opExtrude","SWEPT_BODY",BODY,{"disambiguationData":[OSD([sQuery(id+"F0.wireOp",EDGE,"E1195"),sQuery(id+"F0.wireOp",EDGE,"E1196"),sQuery(id+"F0.wireOp",EDGE,"E1197"),sQuery(id+"F0.wireOp",EDGE,"E1198"),sQuery(id+"F0.wireOp",EDGE,"E1199"),sQuery(id+"F0.wireOp",EDGE,"E1200"),sQuery(id+"F0.wireOp",EDGE,"E1201"),sQuery(id+"F0.wireOp",EDGE,"E1202"),sQuery(id+"F0.wireOp",EDGE,"E1203"),sQuery(id+"F0.wireOp",EDGE,"E1204"),sQuery(id+"F0.wireOp",EDGE,"E1205"),sQuery(id+"F0.wireOp",EDGE,"E1206")])]});
            var Q27;
            Q27=makeQuery(id+"F1.opExtrude","SWEPT_BODY",BODY,{"disambiguationData":[OSD([sQuery(id+"F0.wireOp",EDGE,"E1332"),sQuery(id+"F0.wireOp",EDGE,"E1333"),sQuery(id+"F0.wireOp",EDGE,"E1334"),sQuery(id+"F0.wireOp",EDGE,"E1335"),sQuery(id+"F0.wireOp",EDGE,"E1336"),sQuery(id+"F0.wireOp",EDGE,"E1337"),sQuery(id+"F0.wireOp",EDGE,"E1338"),sQuery(id+"F0.wireOp",EDGE,"E1339"),sQuery(id+"F0.wireOp",EDGE,"E1340"),sQuery(id+"F0.wireOp",EDGE,"E1341"),sQuery(id+"F0.wireOp",EDGE,"E1342")])]});
            var Q28;
            Q28=makeQuery(id+"F1.opExtrude","SWEPT_BODY",BODY,{"disambiguationData":[OSD([sQuery(id+"F0.wireOp",EDGE,"E1863"),sQuery(id+"F0.wireOp",EDGE,"E1864"),sQuery(id+"F0.wireOp",EDGE,"E1865"),sQuery(id+"F0.wireOp",EDGE,"E1866"),sQuery(id+"F0.wireOp",EDGE,"E1867"),sQuery(id+"F0.wireOp",EDGE,"E1868"),sQuery(id+"F0.wireOp",EDGE,"E1869"),sQuery(id+"F0.wireOp",EDGE,"E1870"),sQuery(id+"F0.wireOp",EDGE,"E1871"),sQuery(id+"F0.wireOp",EDGE,"E1872"),sQuery(id+"F0.wireOp",EDGE,"E1873"),sQuery(id+"F0.wireOp",EDGE,"E1874")])]});
            var Q29;
            Q29=makeQuery(id+"F1.opExtrude","SWEPT_BODY",BODY,{"disambiguationData":[OSD([sQuery(id+"F0.wireOp",EDGE,"E2048"),sQuery(id+"F0.wireOp",EDGE,"E2049"),sQuery(id+"F0.wireOp",EDGE,"E2050"),sQuery(id+"F0.wireOp",EDGE,"E2051"),sQuery(id+"F0.wireOp",EDGE,"E2052"),sQuery(id+"F0.wireOp",EDGE,"E2053"),sQuery(id+"F0.wireOp",EDGE,"E2054"),sQuery(id+"F0.wireOp",EDGE,"E2055"),sQuery(id+"F0.wireOp",EDGE,"E2056"),sQuery(id+"F0.wireOp",EDGE,"E2057"),sQuery(id+"F0.wireOp",EDGE,"E2058"),sQuery(id+"F0.wireOp",EDGE,"E2059"),sQuery(id+"F0.wireOp",EDGE,"E2060"),sQuery(id+"F0.wireOp",EDGE,"E2061"),sQuery(id+"F0.wireOp",EDGE,"E2062"),sQuery(id+"F0.wireOp",EDGE,"E2063"),sQuery(id+"F0.wireOp",EDGE,"E2064"),sQuery(id+"F0.wireOp",EDGE,"E2065"),sQuery(id+"F0.wireOp",EDGE,"E2066"),sQuery(id+"F0.wireOp",EDGE,"E2067"),sQuery(id+"F0.wireOp",EDGE,"E2068"),sQuery(id+"F0.wireOp",EDGE,"E2069"),sQuery(id+"F0.wireOp",EDGE,"E2070"),sQuery(id+"F0.wireOp",EDGE,"E2071"),sQuery(id+"F0.wireOp",EDGE,"E2072"),sQuery(id+"F0.wireOp",EDGE,"E2073"),sQuery(id+"F0.wireOp",EDGE,"E2074"),sQuery(id+"F0.wireOp",EDGE,"E2075"),sQuery(id+"F0.wireOp",EDGE,"E2076"),sQuery(id+"F0.wireOp",EDGE,"E2077"),sQuery(id+"F0.wireOp",EDGE,"E2078"),sQuery(id+"F0.wireOp",EDGE,"E2079"),sQuery(id+"F0.wireOp",EDGE,"E2080"),sQuery(id+"F0.wireOp",EDGE,"E2081"),sQuery(id+"F0.wireOp",EDGE,"E2082"),sQuery(id+"F0.wireOp",EDGE,"E2083"),sQuery(id+"F0.wireOp",EDGE,"E2084"),sQuery(id+"F0.wireOp",EDGE,"E2085"),sQuery(id+"F0.wireOp",EDGE,"E2086"),sQuery(id+"F0.wireOp",EDGE,"E2087"),sQuery(id+"F0.wireOp",EDGE,"E2088"),sQuery(id+"F0.wireOp",EDGE,"E2089"),sQuery(id+"F0.wireOp",EDGE,"E2090"),sQuery(id+"F0.wireOp",EDGE,"E2091"),sQuery(id+"F0.wireOp",EDGE,"E2092"),sQuery(id+"F0.wireOp",EDGE,"E2093"),sQuery(id+"F0.wireOp",EDGE,"E2094"),sQuery(id+"F0.wireOp",EDGE,"E2095"),sQuery(id+"F0.wireOp",EDGE,"E2096"),sQuery(id+"F0.wireOp",EDGE,"E2097"),sQuery(id+"F0.wireOp",EDGE,"E2098"),sQuery(id+"F0.wireOp",EDGE,"E2099"),sQuery(id+"F0.wireOp",EDGE,"E2100"),sQuery(id+"F0.wireOp",EDGE,"E2101"),sQuery(id+"F0.wireOp",EDGE,"E2102"),sQuery(id+"F0.wireOp",EDGE,"E2103"),sQuery(id+"F0.wireOp",EDGE,"E2104"),sQuery(id+"F0.wireOp",EDGE,"E2105"),sQuery(id+"F0.wireOp",EDGE,"E2106"),sQuery(id+"F0.wireOp",EDGE,"E2107"),sQuery(id+"F0.wireOp",EDGE,"E2108"),sQuery(id+"F0.wireOp",EDGE,"E2109"),sQuery(id+"F0.wireOp",EDGE,"E2110"),sQuery(id+"F0.wireOp",EDGE,"E2111"),sQuery(id+"F0.wireOp",EDGE,"E2112"),sQuery(id+"F0.wireOp",EDGE,"E2113"),sQuery(id+"F0.wireOp",EDGE,"E2114"),sQuery(id+"F0.wireOp",EDGE,"E2115"),sQuery(id+"F0.wireOp",EDGE,"E2116"),sQuery(id+"F0.wireOp",EDGE,"E2117"),sQuery(id+"F0.wireOp",EDGE,"E2118"),sQuery(id+"F0.wireOp",EDGE,"E2119"),sQuery(id+"F0.wireOp",EDGE,"E2120"),sQuery(id+"F0.wireOp",EDGE,"E2121"),sQuery(id+"F0.wireOp",EDGE,"E2122"),sQuery(id+"F0.wireOp",EDGE,"E2123"),sQuery(id+"F0.wireOp",EDGE,"E2124"),sQuery(id+"F0.wireOp",EDGE,"E2125")])]});
            var Q30;
            Q30=makeQuery(id+"F1.opExtrude","SWEPT_BODY",BODY,{"disambiguationData":[OSD([sQuery(id+"F0.wireOp",EDGE,"E2204"),sQuery(id+"F0.wireOp",EDGE,"E2205"),sQuery(id+"F0.wireOp",EDGE,"E2206"),sQuery(id+"F0.wireOp",EDGE,"E2207"),sQuery(id+"F0.wireOp",EDGE,"E2208"),sQuery(id+"F0.wireOp",EDGE,"E2209"),sQuery(id+"F0.wireOp",EDGE,"E2210"),sQuery(id+"F0.wireOp",EDGE,"E2211"),sQuery(id+"F0.wireOp",EDGE,"E2212"),sQuery(id+"F0.wireOp",EDGE,"E2213"),sQuery(id+"F0.wireOp",EDGE,"E2214"),sQuery(id+"F0.wireOp",EDGE,"E2215"),sQuery(id+"F0.wireOp",EDGE,"E2216"),sQuery(id+"F0.wireOp",EDGE,"E2217"),sQuery(id+"F0.wireOp",EDGE,"E2218"),sQuery(id+"F0.wireOp",EDGE,"E2219"),sQuery(id+"F0.wireOp",EDGE,"E2220"),sQuery(id+"F0.wireOp",EDGE,"E2221"),sQuery(id+"F0.wireOp",EDGE,"E2222"),sQuery(id+"F0.wireOp",EDGE,"E2223"),sQuery(id+"F0.wireOp",EDGE,"E2224"),sQuery(id+"F0.wireOp",EDGE,"E2225"),sQuery(id+"F0.wireOp",EDGE,"E2226"),sQuery(id+"F0.wireOp",EDGE,"E2227"),sQuery(id+"F0.wireOp",EDGE,"E2228"),sQuery(id+"F0.wireOp",EDGE,"E2229"),sQuery(id+"F0.wireOp",EDGE,"E2230"),sQuery(id+"F0.wireOp",EDGE,"E2231"),sQuery(id+"F0.wireOp",EDGE,"E2232"),sQuery(id+"F0.wireOp",EDGE,"E2233"),sQuery(id+"F0.wireOp",EDGE,"E2234"),sQuery(id+"F0.wireOp",EDGE,"E2235"),sQuery(id+"F0.wireOp",EDGE,"E2236"),sQuery(id+"F0.wireOp",EDGE,"E2237"),sQuery(id+"F0.wireOp",EDGE,"E2238"),sQuery(id+"F0.wireOp",EDGE,"E2239"),sQuery(id+"F0.wireOp",EDGE,"E2240"),sQuery(id+"F0.wireOp",EDGE,"E2241"),sQuery(id+"F0.wireOp",EDGE,"E2242"),sQuery(id+"F0.wireOp",EDGE,"E2243"),sQuery(id+"F0.wireOp",EDGE,"E2244"),sQuery(id+"F0.wireOp",EDGE,"E2245"),sQuery(id+"F0.wireOp",EDGE,"E2246"),sQuery(id+"F0.wireOp",EDGE,"E2247"),sQuery(id+"F0.wireOp",EDGE,"E2248"),sQuery(id+"F0.wireOp",EDGE,"E2249"),sQuery(id+"F0.wireOp",EDGE,"E2250"),sQuery(id+"F0.wireOp",EDGE,"E2251"),sQuery(id+"F0.wireOp",EDGE,"E2252"),sQuery(id+"F0.wireOp",EDGE,"E2253"),sQuery(id+"F0.wireOp",EDGE,"E2254"),sQuery(id+"F0.wireOp",EDGE,"E2255"),sQuery(id+"F0.wireOp",EDGE,"E2256"),sQuery(id+"F0.wireOp",EDGE,"E2257"),sQuery(id+"F0.wireOp",EDGE,"E2258"),sQuery(id+"F0.wireOp",EDGE,"E2259"),sQuery(id+"F0.wireOp",EDGE,"E2260"),sQuery(id+"F0.wireOp",EDGE,"E2261"),sQuery(id+"F0.wireOp",EDGE,"E2262"),sQuery(id+"F0.wireOp",EDGE,"E2263"),sQuery(id+"F0.wireOp",EDGE,"E2264"),sQuery(id+"F0.wireOp",EDGE,"E2265"),sQuery(id+"F0.wireOp",EDGE,"E2266"),sQuery(id+"F0.wireOp",EDGE,"E2267"),sQuery(id+"F0.wireOp",EDGE,"E2268"),sQuery(id+"F0.wireOp",EDGE,"E2269"),sQuery(id+"F0.wireOp",EDGE,"E2270"),sQuery(id+"F0.wireOp",EDGE,"E2271"),sQuery(id+"F0.wireOp",EDGE,"E2272"),sQuery(id+"F0.wireOp",EDGE,"E2273"),sQuery(id+"F0.wireOp",EDGE,"E2274"),sQuery(id+"F0.wireOp",EDGE,"E2275"),sQuery(id+"F0.wireOp",EDGE,"E2276"),sQuery(id+"F0.wireOp",EDGE,"E2277")])]});
            var Q31;
            Q31=makeQuery(id+"F1.opExtrude","SWEPT_BODY",BODY,{"disambiguationData":[OSD([sQuery(id+"F0.wireOp",EDGE,"E2426"),sQuery(id+"F0.wireOp",EDGE,"E2427"),sQuery(id+"F0.wireOp",EDGE,"E2428"),sQuery(id+"F0.wireOp",EDGE,"E2429"),sQuery(id+"F0.wireOp",EDGE,"E2430"),sQuery(id+"F0.wireOp",EDGE,"E2431"),sQuery(id+"F0.wireOp",EDGE,"E2432"),sQuery(id+"F0.wireOp",EDGE,"E2433"),sQuery(id+"F0.wireOp",EDGE,"E2434"),sQuery(id+"F0.wireOp",EDGE,"E2435"),sQuery(id+"F0.wireOp",EDGE,"E2436"),sQuery(id+"F0.wireOp",EDGE,"E2437")])]});
            var Q32;
            Q32=makeQuery(id+"F1.opExtrude","SWEPT_BODY",BODY,{"disambiguationData":[OSD([sQuery(id+"F0.wireOp",EDGE,"E2456"),sQuery(id+"F0.wireOp",EDGE,"E2457"),sQuery(id+"F0.wireOp",EDGE,"E2458"),sQuery(id+"F0.wireOp",EDGE,"E2459"),sQuery(id+"F0.wireOp",EDGE,"E2460"),sQuery(id+"F0.wireOp",EDGE,"E2461"),sQuery(id+"F0.wireOp",EDGE,"E2462"),sQuery(id+"F0.wireOp",EDGE,"E2463")])]});
            var Q33;
            Q33=makeQuery(id+"F1.opExtrude","SWEPT_BODY",BODY,{"disambiguationData":[OSD([sQuery(id+"F0.wireOp",EDGE,"E2557"),sQuery(id+"F0.wireOp",EDGE,"E2558"),sQuery(id+"F0.wireOp",EDGE,"E2559"),sQuery(id+"F0.wireOp",EDGE,"E2560"),sQuery(id+"F0.wireOp",EDGE,"E2561"),sQuery(id+"F0.wireOp",EDGE,"E2562"),sQuery(id+"F0.wireOp",EDGE,"E2563"),sQuery(id+"F0.wireOp",EDGE,"E2564"),sQuery(id+"F0.wireOp",EDGE,"E2565"),sQuery(id+"F0.wireOp",EDGE,"E2566"),sQuery(id+"F0.wireOp",EDGE,"E2567"),sQuery(id+"F0.wireOp",EDGE,"E2568"),sQuery(id+"F0.wireOp",EDGE,"E2569"),sQuery(id+"F0.wireOp",EDGE,"E2570"),sQuery(id+"F0.wireOp",EDGE,"E2571"),sQuery(id+"F0.wireOp",EDGE,"E2572"),sQuery(id+"F0.wireOp",EDGE,"E2573"),sQuery(id+"F0.wireOp",EDGE,"E2574"),sQuery(id+"F0.wireOp",EDGE,"E2575"),sQuery(id+"F0.wireOp",EDGE,"E2576"),sQuery(id+"F0.wireOp",EDGE,"E2577"),sQuery(id+"F0.wireOp",EDGE,"E2578"),sQuery(id+"F0.wireOp",EDGE,"E2579"),sQuery(id+"F0.wireOp",EDGE,"E2580"),sQuery(id+"F0.wireOp",EDGE,"E2581"),sQuery(id+"F0.wireOp",EDGE,"E2582"),sQuery(id+"F0.wireOp",EDGE,"E2583"),sQuery(id+"F0.wireOp",EDGE,"E2584"),sQuery(id+"F0.wireOp",EDGE,"E2585"),sQuery(id+"F0.wireOp",EDGE,"E2586"),sQuery(id+"F0.wireOp",EDGE,"E2587"),sQuery(id+"F0.wireOp",EDGE,"E2588"),sQuery(id+"F0.wireOp",EDGE,"E2589"),sQuery(id+"F0.wireOp",EDGE,"E2590"),sQuery(id+"F0.wireOp",EDGE,"E2591"),sQuery(id+"F0.wireOp",EDGE,"E2592"),sQuery(id+"F0.wireOp",EDGE,"E2593"),sQuery(id+"F0.wireOp",EDGE,"E2594"),sQuery(id+"F0.wireOp",EDGE,"E2595"),sQuery(id+"F0.wireOp",EDGE,"E2596"),sQuery(id+"F0.wireOp",EDGE,"E2597"),sQuery(id+"F0.wireOp",EDGE,"E2598"),sQuery(id+"F0.wireOp",EDGE,"E2599"),sQuery(id+"F0.wireOp",EDGE,"E2600"),sQuery(id+"F0.wireOp",EDGE,"E2601"),sQuery(id+"F0.wireOp",EDGE,"E2602")])]});
            var Q34;
            Q34=makeQuery(id+"F1.opExtrude","SWEPT_BODY",BODY,{"disambiguationData":[OSD([sQuery(id+"F0.wireOp",EDGE,"E3353"),sQuery(id+"F0.wireOp",EDGE,"E3354"),sQuery(id+"F0.wireOp",EDGE,"E3355"),sQuery(id+"F0.wireOp",EDGE,"E3356"),sQuery(id+"F0.wireOp",EDGE,"E3357"),sQuery(id+"F0.wireOp",EDGE,"E3358"),sQuery(id+"F0.wireOp",EDGE,"E3359"),sQuery(id+"F0.wireOp",EDGE,"E3360"),sQuery(id+"F0.wireOp",EDGE,"E3361"),sQuery(id+"F0.wireOp",EDGE,"E3362"),sQuery(id+"F0.wireOp",EDGE,"E3363"),sQuery(id+"F0.wireOp",EDGE,"E3364"),sQuery(id+"F0.wireOp",EDGE,"E3365"),sQuery(id+"F0.wireOp",EDGE,"E3366"),sQuery(id+"F0.wireOp",EDGE,"E3367"),sQuery(id+"F0.wireOp",EDGE,"E3368"),sQuery(id+"F0.wireOp",EDGE,"E3369"),sQuery(id+"F0.wireOp",EDGE,"E3370"),sQuery(id+"F0.wireOp",EDGE,"E3371"),sQuery(id+"F0.wireOp",EDGE,"E3372"),sQuery(id+"F0.wireOp",EDGE,"E3373"),sQuery(id+"F0.wireOp",EDGE,"E3374"),sQuery(id+"F0.wireOp",EDGE,"E3375"),sQuery(id+"F0.wireOp",EDGE,"E3376"),sQuery(id+"F0.wireOp",EDGE,"E3377"),sQuery(id+"F0.wireOp",EDGE,"E3378"),sQuery(id+"F0.wireOp",EDGE,"E3379"),sQuery(id+"F0.wireOp",EDGE,"E3380"),sQuery(id+"F0.wireOp",EDGE,"E3381"),sQuery(id+"F0.wireOp",EDGE,"E3382"),sQuery(id+"F0.wireOp",EDGE,"E3383"),sQuery(id+"F0.wireOp",EDGE,"E3384"),sQuery(id+"F0.wireOp",EDGE,"E3385"),sQuery(id+"F0.wireOp",EDGE,"E3386"),sQuery(id+"F0.wireOp",EDGE,"E3387"),sQuery(id+"F0.wireOp",EDGE,"E3388"),sQuery(id+"F0.wireOp",EDGE,"E3389"),sQuery(id+"F0.wireOp",EDGE,"E3390"),sQuery(id+"F0.wireOp",EDGE,"E3391"),sQuery(id+"F0.wireOp",EDGE,"E3392"),sQuery(id+"F0.wireOp",EDGE,"E3393"),sQuery(id+"F0.wireOp",EDGE,"E3394"),sQuery(id+"F0.wireOp",EDGE,"E3395"),sQuery(id+"F0.wireOp",EDGE,"E3396"),sQuery(id+"F0.wireOp",EDGE,"E3397"),sQuery(id+"F0.wireOp",EDGE,"E3398"),sQuery(id+"F0.wireOp",EDGE,"E3399"),sQuery(id+"F0.wireOp",EDGE,"E3400"),sQuery(id+"F0.wireOp",EDGE,"E3401"),sQuery(id+"F0.wireOp",EDGE,"E3402"),sQuery(id+"F0.wireOp",EDGE,"E3403"),sQuery(id+"F0.wireOp",EDGE,"E3404"),sQuery(id+"F0.wireOp",EDGE,"E3405"),sQuery(id+"F0.wireOp",EDGE,"E3406"),sQuery(id+"F0.wireOp",EDGE,"E3407"),sQuery(id+"F0.wireOp",EDGE,"E3408"),sQuery(id+"F0.wireOp",EDGE,"E3409"),sQuery(id+"F0.wireOp",EDGE,"E3410"),sQuery(id+"F0.wireOp",EDGE,"E3411"),sQuery(id+"F0.wireOp",EDGE,"E3412"),sQuery(id+"F0.wireOp",EDGE,"E3413"),sQuery(id+"F0.wireOp",EDGE,"E3414"),sQuery(id+"F0.wireOp",EDGE,"E3415"),sQuery(id+"F0.wireOp",EDGE,"E3416"),sQuery(id+"F0.wireOp",EDGE,"E3417"),sQuery(id+"F0.wireOp",EDGE,"E3418"),sQuery(id+"F0.wireOp",EDGE,"E3419"),sQuery(id+"F0.wireOp",EDGE,"E3420"),sQuery(id+"F0.wireOp",EDGE,"E3421"),sQuery(id+"F0.wireOp",EDGE,"E3422"),sQuery(id+"F0.wireOp",EDGE,"E3423"),sQuery(id+"F0.wireOp",EDGE,"E3424"),sQuery(id+"F0.wireOp",EDGE,"E3425"),sQuery(id+"F0.wireOp",EDGE,"E3426"),sQuery(id+"F0.wireOp",EDGE,"E3427"),sQuery(id+"F0.wireOp",EDGE,"E3428"),sQuery(id+"F0.wireOp",EDGE,"E3429"),sQuery(id+"F0.wireOp",EDGE,"E3430"),sQuery(id+"F0.wireOp",EDGE,"E3431"),sQuery(id+"F0.wireOp",EDGE,"E3432"),sQuery(id+"F0.wireOp",EDGE,"E3433"),sQuery(id+"F0.wireOp",EDGE,"E3434"),sQuery(id+"F0.wireOp",EDGE,"E3435"),sQuery(id+"F0.wireOp",EDGE,"E3436"),sQuery(id+"F0.wireOp",EDGE,"E3437"),sQuery(id+"F0.wireOp",EDGE,"E3438"),sQuery(id+"F0.wireOp",EDGE,"E3439"),sQuery(id+"F0.wireOp",EDGE,"E3440"),sQuery(id+"F0.wireOp",EDGE,"E3441"),sQuery(id+"F0.wireOp",EDGE,"E3442"),sQuery(id+"F0.wireOp",EDGE,"E3443"),sQuery(id+"F0.wireOp",EDGE,"E3444"),sQuery(id+"F0.wireOp",EDGE,"E3445"),sQuery(id+"F0.wireOp",EDGE,"E3446"),sQuery(id+"F0.wireOp",EDGE,"E3447"),sQuery(id+"F0.wireOp",EDGE,"E3448"),sQuery(id+"F0.wireOp",EDGE,"E3449")])]});
            var Q35;
            Q35=makeQuery(id+"F1.opExtrude","SWEPT_BODY",BODY,{"disambiguationData":[OSD([sQuery(id+"F0.wireOp",EDGE,"E1603"),sQuery(id+"F0.wireOp",EDGE,"E1604"),sQuery(id+"F0.wireOp",EDGE,"E1605"),sQuery(id+"F0.wireOp",EDGE,"E1606"),sQuery(id+"F0.wireOp",EDGE,"E1607"),sQuery(id+"F0.wireOp",EDGE,"E1608"),sQuery(id+"F0.wireOp",EDGE,"E1609"),sQuery(id+"F0.wireOp",EDGE,"E1610"),sQuery(id+"F0.wireOp",EDGE,"E1611"),sQuery(id+"F0.wireOp",EDGE,"E1612"),sQuery(id+"F0.wireOp",EDGE,"E1613"),sQuery(id+"F0.wireOp",EDGE,"E1614"),sQuery(id+"F0.wireOp",EDGE,"E1615"),sQuery(id+"F0.wireOp",EDGE,"E1616"),sQuery(id+"F0.wireOp",EDGE,"E1617"),sQuery(id+"F0.wireOp",EDGE,"E1618"),sQuery(id+"F0.wireOp",EDGE,"E1619"),sQuery(id+"F0.wireOp",EDGE,"E1620"),sQuery(id+"F0.wireOp",EDGE,"E1621"),sQuery(id+"F0.wireOp",EDGE,"E1622"),sQuery(id+"F0.wireOp",EDGE,"E1623"),sQuery(id+"F0.wireOp",EDGE,"E1624"),sQuery(id+"F0.wireOp",EDGE,"E1625"),sQuery(id+"F0.wireOp",EDGE,"E1626"),sQuery(id+"F0.wireOp",EDGE,"E1627"),sQuery(id+"F0.wireOp",EDGE,"E1628"),sQuery(id+"F0.wireOp",EDGE,"E1629"),sQuery(id+"F0.wireOp",EDGE,"E1630"),sQuery(id+"F0.wireOp",EDGE,"E1631"),sQuery(id+"F0.wireOp",EDGE,"E1632"),sQuery(id+"F0.wireOp",EDGE,"E1633"),sQuery(id+"F0.wireOp",EDGE,"E1634"),sQuery(id+"F0.wireOp",EDGE,"E1635"),sQuery(id+"F0.wireOp",EDGE,"E1636"),sQuery(id+"F0.wireOp",EDGE,"E1637"),sQuery(id+"F0.wireOp",EDGE,"E1638"),sQuery(id+"F0.wireOp",EDGE,"E1639"),sQuery(id+"F0.wireOp",EDGE,"E1640"),sQuery(id+"F0.wireOp",EDGE,"E1641"),sQuery(id+"F0.wireOp",EDGE,"E1642"),sQuery(id+"F0.wireOp",EDGE,"E1643"),sQuery(id+"F0.wireOp",EDGE,"E1644"),sQuery(id+"F0.wireOp",EDGE,"E1645"),sQuery(id+"F0.wireOp",EDGE,"E1646"),sQuery(id+"F0.wireOp",EDGE,"E1647"),sQuery(id+"F0.wireOp",EDGE,"E1648"),sQuery(id+"F0.wireOp",EDGE,"E1649"),sQuery(id+"F0.wireOp",EDGE,"E1650"),sQuery(id+"F0.wireOp",EDGE,"E1651"),sQuery(id+"F0.wireOp",EDGE,"E1652"),sQuery(id+"F0.wireOp",EDGE,"E1653"),sQuery(id+"F0.wireOp",EDGE,"E1654"),sQuery(id+"F0.wireOp",EDGE,"E1655"),sQuery(id+"F0.wireOp",EDGE,"E1656"),sQuery(id+"F0.wireOp",EDGE,"E1657"),sQuery(id+"F0.wireOp",EDGE,"E1658"),sQuery(id+"F0.wireOp",EDGE,"E1659"),sQuery(id+"F0.wireOp",EDGE,"E1660"),sQuery(id+"F0.wireOp",EDGE,"E1661"),sQuery(id+"F0.wireOp",EDGE,"E1662"),sQuery(id+"F0.wireOp",EDGE,"E1663"),sQuery(id+"F0.wireOp",EDGE,"E1664"),sQuery(id+"F0.wireOp",EDGE,"E1665"),sQuery(id+"F0.wireOp",EDGE,"E1666"),sQuery(id+"F0.wireOp",EDGE,"E1667"),sQuery(id+"F0.wireOp",EDGE,"E1668"),sQuery(id+"F0.wireOp",EDGE,"E1669"),sQuery(id+"F0.wireOp",EDGE,"E1670"),sQuery(id+"F0.wireOp",EDGE,"E1671"),sQuery(id+"F0.wireOp",EDGE,"E1672"),sQuery(id+"F0.wireOp",EDGE,"E1673"),sQuery(id+"F0.wireOp",EDGE,"E1674"),sQuery(id+"F0.wireOp",EDGE,"E1675"),sQuery(id+"F0.wireOp",EDGE,"E1676"),sQuery(id+"F0.wireOp",EDGE,"E1677"),sQuery(id+"F0.wireOp",EDGE,"E1678"),sQuery(id+"F0.wireOp",EDGE,"E1679"),sQuery(id+"F0.wireOp",EDGE,"E1680"),sQuery(id+"F0.wireOp",EDGE,"E1681"),sQuery(id+"F0.wireOp",EDGE,"E1682"),sQuery(id+"F0.wireOp",EDGE,"E1683"),sQuery(id+"F0.wireOp",EDGE,"E1684"),sQuery(id+"F0.wireOp",EDGE,"E1685"),sQuery(id+"F0.wireOp",EDGE,"E1686")])]});
            var Q36;
            Q36=makeQuery(id+"F1.opExtrude","SWEPT_BODY",BODY,{"disambiguationData":[OSD([sQuery(id+"F0.wireOp",EDGE,"E1875"),sQuery(id+"F0.wireOp",EDGE,"E1876"),sQuery(id+"F0.wireOp",EDGE,"E1877"),sQuery(id+"F0.wireOp",EDGE,"E1878"),sQuery(id+"F0.wireOp",EDGE,"E1879"),sQuery(id+"F0.wireOp",EDGE,"E1880"),sQuery(id+"F0.wireOp",EDGE,"E1881"),sQuery(id+"F0.wireOp",EDGE,"E1882"),sQuery(id+"F0.wireOp",EDGE,"E1883"),sQuery(id+"F0.wireOp",EDGE,"E1884"),sQuery(id+"F0.wireOp",EDGE,"E1885"),sQuery(id+"F0.wireOp",EDGE,"E1886"),sQuery(id+"F0.wireOp",EDGE,"E1887"),sQuery(id+"F0.wireOp",EDGE,"E1888"),sQuery(id+"F0.wireOp",EDGE,"E1889"),sQuery(id+"F0.wireOp",EDGE,"E1890"),sQuery(id+"F0.wireOp",EDGE,"E1891"),sQuery(id+"F0.wireOp",EDGE,"E1892"),sQuery(id+"F0.wireOp",EDGE,"E1893"),sQuery(id+"F0.wireOp",EDGE,"E1894"),sQuery(id+"F0.wireOp",EDGE,"E1895"),sQuery(id+"F0.wireOp",EDGE,"E1896"),sQuery(id+"F0.wireOp",EDGE,"E1897"),sQuery(id+"F0.wireOp",EDGE,"E1898"),sQuery(id+"F0.wireOp",EDGE,"E1899"),sQuery(id+"F0.wireOp",EDGE,"E1900"),sQuery(id+"F0.wireOp",EDGE,"E1901"),sQuery(id+"F0.wireOp",EDGE,"E1902"),sQuery(id+"F0.wireOp",EDGE,"E1903"),sQuery(id+"F0.wireOp",EDGE,"E1904"),sQuery(id+"F0.wireOp",EDGE,"E1905"),sQuery(id+"F0.wireOp",EDGE,"E1906"),sQuery(id+"F0.wireOp",EDGE,"E1907"),sQuery(id+"F0.wireOp",EDGE,"E1908"),sQuery(id+"F0.wireOp",EDGE,"E1909"),sQuery(id+"F0.wireOp",EDGE,"E1910"),sQuery(id+"F0.wireOp",EDGE,"E1911"),sQuery(id+"F0.wireOp",EDGE,"E1912"),sQuery(id+"F0.wireOp",EDGE,"E1913"),sQuery(id+"F0.wireOp",EDGE,"E1914"),sQuery(id+"F0.wireOp",EDGE,"E1915"),sQuery(id+"F0.wireOp",EDGE,"E1916"),sQuery(id+"F0.wireOp",EDGE,"E1917"),sQuery(id+"F0.wireOp",EDGE,"E1918"),sQuery(id+"F0.wireOp",EDGE,"E1919"),sQuery(id+"F0.wireOp",EDGE,"E1920"),sQuery(id+"F0.wireOp",EDGE,"E1921"),sQuery(id+"F0.wireOp",EDGE,"E1922"),sQuery(id+"F0.wireOp",EDGE,"E1923"),sQuery(id+"F0.wireOp",EDGE,"E1924"),sQuery(id+"F0.wireOp",EDGE,"E1925"),sQuery(id+"F0.wireOp",EDGE,"E1926"),sQuery(id+"F0.wireOp",EDGE,"E1927"),sQuery(id+"F0.wireOp",EDGE,"E1928"),sQuery(id+"F0.wireOp",EDGE,"E1929"),sQuery(id+"F0.wireOp",EDGE,"E1930"),sQuery(id+"F0.wireOp",EDGE,"E1931"),sQuery(id+"F0.wireOp",EDGE,"E1932"),sQuery(id+"F0.wireOp",EDGE,"E1933"),sQuery(id+"F0.wireOp",EDGE,"E1934"),sQuery(id+"F0.wireOp",EDGE,"E1935"),sQuery(id+"F0.wireOp",EDGE,"E1936"),sQuery(id+"F0.wireOp",EDGE,"E1937"),sQuery(id+"F0.wireOp",EDGE,"E1938"),sQuery(id+"F0.wireOp",EDGE,"E1939"),sQuery(id+"F0.wireOp",EDGE,"E1940"),sQuery(id+"F0.wireOp",EDGE,"E1941"),sQuery(id+"F0.wireOp",EDGE,"E1942"),sQuery(id+"F0.wireOp",EDGE,"E1943"),sQuery(id+"F0.wireOp",EDGE,"E1944"),sQuery(id+"F0.wireOp",EDGE,"E1945"),sQuery(id+"F0.wireOp",EDGE,"E1946"),sQuery(id+"F0.wireOp",EDGE,"E1947"),sQuery(id+"F0.wireOp",EDGE,"E1948"),sQuery(id+"F0.wireOp",EDGE,"E1949"),sQuery(id+"F0.wireOp",EDGE,"E1950"),sQuery(id+"F0.wireOp",EDGE,"E1951"),sQuery(id+"F0.wireOp",EDGE,"E1952"),sQuery(id+"F0.wireOp",EDGE,"E1953"),sQuery(id+"F0.wireOp",EDGE,"E1954"),sQuery(id+"F0.wireOp",EDGE,"E1955"),sQuery(id+"F0.wireOp",EDGE,"E1956"),sQuery(id+"F0.wireOp",EDGE,"E1957"),sQuery(id+"F0.wireOp",EDGE,"E1958"),sQuery(id+"F0.wireOp",EDGE,"E1959"),sQuery(id+"F0.wireOp",EDGE,"E1960")])]});
            var Q37;
            Q37=makeQuery(id+"F1.opExtrude","SWEPT_BODY",BODY,{"disambiguationData":[OSD([sQuery(id+"F0.wireOp",EDGE,"E1961"),sQuery(id+"F0.wireOp",EDGE,"E1962"),sQuery(id+"F0.wireOp",EDGE,"E1963"),sQuery(id+"F0.wireOp",EDGE,"E1964"),sQuery(id+"F0.wireOp",EDGE,"E1965"),sQuery(id+"F0.wireOp",EDGE,"E1966"),sQuery(id+"F0.wireOp",EDGE,"E1967"),sQuery(id+"F0.wireOp",EDGE,"E1968"),sQuery(id+"F0.wireOp",EDGE,"E1969"),sQuery(id+"F0.wireOp",EDGE,"E1970"),sQuery(id+"F0.wireOp",EDGE,"E1971"),sQuery(id+"F0.wireOp",EDGE,"E1972"),sQuery(id+"F0.wireOp",EDGE,"E1973"),sQuery(id+"F0.wireOp",EDGE,"E1974"),sQuery(id+"F0.wireOp",EDGE,"E1975"),sQuery(id+"F0.wireOp",EDGE,"E1976"),sQuery(id+"F0.wireOp",EDGE,"E1977"),sQuery(id+"F0.wireOp",EDGE,"E1978"),sQuery(id+"F0.wireOp",EDGE,"E1979"),sQuery(id+"F0.wireOp",EDGE,"E1980"),sQuery(id+"F0.wireOp",EDGE,"E1981"),sQuery(id+"F0.wireOp",EDGE,"E1982"),sQuery(id+"F0.wireOp",EDGE,"E1983"),sQuery(id+"F0.wireOp",EDGE,"E1984"),sQuery(id+"F0.wireOp",EDGE,"E1985"),sQuery(id+"F0.wireOp",EDGE,"E1986"),sQuery(id+"F0.wireOp",EDGE,"E1987"),sQuery(id+"F0.wireOp",EDGE,"E1988"),sQuery(id+"F0.wireOp",EDGE,"E1989"),sQuery(id+"F0.wireOp",EDGE,"E1990"),sQuery(id+"F0.wireOp",EDGE,"E1991"),sQuery(id+"F0.wireOp",EDGE,"E1992"),sQuery(id+"F0.wireOp",EDGE,"E1993"),sQuery(id+"F0.wireOp",EDGE,"E1994"),sQuery(id+"F0.wireOp",EDGE,"E1995"),sQuery(id+"F0.wireOp",EDGE,"E1996"),sQuery(id+"F0.wireOp",EDGE,"E1997"),sQuery(id+"F0.wireOp",EDGE,"E1998"),sQuery(id+"F0.wireOp",EDGE,"E1999"),sQuery(id+"F0.wireOp",EDGE,"E2000"),sQuery(id+"F0.wireOp",EDGE,"E2001"),sQuery(id+"F0.wireOp",EDGE,"E2002"),sQuery(id+"F0.wireOp",EDGE,"E2003"),sQuery(id+"F0.wireOp",EDGE,"E2004"),sQuery(id+"F0.wireOp",EDGE,"E2005"),sQuery(id+"F0.wireOp",EDGE,"E2006"),sQuery(id+"F0.wireOp",EDGE,"E2007"),sQuery(id+"F0.wireOp",EDGE,"E2008"),sQuery(id+"F0.wireOp",EDGE,"E2009"),sQuery(id+"F0.wireOp",EDGE,"E2010"),sQuery(id+"F0.wireOp",EDGE,"E2011")])]});
            var Q38;
            Q38=makeQuery(id+"F1.opExtrude","SWEPT_BODY",BODY,{"disambiguationData":[OSD([sQuery(id+"F0.wireOp",EDGE,"E2025"),sQuery(id+"F0.wireOp",EDGE,"E2026"),sQuery(id+"F0.wireOp",EDGE,"E2027"),sQuery(id+"F0.wireOp",EDGE,"E2028"),sQuery(id+"F0.wireOp",EDGE,"E2029"),sQuery(id+"F0.wireOp",EDGE,"E2030"),sQuery(id+"F0.wireOp",EDGE,"E2031"),sQuery(id+"F0.wireOp",EDGE,"E2032"),sQuery(id+"F0.wireOp",EDGE,"E2033"),sQuery(id+"F0.wireOp",EDGE,"E2034"),sQuery(id+"F0.wireOp",EDGE,"E2035")])]});
            var Q39;
            Q39=makeQuery(id+"F1.opExtrude","SWEPT_BODY",BODY,{"disambiguationData":[OSD([sQuery(id+"F0.wireOp",EDGE,"E2464"),sQuery(id+"F0.wireOp",EDGE,"E2465"),sQuery(id+"F0.wireOp",EDGE,"E2466"),sQuery(id+"F0.wireOp",EDGE,"E2467"),sQuery(id+"F0.wireOp",EDGE,"E2468"),sQuery(id+"F0.wireOp",EDGE,"E2469"),sQuery(id+"F0.wireOp",EDGE,"E2470"),sQuery(id+"F0.wireOp",EDGE,"E2471"),sQuery(id+"F0.wireOp",EDGE,"E2472"),sQuery(id+"F0.wireOp",EDGE,"E2473"),sQuery(id+"F0.wireOp",EDGE,"E2474"),sQuery(id+"F0.wireOp",EDGE,"E2475"),sQuery(id+"F0.wireOp",EDGE,"E2476"),sQuery(id+"F0.wireOp",EDGE,"E2477"),sQuery(id+"F0.wireOp",EDGE,"E2478"),sQuery(id+"F0.wireOp",EDGE,"E2479")])]});
            var Q40;
            Q40=makeQuery(id+"F1.opExtrude","SWEPT_BODY",BODY,{"disambiguationData":[OSD([sQuery(id+"F0.wireOp",EDGE,"E3026"),sQuery(id+"F0.wireOp",EDGE,"E3027"),sQuery(id+"F0.wireOp",EDGE,"E3028"),sQuery(id+"F0.wireOp",EDGE,"E3029"),sQuery(id+"F0.wireOp",EDGE,"E3030"),sQuery(id+"F0.wireOp",EDGE,"E3031"),sQuery(id+"F0.wireOp",EDGE,"E3032"),sQuery(id+"F0.wireOp",EDGE,"E3033"),sQuery(id+"F0.wireOp",EDGE,"E3034"),sQuery(id+"F0.wireOp",EDGE,"E3035"),sQuery(id+"F0.wireOp",EDGE,"E3036"),sQuery(id+"F0.wireOp",EDGE,"E3037")])]});
            var Q41;
            Q41=makeQuery(id+"F1.opExtrude","SWEPT_BODY",BODY,{"disambiguationData":[OSD([sQuery(id+"F0.wireOp",EDGE,"E3073"),sQuery(id+"F0.wireOp",EDGE,"E3074"),sQuery(id+"F0.wireOp",EDGE,"E3075"),sQuery(id+"F0.wireOp",EDGE,"E3076"),sQuery(id+"F0.wireOp",EDGE,"E3077"),sQuery(id+"F0.wireOp",EDGE,"E3078"),sQuery(id+"F0.wireOp",EDGE,"E3079"),sQuery(id+"F0.wireOp",EDGE,"E3080"),sQuery(id+"F0.wireOp",EDGE,"E3081"),sQuery(id+"F0.wireOp",EDGE,"E3082"),sQuery(id+"F0.wireOp",EDGE,"E3083"),sQuery(id+"F0.wireOp",EDGE,"E3084"),sQuery(id+"F0.wireOp",EDGE,"E3085"),sQuery(id+"F0.wireOp",EDGE,"E3086"),sQuery(id+"F0.wireOp",EDGE,"E3087"),sQuery(id+"F0.wireOp",EDGE,"E3088"),sQuery(id+"F0.wireOp",EDGE,"E3089"),sQuery(id+"F0.wireOp",EDGE,"E3090"),sQuery(id+"F0.wireOp",EDGE,"E3091"),sQuery(id+"F0.wireOp",EDGE,"E3092"),sQuery(id+"F0.wireOp",EDGE,"E3093"),sQuery(id+"F0.wireOp",EDGE,"E3094"),sQuery(id+"F0.wireOp",EDGE,"E3095"),sQuery(id+"F0.wireOp",EDGE,"E3096"),sQuery(id+"F0.wireOp",EDGE,"E3097"),sQuery(id+"F0.wireOp",EDGE,"E3098"),sQuery(id+"F0.wireOp",EDGE,"E3099"),sQuery(id+"F0.wireOp",EDGE,"E3100"),sQuery(id+"F0.wireOp",EDGE,"E3101"),sQuery(id+"F0.wireOp",EDGE,"E3102"),sQuery(id+"F0.wireOp",EDGE,"E3103"),sQuery(id+"F0.wireOp",EDGE,"E3104"),sQuery(id+"F0.wireOp",EDGE,"E3105"),sQuery(id+"F0.wireOp",EDGE,"E3106"),sQuery(id+"F0.wireOp",EDGE,"E3107"),sQuery(id+"F0.wireOp",EDGE,"E3108"),sQuery(id+"F0.wireOp",EDGE,"E3109"),sQuery(id+"F0.wireOp",EDGE,"E3110"),sQuery(id+"F0.wireOp",EDGE,"E3111"),sQuery(id+"F0.wireOp",EDGE,"E3112"),sQuery(id+"F0.wireOp",EDGE,"E3113"),sQuery(id+"F0.wireOp",EDGE,"E3114"),sQuery(id+"F0.wireOp",EDGE,"E3115"),sQuery(id+"F0.wireOp",EDGE,"E3116"),sQuery(id+"F0.wireOp",EDGE,"E3117"),sQuery(id+"F0.wireOp",EDGE,"E3118"),sQuery(id+"F0.wireOp",EDGE,"E3119"),sQuery(id+"F0.wireOp",EDGE,"E3120"),sQuery(id+"F0.wireOp",EDGE,"E3121"),sQuery(id+"F0.wireOp",EDGE,"E3122"),sQuery(id+"F0.wireOp",EDGE,"E3123"),sQuery(id+"F0.wireOp",EDGE,"E3124"),sQuery(id+"F0.wireOp",EDGE,"E3125"),sQuery(id+"F0.wireOp",EDGE,"E3126"),sQuery(id+"F0.wireOp",EDGE,"E3127"),sQuery(id+"F0.wireOp",EDGE,"E3128"),sQuery(id+"F0.wireOp",EDGE,"E3129"),sQuery(id+"F0.wireOp",EDGE,"E3130"),sQuery(id+"F0.wireOp",EDGE,"E3131"),sQuery(id+"F0.wireOp",EDGE,"E3132"),sQuery(id+"F0.wireOp",EDGE,"E3133"),sQuery(id+"F0.wireOp",EDGE,"E3134"),sQuery(id+"F0.wireOp",EDGE,"E3135"),sQuery(id+"F0.wireOp",EDGE,"E3136"),sQuery(id+"F0.wireOp",EDGE,"E3137"),sQuery(id+"F0.wireOp",EDGE,"E3138"),sQuery(id+"F0.wireOp",EDGE,"E3139"),sQuery(id+"F0.wireOp",EDGE,"E3140"),sQuery(id+"F0.wireOp",EDGE,"E3141"),sQuery(id+"F0.wireOp",EDGE,"E3142"),sQuery(id+"F0.wireOp",EDGE,"E3143"),sQuery(id+"F0.wireOp",EDGE,"E3144"),sQuery(id+"F0.wireOp",EDGE,"E3145"),sQuery(id+"F0.wireOp",EDGE,"E3146"),sQuery(id+"F0.wireOp",EDGE,"E3147"),sQuery(id+"F0.wireOp",EDGE,"E3148"),sQuery(id+"F0.wireOp",EDGE,"E3149"),sQuery(id+"F0.wireOp",EDGE,"E3150"),sQuery(id+"F0.wireOp",EDGE,"E3151"),sQuery(id+"F0.wireOp",EDGE,"E3152"),sQuery(id+"F0.wireOp",EDGE,"E3153"),sQuery(id+"F0.wireOp",EDGE,"E3154"),sQuery(id+"F0.wireOp",EDGE,"E3155"),sQuery(id+"F0.wireOp",EDGE,"E3156"),sQuery(id+"F0.wireOp",EDGE,"E3157"),sQuery(id+"F0.wireOp",EDGE,"E3158"),sQuery(id+"F0.wireOp",EDGE,"E3159"),sQuery(id+"F0.wireOp",EDGE,"E3160"),sQuery(id+"F0.wireOp",EDGE,"E3161"),sQuery(id+"F0.wireOp",EDGE,"E3162"),sQuery(id+"F0.wireOp",EDGE,"E3163")])]});
            var Q42;
            Q42=makeQuery(id+"F1.opExtrude","SWEPT_BODY",BODY,{"disambiguationData":[OSD([sQuery(id+"F0.wireOp",EDGE,"E1519"),sQuery(id+"F0.wireOp",EDGE,"E1520"),sQuery(id+"F0.wireOp",EDGE,"E1521"),sQuery(id+"F0.wireOp",EDGE,"E1522"),sQuery(id+"F0.wireOp",EDGE,"E1523"),sQuery(id+"F0.wireOp",EDGE,"E1524"),sQuery(id+"F0.wireOp",EDGE,"E1525"),sQuery(id+"F0.wireOp",EDGE,"E1526"),sQuery(id+"F0.wireOp",EDGE,"E1527"),sQuery(id+"F0.wireOp",EDGE,"E1528"),sQuery(id+"F0.wireOp",EDGE,"E1529"),sQuery(id+"F0.wireOp",EDGE,"E1530"),sQuery(id+"F0.wireOp",EDGE,"E1531"),sQuery(id+"F0.wireOp",EDGE,"E1532"),sQuery(id+"F0.wireOp",EDGE,"E1533"),sQuery(id+"F0.wireOp",EDGE,"E1534"),sQuery(id+"F0.wireOp",EDGE,"E1535"),sQuery(id+"F0.wireOp",EDGE,"E1536"),sQuery(id+"F0.wireOp",EDGE,"E1537"),sQuery(id+"F0.wireOp",EDGE,"E1538"),sQuery(id+"F0.wireOp",EDGE,"E1539"),sQuery(id+"F0.wireOp",EDGE,"E1540"),sQuery(id+"F0.wireOp",EDGE,"E1541"),sQuery(id+"F0.wireOp",EDGE,"E1542"),sQuery(id+"F0.wireOp",EDGE,"E1543"),sQuery(id+"F0.wireOp",EDGE,"E1544"),sQuery(id+"F0.wireOp",EDGE,"E1545"),sQuery(id+"F0.wireOp",EDGE,"E1546"),sQuery(id+"F0.wireOp",EDGE,"E1547"),sQuery(id+"F0.wireOp",EDGE,"E1548"),sQuery(id+"F0.wireOp",EDGE,"E1549"),sQuery(id+"F0.wireOp",EDGE,"E1550"),sQuery(id+"F0.wireOp",EDGE,"E1551"),sQuery(id+"F0.wireOp",EDGE,"E1552"),sQuery(id+"F0.wireOp",EDGE,"E1553"),sQuery(id+"F0.wireOp",EDGE,"E1554"),sQuery(id+"F0.wireOp",EDGE,"E1555"),sQuery(id+"F0.wireOp",EDGE,"E1556"),sQuery(id+"F0.wireOp",EDGE,"E1557"),sQuery(id+"F0.wireOp",EDGE,"E1558"),sQuery(id+"F0.wireOp",EDGE,"E1559"),sQuery(id+"F0.wireOp",EDGE,"E1560"),sQuery(id+"F0.wireOp",EDGE,"E1561"),sQuery(id+"F0.wireOp",EDGE,"E1562"),sQuery(id+"F0.wireOp",EDGE,"E1563"),sQuery(id+"F0.wireOp",EDGE,"E1564"),sQuery(id+"F0.wireOp",EDGE,"E1565"),sQuery(id+"F0.wireOp",EDGE,"E1566"),sQuery(id+"F0.wireOp",EDGE,"E1567"),sQuery(id+"F0.wireOp",EDGE,"E1568"),sQuery(id+"F0.wireOp",EDGE,"E1569"),sQuery(id+"F0.wireOp",EDGE,"E1570"),sQuery(id+"F0.wireOp",EDGE,"E1571"),sQuery(id+"F0.wireOp",EDGE,"E1572"),sQuery(id+"F0.wireOp",EDGE,"E1573"),sQuery(id+"F0.wireOp",EDGE,"E1574"),sQuery(id+"F0.wireOp",EDGE,"E1575"),sQuery(id+"F0.wireOp",EDGE,"E1576"),sQuery(id+"F0.wireOp",EDGE,"E1577"),sQuery(id+"F0.wireOp",EDGE,"E1578"),sQuery(id+"F0.wireOp",EDGE,"E1579"),sQuery(id+"F0.wireOp",EDGE,"E1580"),sQuery(id+"F0.wireOp",EDGE,"E1581"),sQuery(id+"F0.wireOp",EDGE,"E1582"),sQuery(id+"F0.wireOp",EDGE,"E1583"),sQuery(id+"F0.wireOp",EDGE,"E1584"),sQuery(id+"F0.wireOp",EDGE,"E1585"),sQuery(id+"F0.wireOp",EDGE,"E1586"),sQuery(id+"F0.wireOp",EDGE,"E1587"),sQuery(id+"F0.wireOp",EDGE,"E1588"),sQuery(id+"F0.wireOp",EDGE,"E1589"),sQuery(id+"F0.wireOp",EDGE,"E1590"),sQuery(id+"F0.wireOp",EDGE,"E1591"),sQuery(id+"F0.wireOp",EDGE,"E1592"),sQuery(id+"F0.wireOp",EDGE,"E1593"),sQuery(id+"F0.wireOp",EDGE,"E1594"),sQuery(id+"F0.wireOp",EDGE,"E1595"),sQuery(id+"F0.wireOp",EDGE,"E1596"),sQuery(id+"F0.wireOp",EDGE,"E1597"),sQuery(id+"F0.wireOp",EDGE,"E1598"),sQuery(id+"F0.wireOp",EDGE,"E1599"),sQuery(id+"F0.wireOp",EDGE,"E1600"),sQuery(id+"F0.wireOp",EDGE,"E1601"),sQuery(id+"F0.wireOp",EDGE,"E1602")])]});
            var Q43;
            Q43=makeQuery(id+"F1.opExtrude","SWEPT_BODY",BODY,{"disambiguationData":[OSD([sQuery(id+"F0.wireOp",EDGE,"E1775"),sQuery(id+"F0.wireOp",EDGE,"E1776"),sQuery(id+"F0.wireOp",EDGE,"E1777"),sQuery(id+"F0.wireOp",EDGE,"E1778"),sQuery(id+"F0.wireOp",EDGE,"E1779"),sQuery(id+"F0.wireOp",EDGE,"E1780"),sQuery(id+"F0.wireOp",EDGE,"E1781"),sQuery(id+"F0.wireOp",EDGE,"E1782"),sQuery(id+"F0.wireOp",EDGE,"E1783"),sQuery(id+"F0.wireOp",EDGE,"E1784"),sQuery(id+"F0.wireOp",EDGE,"E1785"),sQuery(id+"F0.wireOp",EDGE,"E1786"),sQuery(id+"F0.wireOp",EDGE,"E1787"),sQuery(id+"F0.wireOp",EDGE,"E1788"),sQuery(id+"F0.wireOp",EDGE,"E1789"),sQuery(id+"F0.wireOp",EDGE,"E1790"),sQuery(id+"F0.wireOp",EDGE,"E1791"),sQuery(id+"F0.wireOp",EDGE,"E1792"),sQuery(id+"F0.wireOp",EDGE,"E1793"),sQuery(id+"F0.wireOp",EDGE,"E1794"),sQuery(id+"F0.wireOp",EDGE,"E1795"),sQuery(id+"F0.wireOp",EDGE,"E1796"),sQuery(id+"F0.wireOp",EDGE,"E1797"),sQuery(id+"F0.wireOp",EDGE,"E1798"),sQuery(id+"F0.wireOp",EDGE,"E1799"),sQuery(id+"F0.wireOp",EDGE,"E1800"),sQuery(id+"F0.wireOp",EDGE,"E1801"),sQuery(id+"F0.wireOp",EDGE,"E1802"),sQuery(id+"F0.wireOp",EDGE,"E1803"),sQuery(id+"F0.wireOp",EDGE,"E1804"),sQuery(id+"F0.wireOp",EDGE,"E1805"),sQuery(id+"F0.wireOp",EDGE,"E1806"),sQuery(id+"F0.wireOp",EDGE,"E1807"),sQuery(id+"F0.wireOp",EDGE,"E1808"),sQuery(id+"F0.wireOp",EDGE,"E1809"),sQuery(id+"F0.wireOp",EDGE,"E1810"),sQuery(id+"F0.wireOp",EDGE,"E1811"),sQuery(id+"F0.wireOp",EDGE,"E1812"),sQuery(id+"F0.wireOp",EDGE,"E1813"),sQuery(id+"F0.wireOp",EDGE,"E1814"),sQuery(id+"F0.wireOp",EDGE,"E1815"),sQuery(id+"F0.wireOp",EDGE,"E1816"),sQuery(id+"F0.wireOp",EDGE,"E1817"),sQuery(id+"F0.wireOp",EDGE,"E1818"),sQuery(id+"F0.wireOp",EDGE,"E1819"),sQuery(id+"F0.wireOp",EDGE,"E1820"),sQuery(id+"F0.wireOp",EDGE,"E1821"),sQuery(id+"F0.wireOp",EDGE,"E1822"),sQuery(id+"F0.wireOp",EDGE,"E1823"),sQuery(id+"F0.wireOp",EDGE,"E1824"),sQuery(id+"F0.wireOp",EDGE,"E1825"),sQuery(id+"F0.wireOp",EDGE,"E1826"),sQuery(id+"F0.wireOp",EDGE,"E1827"),sQuery(id+"F0.wireOp",EDGE,"E1828"),sQuery(id+"F0.wireOp",EDGE,"E1829"),sQuery(id+"F0.wireOp",EDGE,"E1830"),sQuery(id+"F0.wireOp",EDGE,"E1831"),sQuery(id+"F0.wireOp",EDGE,"E1832"),sQuery(id+"F0.wireOp",EDGE,"E1833"),sQuery(id+"F0.wireOp",EDGE,"E1834"),sQuery(id+"F0.wireOp",EDGE,"E1835"),sQuery(id+"F0.wireOp",EDGE,"E1836"),sQuery(id+"F0.wireOp",EDGE,"E1837"),sQuery(id+"F0.wireOp",EDGE,"E1838"),sQuery(id+"F0.wireOp",EDGE,"E1839"),sQuery(id+"F0.wireOp",EDGE,"E1840"),sQuery(id+"F0.wireOp",EDGE,"E1841"),sQuery(id+"F0.wireOp",EDGE,"E1842"),sQuery(id+"F0.wireOp",EDGE,"E1843"),sQuery(id+"F0.wireOp",EDGE,"E1844"),sQuery(id+"F0.wireOp",EDGE,"E1845"),sQuery(id+"F0.wireOp",EDGE,"E1846"),sQuery(id+"F0.wireOp",EDGE,"E1847"),sQuery(id+"F0.wireOp",EDGE,"E1848"),sQuery(id+"F0.wireOp",EDGE,"E1849"),sQuery(id+"F0.wireOp",EDGE,"E1850"),sQuery(id+"F0.wireOp",EDGE,"E1851"),sQuery(id+"F0.wireOp",EDGE,"E1852"),sQuery(id+"F0.wireOp",EDGE,"E1853"),sQuery(id+"F0.wireOp",EDGE,"E1854"),sQuery(id+"F0.wireOp",EDGE,"E1855"),sQuery(id+"F0.wireOp",EDGE,"E1856"),sQuery(id+"F0.wireOp",EDGE,"E1857"),sQuery(id+"F0.wireOp",EDGE,"E1858"),sQuery(id+"F0.wireOp",EDGE,"E1859"),sQuery(id+"F0.wireOp",EDGE,"E1860"),sQuery(id+"F0.wireOp",EDGE,"E1861"),sQuery(id+"F0.wireOp",EDGE,"E1862")])]});
            var Q44;
            Q44=makeQuery(id+"F1.opExtrude","SWEPT_BODY",BODY,{"disambiguationData":[OSD([sQuery(id+"F0.wireOp",EDGE,"E2444"),sQuery(id+"F0.wireOp",EDGE,"E2445"),sQuery(id+"F0.wireOp",EDGE,"E2446"),sQuery(id+"F0.wireOp",EDGE,"E2447"),sQuery(id+"F0.wireOp",EDGE,"E2448"),sQuery(id+"F0.wireOp",EDGE,"E2449"),sQuery(id+"F0.wireOp",EDGE,"E2450"),sQuery(id+"F0.wireOp",EDGE,"E2451"),sQuery(id+"F0.wireOp",EDGE,"E2452"),sQuery(id+"F0.wireOp",EDGE,"E2453"),sQuery(id+"F0.wireOp",EDGE,"E2454"),sQuery(id+"F0.wireOp",EDGE,"E2455")])]});
            var Q45;
            Q45=makeQuery(id+"F1.opExtrude","SWEPT_BODY",BODY,{"disambiguationData":[OSD([sQuery(id+"F0.wireOp",EDGE,"E855"),sQuery(id+"F0.wireOp",EDGE,"E856"),sQuery(id+"F0.wireOp",EDGE,"E857"),sQuery(id+"F0.wireOp",EDGE,"E858"),sQuery(id+"F0.wireOp",EDGE,"E859"),sQuery(id+"F0.wireOp",EDGE,"E860"),sQuery(id+"F0.wireOp",EDGE,"E861"),sQuery(id+"F0.wireOp",EDGE,"E862")])]});
            var Q46;
            Q46=makeQuery(id+"F1.opExtrude","SWEPT_BODY",BODY,{"disambiguationData":[OSD([sQuery(id+"F0.wireOp",EDGE,"E863"),sQuery(id+"F0.wireOp",EDGE,"E864"),sQuery(id+"F0.wireOp",EDGE,"E865"),sQuery(id+"F0.wireOp",EDGE,"E866"),sQuery(id+"F0.wireOp",EDGE,"E867"),sQuery(id+"F0.wireOp",EDGE,"E868"),sQuery(id+"F0.wireOp",EDGE,"E869"),sQuery(id+"F0.wireOp",EDGE,"E870")])]});
            var Q47;
            Q47=makeQuery(id+"F1.opExtrude","SWEPT_BODY",BODY,{"disambiguationData":[OSD([sQuery(id+"F0.wireOp",EDGE,"E1076"),sQuery(id+"F0.wireOp",EDGE,"E1077"),sQuery(id+"F0.wireOp",EDGE,"E1078"),sQuery(id+"F0.wireOp",EDGE,"E1079"),sQuery(id+"F0.wireOp",EDGE,"E1080"),sQuery(id+"F0.wireOp",EDGE,"E1081"),sQuery(id+"F0.wireOp",EDGE,"E1082"),sQuery(id+"F0.wireOp",EDGE,"E1083"),sQuery(id+"F0.wireOp",EDGE,"E1084"),sQuery(id+"F0.wireOp",EDGE,"E1085"),sQuery(id+"F0.wireOp",EDGE,"E1086")])]});
            var Q48;
            Q48=makeQuery(id+"F1.opExtrude","SWEPT_BODY",BODY,{"disambiguationData":[OSD([sQuery(id+"F0.wireOp",EDGE,"E2480"),sQuery(id+"F0.wireOp",EDGE,"E2481"),sQuery(id+"F0.wireOp",EDGE,"E2482"),sQuery(id+"F0.wireOp",EDGE,"E2483"),sQuery(id+"F0.wireOp",EDGE,"E2484"),sQuery(id+"F0.wireOp",EDGE,"E2485"),sQuery(id+"F0.wireOp",EDGE,"E2486"),sQuery(id+"F0.wireOp",EDGE,"E2487"),sQuery(id+"F0.wireOp",EDGE,"E2488"),sQuery(id+"F0.wireOp",EDGE,"E2489"),sQuery(id+"F0.wireOp",EDGE,"E2490"),sQuery(id+"F0.wireOp",EDGE,"E2491"),sQuery(id+"F0.wireOp",EDGE,"E2492"),sQuery(id+"F0.wireOp",EDGE,"E2493"),sQuery(id+"F0.wireOp",EDGE,"E2494"),sQuery(id+"F0.wireOp",EDGE,"E2495"),sQuery(id+"F0.wireOp",EDGE,"E2496"),sQuery(id+"F0.wireOp",EDGE,"E2497"),sQuery(id+"F0.wireOp",EDGE,"E2498"),sQuery(id+"F0.wireOp",EDGE,"E2499"),sQuery(id+"F0.wireOp",EDGE,"E2500"),sQuery(id+"F0.wireOp",EDGE,"E2501"),sQuery(id+"F0.wireOp",EDGE,"E2502"),sQuery(id+"F0.wireOp",EDGE,"E2503"),sQuery(id+"F0.wireOp",EDGE,"E2504"),sQuery(id+"F0.wireOp",EDGE,"E2505"),sQuery(id+"F0.wireOp",EDGE,"E2506"),sQuery(id+"F0.wireOp",EDGE,"E2507"),sQuery(id+"F0.wireOp",EDGE,"E2508"),sQuery(id+"F0.wireOp",EDGE,"E2509"),sQuery(id+"F0.wireOp",EDGE,"E2510"),sQuery(id+"F0.wireOp",EDGE,"E2511"),sQuery(id+"F0.wireOp",EDGE,"E2512"),sQuery(id+"F0.wireOp",EDGE,"E2513"),sQuery(id+"F0.wireOp",EDGE,"E2514"),sQuery(id+"F0.wireOp",EDGE,"E2515"),sQuery(id+"F0.wireOp",EDGE,"E2516"),sQuery(id+"F0.wireOp",EDGE,"E2517"),sQuery(id+"F0.wireOp",EDGE,"E2518"),sQuery(id+"F0.wireOp",EDGE,"E2519"),sQuery(id+"F0.wireOp",EDGE,"E2520"),sQuery(id+"F0.wireOp",EDGE,"E2521"),sQuery(id+"F0.wireOp",EDGE,"E2522"),sQuery(id+"F0.wireOp",EDGE,"E2523"),sQuery(id+"F0.wireOp",EDGE,"E2524"),sQuery(id+"F0.wireOp",EDGE,"E2525"),sQuery(id+"F0.wireOp",EDGE,"E2526"),sQuery(id+"F0.wireOp",EDGE,"E2527"),sQuery(id+"F0.wireOp",EDGE,"E2528"),sQuery(id+"F0.wireOp",EDGE,"E2529"),sQuery(id+"F0.wireOp",EDGE,"E2530"),sQuery(id+"F0.wireOp",EDGE,"E2531"),sQuery(id+"F0.wireOp",EDGE,"E2532"),sQuery(id+"F0.wireOp",EDGE,"E2533"),sQuery(id+"F0.wireOp",EDGE,"E2534"),sQuery(id+"F0.wireOp",EDGE,"E2535"),sQuery(id+"F0.wireOp",EDGE,"E2536"),sQuery(id+"F0.wireOp",EDGE,"E2537"),sQuery(id+"F0.wireOp",EDGE,"E2538"),sQuery(id+"F0.wireOp",EDGE,"E2539"),sQuery(id+"F0.wireOp",EDGE,"E2540"),sQuery(id+"F0.wireOp",EDGE,"E2541"),sQuery(id+"F0.wireOp",EDGE,"E2542"),sQuery(id+"F0.wireOp",EDGE,"E2543"),sQuery(id+"F0.wireOp",EDGE,"E2544"),sQuery(id+"F0.wireOp",EDGE,"E2545"),sQuery(id+"F0.wireOp",EDGE,"E2546"),sQuery(id+"F0.wireOp",EDGE,"E2547"),sQuery(id+"F0.wireOp",EDGE,"E2548"),sQuery(id+"F0.wireOp",EDGE,"E2549"),sQuery(id+"F0.wireOp",EDGE,"E2550"),sQuery(id+"F0.wireOp",EDGE,"E2551"),sQuery(id+"F0.wireOp",EDGE,"E2552"),sQuery(id+"F0.wireOp",EDGE,"E2553"),sQuery(id+"F0.wireOp",EDGE,"E2554"),sQuery(id+"F0.wireOp",EDGE,"E2555"),sQuery(id+"F0.wireOp",EDGE,"E2556")])]});
            var Q49;
            Q49=makeQuery(id+"F1.opExtrude","SWEPT_BODY",BODY,{"disambiguationData":[OSD([sQuery(id+"F0.wireOp",EDGE,"E2603"),sQuery(id+"F0.wireOp",EDGE,"E2604"),sQuery(id+"F0.wireOp",EDGE,"E2605"),sQuery(id+"F0.wireOp",EDGE,"E2606")])]});
            var Q50;
            Q50=makeQuery(id+"F1.opExtrude","SWEPT_BODY",BODY,{"disambiguationData":[OSD([sQuery(id+"F0.wireOp",EDGE,"E98"),sQuery(id+"F0.wireOp",EDGE,"E99"),sQuery(id+"F0.wireOp",EDGE,"E100"),sQuery(id+"F0.wireOp",EDGE,"E101"),sQuery(id+"F0.wireOp",EDGE,"E102"),sQuery(id+"F0.wireOp",EDGE,"E103"),sQuery(id+"F0.wireOp",EDGE,"E104"),sQuery(id+"F0.wireOp",EDGE,"E105"),sQuery(id+"F0.wireOp",EDGE,"E106"),sQuery(id+"F0.wireOp",EDGE,"E107"),sQuery(id+"F0.wireOp",EDGE,"E108"),sQuery(id+"F0.wireOp",EDGE,"E109"),sQuery(id+"F0.wireOp",EDGE,"E110"),sQuery(id+"F0.wireOp",EDGE,"E111"),sQuery(id+"F0.wireOp",EDGE,"E112"),sQuery(id+"F0.wireOp",EDGE,"E113"),sQuery(id+"F0.wireOp",EDGE,"E114"),sQuery(id+"F0.wireOp",EDGE,"E115"),sQuery(id+"F0.wireOp",EDGE,"E116"),sQuery(id+"F0.wireOp",EDGE,"E117"),sQuery(id+"F0.wireOp",EDGE,"E118"),sQuery(id+"F0.wireOp",EDGE,"E119"),sQuery(id+"F0.wireOp",EDGE,"E120"),sQuery(id+"F0.wireOp",EDGE,"E121"),sQuery(id+"F0.wireOp",EDGE,"E122"),sQuery(id+"F0.wireOp",EDGE,"E123"),sQuery(id+"F0.wireOp",EDGE,"E124"),sQuery(id+"F0.wireOp",EDGE,"E125"),sQuery(id+"F0.wireOp",EDGE,"E126"),sQuery(id+"F0.wireOp",EDGE,"E127"),sQuery(id+"F0.wireOp",EDGE,"E128"),sQuery(id+"F0.wireOp",EDGE,"E129"),sQuery(id+"F0.wireOp",EDGE,"E130"),sQuery(id+"F0.wireOp",EDGE,"E131"),sQuery(id+"F0.wireOp",EDGE,"E132"),sQuery(id+"F0.wireOp",EDGE,"E133"),sQuery(id+"F0.wireOp",EDGE,"E134"),sQuery(id+"F0.wireOp",EDGE,"E135"),sQuery(id+"F0.wireOp",EDGE,"E136"),sQuery(id+"F0.wireOp",EDGE,"E137"),sQuery(id+"F0.wireOp",EDGE,"E138"),sQuery(id+"F0.wireOp",EDGE,"E139"),sQuery(id+"F0.wireOp",EDGE,"E140"),sQuery(id+"F0.wireOp",EDGE,"E141"),sQuery(id+"F0.wireOp",EDGE,"E142"),sQuery(id+"F0.wireOp",EDGE,"E143"),sQuery(id+"F0.wireOp",EDGE,"E144"),sQuery(id+"F0.wireOp",EDGE,"E145"),sQuery(id+"F0.wireOp",EDGE,"E146"),sQuery(id+"F0.wireOp",EDGE,"E147"),sQuery(id+"F0.wireOp",EDGE,"E148"),sQuery(id+"F0.wireOp",EDGE,"E149"),sQuery(id+"F0.wireOp",EDGE,"E150"),sQuery(id+"F0.wireOp",EDGE,"E151"),sQuery(id+"F0.wireOp",EDGE,"E152"),sQuery(id+"F0.wireOp",EDGE,"E153"),sQuery(id+"F0.wireOp",EDGE,"E154"),sQuery(id+"F0.wireOp",EDGE,"E155"),sQuery(id+"F0.wireOp",EDGE,"E156"),sQuery(id+"F0.wireOp",EDGE,"E157"),sQuery(id+"F0.wireOp",EDGE,"E158"),sQuery(id+"F0.wireOp",EDGE,"E159"),sQuery(id+"F0.wireOp",EDGE,"E160"),sQuery(id+"F0.wireOp",EDGE,"E161"),sQuery(id+"F0.wireOp",EDGE,"E162"),sQuery(id+"F0.wireOp",EDGE,"E163"),sQuery(id+"F0.wireOp",EDGE,"E164"),sQuery(id+"F0.wireOp",EDGE,"E165"),sQuery(id+"F0.wireOp",EDGE,"E166"),sQuery(id+"F0.wireOp",EDGE,"E167"),sQuery(id+"F0.wireOp",EDGE,"E168"),sQuery(id+"F0.wireOp",EDGE,"E169"),sQuery(id+"F0.wireOp",EDGE,"E170"),sQuery(id+"F0.wireOp",EDGE,"E171"),sQuery(id+"F0.wireOp",EDGE,"E172"),sQuery(id+"F0.wireOp",EDGE,"E173"),sQuery(id+"F0.wireOp",EDGE,"E174"),sQuery(id+"F0.wireOp",EDGE,"E175"),sQuery(id+"F0.wireOp",EDGE,"E176"),sQuery(id+"F0.wireOp",EDGE,"E177"),sQuery(id+"F0.wireOp",EDGE,"E178"),sQuery(id+"F0.wireOp",EDGE,"E179"),sQuery(id+"F0.wireOp",EDGE,"E180"),sQuery(id+"F0.wireOp",EDGE,"E181"),sQuery(id+"F0.wireOp",EDGE,"E182"),sQuery(id+"F0.wireOp",EDGE,"E183"),sQuery(id+"F0.wireOp",EDGE,"E184"),sQuery(id+"F0.wireOp",EDGE,"E185"),sQuery(id+"F0.wireOp",EDGE,"E186"),sQuery(id+"F0.wireOp",EDGE,"E187"),sQuery(id+"F0.wireOp",EDGE,"E188"),sQuery(id+"F0.wireOp",EDGE,"E189"),sQuery(id+"F0.wireOp",EDGE,"E190"),sQuery(id+"F0.wireOp",EDGE,"E191"),sQuery(id+"F0.wireOp",EDGE,"E192"),sQuery(id+"F0.wireOp",EDGE,"E193"),sQuery(id+"F0.wireOp",EDGE,"E194"),sQuery(id+"F0.wireOp",EDGE,"E195"),sQuery(id+"F0.wireOp",EDGE,"E196")])]});
            var Q51;
            Q51=makeQuery(id+"F1.opExtrude","SWEPT_BODY",BODY,{"disambiguationData":[OSD([sQuery(id+"F0.wireOp",EDGE,"E729"),sQuery(id+"F0.wireOp",EDGE,"E730"),sQuery(id+"F0.wireOp",EDGE,"E731"),sQuery(id+"F0.wireOp",EDGE,"E732"),sQuery(id+"F0.wireOp",EDGE,"E733"),sQuery(id+"F0.wireOp",EDGE,"E734"),sQuery(id+"F0.wireOp",EDGE,"E735"),sQuery(id+"F0.wireOp",EDGE,"E736"),sQuery(id+"F0.wireOp",EDGE,"E737"),sQuery(id+"F0.wireOp",EDGE,"E738"),sQuery(id+"F0.wireOp",EDGE,"E739"),sQuery(id+"F0.wireOp",EDGE,"E740")])]});
            var Q52;
            Q52=makeQuery(id+"F1.opExtrude","SWEPT_BODY",BODY,{"disambiguationData":[OSD([sQuery(id+"F0.wireOp",EDGE,"E765"),sQuery(id+"F0.wireOp",EDGE,"E766"),sQuery(id+"F0.wireOp",EDGE,"E767"),sQuery(id+"F0.wireOp",EDGE,"E768"),sQuery(id+"F0.wireOp",EDGE,"E769"),sQuery(id+"F0.wireOp",EDGE,"E770"),sQuery(id+"F0.wireOp",EDGE,"E771"),sQuery(id+"F0.wireOp",EDGE,"E772"),sQuery(id+"F0.wireOp",EDGE,"E773"),sQuery(id+"F0.wireOp",EDGE,"E774"),sQuery(id+"F0.wireOp",EDGE,"E775"),sQuery(id+"F0.wireOp",EDGE,"E776")])]});
            var Q53;
            Q53=makeQuery(id+"F1.opExtrude","SWEPT_BODY",BODY,{"disambiguationData":[OSD([sQuery(id+"F0.wireOp",EDGE,"E1687"),sQuery(id+"F0.wireOp",EDGE,"E1688"),sQuery(id+"F0.wireOp",EDGE,"E1689"),sQuery(id+"F0.wireOp",EDGE,"E1690"),sQuery(id+"F0.wireOp",EDGE,"E1691"),sQuery(id+"F0.wireOp",EDGE,"E1692"),sQuery(id+"F0.wireOp",EDGE,"E1693"),sQuery(id+"F0.wireOp",EDGE,"E1694"),sQuery(id+"F0.wireOp",EDGE,"E1695"),sQuery(id+"F0.wireOp",EDGE,"E1696"),sQuery(id+"F0.wireOp",EDGE,"E1697"),sQuery(id+"F0.wireOp",EDGE,"E1698"),sQuery(id+"F0.wireOp",EDGE,"E1699"),sQuery(id+"F0.wireOp",EDGE,"E1700"),sQuery(id+"F0.wireOp",EDGE,"E1701"),sQuery(id+"F0.wireOp",EDGE,"E1702"),sQuery(id+"F0.wireOp",EDGE,"E1703"),sQuery(id+"F0.wireOp",EDGE,"E1704"),sQuery(id+"F0.wireOp",EDGE,"E1705"),sQuery(id+"F0.wireOp",EDGE,"E1706"),sQuery(id+"F0.wireOp",EDGE,"E1707"),sQuery(id+"F0.wireOp",EDGE,"E1708"),sQuery(id+"F0.wireOp",EDGE,"E1709"),sQuery(id+"F0.wireOp",EDGE,"E1710"),sQuery(id+"F0.wireOp",EDGE,"E1711"),sQuery(id+"F0.wireOp",EDGE,"E1712"),sQuery(id+"F0.wireOp",EDGE,"E1713"),sQuery(id+"F0.wireOp",EDGE,"E1714"),sQuery(id+"F0.wireOp",EDGE,"E1715"),sQuery(id+"F0.wireOp",EDGE,"E1716"),sQuery(id+"F0.wireOp",EDGE,"E1717"),sQuery(id+"F0.wireOp",EDGE,"E1718"),sQuery(id+"F0.wireOp",EDGE,"E1719"),sQuery(id+"F0.wireOp",EDGE,"E1720"),sQuery(id+"F0.wireOp",EDGE,"E1721"),sQuery(id+"F0.wireOp",EDGE,"E1722"),sQuery(id+"F0.wireOp",EDGE,"E1723"),sQuery(id+"F0.wireOp",EDGE,"E1724"),sQuery(id+"F0.wireOp",EDGE,"E1725"),sQuery(id+"F0.wireOp",EDGE,"E1726"),sQuery(id+"F0.wireOp",EDGE,"E1727"),sQuery(id+"F0.wireOp",EDGE,"E1728"),sQuery(id+"F0.wireOp",EDGE,"E1729"),sQuery(id+"F0.wireOp",EDGE,"E1730"),sQuery(id+"F0.wireOp",EDGE,"E1731"),sQuery(id+"F0.wireOp",EDGE,"E1732"),sQuery(id+"F0.wireOp",EDGE,"E1733"),sQuery(id+"F0.wireOp",EDGE,"E1734"),sQuery(id+"F0.wireOp",EDGE,"E1735"),sQuery(id+"F0.wireOp",EDGE,"E1736"),sQuery(id+"F0.wireOp",EDGE,"E1737"),sQuery(id+"F0.wireOp",EDGE,"E1738"),sQuery(id+"F0.wireOp",EDGE,"E1739"),sQuery(id+"F0.wireOp",EDGE,"E1740"),sQuery(id+"F0.wireOp",EDGE,"E1741"),sQuery(id+"F0.wireOp",EDGE,"E1742"),sQuery(id+"F0.wireOp",EDGE,"E1743"),sQuery(id+"F0.wireOp",EDGE,"E1744"),sQuery(id+"F0.wireOp",EDGE,"E1745"),sQuery(id+"F0.wireOp",EDGE,"E1746"),sQuery(id+"F0.wireOp",EDGE,"E1747"),sQuery(id+"F0.wireOp",EDGE,"E1748"),sQuery(id+"F0.wireOp",EDGE,"E1749"),sQuery(id+"F0.wireOp",EDGE,"E1750"),sQuery(id+"F0.wireOp",EDGE,"E1751"),sQuery(id+"F0.wireOp",EDGE,"E1752"),sQuery(id+"F0.wireOp",EDGE,"E1753"),sQuery(id+"F0.wireOp",EDGE,"E1754"),sQuery(id+"F0.wireOp",EDGE,"E1755"),sQuery(id+"F0.wireOp",EDGE,"E1756"),sQuery(id+"F0.wireOp",EDGE,"E1757"),sQuery(id+"F0.wireOp",EDGE,"E1758"),sQuery(id+"F0.wireOp",EDGE,"E1759"),sQuery(id+"F0.wireOp",EDGE,"E1760"),sQuery(id+"F0.wireOp",EDGE,"E1761"),sQuery(id+"F0.wireOp",EDGE,"E1762"),sQuery(id+"F0.wireOp",EDGE,"E1763"),sQuery(id+"F0.wireOp",EDGE,"E1764"),sQuery(id+"F0.wireOp",EDGE,"E1765"),sQuery(id+"F0.wireOp",EDGE,"E1766"),sQuery(id+"F0.wireOp",EDGE,"E1767"),sQuery(id+"F0.wireOp",EDGE,"E1768"),sQuery(id+"F0.wireOp",EDGE,"E1769"),sQuery(id+"F0.wireOp",EDGE,"E1770"),sQuery(id+"F0.wireOp",EDGE,"E1771"),sQuery(id+"F0.wireOp",EDGE,"E1772"),sQuery(id+"F0.wireOp",EDGE,"E1773"),sQuery(id+"F0.wireOp",EDGE,"E1774")])]});
            var Q54;
            Q54=makeQuery(id+"F1.opExtrude","SWEPT_BODY",BODY,{"disambiguationData":[OSD([sQuery(id+"F0.wireOp",EDGE,"E2013"),sQuery(id+"F0.wireOp",EDGE,"E2014"),sQuery(id+"F0.wireOp",EDGE,"E2015"),sQuery(id+"F0.wireOp",EDGE,"E2016"),sQuery(id+"F0.wireOp",EDGE,"E2017"),sQuery(id+"F0.wireOp",EDGE,"E2018"),sQuery(id+"F0.wireOp",EDGE,"E2019"),sQuery(id+"F0.wireOp",EDGE,"E2020"),sQuery(id+"F0.wireOp",EDGE,"E2021"),sQuery(id+"F0.wireOp",EDGE,"E2022"),sQuery(id+"F0.wireOp",EDGE,"E2023")])]});
            var Q55;
            Q55=makeQuery(id+"F1.opExtrude","SWEPT_BODY",BODY,{"disambiguationData":[OSD([sQuery(id+"F0.wireOp",EDGE,"E2126"),sQuery(id+"F0.wireOp",EDGE,"E2127"),sQuery(id+"F0.wireOp",EDGE,"E2128"),sQuery(id+"F0.wireOp",EDGE,"E2129"),sQuery(id+"F0.wireOp",EDGE,"E2130"),sQuery(id+"F0.wireOp",EDGE,"E2131"),sQuery(id+"F0.wireOp",EDGE,"E2132"),sQuery(id+"F0.wireOp",EDGE,"E2133"),sQuery(id+"F0.wireOp",EDGE,"E2134"),sQuery(id+"F0.wireOp",EDGE,"E2135"),sQuery(id+"F0.wireOp",EDGE,"E2136"),sQuery(id+"F0.wireOp",EDGE,"E2137"),sQuery(id+"F0.wireOp",EDGE,"E2138"),sQuery(id+"F0.wireOp",EDGE,"E2139"),sQuery(id+"F0.wireOp",EDGE,"E2140"),sQuery(id+"F0.wireOp",EDGE,"E2141"),sQuery(id+"F0.wireOp",EDGE,"E2142"),sQuery(id+"F0.wireOp",EDGE,"E2143"),sQuery(id+"F0.wireOp",EDGE,"E2144"),sQuery(id+"F0.wireOp",EDGE,"E2145"),sQuery(id+"F0.wireOp",EDGE,"E2146"),sQuery(id+"F0.wireOp",EDGE,"E2147"),sQuery(id+"F0.wireOp",EDGE,"E2148"),sQuery(id+"F0.wireOp",EDGE,"E2149"),sQuery(id+"F0.wireOp",EDGE,"E2150"),sQuery(id+"F0.wireOp",EDGE,"E2151"),sQuery(id+"F0.wireOp",EDGE,"E2152"),sQuery(id+"F0.wireOp",EDGE,"E2153"),sQuery(id+"F0.wireOp",EDGE,"E2154"),sQuery(id+"F0.wireOp",EDGE,"E2155"),sQuery(id+"F0.wireOp",EDGE,"E2156"),sQuery(id+"F0.wireOp",EDGE,"E2157"),sQuery(id+"F0.wireOp",EDGE,"E2158"),sQuery(id+"F0.wireOp",EDGE,"E2159"),sQuery(id+"F0.wireOp",EDGE,"E2160"),sQuery(id+"F0.wireOp",EDGE,"E2161"),sQuery(id+"F0.wireOp",EDGE,"E2162"),sQuery(id+"F0.wireOp",EDGE,"E2163"),sQuery(id+"F0.wireOp",EDGE,"E2164"),sQuery(id+"F0.wireOp",EDGE,"E2165"),sQuery(id+"F0.wireOp",EDGE,"E2166"),sQuery(id+"F0.wireOp",EDGE,"E2167"),sQuery(id+"F0.wireOp",EDGE,"E2168"),sQuery(id+"F0.wireOp",EDGE,"E2169"),sQuery(id+"F0.wireOp",EDGE,"E2170"),sQuery(id+"F0.wireOp",EDGE,"E2171"),sQuery(id+"F0.wireOp",EDGE,"E2172"),sQuery(id+"F0.wireOp",EDGE,"E2173"),sQuery(id+"F0.wireOp",EDGE,"E2174"),sQuery(id+"F0.wireOp",EDGE,"E2175"),sQuery(id+"F0.wireOp",EDGE,"E2176"),sQuery(id+"F0.wireOp",EDGE,"E2177"),sQuery(id+"F0.wireOp",EDGE,"E2178"),sQuery(id+"F0.wireOp",EDGE,"E2179"),sQuery(id+"F0.wireOp",EDGE,"E2180"),sQuery(id+"F0.wireOp",EDGE,"E2181"),sQuery(id+"F0.wireOp",EDGE,"E2182"),sQuery(id+"F0.wireOp",EDGE,"E2183"),sQuery(id+"F0.wireOp",EDGE,"E2184"),sQuery(id+"F0.wireOp",EDGE,"E2185"),sQuery(id+"F0.wireOp",EDGE,"E2186"),sQuery(id+"F0.wireOp",EDGE,"E2187"),sQuery(id+"F0.wireOp",EDGE,"E2188"),sQuery(id+"F0.wireOp",EDGE,"E2189"),sQuery(id+"F0.wireOp",EDGE,"E2190"),sQuery(id+"F0.wireOp",EDGE,"E2191"),sQuery(id+"F0.wireOp",EDGE,"E2192"),sQuery(id+"F0.wireOp",EDGE,"E2193"),sQuery(id+"F0.wireOp",EDGE,"E2194"),sQuery(id+"F0.wireOp",EDGE,"E2195"),sQuery(id+"F0.wireOp",EDGE,"E2196"),sQuery(id+"F0.wireOp",EDGE,"E2197"),sQuery(id+"F0.wireOp",EDGE,"E2198"),sQuery(id+"F0.wireOp",EDGE,"E2199"),sQuery(id+"F0.wireOp",EDGE,"E2200"),sQuery(id+"F0.wireOp",EDGE,"E2201"),sQuery(id+"F0.wireOp",EDGE,"E2202"),sQuery(id+"F0.wireOp",EDGE,"E2203")])]});
            var Q56;
            Q56=makeQuery(id+"F1.opExtrude","SWEPT_BODY",BODY,{"disambiguationData":[OSD([sQuery(id+"F0.wireOp",EDGE,"E2438"),sQuery(id+"F0.wireOp",EDGE,"E2439"),sQuery(id+"F0.wireOp",EDGE,"E2440"),sQuery(id+"F0.wireOp",EDGE,"E2441"),sQuery(id+"F0.wireOp",EDGE,"E2442"),sQuery(id+"F0.wireOp",EDGE,"E2443")])]});
            var Q57;
            Q57=makeQuery(id+"F1.opExtrude","SWEPT_BODY",BODY,{"disambiguationData":[OSD([sQuery(id+"F0.wireOp",EDGE,"E2278"),sQuery(id+"F0.wireOp",EDGE,"E2279"),sQuery(id+"F0.wireOp",EDGE,"E2280"),sQuery(id+"F0.wireOp",EDGE,"E2281"),sQuery(id+"F0.wireOp",EDGE,"E2282"),sQuery(id+"F0.wireOp",EDGE,"E2283"),sQuery(id+"F0.wireOp",EDGE,"E2284"),sQuery(id+"F0.wireOp",EDGE,"E2285"),sQuery(id+"F0.wireOp",EDGE,"E2286"),sQuery(id+"F0.wireOp",EDGE,"E2287"),sQuery(id+"F0.wireOp",EDGE,"E2288"),sQuery(id+"F0.wireOp",EDGE,"E2289"),sQuery(id+"F0.wireOp",EDGE,"E2290"),sQuery(id+"F0.wireOp",EDGE,"E2291"),sQuery(id+"F0.wireOp",EDGE,"E2292"),sQuery(id+"F0.wireOp",EDGE,"E2293"),sQuery(id+"F0.wireOp",EDGE,"E2294"),sQuery(id+"F0.wireOp",EDGE,"E2295"),sQuery(id+"F0.wireOp",EDGE,"E2296"),sQuery(id+"F0.wireOp",EDGE,"E2297"),sQuery(id+"F0.wireOp",EDGE,"E2298"),sQuery(id+"F0.wireOp",EDGE,"E2299"),sQuery(id+"F0.wireOp",EDGE,"E2300"),sQuery(id+"F0.wireOp",EDGE,"E2301"),sQuery(id+"F0.wireOp",EDGE,"E2302"),sQuery(id+"F0.wireOp",EDGE,"E2303"),sQuery(id+"F0.wireOp",EDGE,"E2304"),sQuery(id+"F0.wireOp",EDGE,"E2305"),sQuery(id+"F0.wireOp",EDGE,"E2306"),sQuery(id+"F0.wireOp",EDGE,"E2307"),sQuery(id+"F0.wireOp",EDGE,"E2308"),sQuery(id+"F0.wireOp",EDGE,"E2309"),sQuery(id+"F0.wireOp",EDGE,"E2310"),sQuery(id+"F0.wireOp",EDGE,"E2311"),sQuery(id+"F0.wireOp",EDGE,"E2312"),sQuery(id+"F0.wireOp",EDGE,"E2313"),sQuery(id+"F0.wireOp",EDGE,"E2314"),sQuery(id+"F0.wireOp",EDGE,"E2315"),sQuery(id+"F0.wireOp",EDGE,"E2316"),sQuery(id+"F0.wireOp",EDGE,"E2317"),sQuery(id+"F0.wireOp",EDGE,"E2318"),sQuery(id+"F0.wireOp",EDGE,"E2319"),sQuery(id+"F0.wireOp",EDGE,"E2320"),sQuery(id+"F0.wireOp",EDGE,"E2321"),sQuery(id+"F0.wireOp",EDGE,"E2322"),sQuery(id+"F0.wireOp",EDGE,"E2323"),sQuery(id+"F0.wireOp",EDGE,"E2324"),sQuery(id+"F0.wireOp",EDGE,"E2325"),sQuery(id+"F0.wireOp",EDGE,"E2326"),sQuery(id+"F0.wireOp",EDGE,"E2327"),sQuery(id+"F0.wireOp",EDGE,"E2328"),sQuery(id+"F0.wireOp",EDGE,"E2329"),sQuery(id+"F0.wireOp",EDGE,"E2330"),sQuery(id+"F0.wireOp",EDGE,"E2331"),sQuery(id+"F0.wireOp",EDGE,"E2332"),sQuery(id+"F0.wireOp",EDGE,"E2333"),sQuery(id+"F0.wireOp",EDGE,"E2334"),sQuery(id+"F0.wireOp",EDGE,"E2335"),sQuery(id+"F0.wireOp",EDGE,"E2336"),sQuery(id+"F0.wireOp",EDGE,"E2337"),sQuery(id+"F0.wireOp",EDGE,"E2338"),sQuery(id+"F0.wireOp",EDGE,"E2339"),sQuery(id+"F0.wireOp",EDGE,"E2340"),sQuery(id+"F0.wireOp",EDGE,"E2341"),sQuery(id+"F0.wireOp",EDGE,"E2342"),sQuery(id+"F0.wireOp",EDGE,"E2343"),sQuery(id+"F0.wireOp",EDGE,"E2344"),sQuery(id+"F0.wireOp",EDGE,"E2345"),sQuery(id+"F0.wireOp",EDGE,"E2346"),sQuery(id+"F0.wireOp",EDGE,"E2347"),sQuery(id+"F0.wireOp",EDGE,"E2348"),sQuery(id+"F0.wireOp",EDGE,"E2349"),sQuery(id+"F0.wireOp",EDGE,"E2350"),sQuery(id+"F0.wireOp",EDGE,"E2351")])]});
            var Q58;
            Q58=makeQuery(id+"F1.opExtrude","SWEPT_BODY",BODY,{"disambiguationData":[OSD([sQuery(id+"F0.wireOp",EDGE,"E197"),sQuery(id+"F0.wireOp",EDGE,"E198"),sQuery(id+"F0.wireOp",EDGE,"E199"),sQuery(id+"F0.wireOp",EDGE,"E200"),sQuery(id+"F0.wireOp",EDGE,"E201"),sQuery(id+"F0.wireOp",EDGE,"E202"),sQuery(id+"F0.wireOp",EDGE,"E203"),sQuery(id+"F0.wireOp",EDGE,"E204"),sQuery(id+"F0.wireOp",EDGE,"E205"),sQuery(id+"F0.wireOp",EDGE,"E206"),sQuery(id+"F0.wireOp",EDGE,"E207"),sQuery(id+"F0.wireOp",EDGE,"E208"),sQuery(id+"F0.wireOp",EDGE,"E209"),sQuery(id+"F0.wireOp",EDGE,"E210"),sQuery(id+"F0.wireOp",EDGE,"E211"),sQuery(id+"F0.wireOp",EDGE,"E212"),sQuery(id+"F0.wireOp",EDGE,"E213"),sQuery(id+"F0.wireOp",EDGE,"E214"),sQuery(id+"F0.wireOp",EDGE,"E215"),sQuery(id+"F0.wireOp",EDGE,"E216"),sQuery(id+"F0.wireOp",EDGE,"E217"),sQuery(id+"F0.wireOp",EDGE,"E218"),sQuery(id+"F0.wireOp",EDGE,"E219"),sQuery(id+"F0.wireOp",EDGE,"E220"),sQuery(id+"F0.wireOp",EDGE,"E221"),sQuery(id+"F0.wireOp",EDGE,"E222"),sQuery(id+"F0.wireOp",EDGE,"E223"),sQuery(id+"F0.wireOp",EDGE,"E224"),sQuery(id+"F0.wireOp",EDGE,"E225"),sQuery(id+"F0.wireOp",EDGE,"E226"),sQuery(id+"F0.wireOp",EDGE,"E227"),sQuery(id+"F0.wireOp",EDGE,"E228"),sQuery(id+"F0.wireOp",EDGE,"E229"),sQuery(id+"F0.wireOp",EDGE,"E230"),sQuery(id+"F0.wireOp",EDGE,"E231"),sQuery(id+"F0.wireOp",EDGE,"E232"),sQuery(id+"F0.wireOp",EDGE,"E233"),sQuery(id+"F0.wireOp",EDGE,"E234"),sQuery(id+"F0.wireOp",EDGE,"E235"),sQuery(id+"F0.wireOp",EDGE,"E236"),sQuery(id+"F0.wireOp",EDGE,"E237"),sQuery(id+"F0.wireOp",EDGE,"E238"),sQuery(id+"F0.wireOp",EDGE,"E239"),sQuery(id+"F0.wireOp",EDGE,"E240"),sQuery(id+"F0.wireOp",EDGE,"E241"),sQuery(id+"F0.wireOp",EDGE,"E242"),sQuery(id+"F0.wireOp",EDGE,"E243"),sQuery(id+"F0.wireOp",EDGE,"E244"),sQuery(id+"F0.wireOp",EDGE,"E245"),sQuery(id+"F0.wireOp",EDGE,"E246"),sQuery(id+"F0.wireOp",EDGE,"E247"),sQuery(id+"F0.wireOp",EDGE,"E248"),sQuery(id+"F0.wireOp",EDGE,"E249"),sQuery(id+"F0.wireOp",EDGE,"E250"),sQuery(id+"F0.wireOp",EDGE,"E251"),sQuery(id+"F0.wireOp",EDGE,"E252"),sQuery(id+"F0.wireOp",EDGE,"E253"),sQuery(id+"F0.wireOp",EDGE,"E254"),sQuery(id+"F0.wireOp",EDGE,"E255"),sQuery(id+"F0.wireOp",EDGE,"E256"),sQuery(id+"F0.wireOp",EDGE,"E257"),sQuery(id+"F0.wireOp",EDGE,"E258"),sQuery(id+"F0.wireOp",EDGE,"E259"),sQuery(id+"F0.wireOp",EDGE,"E260"),sQuery(id+"F0.wireOp",EDGE,"E261"),sQuery(id+"F0.wireOp",EDGE,"E262"),sQuery(id+"F0.wireOp",EDGE,"E263"),sQuery(id+"F0.wireOp",EDGE,"E264"),sQuery(id+"F0.wireOp",EDGE,"E265"),sQuery(id+"F0.wireOp",EDGE,"E266"),sQuery(id+"F0.wireOp",EDGE,"E267"),sQuery(id+"F0.wireOp",EDGE,"E268"),sQuery(id+"F0.wireOp",EDGE,"E269"),sQuery(id+"F0.wireOp",EDGE,"E270"),sQuery(id+"F0.wireOp",EDGE,"E271"),sQuery(id+"F0.wireOp",EDGE,"E272"),sQuery(id+"F0.wireOp",EDGE,"E273"),sQuery(id+"F0.wireOp",EDGE,"E274"),sQuery(id+"F0.wireOp",EDGE,"E275"),sQuery(id+"F0.wireOp",EDGE,"E276"),sQuery(id+"F0.wireOp",EDGE,"E277"),sQuery(id+"F0.wireOp",EDGE,"E278"),sQuery(id+"F0.wireOp",EDGE,"E279"),sQuery(id+"F0.wireOp",EDGE,"E280"),sQuery(id+"F0.wireOp",EDGE,"E281"),sQuery(id+"F0.wireOp",EDGE,"E282"),sQuery(id+"F0.wireOp",EDGE,"E283"),sQuery(id+"F0.wireOp",EDGE,"E284"),sQuery(id+"F0.wireOp",EDGE,"E285"),sQuery(id+"F0.wireOp",EDGE,"E286"),sQuery(id+"F0.wireOp",EDGE,"E287"),sQuery(id+"F0.wireOp",EDGE,"E288"),sQuery(id+"F0.wireOp",EDGE,"E289"),sQuery(id+"F0.wireOp",EDGE,"E290"),sQuery(id+"F0.wireOp",EDGE,"E291"),sQuery(id+"F0.wireOp",EDGE,"E292"),sQuery(id+"F0.wireOp",EDGE,"E293"),sQuery(id+"F0.wireOp",EDGE,"E294"),sQuery(id+"F0.wireOp",EDGE,"E295"),sQuery(id+"F0.wireOp",EDGE,"E296"),sQuery(id+"F0.wireOp",EDGE,"E297"),sQuery(id+"F0.wireOp",EDGE,"E298"),sQuery(id+"F0.wireOp",EDGE,"E299"),sQuery(id+"F0.wireOp",EDGE,"E300"),sQuery(id+"F0.wireOp",EDGE,"E301"),sQuery(id+"F0.wireOp",EDGE,"E302"),sQuery(id+"F0.wireOp",EDGE,"E303"),sQuery(id+"F0.wireOp",EDGE,"E304"),sQuery(id+"F0.wireOp",EDGE,"E305"),sQuery(id+"F0.wireOp",EDGE,"E306"),sQuery(id+"F0.wireOp",EDGE,"E307"),sQuery(id+"F0.wireOp",EDGE,"E308"),sQuery(id+"F0.wireOp",EDGE,"E309"),sQuery(id+"F0.wireOp",EDGE,"E310"),sQuery(id+"F0.wireOp",EDGE,"E311"),sQuery(id+"F0.wireOp",EDGE,"E312"),sQuery(id+"F0.wireOp",EDGE,"E313"),sQuery(id+"F0.wireOp",EDGE,"E314"),sQuery(id+"F0.wireOp",EDGE,"E315"),sQuery(id+"F0.wireOp",EDGE,"E316"),sQuery(id+"F0.wireOp",EDGE,"E317"),sQuery(id+"F0.wireOp",EDGE,"E318"),sQuery(id+"F0.wireOp",EDGE,"E319"),sQuery(id+"F0.wireOp",EDGE,"E320")])]});
            var Q59;
            Q59=makeQuery(id+"F1.opExtrude","SWEPT_BODY",BODY,{"disambiguationData":[OSD([sQuery(id+"F0.wireOp",EDGE,"E741"),sQuery(id+"F0.wireOp",EDGE,"E742"),sQuery(id+"F0.wireOp",EDGE,"E743"),sQuery(id+"F0.wireOp",EDGE,"E744"),sQuery(id+"F0.wireOp",EDGE,"E745"),sQuery(id+"F0.wireOp",EDGE,"E746"),sQuery(id+"F0.wireOp",EDGE,"E747"),sQuery(id+"F0.wireOp",EDGE,"E748"),sQuery(id+"F0.wireOp",EDGE,"E749"),sQuery(id+"F0.wireOp",EDGE,"E750"),sQuery(id+"F0.wireOp",EDGE,"E751"),sQuery(id+"F0.wireOp",EDGE,"E752")])]});
            var Q60;
            Q60=makeQuery(id+"F1.opExtrude","SWEPT_BODY",BODY,{"disambiguationData":[OSD([sQuery(id+"F0.wireOp",EDGE,"E670"),sQuery(id+"F0.wireOp",EDGE,"E671"),sQuery(id+"F0.wireOp",EDGE,"E672"),sQuery(id+"F0.wireOp",EDGE,"E673"),sQuery(id+"F0.wireOp",EDGE,"E674"),sQuery(id+"F0.wireOp",EDGE,"E675"),sQuery(id+"F0.wireOp",EDGE,"E676"),sQuery(id+"F0.wireOp",EDGE,"E677"),sQuery(id+"F0.wireOp",EDGE,"E678"),sQuery(id+"F0.wireOp",EDGE,"E679"),sQuery(id+"F0.wireOp",EDGE,"E680"),sQuery(id+"F0.wireOp",EDGE,"E681"),sQuery(id+"F0.wireOp",EDGE,"E682"),sQuery(id+"F0.wireOp",EDGE,"E683"),sQuery(id+"F0.wireOp",EDGE,"E684"),sQuery(id+"F0.wireOp",EDGE,"E685"),sQuery(id+"F0.wireOp",EDGE,"E686"),sQuery(id+"F0.wireOp",EDGE,"E687"),sQuery(id+"F0.wireOp",EDGE,"E688"),sQuery(id+"F0.wireOp",EDGE,"E689"),sQuery(id+"F0.wireOp",EDGE,"E690"),sQuery(id+"F0.wireOp",EDGE,"E691"),sQuery(id+"F0.wireOp",EDGE,"E692"),sQuery(id+"F0.wireOp",EDGE,"E693"),sQuery(id+"F0.wireOp",EDGE,"E694"),sQuery(id+"F0.wireOp",EDGE,"E695"),sQuery(id+"F0.wireOp",EDGE,"E696"),sQuery(id+"F0.wireOp",EDGE,"E697"),sQuery(id+"F0.wireOp",EDGE,"E698"),sQuery(id+"F0.wireOp",EDGE,"E699"),sQuery(id+"F0.wireOp",EDGE,"E700"),sQuery(id+"F0.wireOp",EDGE,"E701"),sQuery(id+"F0.wireOp",EDGE,"E702"),sQuery(id+"F0.wireOp",EDGE,"E703"),sQuery(id+"F0.wireOp",EDGE,"E704"),sQuery(id+"F0.wireOp",EDGE,"E705"),sQuery(id+"F0.wireOp",EDGE,"E706"),sQuery(id+"F0.wireOp",EDGE,"E707"),sQuery(id+"F0.wireOp",EDGE,"E708"),sQuery(id+"F0.wireOp",EDGE,"E709"),sQuery(id+"F0.wireOp",EDGE,"E710"),sQuery(id+"F0.wireOp",EDGE,"E711"),sQuery(id+"F0.wireOp",EDGE,"E712"),sQuery(id+"F0.wireOp",EDGE,"E713"),sQuery(id+"F0.wireOp",EDGE,"E714"),sQuery(id+"F0.wireOp",EDGE,"E715"),sQuery(id+"F0.wireOp",EDGE,"E716")])]});
            var Q61;
            Q61=makeQuery(id+"F1.opExtrude","SWEPT_BODY",BODY,{"disambiguationData":[OSD([sQuery(id+"F0.wireOp",EDGE,"E1183"),sQuery(id+"F0.wireOp",EDGE,"E1184"),sQuery(id+"F0.wireOp",EDGE,"E1185"),sQuery(id+"F0.wireOp",EDGE,"E1186"),sQuery(id+"F0.wireOp",EDGE,"E1187"),sQuery(id+"F0.wireOp",EDGE,"E1188"),sQuery(id+"F0.wireOp",EDGE,"E1189"),sQuery(id+"F0.wireOp",EDGE,"E1190"),sQuery(id+"F0.wireOp",EDGE,"E1191"),sQuery(id+"F0.wireOp",EDGE,"E1192"),sQuery(id+"F0.wireOp",EDGE,"E1193"),sQuery(id+"F0.wireOp",EDGE,"E1194")])]});
            var Q62;
            Q62=makeQuery(id+"F1.opExtrude","SWEPT_BODY",BODY,{"disambiguationData":[OSD([sQuery(id+"F0.wireOp",EDGE,"E1320"),sQuery(id+"F0.wireOp",EDGE,"E1321"),sQuery(id+"F0.wireOp",EDGE,"E1322"),sQuery(id+"F0.wireOp",EDGE,"E1323"),sQuery(id+"F0.wireOp",EDGE,"E1324"),sQuery(id+"F0.wireOp",EDGE,"E1325"),sQuery(id+"F0.wireOp",EDGE,"E1326"),sQuery(id+"F0.wireOp",EDGE,"E1327"),sQuery(id+"F0.wireOp",EDGE,"E1328"),sQuery(id+"F0.wireOp",EDGE,"E1329"),sQuery(id+"F0.wireOp",EDGE,"E1330")])]});
            var Q63;
            Q63=makeQuery(id+"F1.opExtrude","SWEPT_BODY",BODY,{"disambiguationData":[OSD([sQuery(id+"F0.wireOp",EDGE,"E1431"),sQuery(id+"F0.wireOp",EDGE,"E1432"),sQuery(id+"F0.wireOp",EDGE,"E1433"),sQuery(id+"F0.wireOp",EDGE,"E1434"),sQuery(id+"F0.wireOp",EDGE,"E1435"),sQuery(id+"F0.wireOp",EDGE,"E1436"),sQuery(id+"F0.wireOp",EDGE,"E1437"),sQuery(id+"F0.wireOp",EDGE,"E1438"),sQuery(id+"F0.wireOp",EDGE,"E1439"),sQuery(id+"F0.wireOp",EDGE,"E1440"),sQuery(id+"F0.wireOp",EDGE,"E1441"),sQuery(id+"F0.wireOp",EDGE,"E1442"),sQuery(id+"F0.wireOp",EDGE,"E1443"),sQuery(id+"F0.wireOp",EDGE,"E1444"),sQuery(id+"F0.wireOp",EDGE,"E1445"),sQuery(id+"F0.wireOp",EDGE,"E1446"),sQuery(id+"F0.wireOp",EDGE,"E1447"),sQuery(id+"F0.wireOp",EDGE,"E1448"),sQuery(id+"F0.wireOp",EDGE,"E1449"),sQuery(id+"F0.wireOp",EDGE,"E1450"),sQuery(id+"F0.wireOp",EDGE,"E1451"),sQuery(id+"F0.wireOp",EDGE,"E1452"),sQuery(id+"F0.wireOp",EDGE,"E1453"),sQuery(id+"F0.wireOp",EDGE,"E1454"),sQuery(id+"F0.wireOp",EDGE,"E1455"),sQuery(id+"F0.wireOp",EDGE,"E1456"),sQuery(id+"F0.wireOp",EDGE,"E1457"),sQuery(id+"F0.wireOp",EDGE,"E1458"),sQuery(id+"F0.wireOp",EDGE,"E1459"),sQuery(id+"F0.wireOp",EDGE,"E1460"),sQuery(id+"F0.wireOp",EDGE,"E1461"),sQuery(id+"F0.wireOp",EDGE,"E1462"),sQuery(id+"F0.wireOp",EDGE,"E1463"),sQuery(id+"F0.wireOp",EDGE,"E1464"),sQuery(id+"F0.wireOp",EDGE,"E1465"),sQuery(id+"F0.wireOp",EDGE,"E1466"),sQuery(id+"F0.wireOp",EDGE,"E1467"),sQuery(id+"F0.wireOp",EDGE,"E1468"),sQuery(id+"F0.wireOp",EDGE,"E1469"),sQuery(id+"F0.wireOp",EDGE,"E1470"),sQuery(id+"F0.wireOp",EDGE,"E1471"),sQuery(id+"F0.wireOp",EDGE,"E1472"),sQuery(id+"F0.wireOp",EDGE,"E1473"),sQuery(id+"F0.wireOp",EDGE,"E1474"),sQuery(id+"F0.wireOp",EDGE,"E1475"),sQuery(id+"F0.wireOp",EDGE,"E1476"),sQuery(id+"F0.wireOp",EDGE,"E1477"),sQuery(id+"F0.wireOp",EDGE,"E1478"),sQuery(id+"F0.wireOp",EDGE,"E1479"),sQuery(id+"F0.wireOp",EDGE,"E1480"),sQuery(id+"F0.wireOp",EDGE,"E1481"),sQuery(id+"F0.wireOp",EDGE,"E1482"),sQuery(id+"F0.wireOp",EDGE,"E1483"),sQuery(id+"F0.wireOp",EDGE,"E1484"),sQuery(id+"F0.wireOp",EDGE,"E1485"),sQuery(id+"F0.wireOp",EDGE,"E1486"),sQuery(id+"F0.wireOp",EDGE,"E1487"),sQuery(id+"F0.wireOp",EDGE,"E1488"),sQuery(id+"F0.wireOp",EDGE,"E1489"),sQuery(id+"F0.wireOp",EDGE,"E1490"),sQuery(id+"F0.wireOp",EDGE,"E1491"),sQuery(id+"F0.wireOp",EDGE,"E1492"),sQuery(id+"F0.wireOp",EDGE,"E1493"),sQuery(id+"F0.wireOp",EDGE,"E1494"),sQuery(id+"F0.wireOp",EDGE,"E1495"),sQuery(id+"F0.wireOp",EDGE,"E1496"),sQuery(id+"F0.wireOp",EDGE,"E1497"),sQuery(id+"F0.wireOp",EDGE,"E1498"),sQuery(id+"F0.wireOp",EDGE,"E1499"),sQuery(id+"F0.wireOp",EDGE,"E1500"),sQuery(id+"F0.wireOp",EDGE,"E1501"),sQuery(id+"F0.wireOp",EDGE,"E1502"),sQuery(id+"F0.wireOp",EDGE,"E1503"),sQuery(id+"F0.wireOp",EDGE,"E1504"),sQuery(id+"F0.wireOp",EDGE,"E1505"),sQuery(id+"F0.wireOp",EDGE,"E1506"),sQuery(id+"F0.wireOp",EDGE,"E1507"),sQuery(id+"F0.wireOp",EDGE,"E1508"),sQuery(id+"F0.wireOp",EDGE,"E1509"),sQuery(id+"F0.wireOp",EDGE,"E1510"),sQuery(id+"F0.wireOp",EDGE,"E1511"),sQuery(id+"F0.wireOp",EDGE,"E1512"),sQuery(id+"F0.wireOp",EDGE,"E1513"),sQuery(id+"F0.wireOp",EDGE,"E1514"),sQuery(id+"F0.wireOp",EDGE,"E1515"),sQuery(id+"F0.wireOp",EDGE,"E1516"),sQuery(id+"F0.wireOp",EDGE,"E1517"),sQuery(id+"F0.wireOp",EDGE,"E1518")])]});
            var Q64;
            Q64=makeQuery(id+"F1.opExtrude","SWEPT_BODY",BODY,{"disambiguationData":[OSD([sQuery(id+"F0.wireOp",EDGE,"E584"),sQuery(id+"F0.wireOp",EDGE,"E585"),sQuery(id+"F0.wireOp",EDGE,"E586"),sQuery(id+"F0.wireOp",EDGE,"E587"),sQuery(id+"F0.wireOp",EDGE,"E588"),sQuery(id+"F0.wireOp",EDGE,"E589"),sQuery(id+"F0.wireOp",EDGE,"E590"),sQuery(id+"F0.wireOp",EDGE,"E591"),sQuery(id+"F0.wireOp",EDGE,"E592"),sQuery(id+"F0.wireOp",EDGE,"E593"),sQuery(id+"F0.wireOp",EDGE,"E594"),sQuery(id+"F0.wireOp",EDGE,"E595"),sQuery(id+"F0.wireOp",EDGE,"E596"),sQuery(id+"F0.wireOp",EDGE,"E597"),sQuery(id+"F0.wireOp",EDGE,"E598"),sQuery(id+"F0.wireOp",EDGE,"E599"),sQuery(id+"F0.wireOp",EDGE,"E600"),sQuery(id+"F0.wireOp",EDGE,"E601"),sQuery(id+"F0.wireOp",EDGE,"E602"),sQuery(id+"F0.wireOp",EDGE,"E603"),sQuery(id+"F0.wireOp",EDGE,"E604"),sQuery(id+"F0.wireOp",EDGE,"E605"),sQuery(id+"F0.wireOp",EDGE,"E606"),sQuery(id+"F0.wireOp",EDGE,"E607"),sQuery(id+"F0.wireOp",EDGE,"E608"),sQuery(id+"F0.wireOp",EDGE,"E609"),sQuery(id+"F0.wireOp",EDGE,"E610"),sQuery(id+"F0.wireOp",EDGE,"E611"),sQuery(id+"F0.wireOp",EDGE,"E612"),sQuery(id+"F0.wireOp",EDGE,"E613"),sQuery(id+"F0.wireOp",EDGE,"E614"),sQuery(id+"F0.wireOp",EDGE,"E615"),sQuery(id+"F0.wireOp",EDGE,"E616"),sQuery(id+"F0.wireOp",EDGE,"E617"),sQuery(id+"F0.wireOp",EDGE,"E618"),sQuery(id+"F0.wireOp",EDGE,"E619"),sQuery(id+"F0.wireOp",EDGE,"E620"),sQuery(id+"F0.wireOp",EDGE,"E621"),sQuery(id+"F0.wireOp",EDGE,"E622"),sQuery(id+"F0.wireOp",EDGE,"E623"),sQuery(id+"F0.wireOp",EDGE,"E624")])]});
            var Q65;
            Q65=makeQuery(id+"F1.opExtrude","SWEPT_BODY",BODY,{"disambiguationData":[OSD([sQuery(id+"F0.wireOp",EDGE,"E871"),sQuery(id+"F0.wireOp",EDGE,"E872"),sQuery(id+"F0.wireOp",EDGE,"E873"),sQuery(id+"F0.wireOp",EDGE,"E874"),sQuery(id+"F0.wireOp",EDGE,"E875"),sQuery(id+"F0.wireOp",EDGE,"E876"),sQuery(id+"F0.wireOp",EDGE,"E877"),sQuery(id+"F0.wireOp",EDGE,"E878"),sQuery(id+"F0.wireOp",EDGE,"E879"),sQuery(id+"F0.wireOp",EDGE,"E880"),sQuery(id+"F0.wireOp",EDGE,"E881"),sQuery(id+"F0.wireOp",EDGE,"E882"),sQuery(id+"F0.wireOp",EDGE,"E883"),sQuery(id+"F0.wireOp",EDGE,"E884"),sQuery(id+"F0.wireOp",EDGE,"E885"),sQuery(id+"F0.wireOp",EDGE,"E886"),sQuery(id+"F0.wireOp",EDGE,"E887"),sQuery(id+"F0.wireOp",EDGE,"E888"),sQuery(id+"F0.wireOp",EDGE,"E889"),sQuery(id+"F0.wireOp",EDGE,"E890"),sQuery(id+"F0.wireOp",EDGE,"E891"),sQuery(id+"F0.wireOp",EDGE,"E892"),sQuery(id+"F0.wireOp",EDGE,"E893"),sQuery(id+"F0.wireOp",EDGE,"E894"),sQuery(id+"F0.wireOp",EDGE,"E895"),sQuery(id+"F0.wireOp",EDGE,"E896"),sQuery(id+"F0.wireOp",EDGE,"E897"),sQuery(id+"F0.wireOp",EDGE,"E898"),sQuery(id+"F0.wireOp",EDGE,"E899"),sQuery(id+"F0.wireOp",EDGE,"E900"),sQuery(id+"F0.wireOp",EDGE,"E901"),sQuery(id+"F0.wireOp",EDGE,"E902"),sQuery(id+"F0.wireOp",EDGE,"E903"),sQuery(id+"F0.wireOp",EDGE,"E904"),sQuery(id+"F0.wireOp",EDGE,"E905"),sQuery(id+"F0.wireOp",EDGE,"E906"),sQuery(id+"F0.wireOp",EDGE,"E907"),sQuery(id+"F0.wireOp",EDGE,"E908"),sQuery(id+"F0.wireOp",EDGE,"E909"),sQuery(id+"F0.wireOp",EDGE,"E910"),sQuery(id+"F0.wireOp",EDGE,"E911"),sQuery(id+"F0.wireOp",EDGE,"E912"),sQuery(id+"F0.wireOp",EDGE,"E913"),sQuery(id+"F0.wireOp",EDGE,"E914"),sQuery(id+"F0.wireOp",EDGE,"E915"),sQuery(id+"F0.wireOp",EDGE,"E916"),sQuery(id+"F0.wireOp",EDGE,"E917"),sQuery(id+"F0.wireOp",EDGE,"E918"),sQuery(id+"F0.wireOp",EDGE,"E919"),sQuery(id+"F0.wireOp",EDGE,"E920"),sQuery(id+"F0.wireOp",EDGE,"E921"),sQuery(id+"F0.wireOp",EDGE,"E922"),sQuery(id+"F0.wireOp",EDGE,"E923"),sQuery(id+"F0.wireOp",EDGE,"E924"),sQuery(id+"F0.wireOp",EDGE,"E925"),sQuery(id+"F0.wireOp",EDGE,"E926"),sQuery(id+"F0.wireOp",EDGE,"E927"),sQuery(id+"F0.wireOp",EDGE,"E928"),sQuery(id+"F0.wireOp",EDGE,"E929"),sQuery(id+"F0.wireOp",EDGE,"E930"),sQuery(id+"F0.wireOp",EDGE,"E931"),sQuery(id+"F0.wireOp",EDGE,"E932"),sQuery(id+"F0.wireOp",EDGE,"E933"),sQuery(id+"F0.wireOp",EDGE,"E934"),sQuery(id+"F0.wireOp",EDGE,"E935"),sQuery(id+"F0.wireOp",EDGE,"E936"),sQuery(id+"F0.wireOp",EDGE,"E937"),sQuery(id+"F0.wireOp",EDGE,"E938"),sQuery(id+"F0.wireOp",EDGE,"E939"),sQuery(id+"F0.wireOp",EDGE,"E940"),sQuery(id+"F0.wireOp",EDGE,"E941"),sQuery(id+"F0.wireOp",EDGE,"E942"),sQuery(id+"F0.wireOp",EDGE,"E943"),sQuery(id+"F0.wireOp",EDGE,"E944"),sQuery(id+"F0.wireOp",EDGE,"E945"),sQuery(id+"F0.wireOp",EDGE,"E946"),sQuery(id+"F0.wireOp",EDGE,"E947"),sQuery(id+"F0.wireOp",EDGE,"E948"),sQuery(id+"F0.wireOp",EDGE,"E949"),sQuery(id+"F0.wireOp",EDGE,"E950"),sQuery(id+"F0.wireOp",EDGE,"E951"),sQuery(id+"F0.wireOp",EDGE,"E952"),sQuery(id+"F0.wireOp",EDGE,"E953"),sQuery(id+"F0.wireOp",EDGE,"E954"),sQuery(id+"F0.wireOp",EDGE,"E955"),sQuery(id+"F0.wireOp",EDGE,"E956"),sQuery(id+"F0.wireOp",EDGE,"E957"),sQuery(id+"F0.wireOp",EDGE,"E958"),sQuery(id+"F0.wireOp",EDGE,"E959"),sQuery(id+"F0.wireOp",EDGE,"E960"),sQuery(id+"F0.wireOp",EDGE,"E961"),sQuery(id+"F0.wireOp",EDGE,"E962"),sQuery(id+"F0.wireOp",EDGE,"E963"),sQuery(id+"F0.wireOp",EDGE,"E964"),sQuery(id+"F0.wireOp",EDGE,"E965"),sQuery(id+"F0.wireOp",EDGE,"E966"),sQuery(id+"F0.wireOp",EDGE,"E967"),sQuery(id+"F0.wireOp",EDGE,"E968"),sQuery(id+"F0.wireOp",EDGE,"E969"),sQuery(id+"F0.wireOp",EDGE,"E970"),sQuery(id+"F0.wireOp",EDGE,"E971"),sQuery(id+"F0.wireOp",EDGE,"E972")])]});
            var Q66;
            Q66=makeQuery(id+"F1.opExtrude","SWEPT_BODY",BODY,{"disambiguationData":[OSD([sQuery(id+"F0.wireOp",EDGE,"E1167"),sQuery(id+"F0.wireOp",EDGE,"E1168"),sQuery(id+"F0.wireOp",EDGE,"E1169"),sQuery(id+"F0.wireOp",EDGE,"E1170"),sQuery(id+"F0.wireOp",EDGE,"E1171"),sQuery(id+"F0.wireOp",EDGE,"E1172"),sQuery(id+"F0.wireOp",EDGE,"E1173"),sQuery(id+"F0.wireOp",EDGE,"E1174"),sQuery(id+"F0.wireOp",EDGE,"E1175"),sQuery(id+"F0.wireOp",EDGE,"E1176"),sQuery(id+"F0.wireOp",EDGE,"E1177"),sQuery(id+"F0.wireOp",EDGE,"E1178"),sQuery(id+"F0.wireOp",EDGE,"E1179"),sQuery(id+"F0.wireOp",EDGE,"E1180"),sQuery(id+"F0.wireOp",EDGE,"E1181"),sQuery(id+"F0.wireOp",EDGE,"E1182")])]});
            var Q67;
            Q67=makeQuery(id+"F1.opExtrude","SWEPT_BODY",BODY,{"disambiguationData":[OSD([sQuery(id+"F0.wireOp",EDGE,"E1343"),sQuery(id+"F0.wireOp",EDGE,"E1344"),sQuery(id+"F0.wireOp",EDGE,"E1345"),sQuery(id+"F0.wireOp",EDGE,"E1346")])]});
            var Q68;
            Q68=makeQuery(id+"F1.opExtrude","SWEPT_BODY",BODY,{"disambiguationData":[OSD([sQuery(id+"F0.wireOp",EDGE,"E542"),sQuery(id+"F0.wireOp",EDGE,"E543"),sQuery(id+"F0.wireOp",EDGE,"E544"),sQuery(id+"F0.wireOp",EDGE,"E545"),sQuery(id+"F0.wireOp",EDGE,"E546"),sQuery(id+"F0.wireOp",EDGE,"E547"),sQuery(id+"F0.wireOp",EDGE,"E548"),sQuery(id+"F0.wireOp",EDGE,"E549"),sQuery(id+"F0.wireOp",EDGE,"E550"),sQuery(id+"F0.wireOp",EDGE,"E551"),sQuery(id+"F0.wireOp",EDGE,"E552"),sQuery(id+"F0.wireOp",EDGE,"E553"),sQuery(id+"F0.wireOp",EDGE,"E554"),sQuery(id+"F0.wireOp",EDGE,"E555"),sQuery(id+"F0.wireOp",EDGE,"E556"),sQuery(id+"F0.wireOp",EDGE,"E557"),sQuery(id+"F0.wireOp",EDGE,"E558"),sQuery(id+"F0.wireOp",EDGE,"E559"),sQuery(id+"F0.wireOp",EDGE,"E560"),sQuery(id+"F0.wireOp",EDGE,"E561"),sQuery(id+"F0.wireOp",EDGE,"E562"),sQuery(id+"F0.wireOp",EDGE,"E563"),sQuery(id+"F0.wireOp",EDGE,"E564"),sQuery(id+"F0.wireOp",EDGE,"E565"),sQuery(id+"F0.wireOp",EDGE,"E566"),sQuery(id+"F0.wireOp",EDGE,"E567"),sQuery(id+"F0.wireOp",EDGE,"E568"),sQuery(id+"F0.wireOp",EDGE,"E569"),sQuery(id+"F0.wireOp",EDGE,"E570"),sQuery(id+"F0.wireOp",EDGE,"E571"),sQuery(id+"F0.wireOp",EDGE,"E572"),sQuery(id+"F0.wireOp",EDGE,"E573"),sQuery(id+"F0.wireOp",EDGE,"E574"),sQuery(id+"F0.wireOp",EDGE,"E575"),sQuery(id+"F0.wireOp",EDGE,"E576"),sQuery(id+"F0.wireOp",EDGE,"E577"),sQuery(id+"F0.wireOp",EDGE,"E578"),sQuery(id+"F0.wireOp",EDGE,"E579"),sQuery(id+"F0.wireOp",EDGE,"E580"),sQuery(id+"F0.wireOp",EDGE,"E581"),sQuery(id+"F0.wireOp",EDGE,"E582"),sQuery(id+"F0.wireOp",EDGE,"E583")])]});
            var Q69;
            Q69=makeQuery(id+"F1.opExtrude","SWEPT_BODY",BODY,{"disambiguationData":[OSD([sQuery(id+"F0.wireOp",EDGE,"E625"),sQuery(id+"F0.wireOp",EDGE,"E626"),sQuery(id+"F0.wireOp",EDGE,"E627"),sQuery(id+"F0.wireOp",EDGE,"E628"),sQuery(id+"F0.wireOp",EDGE,"E629"),sQuery(id+"F0.wireOp",EDGE,"E630"),sQuery(id+"F0.wireOp",EDGE,"E631"),sQuery(id+"F0.wireOp",EDGE,"E632"),sQuery(id+"F0.wireOp",EDGE,"E633"),sQuery(id+"F0.wireOp",EDGE,"E634"),sQuery(id+"F0.wireOp",EDGE,"E635"),sQuery(id+"F0.wireOp",EDGE,"E636"),sQuery(id+"F0.wireOp",EDGE,"E637"),sQuery(id+"F0.wireOp",EDGE,"E638"),sQuery(id+"F0.wireOp",EDGE,"E639"),sQuery(id+"F0.wireOp",EDGE,"E640"),sQuery(id+"F0.wireOp",EDGE,"E641"),sQuery(id+"F0.wireOp",EDGE,"E642"),sQuery(id+"F0.wireOp",EDGE,"E643"),sQuery(id+"F0.wireOp",EDGE,"E644"),sQuery(id+"F0.wireOp",EDGE,"E645"),sQuery(id+"F0.wireOp",EDGE,"E646"),sQuery(id+"F0.wireOp",EDGE,"E647"),sQuery(id+"F0.wireOp",EDGE,"E648"),sQuery(id+"F0.wireOp",EDGE,"E649"),sQuery(id+"F0.wireOp",EDGE,"E650"),sQuery(id+"F0.wireOp",EDGE,"E651"),sQuery(id+"F0.wireOp",EDGE,"E652"),sQuery(id+"F0.wireOp",EDGE,"E653"),sQuery(id+"F0.wireOp",EDGE,"E654"),sQuery(id+"F0.wireOp",EDGE,"E655"),sQuery(id+"F0.wireOp",EDGE,"E656"),sQuery(id+"F0.wireOp",EDGE,"E657"),sQuery(id+"F0.wireOp",EDGE,"E658"),sQuery(id+"F0.wireOp",EDGE,"E659"),sQuery(id+"F0.wireOp",EDGE,"E660"),sQuery(id+"F0.wireOp",EDGE,"E661"),sQuery(id+"F0.wireOp",EDGE,"E662"),sQuery(id+"F0.wireOp",EDGE,"E663"),sQuery(id+"F0.wireOp",EDGE,"E664"),sQuery(id+"F0.wireOp",EDGE,"E665")])]});
            var Q70;
            Q70=makeQuery(id+"F1.opExtrude","SWEPT_BODY",BODY,{"disambiguationData":[OSD([sQuery(id+"F0.wireOp",EDGE,"E777"),sQuery(id+"F0.wireOp",EDGE,"E778"),sQuery(id+"F0.wireOp",EDGE,"E779"),sQuery(id+"F0.wireOp",EDGE,"E780"),sQuery(id+"F0.wireOp",EDGE,"E781"),sQuery(id+"F0.wireOp",EDGE,"E782"),sQuery(id+"F0.wireOp",EDGE,"E783"),sQuery(id+"F0.wireOp",EDGE,"E784"),sQuery(id+"F0.wireOp",EDGE,"E785"),sQuery(id+"F0.wireOp",EDGE,"E786"),sQuery(id+"F0.wireOp",EDGE,"E787"),sQuery(id+"F0.wireOp",EDGE,"E788"),sQuery(id+"F0.wireOp",EDGE,"E789"),sQuery(id+"F0.wireOp",EDGE,"E790"),sQuery(id+"F0.wireOp",EDGE,"E791"),sQuery(id+"F0.wireOp",EDGE,"E792"),sQuery(id+"F0.wireOp",EDGE,"E793"),sQuery(id+"F0.wireOp",EDGE,"E794"),sQuery(id+"F0.wireOp",EDGE,"E795"),sQuery(id+"F0.wireOp",EDGE,"E796"),sQuery(id+"F0.wireOp",EDGE,"E797"),sQuery(id+"F0.wireOp",EDGE,"E798"),sQuery(id+"F0.wireOp",EDGE,"E799"),sQuery(id+"F0.wireOp",EDGE,"E800"),sQuery(id+"F0.wireOp",EDGE,"E801"),sQuery(id+"F0.wireOp",EDGE,"E802"),sQuery(id+"F0.wireOp",EDGE,"E803"),sQuery(id+"F0.wireOp",EDGE,"E804"),sQuery(id+"F0.wireOp",EDGE,"E805"),sQuery(id+"F0.wireOp",EDGE,"E806"),sQuery(id+"F0.wireOp",EDGE,"E807"),sQuery(id+"F0.wireOp",EDGE,"E808"),sQuery(id+"F0.wireOp",EDGE,"E809"),sQuery(id+"F0.wireOp",EDGE,"E810"),sQuery(id+"F0.wireOp",EDGE,"E811"),sQuery(id+"F0.wireOp",EDGE,"E812"),sQuery(id+"F0.wireOp",EDGE,"E813"),sQuery(id+"F0.wireOp",EDGE,"E814"),sQuery(id+"F0.wireOp",EDGE,"E815"),sQuery(id+"F0.wireOp",EDGE,"E816"),sQuery(id+"F0.wireOp",EDGE,"E817"),sQuery(id+"F0.wireOp",EDGE,"E818"),sQuery(id+"F0.wireOp",EDGE,"E819"),sQuery(id+"F0.wireOp",EDGE,"E820"),sQuery(id+"F0.wireOp",EDGE,"E821"),sQuery(id+"F0.wireOp",EDGE,"E822"),sQuery(id+"F0.wireOp",EDGE,"E823"),sQuery(id+"F0.wireOp",EDGE,"E824"),sQuery(id+"F0.wireOp",EDGE,"E825"),sQuery(id+"F0.wireOp",EDGE,"E826"),sQuery(id+"F0.wireOp",EDGE,"E827"),sQuery(id+"F0.wireOp",EDGE,"E828"),sQuery(id+"F0.wireOp",EDGE,"E829"),sQuery(id+"F0.wireOp",EDGE,"E830"),sQuery(id+"F0.wireOp",EDGE,"E831"),sQuery(id+"F0.wireOp",EDGE,"E832"),sQuery(id+"F0.wireOp",EDGE,"E833"),sQuery(id+"F0.wireOp",EDGE,"E834"),sQuery(id+"F0.wireOp",EDGE,"E835"),sQuery(id+"F0.wireOp",EDGE,"E836"),sQuery(id+"F0.wireOp",EDGE,"E837"),sQuery(id+"F0.wireOp",EDGE,"E838"),sQuery(id+"F0.wireOp",EDGE,"E839"),sQuery(id+"F0.wireOp",EDGE,"E840"),sQuery(id+"F0.wireOp",EDGE,"E841"),sQuery(id+"F0.wireOp",EDGE,"E842"),sQuery(id+"F0.wireOp",EDGE,"E843"),sQuery(id+"F0.wireOp",EDGE,"E844"),sQuery(id+"F0.wireOp",EDGE,"E845"),sQuery(id+"F0.wireOp",EDGE,"E846"),sQuery(id+"F0.wireOp",EDGE,"E847"),sQuery(id+"F0.wireOp",EDGE,"E848"),sQuery(id+"F0.wireOp",EDGE,"E849"),sQuery(id+"F0.wireOp",EDGE,"E850"),sQuery(id+"F0.wireOp",EDGE,"E851"),sQuery(id+"F0.wireOp",EDGE,"E852"),sQuery(id+"F0.wireOp",EDGE,"E853"),sQuery(id+"F0.wireOp",EDGE,"E854")])]});
            var Q71;
            Q71=makeQuery(id+"F1.opExtrude","SWEPT_BODY",BODY,{"disambiguationData":[OSD([sQuery(id+"F0.wireOp",EDGE,"E753"),sQuery(id+"F0.wireOp",EDGE,"E754"),sQuery(id+"F0.wireOp",EDGE,"E755"),sQuery(id+"F0.wireOp",EDGE,"E756"),sQuery(id+"F0.wireOp",EDGE,"E757"),sQuery(id+"F0.wireOp",EDGE,"E758"),sQuery(id+"F0.wireOp",EDGE,"E759"),sQuery(id+"F0.wireOp",EDGE,"E760"),sQuery(id+"F0.wireOp",EDGE,"E761"),sQuery(id+"F0.wireOp",EDGE,"E762"),sQuery(id+"F0.wireOp",EDGE,"E763"),sQuery(id+"F0.wireOp",EDGE,"E764")])]});
            var Q72;
            Q72=makeQuery(id+"F1.opExtrude","SWEPT_BODY",BODY,{"disambiguationData":[OSD([sQuery(id+"F0.wireOp",EDGE,"E1308"),sQuery(id+"F0.wireOp",EDGE,"E1309"),sQuery(id+"F0.wireOp",EDGE,"E1310"),sQuery(id+"F0.wireOp",EDGE,"E1311"),sQuery(id+"F0.wireOp",EDGE,"E1312"),sQuery(id+"F0.wireOp",EDGE,"E1313"),sQuery(id+"F0.wireOp",EDGE,"E1314"),sQuery(id+"F0.wireOp",EDGE,"E1315"),sQuery(id+"F0.wireOp",EDGE,"E1316"),sQuery(id+"F0.wireOp",EDGE,"E1317"),sQuery(id+"F0.wireOp",EDGE,"E1318")])]});
            var Q73;
            Q73=makeQuery(id+"F1.opExtrude","SWEPT_BODY",BODY,{"disambiguationData":[OSD([sQuery(id+"F0.wireOp",EDGE,"E666"),sQuery(id+"F0.wireOp",EDGE,"E667"),sQuery(id+"F0.wireOp",EDGE,"E668"),sQuery(id+"F0.wireOp",EDGE,"E669")])]});
            var Q74;
            Q74=makeQuery(id+"F1.opExtrude","SWEPT_BODY",BODY,{"disambiguationData":[OSD([sQuery(id+"F0.wireOp",EDGE,"E442"),sQuery(id+"F0.wireOp",EDGE,"E443"),sQuery(id+"F0.wireOp",EDGE,"E444"),sQuery(id+"F0.wireOp",EDGE,"E445"),sQuery(id+"F0.wireOp",EDGE,"E446"),sQuery(id+"F0.wireOp",EDGE,"E447"),sQuery(id+"F0.wireOp",EDGE,"E448"),sQuery(id+"F0.wireOp",EDGE,"E449"),sQuery(id+"F0.wireOp",EDGE,"E450"),sQuery(id+"F0.wireOp",EDGE,"E451"),sQuery(id+"F0.wireOp",EDGE,"E452"),sQuery(id+"F0.wireOp",EDGE,"E453"),sQuery(id+"F0.wireOp",EDGE,"E454"),sQuery(id+"F0.wireOp",EDGE,"E455"),sQuery(id+"F0.wireOp",EDGE,"E456"),sQuery(id+"F0.wireOp",EDGE,"E457"),sQuery(id+"F0.wireOp",EDGE,"E458"),sQuery(id+"F0.wireOp",EDGE,"E459"),sQuery(id+"F0.wireOp",EDGE,"E460"),sQuery(id+"F0.wireOp",EDGE,"E461"),sQuery(id+"F0.wireOp",EDGE,"E462"),sQuery(id+"F0.wireOp",EDGE,"E463"),sQuery(id+"F0.wireOp",EDGE,"E464"),sQuery(id+"F0.wireOp",EDGE,"E465"),sQuery(id+"F0.wireOp",EDGE,"E466"),sQuery(id+"F0.wireOp",EDGE,"E467"),sQuery(id+"F0.wireOp",EDGE,"E468"),sQuery(id+"F0.wireOp",EDGE,"E469"),sQuery(id+"F0.wireOp",EDGE,"E470"),sQuery(id+"F0.wireOp",EDGE,"E471"),sQuery(id+"F0.wireOp",EDGE,"E472"),sQuery(id+"F0.wireOp",EDGE,"E473"),sQuery(id+"F0.wireOp",EDGE,"E474"),sQuery(id+"F0.wireOp",EDGE,"E475"),sQuery(id+"F0.wireOp",EDGE,"E476"),sQuery(id+"F0.wireOp",EDGE,"E477"),sQuery(id+"F0.wireOp",EDGE,"E478"),sQuery(id+"F0.wireOp",EDGE,"E479"),sQuery(id+"F0.wireOp",EDGE,"E480"),sQuery(id+"F0.wireOp",EDGE,"E481"),sQuery(id+"F0.wireOp",EDGE,"E482"),sQuery(id+"F0.wireOp",EDGE,"E483"),sQuery(id+"F0.wireOp",EDGE,"E484"),sQuery(id+"F0.wireOp",EDGE,"E485"),sQuery(id+"F0.wireOp",EDGE,"E486"),sQuery(id+"F0.wireOp",EDGE,"E487"),sQuery(id+"F0.wireOp",EDGE,"E488"),sQuery(id+"F0.wireOp",EDGE,"E489"),sQuery(id+"F0.wireOp",EDGE,"E490"),sQuery(id+"F0.wireOp",EDGE,"E491"),sQuery(id+"F0.wireOp",EDGE,"E492"),sQuery(id+"F0.wireOp",EDGE,"E493"),sQuery(id+"F0.wireOp",EDGE,"E494"),sQuery(id+"F0.wireOp",EDGE,"E495"),sQuery(id+"F0.wireOp",EDGE,"E496"),sQuery(id+"F0.wireOp",EDGE,"E497"),sQuery(id+"F0.wireOp",EDGE,"E498"),sQuery(id+"F0.wireOp",EDGE,"E499"),sQuery(id+"F0.wireOp",EDGE,"E500"),sQuery(id+"F0.wireOp",EDGE,"E501"),sQuery(id+"F0.wireOp",EDGE,"E502"),sQuery(id+"F0.wireOp",EDGE,"E503"),sQuery(id+"F0.wireOp",EDGE,"E504"),sQuery(id+"F0.wireOp",EDGE,"E505"),sQuery(id+"F0.wireOp",EDGE,"E506"),sQuery(id+"F0.wireOp",EDGE,"E507"),sQuery(id+"F0.wireOp",EDGE,"E508"),sQuery(id+"F0.wireOp",EDGE,"E509"),sQuery(id+"F0.wireOp",EDGE,"E510"),sQuery(id+"F0.wireOp",EDGE,"E511"),sQuery(id+"F0.wireOp",EDGE,"E512"),sQuery(id+"F0.wireOp",EDGE,"E513"),sQuery(id+"F0.wireOp",EDGE,"E514"),sQuery(id+"F0.wireOp",EDGE,"E515"),sQuery(id+"F0.wireOp",EDGE,"E516"),sQuery(id+"F0.wireOp",EDGE,"E517"),sQuery(id+"F0.wireOp",EDGE,"E518"),sQuery(id+"F0.wireOp",EDGE,"E519"),sQuery(id+"F0.wireOp",EDGE,"E520"),sQuery(id+"F0.wireOp",EDGE,"E521"),sQuery(id+"F0.wireOp",EDGE,"E522"),sQuery(id+"F0.wireOp",EDGE,"E523"),sQuery(id+"F0.wireOp",EDGE,"E524"),sQuery(id+"F0.wireOp",EDGE,"E525"),sQuery(id+"F0.wireOp",EDGE,"E526"),sQuery(id+"F0.wireOp",EDGE,"E527"),sQuery(id+"F0.wireOp",EDGE,"E528"),sQuery(id+"F0.wireOp",EDGE,"E529"),sQuery(id+"F0.wireOp",EDGE,"E530"),sQuery(id+"F0.wireOp",EDGE,"E531"),sQuery(id+"F0.wireOp",EDGE,"E532"),sQuery(id+"F0.wireOp",EDGE,"E533"),sQuery(id+"F0.wireOp",EDGE,"E534"),sQuery(id+"F0.wireOp",EDGE,"E535"),sQuery(id+"F0.wireOp",EDGE,"E536"),sQuery(id+"F0.wireOp",EDGE,"E537")])]});
            var Q75;
            Q75=makeQuery(id+"F1.opExtrude","SWEPT_BODY",BODY,{"disambiguationData":[OSD([sQuery(id+"F0.wireOp",EDGE,"E717"),sQuery(id+"F0.wireOp",EDGE,"E718"),sQuery(id+"F0.wireOp",EDGE,"E719"),sQuery(id+"F0.wireOp",EDGE,"E720"),sQuery(id+"F0.wireOp",EDGE,"E721"),sQuery(id+"F0.wireOp",EDGE,"E722"),sQuery(id+"F0.wireOp",EDGE,"E723"),sQuery(id+"F0.wireOp",EDGE,"E724"),sQuery(id+"F0.wireOp",EDGE,"E725"),sQuery(id+"F0.wireOp",EDGE,"E726"),sQuery(id+"F0.wireOp",EDGE,"E727"),sQuery(id+"F0.wireOp",EDGE,"E728")])]});
            var Q76;
            Q76=makeQuery(id+"F1.opExtrude","SWEPT_BODY",BODY,{"disambiguationData":[OSD([sQuery(id+"F0.wireOp",EDGE,"E1093"),sQuery(id+"F0.wireOp",EDGE,"E1094"),sQuery(id+"F0.wireOp",EDGE,"E1095"),sQuery(id+"F0.wireOp",EDGE,"E1096"),sQuery(id+"F0.wireOp",EDGE,"E1097"),sQuery(id+"F0.wireOp",EDGE,"E1098"),sQuery(id+"F0.wireOp",EDGE,"E1099"),sQuery(id+"F0.wireOp",EDGE,"E1100"),sQuery(id+"F0.wireOp",EDGE,"E1101"),sQuery(id+"F0.wireOp",EDGE,"E1102"),sQuery(id+"F0.wireOp",EDGE,"E1103"),sQuery(id+"F0.wireOp",EDGE,"E1104"),sQuery(id+"F0.wireOp",EDGE,"E1105"),sQuery(id+"F0.wireOp",EDGE,"E1106"),sQuery(id+"F0.wireOp",EDGE,"E1107"),sQuery(id+"F0.wireOp",EDGE,"E1108"),sQuery(id+"F0.wireOp",EDGE,"E1109"),sQuery(id+"F0.wireOp",EDGE,"E1110"),sQuery(id+"F0.wireOp",EDGE,"E1111"),sQuery(id+"F0.wireOp",EDGE,"E1112"),sQuery(id+"F0.wireOp",EDGE,"E1113"),sQuery(id+"F0.wireOp",EDGE,"E1114"),sQuery(id+"F0.wireOp",EDGE,"E1115"),sQuery(id+"F0.wireOp",EDGE,"E1116"),sQuery(id+"F0.wireOp",EDGE,"E1117"),sQuery(id+"F0.wireOp",EDGE,"E1118"),sQuery(id+"F0.wireOp",EDGE,"E1119"),sQuery(id+"F0.wireOp",EDGE,"E1120"),sQuery(id+"F0.wireOp",EDGE,"E1121"),sQuery(id+"F0.wireOp",EDGE,"E1122"),sQuery(id+"F0.wireOp",EDGE,"E1123"),sQuery(id+"F0.wireOp",EDGE,"E1124"),sQuery(id+"F0.wireOp",EDGE,"E1125"),sQuery(id+"F0.wireOp",EDGE,"E1126"),sQuery(id+"F0.wireOp",EDGE,"E1127"),sQuery(id+"F0.wireOp",EDGE,"E1128"),sQuery(id+"F0.wireOp",EDGE,"E1129"),sQuery(id+"F0.wireOp",EDGE,"E1130"),sQuery(id+"F0.wireOp",EDGE,"E1131"),sQuery(id+"F0.wireOp",EDGE,"E1132"),sQuery(id+"F0.wireOp",EDGE,"E1133"),sQuery(id+"F0.wireOp",EDGE,"E1134"),sQuery(id+"F0.wireOp",EDGE,"E1135"),sQuery(id+"F0.wireOp",EDGE,"E1136"),sQuery(id+"F0.wireOp",EDGE,"E1137"),sQuery(id+"F0.wireOp",EDGE,"E1138"),sQuery(id+"F0.wireOp",EDGE,"E1139"),sQuery(id+"F0.wireOp",EDGE,"E1140"),sQuery(id+"F0.wireOp",EDGE,"E1141"),sQuery(id+"F0.wireOp",EDGE,"E1142"),sQuery(id+"F0.wireOp",EDGE,"E1143"),sQuery(id+"F0.wireOp",EDGE,"E1144"),sQuery(id+"F0.wireOp",EDGE,"E1145"),sQuery(id+"F0.wireOp",EDGE,"E1146"),sQuery(id+"F0.wireOp",EDGE,"E1147"),sQuery(id+"F0.wireOp",EDGE,"E1148"),sQuery(id+"F0.wireOp",EDGE,"E1149"),sQuery(id+"F0.wireOp",EDGE,"E1150"),sQuery(id+"F0.wireOp",EDGE,"E1151"),sQuery(id+"F0.wireOp",EDGE,"E1152"),sQuery(id+"F0.wireOp",EDGE,"E1153"),sQuery(id+"F0.wireOp",EDGE,"E1154"),sQuery(id+"F0.wireOp",EDGE,"E1155"),sQuery(id+"F0.wireOp",EDGE,"E1156"),sQuery(id+"F0.wireOp",EDGE,"E1157"),sQuery(id+"F0.wireOp",EDGE,"E1158"),sQuery(id+"F0.wireOp",EDGE,"E1159"),sQuery(id+"F0.wireOp",EDGE,"E1160"),sQuery(id+"F0.wireOp",EDGE,"E1161"),sQuery(id+"F0.wireOp",EDGE,"E1162"),sQuery(id+"F0.wireOp",EDGE,"E1163"),sQuery(id+"F0.wireOp",EDGE,"E1164"),sQuery(id+"F0.wireOp",EDGE,"E1165"),sQuery(id+"F0.wireOp",EDGE,"E1166")])]});
            var Q77;
            Q77=makeQuery(id+"F1.opExtrude","SWEPT_BODY",BODY,{"disambiguationData":[OSD([sQuery(id+"F0.wireOp",EDGE,"E1087"),sQuery(id+"F0.wireOp",EDGE,"E1088"),sQuery(id+"F0.wireOp",EDGE,"E1089"),sQuery(id+"F0.wireOp",EDGE,"E1090"),sQuery(id+"F0.wireOp",EDGE,"E1091"),sQuery(id+"F0.wireOp",EDGE,"E1092")])]});
            booleanBodies(context, id + "F4", {"operationType" : BooleanOperationType.UNION, "tools" : qUnion([Q0, Q1, Q2, Q3, Q4, Q5, Q6, Q7, Q8, Q9, Q10, Q11, Q12, Q13, Q14, Q15, Q16, Q17, Q18, Q19, Q20, Q21, Q22, Q23, Q24, Q25, Q26, Q27, Q28, Q29, Q30, Q31, Q32, Q33, Q34, Q35, Q36, Q37, Q38, Q39, Q40, Q41, Q42, Q43, Q44, Q45, Q46, Q47, Q48, Q49, Q50, Q51, Q52, Q53, Q54, Q55, Q56, Q57, Q58, Q59, Q60, Q61, Q62, Q63, Q64, Q65, Q66, Q67, Q68, Q69, Q70, Q71, Q72, Q73, Q74, Q75, Q76, Q77])});
        }
        {
            var Q0;
            Q0=makeQuery(id+"F1.opExtrude","SWEPT_BODY",BODY,{"disambiguationData":[OSD([sQuery(id+"F0.wireOp",EDGE,"E2618"),sQuery(id+"F0.wireOp",EDGE,"E2619"),sQuery(id+"F0.wireOp",EDGE,"E2620"),sQuery(id+"F0.wireOp",EDGE,"E2621"),sQuery(id+"F0.wireOp",EDGE,"E2622"),sQuery(id+"F0.wireOp",EDGE,"E2623"),sQuery(id+"F0.wireOp",EDGE,"E2624"),sQuery(id+"F0.wireOp",EDGE,"E2625"),sQuery(id+"F0.wireOp",EDGE,"E2626"),sQuery(id+"F0.wireOp",EDGE,"E2627"),sQuery(id+"F0.wireOp",EDGE,"E2628"),sQuery(id+"F0.wireOp",EDGE,"E2629"),sQuery(id+"F0.wireOp",EDGE,"E2630"),sQuery(id+"F0.wireOp",EDGE,"E2631"),sQuery(id+"F0.wireOp",EDGE,"E2632"),sQuery(id+"F0.wireOp",EDGE,"E2633"),sQuery(id+"F0.wireOp",EDGE,"E2634"),sQuery(id+"F0.wireOp",EDGE,"E2635"),sQuery(id+"F0.wireOp",EDGE,"E2636"),sQuery(id+"F0.wireOp",EDGE,"E2637"),sQuery(id+"F0.wireOp",EDGE,"E2638"),sQuery(id+"F0.wireOp",EDGE,"E2639"),sQuery(id+"F0.wireOp",EDGE,"E2640"),sQuery(id+"F0.wireOp",EDGE,"E2641"),sQuery(id+"F0.wireOp",EDGE,"E2642"),sQuery(id+"F0.wireOp",EDGE,"E2643"),sQuery(id+"F0.wireOp",EDGE,"E2644"),sQuery(id+"F0.wireOp",EDGE,"E2645"),sQuery(id+"F0.wireOp",EDGE,"E2646"),sQuery(id+"F0.wireOp",EDGE,"E2647"),sQuery(id+"F0.wireOp",EDGE,"E2648"),sQuery(id+"F0.wireOp",EDGE,"E2649"),sQuery(id+"F0.wireOp",EDGE,"E2650"),sQuery(id+"F0.wireOp",EDGE,"E2651"),sQuery(id+"F0.wireOp",EDGE,"E2652"),sQuery(id+"F0.wireOp",EDGE,"E2653"),sQuery(id+"F0.wireOp",EDGE,"E2654"),sQuery(id+"F0.wireOp",EDGE,"E2655"),sQuery(id+"F0.wireOp",EDGE,"E2656"),sQuery(id+"F0.wireOp",EDGE,"E2657"),sQuery(id+"F0.wireOp",EDGE,"E2658"),sQuery(id+"F0.wireOp",EDGE,"E2659"),sQuery(id+"F0.wireOp",EDGE,"E2660"),sQuery(id+"F0.wireOp",EDGE,"E2661"),sQuery(id+"F0.wireOp",EDGE,"E2662"),sQuery(id+"F0.wireOp",EDGE,"E2663"),sQuery(id+"F0.wireOp",EDGE,"E2664"),sQuery(id+"F0.wireOp",EDGE,"E2665"),sQuery(id+"F0.wireOp",EDGE,"E2666"),sQuery(id+"F0.wireOp",EDGE,"E2667"),sQuery(id+"F0.wireOp",EDGE,"E2668"),sQuery(id+"F0.wireOp",EDGE,"E2669"),sQuery(id+"F0.wireOp",EDGE,"E2670"),sQuery(id+"F0.wireOp",EDGE,"E2671"),sQuery(id+"F0.wireOp",EDGE,"E2672"),sQuery(id+"F0.wireOp",EDGE,"E2673"),sQuery(id+"F0.wireOp",EDGE,"E2674"),sQuery(id+"F0.wireOp",EDGE,"E2675"),sQuery(id+"F0.wireOp",EDGE,"E2676"),sQuery(id+"F0.wireOp",EDGE,"E2677"),sQuery(id+"F0.wireOp",EDGE,"E2678"),sQuery(id+"F0.wireOp",EDGE,"E2679"),sQuery(id+"F0.wireOp",EDGE,"E2680"),sQuery(id+"F0.wireOp",EDGE,"E2681"),sQuery(id+"F0.wireOp",EDGE,"E2682"),sQuery(id+"F0.wireOp",EDGE,"E2683"),sQuery(id+"F0.wireOp",EDGE,"E2684"),sQuery(id+"F0.wireOp",EDGE,"E2685"),sQuery(id+"F0.wireOp",EDGE,"E2686"),sQuery(id+"F0.wireOp",EDGE,"E2687"),sQuery(id+"F0.wireOp",EDGE,"E2688"),sQuery(id+"F0.wireOp",EDGE,"E2689"),sQuery(id+"F0.wireOp",EDGE,"E2690"),sQuery(id+"F0.wireOp",EDGE,"E2691"),sQuery(id+"F0.wireOp",EDGE,"E2692"),sQuery(id+"F0.wireOp",EDGE,"E2693"),sQuery(id+"F0.wireOp",EDGE,"E2694"),sQuery(id+"F0.wireOp",EDGE,"E2695"),sQuery(id+"F0.wireOp",EDGE,"E2696"),sQuery(id+"F0.wireOp",EDGE,"E2697"),sQuery(id+"F0.wireOp",EDGE,"E2698"),sQuery(id+"F0.wireOp",EDGE,"E2699"),sQuery(id+"F0.wireOp",EDGE,"E2700"),sQuery(id+"F0.wireOp",EDGE,"E2701"),sQuery(id+"F0.wireOp",EDGE,"E2702"),sQuery(id+"F0.wireOp",EDGE,"E2703"),sQuery(id+"F0.wireOp",EDGE,"E2704"),sQuery(id+"F0.wireOp",EDGE,"E2705"),sQuery(id+"F0.wireOp",EDGE,"E2706"),sQuery(id+"F0.wireOp",EDGE,"E2707"),sQuery(id+"F0.wireOp",EDGE,"E2708"),sQuery(id+"F0.wireOp",EDGE,"E2709"),sQuery(id+"F0.wireOp",EDGE,"E2710"),sQuery(id+"F0.wireOp",EDGE,"E2711"),sQuery(id+"F0.wireOp",EDGE,"E2712"),sQuery(id+"F0.wireOp",EDGE,"E2713"),sQuery(id+"F0.wireOp",EDGE,"E2714"),sQuery(id+"F0.wireOp",EDGE,"E2715"),sQuery(id+"F0.wireOp",EDGE,"E2716"),sQuery(id+"F0.wireOp",EDGE,"E2717"),sQuery(id+"F0.wireOp",EDGE,"E2718"),sQuery(id+"F0.wireOp",EDGE,"E2719"),sQuery(id+"F0.wireOp",EDGE,"E2720"),sQuery(id+"F0.wireOp",EDGE,"E2721"),sQuery(id+"F0.wireOp",EDGE,"E2722"),sQuery(id+"F0.wireOp",EDGE,"E2723"),sQuery(id+"F0.wireOp",EDGE,"E2724"),sQuery(id+"F0.wireOp",EDGE,"E2725"),sQuery(id+"F0.wireOp",EDGE,"E2726"),sQuery(id+"F0.wireOp",EDGE,"E2727"),sQuery(id+"F0.wireOp",EDGE,"E2728"),sQuery(id+"F0.wireOp",EDGE,"E2729"),sQuery(id+"F0.wireOp",EDGE,"E2730"),sQuery(id+"F0.wireOp",EDGE,"E2731"),sQuery(id+"F0.wireOp",EDGE,"E2732"),sQuery(id+"F0.wireOp",EDGE,"E2733"),sQuery(id+"F0.wireOp",EDGE,"E2734"),sQuery(id+"F0.wireOp",EDGE,"E2735"),sQuery(id+"F0.wireOp",EDGE,"E2736"),sQuery(id+"F0.wireOp",EDGE,"E2737"),sQuery(id+"F0.wireOp",EDGE,"E2738"),sQuery(id+"F0.wireOp",EDGE,"E2739"),sQuery(id+"F0.wireOp",EDGE,"E2740"),sQuery(id+"F0.wireOp",EDGE,"E2741"),sQuery(id+"F0.wireOp",EDGE,"E2742"),sQuery(id+"F0.wireOp",EDGE,"E2743"),sQuery(id+"F0.wireOp",EDGE,"E2744"),sQuery(id+"F0.wireOp",EDGE,"E2745"),sQuery(id+"F0.wireOp",EDGE,"E2746"),sQuery(id+"F0.wireOp",EDGE,"E2747"),sQuery(id+"F0.wireOp",EDGE,"E2748"),sQuery(id+"F0.wireOp",EDGE,"E2749"),sQuery(id+"F0.wireOp",EDGE,"E2750"),sQuery(id+"F0.wireOp",EDGE,"E2751"),sQuery(id+"F0.wireOp",EDGE,"E2752"),sQuery(id+"F0.wireOp",EDGE,"E2753"),sQuery(id+"F0.wireOp",EDGE,"E2754"),sQuery(id+"F0.wireOp",EDGE,"E2755"),sQuery(id+"F0.wireOp",EDGE,"E2756"),sQuery(id+"F0.wireOp",EDGE,"E2757"),sQuery(id+"F0.wireOp",EDGE,"E2758"),sQuery(id+"F0.wireOp",EDGE,"E2759"),sQuery(id+"F0.wireOp",EDGE,"E2760"),sQuery(id+"F0.wireOp",EDGE,"E2761"),sQuery(id+"F0.wireOp",EDGE,"E2762"),sQuery(id+"F0.wireOp",EDGE,"E2763"),sQuery(id+"F0.wireOp",EDGE,"E2764"),sQuery(id+"F0.wireOp",EDGE,"E2765"),sQuery(id+"F0.wireOp",EDGE,"E2766"),sQuery(id+"F0.wireOp",EDGE,"E2767"),sQuery(id+"F0.wireOp",EDGE,"E2768"),sQuery(id+"F0.wireOp",EDGE,"E2769"),sQuery(id+"F0.wireOp",EDGE,"E2770"),sQuery(id+"F0.wireOp",EDGE,"E2771"),sQuery(id+"F0.wireOp",EDGE,"E2772"),sQuery(id+"F0.wireOp",EDGE,"E2773"),sQuery(id+"F0.wireOp",EDGE,"E2774"),sQuery(id+"F0.wireOp",EDGE,"E2775"),sQuery(id+"F0.wireOp",EDGE,"E2776"),sQuery(id+"F0.wireOp",EDGE,"E2777"),sQuery(id+"F0.wireOp",EDGE,"E2778"),sQuery(id+"F0.wireOp",EDGE,"E2779"),sQuery(id+"F0.wireOp",EDGE,"E2780"),sQuery(id+"F0.wireOp",EDGE,"E2781"),sQuery(id+"F0.wireOp",EDGE,"E2782"),sQuery(id+"F0.wireOp",EDGE,"E2783"),sQuery(id+"F0.wireOp",EDGE,"E2784"),sQuery(id+"F0.wireOp",EDGE,"E2785")])]});
            var Q1;
            Q1=makeQuery(id+"F1.opExtrude","SWEPT_BODY",BODY,{"disambiguationData":[OSD([sQuery(id+"F0.wireOp",EDGE,"E321"),sQuery(id+"F0.wireOp",EDGE,"E322"),sQuery(id+"F0.wireOp",EDGE,"E323"),sQuery(id+"F0.wireOp",EDGE,"E324"),sQuery(id+"F0.wireOp",EDGE,"E325"),sQuery(id+"F0.wireOp",EDGE,"E326"),sQuery(id+"F0.wireOp",EDGE,"E327"),sQuery(id+"F0.wireOp",EDGE,"E328"),sQuery(id+"F0.wireOp",EDGE,"E329"),sQuery(id+"F0.wireOp",EDGE,"E330"),sQuery(id+"F0.wireOp",EDGE,"E331"),sQuery(id+"F0.wireOp",EDGE,"E332"),sQuery(id+"F0.wireOp",EDGE,"E333"),sQuery(id+"F0.wireOp",EDGE,"E334"),sQuery(id+"F0.wireOp",EDGE,"E335"),sQuery(id+"F0.wireOp",EDGE,"E336"),sQuery(id+"F0.wireOp",EDGE,"E337"),sQuery(id+"F0.wireOp",EDGE,"E338"),sQuery(id+"F0.wireOp",EDGE,"E339"),sQuery(id+"F0.wireOp",EDGE,"E340"),sQuery(id+"F0.wireOp",EDGE,"E341"),sQuery(id+"F0.wireOp",EDGE,"E342"),sQuery(id+"F0.wireOp",EDGE,"E343"),sQuery(id+"F0.wireOp",EDGE,"E344"),sQuery(id+"F0.wireOp",EDGE,"E345"),sQuery(id+"F0.wireOp",EDGE,"E346"),sQuery(id+"F0.wireOp",EDGE,"E347"),sQuery(id+"F0.wireOp",EDGE,"E348"),sQuery(id+"F0.wireOp",EDGE,"E349"),sQuery(id+"F0.wireOp",EDGE,"E350"),sQuery(id+"F0.wireOp",EDGE,"E351"),sQuery(id+"F0.wireOp",EDGE,"E352"),sQuery(id+"F0.wireOp",EDGE,"E353"),sQuery(id+"F0.wireOp",EDGE,"E354"),sQuery(id+"F0.wireOp",EDGE,"E355"),sQuery(id+"F0.wireOp",EDGE,"E356"),sQuery(id+"F0.wireOp",EDGE,"E357"),sQuery(id+"F0.wireOp",EDGE,"E358"),sQuery(id+"F0.wireOp",EDGE,"E359"),sQuery(id+"F0.wireOp",EDGE,"E360"),sQuery(id+"F0.wireOp",EDGE,"E361"),sQuery(id+"F0.wireOp",EDGE,"E362"),sQuery(id+"F0.wireOp",EDGE,"E363"),sQuery(id+"F0.wireOp",EDGE,"E364"),sQuery(id+"F0.wireOp",EDGE,"E365"),sQuery(id+"F0.wireOp",EDGE,"E366"),sQuery(id+"F0.wireOp",EDGE,"E367"),sQuery(id+"F0.wireOp",EDGE,"E368"),sQuery(id+"F0.wireOp",EDGE,"E369"),sQuery(id+"F0.wireOp",EDGE,"E370"),sQuery(id+"F0.wireOp",EDGE,"E371"),sQuery(id+"F0.wireOp",EDGE,"E372"),sQuery(id+"F0.wireOp",EDGE,"E373"),sQuery(id+"F0.wireOp",EDGE,"E374"),sQuery(id+"F0.wireOp",EDGE,"E375"),sQuery(id+"F0.wireOp",EDGE,"E376"),sQuery(id+"F0.wireOp",EDGE,"E377"),sQuery(id+"F0.wireOp",EDGE,"E378"),sQuery(id+"F0.wireOp",EDGE,"E379"),sQuery(id+"F0.wireOp",EDGE,"E380"),sQuery(id+"F0.wireOp",EDGE,"E381"),sQuery(id+"F0.wireOp",EDGE,"E382"),sQuery(id+"F0.wireOp",EDGE,"E383"),sQuery(id+"F0.wireOp",EDGE,"E384"),sQuery(id+"F0.wireOp",EDGE,"E385"),sQuery(id+"F0.wireOp",EDGE,"E386"),sQuery(id+"F0.wireOp",EDGE,"E387"),sQuery(id+"F0.wireOp",EDGE,"E388"),sQuery(id+"F0.wireOp",EDGE,"E389"),sQuery(id+"F0.wireOp",EDGE,"E390"),sQuery(id+"F0.wireOp",EDGE,"E391"),sQuery(id+"F0.wireOp",EDGE,"E392"),sQuery(id+"F0.wireOp",EDGE,"E393"),sQuery(id+"F0.wireOp",EDGE,"E394"),sQuery(id+"F0.wireOp",EDGE,"E395"),sQuery(id+"F0.wireOp",EDGE,"E396"),sQuery(id+"F0.wireOp",EDGE,"E397"),sQuery(id+"F0.wireOp",EDGE,"E398"),sQuery(id+"F0.wireOp",EDGE,"E399"),sQuery(id+"F0.wireOp",EDGE,"E400"),sQuery(id+"F0.wireOp",EDGE,"E401"),sQuery(id+"F0.wireOp",EDGE,"E402"),sQuery(id+"F0.wireOp",EDGE,"E403"),sQuery(id+"F0.wireOp",EDGE,"E404"),sQuery(id+"F0.wireOp",EDGE,"E405"),sQuery(id+"F0.wireOp",EDGE,"E406"),sQuery(id+"F0.wireOp",EDGE,"E407"),sQuery(id+"F0.wireOp",EDGE,"E408"),sQuery(id+"F0.wireOp",EDGE,"E409"),sQuery(id+"F0.wireOp",EDGE,"E410"),sQuery(id+"F0.wireOp",EDGE,"E411"),sQuery(id+"F0.wireOp",EDGE,"E412"),sQuery(id+"F0.wireOp",EDGE,"E413"),sQuery(id+"F0.wireOp",EDGE,"E414"),sQuery(id+"F0.wireOp",EDGE,"E415"),sQuery(id+"F0.wireOp",EDGE,"E416"),sQuery(id+"F0.wireOp",EDGE,"E417"),sQuery(id+"F0.wireOp",EDGE,"E418"),sQuery(id+"F0.wireOp",EDGE,"E419"),sQuery(id+"F0.wireOp",EDGE,"E420"),sQuery(id+"F0.wireOp",EDGE,"E421"),sQuery(id+"F0.wireOp",EDGE,"E422"),sQuery(id+"F0.wireOp",EDGE,"E423"),sQuery(id+"F0.wireOp",EDGE,"E424"),sQuery(id+"F0.wireOp",EDGE,"E425"),sQuery(id+"F0.wireOp",EDGE,"E426"),sQuery(id+"F0.wireOp",EDGE,"E427"),sQuery(id+"F0.wireOp",EDGE,"E428"),sQuery(id+"F0.wireOp",EDGE,"E429"),sQuery(id+"F0.wireOp",EDGE,"E430"),sQuery(id+"F0.wireOp",EDGE,"E431"),sQuery(id+"F0.wireOp",EDGE,"E432"),sQuery(id+"F0.wireOp",EDGE,"E433"),sQuery(id+"F0.wireOp",EDGE,"E434"),sQuery(id+"F0.wireOp",EDGE,"E435"),sQuery(id+"F0.wireOp",EDGE,"E436"),sQuery(id+"F0.wireOp",EDGE,"E437"),sQuery(id+"F0.wireOp",EDGE,"E438"),sQuery(id+"F0.wireOp",EDGE,"E439"),sQuery(id+"F0.wireOp",EDGE,"E440"),sQuery(id+"F0.wireOp",EDGE,"E441")])]});
            booleanBodies(context, id + "F5", {"operationType" : BooleanOperationType.UNION, "tools" : qUnion([Q0, Q1])});
        }
        {
            var Q0;
            {var subQ1071=makeQuery(id+"F1.opExtrude","SWEPT_FACE",FACE,{"disambiguationData":[OSD([sQuery(id+"F0.wireOp",EDGE,"E2")])]});var subQ2349=sQuery(id+"F2.wireOp",EDGE,"E3450.bottom");var subQ2354=sQuery(id+"F2.wireOp",EDGE,"E3450.top");var subQ2357=sQuery(id+"F2.wireOp",EDGE,"E3450.left");var subQ2360=sQuery(id+"F2.wireOp",EDGE,"E3450.right");Q0=makeQuery(id+"F5.opBoolean","SPLIT",FACE,{"disambiguationData":[TD([subQ1071])],"derivedFrom":makeQuery(id+"F4.opBoolean","SPLIT",FACE,{"disambiguationData":[TD([subQ1071])],"derivedFrom":makeQuery(id+"F3.opExtrude","CAP_FACE",FACE,{"disambiguationData":[OSD([subQ2349,subQ2354,subQ2357,subQ2360])],"isStart":false})})});}
            var sketch = newSketch(context, id + "F6", { "sketchPlane" : qUnion([Q0])});
            skLineSegment(sketch, "E3451.bottom", {"start": v(-279.84, 102.3) * mm, "end": v(358.3, 102.3) * mm});
            skLineSegment(sketch, "E3451.top", {"start": v(-279.84, -442.08) * mm, "end": v(358.3, -442.08) * mm});
            skLineSegment(sketch, "E3451.left", {"start": v(-279.84, 102.3) * mm, "end": v(-279.84, -442.08) * mm});
            skLineSegment(sketch, "E3451.right", {"start": v(358.3, 102.3) * mm, "end": v(358.3, -442.08) * mm});
            skSolve(sketch);
        }
        {
            var Q0;
            Q0 = qSketchRegion(id + "F6", true);
            extrude(context, id + "F7", {"entities" : qUnion([Q0]), "operationType" : NewBodyOperationType.REMOVE, "endBound" : BoundingType.SYMMETRIC, "oppositeDirection" : true, "depth" : 152.4 * mm, "offsetDistance" : 25.4 * mm});
        }
    });
